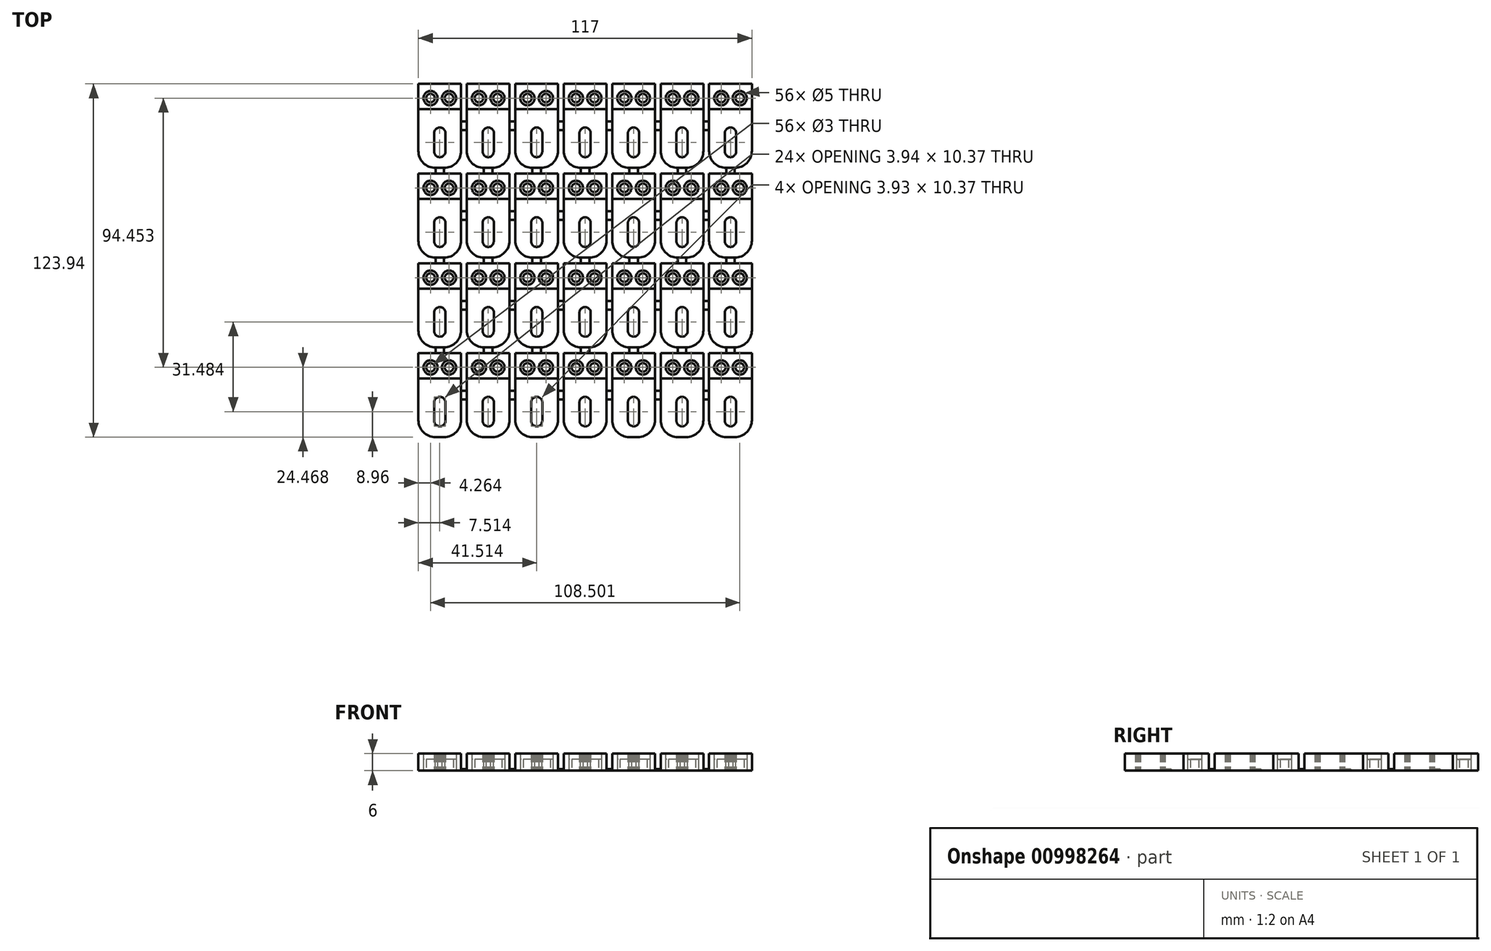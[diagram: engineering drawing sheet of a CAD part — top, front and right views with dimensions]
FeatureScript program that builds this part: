
annotation { "Feature Type Name" : "Feature", "Feature Type Description" : "" }
export const myFeature = defineFeature(function(context is Context, id is Id, definition is map)
    precondition{}
    {
        {
            var Q0;
            Q0=qCreatedBy(makeId("Top.planeOp"),FACE);
            var sketch = newSketch(context, id + "F0", { "sketchPlane" : qUnion([Q0])});
            skLineSegment(sketch, "E0", {"start": v(-52.5, 30.48) * mm, "end": v(-49.5, 30.48) * mm});
            skLineSegment(sketch, "E1", {"start": v(-49.5, 30.48) * mm, "end": v(-49.5, 32.48) * mm});
            skLineSegment(sketch, "E2", {"start": v(-49.5, 32.48) * mm, "end": v(-52.5, 32.48) * mm});
            skLineSegment(sketch, "E3", {"start": v(-52.5, 32.48) * mm, "end": v(-52.5, 30.48) * mm});
            skLineSegment(sketch, "E4", {"start": v(-58.5, 53.13) * mm, "end": v(-43.5, 53.13) * mm});
            skLineSegment(sketch, "E5", {"start": v(-43.5, 53.13) * mm, "end": v(-43.5, 61.97) * mm});
            skLineSegment(sketch, "E6", {"start": v(-43.5, 61.97) * mm, "end": v(-58.5, 61.97) * mm});
            skLineSegment(sketch, "E7", {"start": v(-58.5, 61.97) * mm, "end": v(-58.5, 53.13) * mm});
            skArc(sketch, "E8", {"start": v(-50.24, 56.95) * mm, "mid": v(-49.5, 55.18) * mm, "end": v(-47.74, 54.45) * mm});
            skArc(sketch, "E9", {"start": v(-47.74, 54.45) * mm, "mid": v(-45.97, 55.18) * mm, "end": v(-45.24, 56.95) * mm});
            skArc(sketch, "E10", {"start": v(-45.24, 56.95) * mm, "mid": v(-45.97, 58.72) * mm, "end": v(-47.74, 59.45) * mm});
            skArc(sketch, "E11", {"start": v(-47.74, 59.45) * mm, "mid": v(-49.5, 58.72) * mm, "end": v(-50.24, 56.95) * mm});
            skLineSegment(sketch, "E12", {"start": v(-58.5, 61.97) * mm, "end": v(-58.5, 38.48) * mm});
            skArc(sketch, "E13", {"start": v(-58.5, 38.48) * mm, "mid": v(-56.74, 34.24) * mm, "end": v(-52.5, 32.48) * mm});
            skLineSegment(sketch, "E14", {"start": v(-52.5, 32.48) * mm, "end": v(-49.5, 32.48) * mm});
            skArc(sketch, "E15", {"start": v(-49.5, 32.48) * mm, "mid": v(-45.26, 34.24) * mm, "end": v(-43.5, 38.48) * mm});
            skLineSegment(sketch, "E16", {"start": v(-43.5, 38.48) * mm, "end": v(-43.5, 61.97) * mm});
            skArc(sketch, "E17", {"start": v(-56.74, 56.95) * mm, "mid": v(-56, 55.18) * mm, "end": v(-54.24, 54.45) * mm});
            skArc(sketch, "E18", {"start": v(-54.24, 54.45) * mm, "mid": v(-52.47, 55.18) * mm, "end": v(-51.74, 56.95) * mm});
            skArc(sketch, "E19", {"start": v(-51.74, 56.95) * mm, "mid": v(-52.47, 58.72) * mm, "end": v(-54.24, 59.45) * mm});
            skArc(sketch, "E20", {"start": v(-54.24, 59.45) * mm, "mid": v(-56, 58.72) * mm, "end": v(-56.74, 56.95) * mm});
            skArc(sketch, "E21", {"start": v(-54.24, 58.45) * mm, "mid": v(-55.3, 58.01) * mm, "end": v(-55.74, 56.95) * mm});
            skArc(sketch, "E22", {"start": v(-55.74, 56.95) * mm, "mid": v(-55.3, 55.9) * mm, "end": v(-54.24, 55.45) * mm});
            skArc(sketch, "E23", {"start": v(-54.24, 55.45) * mm, "mid": v(-53.18, 55.9) * mm, "end": v(-52.74, 56.95) * mm});
            skArc(sketch, "E24", {"start": v(-52.74, 56.95) * mm, "mid": v(-53.18, 58.01) * mm, "end": v(-54.24, 58.45) * mm});
            skArc(sketch, "E25", {"start": v(-47.74, 58.45) * mm, "mid": v(-48.8, 58.01) * mm, "end": v(-49.24, 56.95) * mm});
            skArc(sketch, "E26", {"start": v(-49.24, 56.95) * mm, "mid": v(-48.8, 55.9) * mm, "end": v(-47.74, 55.45) * mm});
            skArc(sketch, "E27", {"start": v(-47.74, 55.45) * mm, "mid": v(-46.67, 55.9) * mm, "end": v(-46.24, 56.95) * mm});
            skArc(sketch, "E28", {"start": v(-46.24, 56.95) * mm, "mid": v(-46.67, 58.01) * mm, "end": v(-47.74, 58.45) * mm});
            skLineSegment(sketch, "E29", {"start": v(-51.27, 46.62) * mm, "end": v(-51.4, 46.6) * mm});
            skLineSegment(sketch, "E30", {"start": v(-51.4, 46.6) * mm, "end": v(-51.5, 46.58) * mm});
            skLineSegment(sketch, "E31", {"start": v(-51.5, 46.58) * mm, "end": v(-51.72, 46.5) * mm});
            skLineSegment(sketch, "E32", {"start": v(-51.72, 46.5) * mm, "end": v(-51.94, 46.4) * mm});
            skLineSegment(sketch, "E33", {"start": v(-51.94, 46.4) * mm, "end": v(-52.15, 46.27) * mm});
            skLineSegment(sketch, "E34", {"start": v(-52.15, 46.27) * mm, "end": v(-52.33, 46.12) * mm});
            skLineSegment(sketch, "E35", {"start": v(-52.33, 46.12) * mm, "end": v(-52.53, 45.92) * mm});
            skLineSegment(sketch, "E36", {"start": v(-52.53, 45.92) * mm, "end": v(-52.6, 45.8) * mm});
            skLineSegment(sketch, "E37", {"start": v(-52.6, 45.8) * mm, "end": v(-52.6, 45.8) * mm});
            skLineSegment(sketch, "E38", {"start": v(-52.6, 45.8) * mm, "end": v(-52.66, 45.7) * mm});
            skLineSegment(sketch, "E39", {"start": v(-52.66, 45.7) * mm, "end": v(-52.76, 45.53) * mm});
            skLineSegment(sketch, "E40", {"start": v(-52.76, 45.53) * mm, "end": v(-52.83, 45.34) * mm});
            skLineSegment(sketch, "E41", {"start": v(-52.83, 45.34) * mm, "end": v(-52.91, 45.1) * mm});
            skLineSegment(sketch, "E42", {"start": v(-52.91, 45.1) * mm, "end": v(-52.95, 45) * mm});
            skLineSegment(sketch, "E43", {"start": v(-52.95, 45) * mm, "end": v(-52.95, 37.9) * mm});
            skLineSegment(sketch, "E44", {"start": v(-52.95, 37.9) * mm, "end": v(-52.91, 37.81) * mm});
            skLineSegment(sketch, "E45", {"start": v(-52.91, 37.81) * mm, "end": v(-52.84, 37.58) * mm});
            skLineSegment(sketch, "E46", {"start": v(-52.84, 37.58) * mm, "end": v(-52.79, 37.43) * mm});
            skLineSegment(sketch, "E47", {"start": v(-52.79, 37.43) * mm, "end": v(-52.74, 37.31) * mm});
            skLineSegment(sketch, "E48", {"start": v(-52.74, 37.31) * mm, "end": v(-52.67, 37.2) * mm});
            skLineSegment(sketch, "E49", {"start": v(-52.67, 37.2) * mm, "end": v(-52.6, 37.11) * mm});
            skLineSegment(sketch, "E50", {"start": v(-52.6, 37.11) * mm, "end": v(-52.59, 37.1) * mm});
            skLineSegment(sketch, "E51", {"start": v(-52.59, 37.1) * mm, "end": v(-52.58, 37.07) * mm});
            skLineSegment(sketch, "E52", {"start": v(-52.58, 37.07) * mm, "end": v(-52.52, 36.98) * mm});
            skLineSegment(sketch, "E53", {"start": v(-52.52, 36.98) * mm, "end": v(-52.42, 36.87) * mm});
            skLineSegment(sketch, "E54", {"start": v(-52.42, 36.87) * mm, "end": v(-52.22, 36.68) * mm});
            skLineSegment(sketch, "E55", {"start": v(-52.22, 36.68) * mm, "end": v(-52.13, 36.62) * mm});
            skLineSegment(sketch, "E56", {"start": v(-52.13, 36.62) * mm, "end": v(-52.07, 36.58) * mm});
            skLineSegment(sketch, "E57", {"start": v(-52.07, 36.58) * mm, "end": v(-52.04, 36.56) * mm});
            skLineSegment(sketch, "E58", {"start": v(-52.04, 36.56) * mm, "end": v(-51.95, 36.51) * mm});
            skLineSegment(sketch, "E59", {"start": v(-51.95, 36.51) * mm, "end": v(-51.66, 36.37) * mm});
            skLineSegment(sketch, "E60", {"start": v(-51.66, 36.37) * mm, "end": v(-51.51, 36.32) * mm});
            skLineSegment(sketch, "E61", {"start": v(-51.51, 36.32) * mm, "end": v(-51.35, 36.29) * mm});
            skLineSegment(sketch, "E62", {"start": v(-51.35, 36.29) * mm, "end": v(-51.17, 36.27) * mm});
            skLineSegment(sketch, "E63", {"start": v(-51.17, 36.27) * mm, "end": v(-51, 36.26) * mm});
            skLineSegment(sketch, "E64", {"start": v(-51, 36.26) * mm, "end": v(-50.81, 36.27) * mm});
            skLineSegment(sketch, "E65", {"start": v(-50.81, 36.27) * mm, "end": v(-50.64, 36.29) * mm});
            skLineSegment(sketch, "E66", {"start": v(-50.64, 36.29) * mm, "end": v(-50.47, 36.32) * mm});
            skLineSegment(sketch, "E67", {"start": v(-50.47, 36.32) * mm, "end": v(-50.32, 36.37) * mm});
            skLineSegment(sketch, "E68", {"start": v(-50.32, 36.37) * mm, "end": v(-50.02, 36.5) * mm});
            skLineSegment(sketch, "E69", {"start": v(-50.02, 36.5) * mm, "end": v(-49.92, 36.56) * mm});
            skLineSegment(sketch, "E70", {"start": v(-49.92, 36.56) * mm, "end": v(-49.89, 36.6) * mm});
            skLineSegment(sketch, "E71", {"start": v(-49.89, 36.6) * mm, "end": v(-49.86, 36.6) * mm});
            skLineSegment(sketch, "E72", {"start": v(-49.86, 36.6) * mm, "end": v(-49.78, 36.66) * mm});
            skLineSegment(sketch, "E73", {"start": v(-49.78, 36.66) * mm, "end": v(-49.63, 36.8) * mm});
            skLineSegment(sketch, "E74", {"start": v(-49.63, 36.8) * mm, "end": v(-49.48, 36.94) * mm});
            skLineSegment(sketch, "E75", {"start": v(-49.48, 36.94) * mm, "end": v(-49.42, 37.02) * mm});
            skLineSegment(sketch, "E76", {"start": v(-49.42, 37.02) * mm, "end": v(-49.4, 37.08) * mm});
            skLineSegment(sketch, "E77", {"start": v(-49.4, 37.08) * mm, "end": v(-49.38, 37.1) * mm});
            skLineSegment(sketch, "E78", {"start": v(-49.38, 37.1) * mm, "end": v(-49.38, 37.1) * mm});
            skLineSegment(sketch, "E79", {"start": v(-49.38, 37.1) * mm, "end": v(-49.31, 37.19) * mm});
            skLineSegment(sketch, "E80", {"start": v(-49.31, 37.19) * mm, "end": v(-49.25, 37.27) * mm});
            skLineSegment(sketch, "E81", {"start": v(-49.25, 37.27) * mm, "end": v(-49.2, 37.4) * mm});
            skLineSegment(sketch, "E82", {"start": v(-49.2, 37.4) * mm, "end": v(-49.06, 37.8) * mm});
            skLineSegment(sketch, "E83", {"start": v(-49.06, 37.8) * mm, "end": v(-49.02, 37.94) * mm});
            skLineSegment(sketch, "E84", {"start": v(-49.02, 37.94) * mm, "end": v(-49.02, 45) * mm});
            skLineSegment(sketch, "E85", {"start": v(-49.02, 45) * mm, "end": v(-49.06, 45.1) * mm});
            skLineSegment(sketch, "E86", {"start": v(-49.06, 45.1) * mm, "end": v(-49.14, 45.34) * mm});
            skLineSegment(sketch, "E87", {"start": v(-49.14, 45.34) * mm, "end": v(-49.21, 45.53) * mm});
            skLineSegment(sketch, "E88", {"start": v(-49.21, 45.53) * mm, "end": v(-49.3, 45.7) * mm});
            skLineSegment(sketch, "E89", {"start": v(-49.3, 45.7) * mm, "end": v(-49.37, 45.8) * mm});
            skLineSegment(sketch, "E90", {"start": v(-49.37, 45.8) * mm, "end": v(-49.4, 45.86) * mm});
            skLineSegment(sketch, "E91", {"start": v(-49.4, 45.86) * mm, "end": v(-49.45, 45.92) * mm});
            skLineSegment(sketch, "E92", {"start": v(-49.45, 45.92) * mm, "end": v(-49.54, 46.02) * mm});
            skLineSegment(sketch, "E93", {"start": v(-49.54, 46.02) * mm, "end": v(-49.8, 46.26) * mm});
            skLineSegment(sketch, "E94", {"start": v(-49.8, 46.26) * mm, "end": v(-49.94, 46.35) * mm});
            skLineSegment(sketch, "E95", {"start": v(-49.94, 46.35) * mm, "end": v(-50.11, 46.44) * mm});
            skLineSegment(sketch, "E96", {"start": v(-50.11, 46.44) * mm, "end": v(-50.3, 46.52) * mm});
            skLineSegment(sketch, "E97", {"start": v(-50.3, 46.52) * mm, "end": v(-50.47, 46.58) * mm});
            skLineSegment(sketch, "E98", {"start": v(-50.47, 46.58) * mm, "end": v(-50.58, 46.6) * mm});
            skLineSegment(sketch, "E99", {"start": v(-50.58, 46.6) * mm, "end": v(-50.7, 46.62) * mm});
            skLineSegment(sketch, "E100", {"start": v(-50.7, 46.62) * mm, "end": v(-50.98, 46.63) * mm});
            skLineSegment(sketch, "E101", {"start": v(-50.98, 46.63) * mm, "end": v(-51.27, 46.62) * mm});
            skLineSegment(sketch, "E102", {"start": v(-35.5, 30.48) * mm, "end": v(-32.5, 30.48) * mm});
            skLineSegment(sketch, "E103", {"start": v(-32.5, 30.48) * mm, "end": v(-32.5, 32.48) * mm});
            skLineSegment(sketch, "E104", {"start": v(-32.5, 32.48) * mm, "end": v(-35.5, 32.48) * mm});
            skLineSegment(sketch, "E105", {"start": v(-35.5, 32.48) * mm, "end": v(-35.5, 30.48) * mm});
            skLineSegment(sketch, "E106", {"start": v(-41.5, 53.13) * mm, "end": v(-26.5, 53.13) * mm});
            skLineSegment(sketch, "E107", {"start": v(-26.5, 53.13) * mm, "end": v(-26.5, 61.97) * mm});
            skLineSegment(sketch, "E108", {"start": v(-26.5, 61.97) * mm, "end": v(-41.5, 61.97) * mm});
            skLineSegment(sketch, "E109", {"start": v(-41.5, 61.97) * mm, "end": v(-41.5, 53.13) * mm});
            skArc(sketch, "E110", {"start": v(-33.24, 56.95) * mm, "mid": v(-32.5, 55.18) * mm, "end": v(-30.74, 54.45) * mm});
            skArc(sketch, "E111", {"start": v(-30.74, 54.45) * mm, "mid": v(-28.97, 55.18) * mm, "end": v(-28.24, 56.95) * mm});
            skArc(sketch, "E112", {"start": v(-28.24, 56.95) * mm, "mid": v(-28.97, 58.72) * mm, "end": v(-30.74, 59.45) * mm});
            skArc(sketch, "E113", {"start": v(-30.74, 59.45) * mm, "mid": v(-32.5, 58.72) * mm, "end": v(-33.24, 56.95) * mm});
            skLineSegment(sketch, "E114", {"start": v(-41.5, 61.97) * mm, "end": v(-41.5, 38.48) * mm});
            skArc(sketch, "E115", {"start": v(-41.5, 38.48) * mm, "mid": v(-39.74, 34.24) * mm, "end": v(-35.5, 32.48) * mm});
            skLineSegment(sketch, "E116", {"start": v(-35.5, 32.48) * mm, "end": v(-32.5, 32.48) * mm});
            skArc(sketch, "E117", {"start": v(-32.5, 32.48) * mm, "mid": v(-28.26, 34.24) * mm, "end": v(-26.5, 38.48) * mm});
            skLineSegment(sketch, "E118", {"start": v(-26.5, 38.48) * mm, "end": v(-26.5, 61.97) * mm});
            skArc(sketch, "E119", {"start": v(-39.74, 56.95) * mm, "mid": v(-39, 55.18) * mm, "end": v(-37.24, 54.45) * mm});
            skArc(sketch, "E120", {"start": v(-37.24, 54.45) * mm, "mid": v(-35.47, 55.18) * mm, "end": v(-34.74, 56.95) * mm});
            skArc(sketch, "E121", {"start": v(-34.74, 56.95) * mm, "mid": v(-35.47, 58.72) * mm, "end": v(-37.24, 59.45) * mm});
            skArc(sketch, "E122", {"start": v(-37.24, 59.45) * mm, "mid": v(-39, 58.72) * mm, "end": v(-39.74, 56.95) * mm});
            skArc(sketch, "E123", {"start": v(-37.24, 58.45) * mm, "mid": v(-38.3, 58.01) * mm, "end": v(-38.74, 56.95) * mm});
            skArc(sketch, "E124", {"start": v(-38.74, 56.95) * mm, "mid": v(-38.3, 55.9) * mm, "end": v(-37.24, 55.45) * mm});
            skArc(sketch, "E125", {"start": v(-37.24, 55.45) * mm, "mid": v(-36.18, 55.9) * mm, "end": v(-35.74, 56.95) * mm});
            skArc(sketch, "E126", {"start": v(-35.74, 56.95) * mm, "mid": v(-36.18, 58.01) * mm, "end": v(-37.24, 58.45) * mm});
            skArc(sketch, "E127", {"start": v(-30.74, 58.45) * mm, "mid": v(-31.8, 58.01) * mm, "end": v(-32.24, 56.95) * mm});
            skArc(sketch, "E128", {"start": v(-32.24, 56.95) * mm, "mid": v(-31.8, 55.9) * mm, "end": v(-30.74, 55.45) * mm});
            skArc(sketch, "E129", {"start": v(-30.74, 55.45) * mm, "mid": v(-29.67, 55.9) * mm, "end": v(-29.24, 56.95) * mm});
            skArc(sketch, "E130", {"start": v(-29.24, 56.95) * mm, "mid": v(-29.67, 58.01) * mm, "end": v(-30.74, 58.45) * mm});
            skLineSegment(sketch, "E131", {"start": v(-34.27, 46.62) * mm, "end": v(-34.4, 46.6) * mm});
            skLineSegment(sketch, "E132", {"start": v(-34.4, 46.6) * mm, "end": v(-34.5, 46.58) * mm});
            skLineSegment(sketch, "E133", {"start": v(-34.5, 46.58) * mm, "end": v(-34.72, 46.5) * mm});
            skLineSegment(sketch, "E134", {"start": v(-34.72, 46.5) * mm, "end": v(-34.94, 46.4) * mm});
            skLineSegment(sketch, "E135", {"start": v(-34.94, 46.4) * mm, "end": v(-35.15, 46.27) * mm});
            skLineSegment(sketch, "E136", {"start": v(-35.15, 46.27) * mm, "end": v(-35.33, 46.12) * mm});
            skLineSegment(sketch, "E137", {"start": v(-35.33, 46.12) * mm, "end": v(-35.53, 45.92) * mm});
            skLineSegment(sketch, "E138", {"start": v(-35.53, 45.92) * mm, "end": v(-35.6, 45.8) * mm});
            skLineSegment(sketch, "E139", {"start": v(-35.6, 45.8) * mm, "end": v(-35.6, 45.8) * mm});
            skLineSegment(sketch, "E140", {"start": v(-35.6, 45.8) * mm, "end": v(-35.66, 45.7) * mm});
            skLineSegment(sketch, "E141", {"start": v(-35.66, 45.7) * mm, "end": v(-35.76, 45.53) * mm});
            skLineSegment(sketch, "E142", {"start": v(-35.76, 45.53) * mm, "end": v(-35.83, 45.34) * mm});
            skLineSegment(sketch, "E143", {"start": v(-35.83, 45.34) * mm, "end": v(-35.91, 45.1) * mm});
            skLineSegment(sketch, "E144", {"start": v(-35.91, 45.1) * mm, "end": v(-35.95, 45) * mm});
            skLineSegment(sketch, "E145", {"start": v(-35.95, 45) * mm, "end": v(-35.95, 37.9) * mm});
            skLineSegment(sketch, "E146", {"start": v(-35.95, 37.9) * mm, "end": v(-35.91, 37.81) * mm});
            skLineSegment(sketch, "E147", {"start": v(-35.91, 37.81) * mm, "end": v(-35.84, 37.58) * mm});
            skLineSegment(sketch, "E148", {"start": v(-35.84, 37.58) * mm, "end": v(-35.79, 37.43) * mm});
            skLineSegment(sketch, "E149", {"start": v(-35.79, 37.43) * mm, "end": v(-35.74, 37.31) * mm});
            skLineSegment(sketch, "E150", {"start": v(-35.74, 37.31) * mm, "end": v(-35.67, 37.2) * mm});
            skLineSegment(sketch, "E151", {"start": v(-35.67, 37.2) * mm, "end": v(-35.6, 37.11) * mm});
            skLineSegment(sketch, "E152", {"start": v(-35.6, 37.11) * mm, "end": v(-35.59, 37.1) * mm});
            skLineSegment(sketch, "E153", {"start": v(-35.59, 37.1) * mm, "end": v(-35.58, 37.07) * mm});
            skLineSegment(sketch, "E154", {"start": v(-35.58, 37.07) * mm, "end": v(-35.52, 36.98) * mm});
            skLineSegment(sketch, "E155", {"start": v(-35.52, 36.98) * mm, "end": v(-35.42, 36.87) * mm});
            skLineSegment(sketch, "E156", {"start": v(-35.42, 36.87) * mm, "end": v(-35.22, 36.68) * mm});
            skLineSegment(sketch, "E157", {"start": v(-35.22, 36.68) * mm, "end": v(-35.13, 36.62) * mm});
            skLineSegment(sketch, "E158", {"start": v(-35.13, 36.62) * mm, "end": v(-35.07, 36.58) * mm});
            skLineSegment(sketch, "E159", {"start": v(-35.07, 36.58) * mm, "end": v(-35.04, 36.56) * mm});
            skLineSegment(sketch, "E160", {"start": v(-35.04, 36.56) * mm, "end": v(-34.95, 36.51) * mm});
            skLineSegment(sketch, "E161", {"start": v(-34.95, 36.51) * mm, "end": v(-34.66, 36.37) * mm});
            skLineSegment(sketch, "E162", {"start": v(-34.66, 36.37) * mm, "end": v(-34.51, 36.32) * mm});
            skLineSegment(sketch, "E163", {"start": v(-34.51, 36.32) * mm, "end": v(-34.35, 36.29) * mm});
            skLineSegment(sketch, "E164", {"start": v(-34.35, 36.29) * mm, "end": v(-34.17, 36.27) * mm});
            skLineSegment(sketch, "E165", {"start": v(-34.17, 36.27) * mm, "end": v(-34, 36.26) * mm});
            skLineSegment(sketch, "E166", {"start": v(-34, 36.26) * mm, "end": v(-33.81, 36.27) * mm});
            skLineSegment(sketch, "E167", {"start": v(-33.81, 36.27) * mm, "end": v(-33.64, 36.29) * mm});
            skLineSegment(sketch, "E168", {"start": v(-33.64, 36.29) * mm, "end": v(-33.47, 36.32) * mm});
            skLineSegment(sketch, "E169", {"start": v(-33.47, 36.32) * mm, "end": v(-33.32, 36.37) * mm});
            skLineSegment(sketch, "E170", {"start": v(-33.32, 36.37) * mm, "end": v(-33.02, 36.5) * mm});
            skLineSegment(sketch, "E171", {"start": v(-33.02, 36.5) * mm, "end": v(-32.92, 36.56) * mm});
            skLineSegment(sketch, "E172", {"start": v(-32.92, 36.56) * mm, "end": v(-32.89, 36.6) * mm});
            skLineSegment(sketch, "E173", {"start": v(-32.89, 36.6) * mm, "end": v(-32.86, 36.6) * mm});
            skLineSegment(sketch, "E174", {"start": v(-32.86, 36.6) * mm, "end": v(-32.78, 36.66) * mm});
            skLineSegment(sketch, "E175", {"start": v(-32.78, 36.66) * mm, "end": v(-32.63, 36.8) * mm});
            skLineSegment(sketch, "E176", {"start": v(-32.63, 36.8) * mm, "end": v(-32.48, 36.94) * mm});
            skLineSegment(sketch, "E177", {"start": v(-32.48, 36.94) * mm, "end": v(-32.42, 37.02) * mm});
            skLineSegment(sketch, "E178", {"start": v(-32.42, 37.02) * mm, "end": v(-32.4, 37.08) * mm});
            skLineSegment(sketch, "E179", {"start": v(-32.4, 37.08) * mm, "end": v(-32.38, 37.1) * mm});
            skLineSegment(sketch, "E180", {"start": v(-32.38, 37.1) * mm, "end": v(-32.38, 37.1) * mm});
            skLineSegment(sketch, "E181", {"start": v(-32.38, 37.1) * mm, "end": v(-32.31, 37.19) * mm});
            skLineSegment(sketch, "E182", {"start": v(-32.31, 37.19) * mm, "end": v(-32.25, 37.27) * mm});
            skLineSegment(sketch, "E183", {"start": v(-32.25, 37.27) * mm, "end": v(-32.2, 37.4) * mm});
            skLineSegment(sketch, "E184", {"start": v(-32.2, 37.4) * mm, "end": v(-32.06, 37.8) * mm});
            skLineSegment(sketch, "E185", {"start": v(-32.06, 37.8) * mm, "end": v(-32.02, 37.94) * mm});
            skLineSegment(sketch, "E186", {"start": v(-32.02, 37.94) * mm, "end": v(-32.02, 45) * mm});
            skLineSegment(sketch, "E187", {"start": v(-32.02, 45) * mm, "end": v(-32.06, 45.1) * mm});
            skLineSegment(sketch, "E188", {"start": v(-32.06, 45.1) * mm, "end": v(-32.14, 45.34) * mm});
            skLineSegment(sketch, "E189", {"start": v(-32.14, 45.34) * mm, "end": v(-32.21, 45.53) * mm});
            skLineSegment(sketch, "E190", {"start": v(-32.21, 45.53) * mm, "end": v(-32.3, 45.7) * mm});
            skLineSegment(sketch, "E191", {"start": v(-32.3, 45.7) * mm, "end": v(-32.37, 45.8) * mm});
            skLineSegment(sketch, "E192", {"start": v(-32.37, 45.8) * mm, "end": v(-32.4, 45.86) * mm});
            skLineSegment(sketch, "E193", {"start": v(-32.4, 45.86) * mm, "end": v(-32.45, 45.92) * mm});
            skLineSegment(sketch, "E194", {"start": v(-32.45, 45.92) * mm, "end": v(-32.54, 46.02) * mm});
            skLineSegment(sketch, "E195", {"start": v(-32.54, 46.02) * mm, "end": v(-32.8, 46.26) * mm});
            skLineSegment(sketch, "E196", {"start": v(-32.8, 46.26) * mm, "end": v(-32.94, 46.35) * mm});
            skLineSegment(sketch, "E197", {"start": v(-32.94, 46.35) * mm, "end": v(-33.11, 46.44) * mm});
            skLineSegment(sketch, "E198", {"start": v(-33.11, 46.44) * mm, "end": v(-33.3, 46.52) * mm});
            skLineSegment(sketch, "E199", {"start": v(-33.3, 46.52) * mm, "end": v(-33.47, 46.58) * mm});
            skLineSegment(sketch, "E200", {"start": v(-33.47, 46.58) * mm, "end": v(-33.58, 46.6) * mm});
            skLineSegment(sketch, "E201", {"start": v(-33.58, 46.6) * mm, "end": v(-33.7, 46.62) * mm});
            skLineSegment(sketch, "E202", {"start": v(-33.7, 46.62) * mm, "end": v(-33.98, 46.63) * mm});
            skLineSegment(sketch, "E203", {"start": v(-33.98, 46.63) * mm, "end": v(-34.27, 46.62) * mm});
            skLineSegment(sketch, "E204", {"start": v(-43.5, 45.73) * mm, "end": v(-41.5, 45.73) * mm});
            skLineSegment(sketch, "E205", {"start": v(-41.5, 45.73) * mm, "end": v(-41.5, 48.73) * mm});
            skLineSegment(sketch, "E206", {"start": v(-41.5, 48.73) * mm, "end": v(-43.5, 48.73) * mm});
            skLineSegment(sketch, "E207", {"start": v(-43.5, 48.73) * mm, "end": v(-43.5, 45.73) * mm});
            skLineSegment(sketch, "E208", {"start": v(-18.5, 30.48) * mm, "end": v(-15.5, 30.48) * mm});
            skLineSegment(sketch, "E209", {"start": v(-15.5, 30.48) * mm, "end": v(-15.5, 32.48) * mm});
            skLineSegment(sketch, "E210", {"start": v(-15.5, 32.48) * mm, "end": v(-18.5, 32.48) * mm});
            skLineSegment(sketch, "E211", {"start": v(-18.5, 32.48) * mm, "end": v(-18.5, 30.48) * mm});
            skLineSegment(sketch, "E212", {"start": v(-24.5, 53.13) * mm, "end": v(-9.5, 53.13) * mm});
            skLineSegment(sketch, "E213", {"start": v(-9.5, 53.13) * mm, "end": v(-9.5, 61.97) * mm});
            skLineSegment(sketch, "E214", {"start": v(-9.5, 61.97) * mm, "end": v(-24.5, 61.97) * mm});
            skLineSegment(sketch, "E215", {"start": v(-24.5, 61.97) * mm, "end": v(-24.5, 53.13) * mm});
            skArc(sketch, "E216", {"start": v(-16.24, 56.95) * mm, "mid": v(-15.5, 55.18) * mm, "end": v(-13.74, 54.45) * mm});
            skArc(sketch, "E217", {"start": v(-13.74, 54.45) * mm, "mid": v(-11.97, 55.18) * mm, "end": v(-11.24, 56.95) * mm});
            skArc(sketch, "E218", {"start": v(-11.24, 56.95) * mm, "mid": v(-11.97, 58.72) * mm, "end": v(-13.74, 59.45) * mm});
            skArc(sketch, "E219", {"start": v(-13.74, 59.45) * mm, "mid": v(-15.5, 58.72) * mm, "end": v(-16.24, 56.95) * mm});
            skLineSegment(sketch, "E220", {"start": v(-24.5, 61.97) * mm, "end": v(-24.5, 38.48) * mm});
            skArc(sketch, "E221", {"start": v(-24.5, 38.48) * mm, "mid": v(-22.74, 34.24) * mm, "end": v(-18.5, 32.48) * mm});
            skLineSegment(sketch, "E222", {"start": v(-18.5, 32.48) * mm, "end": v(-15.5, 32.48) * mm});
            skArc(sketch, "E223", {"start": v(-15.5, 32.48) * mm, "mid": v(-11.26, 34.24) * mm, "end": v(-9.5, 38.48) * mm});
            skLineSegment(sketch, "E224", {"start": v(-9.5, 38.48) * mm, "end": v(-9.5, 61.97) * mm});
            skArc(sketch, "E225", {"start": v(-22.74, 56.95) * mm, "mid": v(-22, 55.18) * mm, "end": v(-20.24, 54.45) * mm});
            skArc(sketch, "E226", {"start": v(-20.24, 54.45) * mm, "mid": v(-18.47, 55.18) * mm, "end": v(-17.74, 56.95) * mm});
            skArc(sketch, "E227", {"start": v(-17.74, 56.95) * mm, "mid": v(-18.47, 58.72) * mm, "end": v(-20.24, 59.45) * mm});
            skArc(sketch, "E228", {"start": v(-20.24, 59.45) * mm, "mid": v(-22, 58.72) * mm, "end": v(-22.74, 56.95) * mm});
            skArc(sketch, "E229", {"start": v(-20.24, 58.45) * mm, "mid": v(-21.3, 58.01) * mm, "end": v(-21.74, 56.95) * mm});
            skArc(sketch, "E230", {"start": v(-21.74, 56.95) * mm, "mid": v(-21.3, 55.9) * mm, "end": v(-20.24, 55.45) * mm});
            skArc(sketch, "E231", {"start": v(-20.24, 55.45) * mm, "mid": v(-19.18, 55.9) * mm, "end": v(-18.74, 56.95) * mm});
            skArc(sketch, "E232", {"start": v(-18.74, 56.95) * mm, "mid": v(-19.18, 58.01) * mm, "end": v(-20.24, 58.45) * mm});
            skArc(sketch, "E233", {"start": v(-13.74, 58.45) * mm, "mid": v(-14.8, 58.01) * mm, "end": v(-15.24, 56.95) * mm});
            skArc(sketch, "E234", {"start": v(-15.24, 56.95) * mm, "mid": v(-14.8, 55.9) * mm, "end": v(-13.74, 55.45) * mm});
            skArc(sketch, "E235", {"start": v(-13.74, 55.45) * mm, "mid": v(-12.67, 55.9) * mm, "end": v(-12.24, 56.95) * mm});
            skArc(sketch, "E236", {"start": v(-12.24, 56.95) * mm, "mid": v(-12.67, 58.01) * mm, "end": v(-13.74, 58.45) * mm});
            skLineSegment(sketch, "E237", {"start": v(-17.27, 46.62) * mm, "end": v(-17.4, 46.6) * mm});
            skLineSegment(sketch, "E238", {"start": v(-17.4, 46.6) * mm, "end": v(-17.5, 46.58) * mm});
            skLineSegment(sketch, "E239", {"start": v(-17.5, 46.58) * mm, "end": v(-17.72, 46.5) * mm});
            skLineSegment(sketch, "E240", {"start": v(-17.72, 46.5) * mm, "end": v(-17.94, 46.4) * mm});
            skLineSegment(sketch, "E241", {"start": v(-17.94, 46.4) * mm, "end": v(-18.15, 46.27) * mm});
            skLineSegment(sketch, "E242", {"start": v(-18.15, 46.27) * mm, "end": v(-18.33, 46.12) * mm});
            skLineSegment(sketch, "E243", {"start": v(-18.33, 46.12) * mm, "end": v(-18.53, 45.92) * mm});
            skLineSegment(sketch, "E244", {"start": v(-18.53, 45.92) * mm, "end": v(-18.6, 45.8) * mm});
            skLineSegment(sketch, "E245", {"start": v(-18.6, 45.8) * mm, "end": v(-18.6, 45.8) * mm});
            skLineSegment(sketch, "E246", {"start": v(-18.6, 45.8) * mm, "end": v(-18.66, 45.7) * mm});
            skLineSegment(sketch, "E247", {"start": v(-18.66, 45.7) * mm, "end": v(-18.76, 45.53) * mm});
            skLineSegment(sketch, "E248", {"start": v(-18.76, 45.53) * mm, "end": v(-18.83, 45.34) * mm});
            skLineSegment(sketch, "E249", {"start": v(-18.83, 45.34) * mm, "end": v(-18.91, 45.1) * mm});
            skLineSegment(sketch, "E250", {"start": v(-18.91, 45.1) * mm, "end": v(-18.95, 45) * mm});
            skLineSegment(sketch, "E251", {"start": v(-18.95, 45) * mm, "end": v(-18.95, 37.9) * mm});
            skLineSegment(sketch, "E252", {"start": v(-18.95, 37.9) * mm, "end": v(-18.91, 37.81) * mm});
            skLineSegment(sketch, "E253", {"start": v(-18.91, 37.81) * mm, "end": v(-18.84, 37.58) * mm});
            skLineSegment(sketch, "E254", {"start": v(-18.84, 37.58) * mm, "end": v(-18.79, 37.43) * mm});
            skLineSegment(sketch, "E255", {"start": v(-18.79, 37.43) * mm, "end": v(-18.74, 37.31) * mm});
            skLineSegment(sketch, "E256", {"start": v(-18.74, 37.31) * mm, "end": v(-18.67, 37.2) * mm});
            skLineSegment(sketch, "E257", {"start": v(-18.67, 37.2) * mm, "end": v(-18.6, 37.11) * mm});
            skLineSegment(sketch, "E258", {"start": v(-18.6, 37.11) * mm, "end": v(-18.59, 37.1) * mm});
            skLineSegment(sketch, "E259", {"start": v(-18.59, 37.1) * mm, "end": v(-18.58, 37.07) * mm});
            skLineSegment(sketch, "E260", {"start": v(-18.58, 37.07) * mm, "end": v(-18.52, 36.98) * mm});
            skLineSegment(sketch, "E261", {"start": v(-18.52, 36.98) * mm, "end": v(-18.42, 36.87) * mm});
            skLineSegment(sketch, "E262", {"start": v(-18.42, 36.87) * mm, "end": v(-18.22, 36.68) * mm});
            skLineSegment(sketch, "E263", {"start": v(-18.22, 36.68) * mm, "end": v(-18.13, 36.62) * mm});
            skLineSegment(sketch, "E264", {"start": v(-18.13, 36.62) * mm, "end": v(-18.07, 36.58) * mm});
            skLineSegment(sketch, "E265", {"start": v(-18.07, 36.58) * mm, "end": v(-18.04, 36.56) * mm});
            skLineSegment(sketch, "E266", {"start": v(-18.04, 36.56) * mm, "end": v(-17.95, 36.51) * mm});
            skLineSegment(sketch, "E267", {"start": v(-17.95, 36.51) * mm, "end": v(-17.66, 36.37) * mm});
            skLineSegment(sketch, "E268", {"start": v(-17.66, 36.37) * mm, "end": v(-17.51, 36.32) * mm});
            skLineSegment(sketch, "E269", {"start": v(-17.51, 36.32) * mm, "end": v(-17.35, 36.29) * mm});
            skLineSegment(sketch, "E270", {"start": v(-17.35, 36.29) * mm, "end": v(-17.17, 36.27) * mm});
            skLineSegment(sketch, "E271", {"start": v(-17.17, 36.27) * mm, "end": v(-17, 36.26) * mm});
            skLineSegment(sketch, "E272", {"start": v(-17, 36.26) * mm, "end": v(-16.81, 36.27) * mm});
            skLineSegment(sketch, "E273", {"start": v(-16.81, 36.27) * mm, "end": v(-16.64, 36.29) * mm});
            skLineSegment(sketch, "E274", {"start": v(-16.64, 36.29) * mm, "end": v(-16.47, 36.32) * mm});
            skLineSegment(sketch, "E275", {"start": v(-16.47, 36.32) * mm, "end": v(-16.32, 36.37) * mm});
            skLineSegment(sketch, "E276", {"start": v(-16.32, 36.37) * mm, "end": v(-16.02, 36.5) * mm});
            skLineSegment(sketch, "E277", {"start": v(-16.02, 36.5) * mm, "end": v(-15.92, 36.56) * mm});
            skLineSegment(sketch, "E278", {"start": v(-15.92, 36.56) * mm, "end": v(-15.89, 36.6) * mm});
            skLineSegment(sketch, "E279", {"start": v(-15.89, 36.6) * mm, "end": v(-15.86, 36.6) * mm});
            skLineSegment(sketch, "E280", {"start": v(-15.86, 36.6) * mm, "end": v(-15.78, 36.66) * mm});
            skLineSegment(sketch, "E281", {"start": v(-15.78, 36.66) * mm, "end": v(-15.63, 36.8) * mm});
            skLineSegment(sketch, "E282", {"start": v(-15.63, 36.8) * mm, "end": v(-15.48, 36.94) * mm});
            skLineSegment(sketch, "E283", {"start": v(-15.48, 36.94) * mm, "end": v(-15.42, 37.02) * mm});
            skLineSegment(sketch, "E284", {"start": v(-15.42, 37.02) * mm, "end": v(-15.4, 37.08) * mm});
            skLineSegment(sketch, "E285", {"start": v(-15.4, 37.08) * mm, "end": v(-15.38, 37.1) * mm});
            skLineSegment(sketch, "E286", {"start": v(-15.38, 37.1) * mm, "end": v(-15.38, 37.1) * mm});
            skLineSegment(sketch, "E287", {"start": v(-15.38, 37.1) * mm, "end": v(-15.31, 37.19) * mm});
            skLineSegment(sketch, "E288", {"start": v(-15.31, 37.19) * mm, "end": v(-15.25, 37.27) * mm});
            skLineSegment(sketch, "E289", {"start": v(-15.25, 37.27) * mm, "end": v(-15.2, 37.4) * mm});
            skLineSegment(sketch, "E290", {"start": v(-15.2, 37.4) * mm, "end": v(-15.06, 37.8) * mm});
            skLineSegment(sketch, "E291", {"start": v(-15.06, 37.8) * mm, "end": v(-15.02, 37.94) * mm});
            skLineSegment(sketch, "E292", {"start": v(-15.02, 37.94) * mm, "end": v(-15.02, 45) * mm});
            skLineSegment(sketch, "E293", {"start": v(-15.02, 45) * mm, "end": v(-15.06, 45.1) * mm});
            skLineSegment(sketch, "E294", {"start": v(-15.06, 45.1) * mm, "end": v(-15.14, 45.34) * mm});
            skLineSegment(sketch, "E295", {"start": v(-15.14, 45.34) * mm, "end": v(-15.21, 45.53) * mm});
            skLineSegment(sketch, "E296", {"start": v(-15.21, 45.53) * mm, "end": v(-15.3, 45.7) * mm});
            skLineSegment(sketch, "E297", {"start": v(-15.3, 45.7) * mm, "end": v(-15.37, 45.8) * mm});
            skLineSegment(sketch, "E298", {"start": v(-15.37, 45.8) * mm, "end": v(-15.4, 45.86) * mm});
            skLineSegment(sketch, "E299", {"start": v(-15.4, 45.86) * mm, "end": v(-15.45, 45.92) * mm});
            skLineSegment(sketch, "E300", {"start": v(-15.45, 45.92) * mm, "end": v(-15.54, 46.02) * mm});
            skLineSegment(sketch, "E301", {"start": v(-15.54, 46.02) * mm, "end": v(-15.8, 46.26) * mm});
            skLineSegment(sketch, "E302", {"start": v(-15.8, 46.26) * mm, "end": v(-15.94, 46.35) * mm});
            skLineSegment(sketch, "E303", {"start": v(-15.94, 46.35) * mm, "end": v(-16.11, 46.44) * mm});
            skLineSegment(sketch, "E304", {"start": v(-16.11, 46.44) * mm, "end": v(-16.3, 46.52) * mm});
            skLineSegment(sketch, "E305", {"start": v(-16.3, 46.52) * mm, "end": v(-16.47, 46.58) * mm});
            skLineSegment(sketch, "E306", {"start": v(-16.47, 46.58) * mm, "end": v(-16.58, 46.6) * mm});
            skLineSegment(sketch, "E307", {"start": v(-16.58, 46.6) * mm, "end": v(-16.7, 46.62) * mm});
            skLineSegment(sketch, "E308", {"start": v(-16.7, 46.62) * mm, "end": v(-16.98, 46.63) * mm});
            skLineSegment(sketch, "E309", {"start": v(-16.98, 46.63) * mm, "end": v(-17.27, 46.62) * mm});
            skLineSegment(sketch, "E310", {"start": v(-26.5, 45.73) * mm, "end": v(-24.5, 45.73) * mm});
            skLineSegment(sketch, "E311", {"start": v(-24.5, 45.73) * mm, "end": v(-24.5, 48.73) * mm});
            skLineSegment(sketch, "E312", {"start": v(-24.5, 48.73) * mm, "end": v(-26.5, 48.73) * mm});
            skLineSegment(sketch, "E313", {"start": v(-26.5, 48.73) * mm, "end": v(-26.5, 45.73) * mm});
            skLineSegment(sketch, "E314", {"start": v(15.5, 30.48) * mm, "end": v(18.5, 30.48) * mm});
            skLineSegment(sketch, "E315", {"start": v(18.5, 30.48) * mm, "end": v(18.5, 32.48) * mm});
            skLineSegment(sketch, "E316", {"start": v(18.5, 32.48) * mm, "end": v(15.5, 32.48) * mm});
            skLineSegment(sketch, "E317", {"start": v(15.5, 32.48) * mm, "end": v(15.5, 30.48) * mm});
            skLineSegment(sketch, "E318", {"start": v(9.5, 53.13) * mm, "end": v(24.5, 53.13) * mm});
            skLineSegment(sketch, "E319", {"start": v(24.5, 53.13) * mm, "end": v(24.5, 61.97) * mm});
            skLineSegment(sketch, "E320", {"start": v(24.5, 61.97) * mm, "end": v(9.5, 61.97) * mm});
            skLineSegment(sketch, "E321", {"start": v(9.5, 61.97) * mm, "end": v(9.5, 53.13) * mm});
            skArc(sketch, "E322", {"start": v(17.76, 56.95) * mm, "mid": v(18.5, 55.18) * mm, "end": v(20.26, 54.45) * mm});
            skArc(sketch, "E323", {"start": v(20.26, 54.45) * mm, "mid": v(22.03, 55.18) * mm, "end": v(22.76, 56.95) * mm});
            skArc(sketch, "E324", {"start": v(22.76, 56.95) * mm, "mid": v(22.03, 58.72) * mm, "end": v(20.26, 59.45) * mm});
            skArc(sketch, "E325", {"start": v(20.26, 59.45) * mm, "mid": v(18.5, 58.72) * mm, "end": v(17.76, 56.95) * mm});
            skLineSegment(sketch, "E326", {"start": v(9.5, 61.97) * mm, "end": v(9.5, 38.48) * mm});
            skArc(sketch, "E327", {"start": v(9.5, 38.48) * mm, "mid": v(11.26, 34.24) * mm, "end": v(15.5, 32.48) * mm});
            skLineSegment(sketch, "E328", {"start": v(15.5, 32.48) * mm, "end": v(18.5, 32.48) * mm});
            skArc(sketch, "E329", {"start": v(18.5, 32.48) * mm, "mid": v(22.74, 34.24) * mm, "end": v(24.5, 38.48) * mm});
            skLineSegment(sketch, "E330", {"start": v(24.5, 38.48) * mm, "end": v(24.5, 61.97) * mm});
            skArc(sketch, "E331", {"start": v(11.26, 56.95) * mm, "mid": v(12, 55.18) * mm, "end": v(13.76, 54.45) * mm});
            skArc(sketch, "E332", {"start": v(13.76, 54.45) * mm, "mid": v(15.53, 55.18) * mm, "end": v(16.26, 56.95) * mm});
            skArc(sketch, "E333", {"start": v(16.26, 56.95) * mm, "mid": v(15.53, 58.72) * mm, "end": v(13.76, 59.45) * mm});
            skArc(sketch, "E334", {"start": v(13.76, 59.45) * mm, "mid": v(12, 58.72) * mm, "end": v(11.26, 56.95) * mm});
            skArc(sketch, "E335", {"start": v(13.76, 58.45) * mm, "mid": v(12.7, 58.01) * mm, "end": v(12.26, 56.95) * mm});
            skArc(sketch, "E336", {"start": v(12.26, 56.95) * mm, "mid": v(12.7, 55.9) * mm, "end": v(13.76, 55.45) * mm});
            skArc(sketch, "E337", {"start": v(13.76, 55.45) * mm, "mid": v(14.82, 55.9) * mm, "end": v(15.26, 56.95) * mm});
            skArc(sketch, "E338", {"start": v(15.26, 56.95) * mm, "mid": v(14.82, 58.01) * mm, "end": v(13.76, 58.45) * mm});
            skArc(sketch, "E339", {"start": v(20.27, 58.45) * mm, "mid": v(19.2, 58.01) * mm, "end": v(18.77, 56.95) * mm});
            skArc(sketch, "E340", {"start": v(18.77, 56.95) * mm, "mid": v(19.2, 55.9) * mm, "end": v(20.27, 55.45) * mm});
            skArc(sketch, "E341", {"start": v(20.27, 55.45) * mm, "mid": v(21.33, 55.9) * mm, "end": v(21.77, 56.95) * mm});
            skArc(sketch, "E342", {"start": v(21.77, 56.95) * mm, "mid": v(21.33, 58.01) * mm, "end": v(20.27, 58.45) * mm});
            skLineSegment(sketch, "E343", {"start": v(16.73, 46.62) * mm, "end": v(16.6, 46.6) * mm});
            skLineSegment(sketch, "E344", {"start": v(16.6, 46.6) * mm, "end": v(16.5, 46.58) * mm});
            skLineSegment(sketch, "E345", {"start": v(16.5, 46.58) * mm, "end": v(16.28, 46.5) * mm});
            skLineSegment(sketch, "E346", {"start": v(16.28, 46.5) * mm, "end": v(16.06, 46.4) * mm});
            skLineSegment(sketch, "E347", {"start": v(16.06, 46.4) * mm, "end": v(15.85, 46.27) * mm});
            skLineSegment(sketch, "E348", {"start": v(15.85, 46.27) * mm, "end": v(15.67, 46.12) * mm});
            skLineSegment(sketch, "E349", {"start": v(15.67, 46.12) * mm, "end": v(15.47, 45.92) * mm});
            skLineSegment(sketch, "E350", {"start": v(15.47, 45.92) * mm, "end": v(15.4, 45.8) * mm});
            skLineSegment(sketch, "E351", {"start": v(15.4, 45.8) * mm, "end": v(15.4, 45.8) * mm});
            skLineSegment(sketch, "E352", {"start": v(15.4, 45.8) * mm, "end": v(15.34, 45.7) * mm});
            skLineSegment(sketch, "E353", {"start": v(15.34, 45.7) * mm, "end": v(15.24, 45.53) * mm});
            skLineSegment(sketch, "E354", {"start": v(15.24, 45.53) * mm, "end": v(15.17, 45.34) * mm});
            skLineSegment(sketch, "E355", {"start": v(15.17, 45.34) * mm, "end": v(15.09, 45.1) * mm});
            skLineSegment(sketch, "E356", {"start": v(15.09, 45.1) * mm, "end": v(15.05, 45) * mm});
            skLineSegment(sketch, "E357", {"start": v(15.05, 45) * mm, "end": v(15.05, 37.9) * mm});
            skLineSegment(sketch, "E358", {"start": v(15.05, 37.9) * mm, "end": v(15.09, 37.81) * mm});
            skLineSegment(sketch, "E359", {"start": v(15.09, 37.81) * mm, "end": v(15.16, 37.58) * mm});
            skLineSegment(sketch, "E360", {"start": v(15.16, 37.58) * mm, "end": v(15.21, 37.43) * mm});
            skLineSegment(sketch, "E361", {"start": v(15.21, 37.43) * mm, "end": v(15.26, 37.31) * mm});
            skLineSegment(sketch, "E362", {"start": v(15.26, 37.31) * mm, "end": v(15.33, 37.2) * mm});
            skLineSegment(sketch, "E363", {"start": v(15.33, 37.2) * mm, "end": v(15.4, 37.11) * mm});
            skLineSegment(sketch, "E364", {"start": v(15.4, 37.11) * mm, "end": v(15.41, 37.1) * mm});
            skLineSegment(sketch, "E365", {"start": v(15.41, 37.1) * mm, "end": v(15.42, 37.07) * mm});
            skLineSegment(sketch, "E366", {"start": v(15.42, 37.07) * mm, "end": v(15.48, 36.98) * mm});
            skLineSegment(sketch, "E367", {"start": v(15.48, 36.98) * mm, "end": v(15.58, 36.87) * mm});
            skLineSegment(sketch, "E368", {"start": v(15.58, 36.87) * mm, "end": v(15.78, 36.68) * mm});
            skLineSegment(sketch, "E369", {"start": v(15.78, 36.68) * mm, "end": v(15.87, 36.62) * mm});
            skLineSegment(sketch, "E370", {"start": v(15.87, 36.62) * mm, "end": v(15.93, 36.58) * mm});
            skLineSegment(sketch, "E371", {"start": v(15.93, 36.58) * mm, "end": v(15.96, 36.56) * mm});
            skLineSegment(sketch, "E372", {"start": v(15.96, 36.56) * mm, "end": v(16.05, 36.51) * mm});
            skLineSegment(sketch, "E373", {"start": v(16.05, 36.51) * mm, "end": v(16.34, 36.37) * mm});
            skLineSegment(sketch, "E374", {"start": v(16.34, 36.37) * mm, "end": v(16.49, 36.32) * mm});
            skLineSegment(sketch, "E375", {"start": v(16.49, 36.32) * mm, "end": v(16.65, 36.29) * mm});
            skLineSegment(sketch, "E376", {"start": v(16.65, 36.29) * mm, "end": v(16.83, 36.27) * mm});
            skLineSegment(sketch, "E377", {"start": v(16.83, 36.27) * mm, "end": v(17, 36.26) * mm});
            skLineSegment(sketch, "E378", {"start": v(17, 36.26) * mm, "end": v(17.19, 36.27) * mm});
            skLineSegment(sketch, "E379", {"start": v(17.19, 36.27) * mm, "end": v(17.36, 36.29) * mm});
            skLineSegment(sketch, "E380", {"start": v(17.36, 36.29) * mm, "end": v(17.53, 36.32) * mm});
            skLineSegment(sketch, "E381", {"start": v(17.53, 36.32) * mm, "end": v(17.68, 36.37) * mm});
            skLineSegment(sketch, "E382", {"start": v(17.68, 36.37) * mm, "end": v(17.98, 36.5) * mm});
            skLineSegment(sketch, "E383", {"start": v(17.98, 36.5) * mm, "end": v(18.08, 36.56) * mm});
            skLineSegment(sketch, "E384", {"start": v(18.08, 36.56) * mm, "end": v(18.11, 36.6) * mm});
            skLineSegment(sketch, "E385", {"start": v(18.11, 36.6) * mm, "end": v(18.14, 36.6) * mm});
            skLineSegment(sketch, "E386", {"start": v(18.14, 36.6) * mm, "end": v(18.22, 36.66) * mm});
            skLineSegment(sketch, "E387", {"start": v(18.22, 36.66) * mm, "end": v(18.37, 36.8) * mm});
            skLineSegment(sketch, "E388", {"start": v(18.37, 36.8) * mm, "end": v(18.52, 36.94) * mm});
            skLineSegment(sketch, "E389", {"start": v(18.52, 36.94) * mm, "end": v(18.58, 37.02) * mm});
            skLineSegment(sketch, "E390", {"start": v(18.58, 37.02) * mm, "end": v(18.6, 37.08) * mm});
            skLineSegment(sketch, "E391", {"start": v(18.6, 37.08) * mm, "end": v(18.62, 37.1) * mm});
            skLineSegment(sketch, "E392", {"start": v(18.62, 37.1) * mm, "end": v(18.62, 37.1) * mm});
            skLineSegment(sketch, "E393", {"start": v(18.62, 37.1) * mm, "end": v(18.69, 37.19) * mm});
            skLineSegment(sketch, "E394", {"start": v(18.69, 37.19) * mm, "end": v(18.75, 37.27) * mm});
            skLineSegment(sketch, "E395", {"start": v(18.75, 37.27) * mm, "end": v(18.8, 37.4) * mm});
            skLineSegment(sketch, "E396", {"start": v(18.8, 37.4) * mm, "end": v(18.94, 37.8) * mm});
            skLineSegment(sketch, "E397", {"start": v(18.94, 37.8) * mm, "end": v(18.98, 37.94) * mm});
            skLineSegment(sketch, "E398", {"start": v(18.98, 37.94) * mm, "end": v(18.98, 45) * mm});
            skLineSegment(sketch, "E399", {"start": v(18.98, 45) * mm, "end": v(18.94, 45.1) * mm});
            skLineSegment(sketch, "E400", {"start": v(18.94, 45.1) * mm, "end": v(18.86, 45.34) * mm});
            skLineSegment(sketch, "E401", {"start": v(18.86, 45.34) * mm, "end": v(18.79, 45.53) * mm});
            skLineSegment(sketch, "E402", {"start": v(18.79, 45.53) * mm, "end": v(18.7, 45.7) * mm});
            skLineSegment(sketch, "E403", {"start": v(18.7, 45.7) * mm, "end": v(18.63, 45.8) * mm});
            skLineSegment(sketch, "E404", {"start": v(18.63, 45.8) * mm, "end": v(18.6, 45.86) * mm});
            skLineSegment(sketch, "E405", {"start": v(18.6, 45.86) * mm, "end": v(18.55, 45.92) * mm});
            skLineSegment(sketch, "E406", {"start": v(18.55, 45.92) * mm, "end": v(18.46, 46.02) * mm});
            skLineSegment(sketch, "E407", {"start": v(18.46, 46.02) * mm, "end": v(18.2, 46.26) * mm});
            skLineSegment(sketch, "E408", {"start": v(18.2, 46.26) * mm, "end": v(18.06, 46.35) * mm});
            skLineSegment(sketch, "E409", {"start": v(18.06, 46.35) * mm, "end": v(17.89, 46.44) * mm});
            skLineSegment(sketch, "E410", {"start": v(17.89, 46.44) * mm, "end": v(17.7, 46.52) * mm});
            skLineSegment(sketch, "E411", {"start": v(17.7, 46.52) * mm, "end": v(17.53, 46.58) * mm});
            skLineSegment(sketch, "E412", {"start": v(17.53, 46.58) * mm, "end": v(17.42, 46.6) * mm});
            skLineSegment(sketch, "E413", {"start": v(17.42, 46.6) * mm, "end": v(17.3, 46.62) * mm});
            skLineSegment(sketch, "E414", {"start": v(17.3, 46.62) * mm, "end": v(17.02, 46.63) * mm});
            skLineSegment(sketch, "E415", {"start": v(17.02, 46.63) * mm, "end": v(16.73, 46.62) * mm});
            skLineSegment(sketch, "E416", {"start": v(7.5, 45.73) * mm, "end": v(9.5, 45.73) * mm});
            skLineSegment(sketch, "E417", {"start": v(9.5, 45.73) * mm, "end": v(9.5, 48.73) * mm});
            skLineSegment(sketch, "E418", {"start": v(9.5, 48.73) * mm, "end": v(7.5, 48.73) * mm});
            skLineSegment(sketch, "E419", {"start": v(7.5, 48.73) * mm, "end": v(7.5, 45.73) * mm});
            skLineSegment(sketch, "E420", {"start": v(32.5, 30.48) * mm, "end": v(35.5, 30.48) * mm});
            skLineSegment(sketch, "E421", {"start": v(35.5, 30.48) * mm, "end": v(35.5, 32.48) * mm});
            skLineSegment(sketch, "E422", {"start": v(35.5, 32.48) * mm, "end": v(32.5, 32.48) * mm});
            skLineSegment(sketch, "E423", {"start": v(32.5, 32.48) * mm, "end": v(32.5, 30.48) * mm});
            skLineSegment(sketch, "E424", {"start": v(26.5, 53.13) * mm, "end": v(41.5, 53.13) * mm});
            skLineSegment(sketch, "E425", {"start": v(41.5, 53.13) * mm, "end": v(41.5, 61.97) * mm});
            skLineSegment(sketch, "E426", {"start": v(41.5, 61.97) * mm, "end": v(26.5, 61.97) * mm});
            skLineSegment(sketch, "E427", {"start": v(26.5, 61.97) * mm, "end": v(26.5, 53.13) * mm});
            skArc(sketch, "E428", {"start": v(34.76, 56.95) * mm, "mid": v(35.5, 55.18) * mm, "end": v(37.26, 54.45) * mm});
            skArc(sketch, "E429", {"start": v(37.26, 54.45) * mm, "mid": v(39.03, 55.18) * mm, "end": v(39.76, 56.95) * mm});
            skArc(sketch, "E430", {"start": v(39.76, 56.95) * mm, "mid": v(39.03, 58.72) * mm, "end": v(37.26, 59.45) * mm});
            skArc(sketch, "E431", {"start": v(37.26, 59.45) * mm, "mid": v(35.5, 58.72) * mm, "end": v(34.76, 56.95) * mm});
            skLineSegment(sketch, "E432", {"start": v(26.5, 61.97) * mm, "end": v(26.5, 38.48) * mm});
            skArc(sketch, "E433", {"start": v(26.5, 38.48) * mm, "mid": v(28.26, 34.24) * mm, "end": v(32.5, 32.48) * mm});
            skLineSegment(sketch, "E434", {"start": v(32.5, 32.48) * mm, "end": v(35.5, 32.48) * mm});
            skArc(sketch, "E435", {"start": v(35.5, 32.48) * mm, "mid": v(39.74, 34.24) * mm, "end": v(41.5, 38.48) * mm});
            skLineSegment(sketch, "E436", {"start": v(41.5, 38.48) * mm, "end": v(41.5, 61.97) * mm});
            skArc(sketch, "E437", {"start": v(28.26, 56.95) * mm, "mid": v(29, 55.18) * mm, "end": v(30.76, 54.45) * mm});
            skArc(sketch, "E438", {"start": v(30.76, 54.45) * mm, "mid": v(32.53, 55.18) * mm, "end": v(33.26, 56.95) * mm});
            skArc(sketch, "E439", {"start": v(33.26, 56.95) * mm, "mid": v(32.53, 58.72) * mm, "end": v(30.76, 59.45) * mm});
            skArc(sketch, "E440", {"start": v(30.76, 59.45) * mm, "mid": v(29, 58.72) * mm, "end": v(28.26, 56.95) * mm});
            skArc(sketch, "E441", {"start": v(30.76, 58.45) * mm, "mid": v(29.7, 58.01) * mm, "end": v(29.26, 56.95) * mm});
            skArc(sketch, "E442", {"start": v(29.26, 56.95) * mm, "mid": v(29.7, 55.9) * mm, "end": v(30.76, 55.45) * mm});
            skArc(sketch, "E443", {"start": v(30.76, 55.45) * mm, "mid": v(31.82, 55.9) * mm, "end": v(32.26, 56.95) * mm});
            skArc(sketch, "E444", {"start": v(32.26, 56.95) * mm, "mid": v(31.82, 58.01) * mm, "end": v(30.76, 58.45) * mm});
            skArc(sketch, "E445", {"start": v(37.27, 58.45) * mm, "mid": v(36.2, 58.01) * mm, "end": v(35.77, 56.95) * mm});
            skArc(sketch, "E446", {"start": v(35.77, 56.95) * mm, "mid": v(36.2, 55.9) * mm, "end": v(37.27, 55.45) * mm});
            skArc(sketch, "E447", {"start": v(37.27, 55.45) * mm, "mid": v(38.33, 55.9) * mm, "end": v(38.77, 56.95) * mm});
            skArc(sketch, "E448", {"start": v(38.77, 56.95) * mm, "mid": v(38.33, 58.01) * mm, "end": v(37.27, 58.45) * mm});
            skLineSegment(sketch, "E449", {"start": v(33.73, 46.62) * mm, "end": v(33.6, 46.6) * mm});
            skLineSegment(sketch, "E450", {"start": v(33.6, 46.6) * mm, "end": v(33.5, 46.58) * mm});
            skLineSegment(sketch, "E451", {"start": v(33.5, 46.58) * mm, "end": v(33.28, 46.5) * mm});
            skLineSegment(sketch, "E452", {"start": v(33.28, 46.5) * mm, "end": v(33.06, 46.4) * mm});
            skLineSegment(sketch, "E453", {"start": v(33.06, 46.4) * mm, "end": v(32.85, 46.27) * mm});
            skLineSegment(sketch, "E454", {"start": v(32.85, 46.27) * mm, "end": v(32.67, 46.12) * mm});
            skLineSegment(sketch, "E455", {"start": v(32.67, 46.12) * mm, "end": v(32.47, 45.92) * mm});
            skLineSegment(sketch, "E456", {"start": v(32.47, 45.92) * mm, "end": v(32.4, 45.8) * mm});
            skLineSegment(sketch, "E457", {"start": v(32.4, 45.8) * mm, "end": v(32.4, 45.8) * mm});
            skLineSegment(sketch, "E458", {"start": v(32.4, 45.8) * mm, "end": v(32.34, 45.7) * mm});
            skLineSegment(sketch, "E459", {"start": v(32.34, 45.7) * mm, "end": v(32.24, 45.53) * mm});
            skLineSegment(sketch, "E460", {"start": v(32.24, 45.53) * mm, "end": v(32.17, 45.34) * mm});
            skLineSegment(sketch, "E461", {"start": v(32.17, 45.34) * mm, "end": v(32.09, 45.1) * mm});
            skLineSegment(sketch, "E462", {"start": v(32.09, 45.1) * mm, "end": v(32.05, 45) * mm});
            skLineSegment(sketch, "E463", {"start": v(32.05, 45) * mm, "end": v(32.05, 37.9) * mm});
            skLineSegment(sketch, "E464", {"start": v(32.05, 37.9) * mm, "end": v(32.09, 37.81) * mm});
            skLineSegment(sketch, "E465", {"start": v(32.09, 37.81) * mm, "end": v(32.16, 37.58) * mm});
            skLineSegment(sketch, "E466", {"start": v(32.16, 37.58) * mm, "end": v(32.21, 37.43) * mm});
            skLineSegment(sketch, "E467", {"start": v(32.21, 37.43) * mm, "end": v(32.26, 37.31) * mm});
            skLineSegment(sketch, "E468", {"start": v(32.26, 37.31) * mm, "end": v(32.33, 37.2) * mm});
            skLineSegment(sketch, "E469", {"start": v(32.33, 37.2) * mm, "end": v(32.4, 37.11) * mm});
            skLineSegment(sketch, "E470", {"start": v(32.4, 37.11) * mm, "end": v(32.41, 37.1) * mm});
            skLineSegment(sketch, "E471", {"start": v(32.41, 37.1) * mm, "end": v(32.42, 37.07) * mm});
            skLineSegment(sketch, "E472", {"start": v(32.42, 37.07) * mm, "end": v(32.48, 36.98) * mm});
            skLineSegment(sketch, "E473", {"start": v(32.48, 36.98) * mm, "end": v(32.58, 36.87) * mm});
            skLineSegment(sketch, "E474", {"start": v(32.58, 36.87) * mm, "end": v(32.78, 36.68) * mm});
            skLineSegment(sketch, "E475", {"start": v(32.78, 36.68) * mm, "end": v(32.87, 36.62) * mm});
            skLineSegment(sketch, "E476", {"start": v(32.87, 36.62) * mm, "end": v(32.93, 36.58) * mm});
            skLineSegment(sketch, "E477", {"start": v(32.93, 36.58) * mm, "end": v(32.96, 36.56) * mm});
            skLineSegment(sketch, "E478", {"start": v(32.96, 36.56) * mm, "end": v(33.05, 36.51) * mm});
            skLineSegment(sketch, "E479", {"start": v(33.05, 36.51) * mm, "end": v(33.34, 36.37) * mm});
            skLineSegment(sketch, "E480", {"start": v(33.34, 36.37) * mm, "end": v(33.49, 36.32) * mm});
            skLineSegment(sketch, "E481", {"start": v(33.49, 36.32) * mm, "end": v(33.65, 36.29) * mm});
            skLineSegment(sketch, "E482", {"start": v(33.65, 36.29) * mm, "end": v(33.83, 36.27) * mm});
            skLineSegment(sketch, "E483", {"start": v(33.83, 36.27) * mm, "end": v(34, 36.26) * mm});
            skLineSegment(sketch, "E484", {"start": v(34, 36.26) * mm, "end": v(34.19, 36.27) * mm});
            skLineSegment(sketch, "E485", {"start": v(34.19, 36.27) * mm, "end": v(34.36, 36.29) * mm});
            skLineSegment(sketch, "E486", {"start": v(34.36, 36.29) * mm, "end": v(34.53, 36.32) * mm});
            skLineSegment(sketch, "E487", {"start": v(34.53, 36.32) * mm, "end": v(34.68, 36.37) * mm});
            skLineSegment(sketch, "E488", {"start": v(34.68, 36.37) * mm, "end": v(34.98, 36.5) * mm});
            skLineSegment(sketch, "E489", {"start": v(34.98, 36.5) * mm, "end": v(35.08, 36.56) * mm});
            skLineSegment(sketch, "E490", {"start": v(35.08, 36.56) * mm, "end": v(35.11, 36.6) * mm});
            skLineSegment(sketch, "E491", {"start": v(35.11, 36.6) * mm, "end": v(35.14, 36.6) * mm});
            skLineSegment(sketch, "E492", {"start": v(35.14, 36.6) * mm, "end": v(35.22, 36.66) * mm});
            skLineSegment(sketch, "E493", {"start": v(35.22, 36.66) * mm, "end": v(35.37, 36.8) * mm});
            skLineSegment(sketch, "E494", {"start": v(35.37, 36.8) * mm, "end": v(35.52, 36.94) * mm});
            skLineSegment(sketch, "E495", {"start": v(35.52, 36.94) * mm, "end": v(35.58, 37.02) * mm});
            skLineSegment(sketch, "E496", {"start": v(35.58, 37.02) * mm, "end": v(35.6, 37.08) * mm});
            skLineSegment(sketch, "E497", {"start": v(35.6, 37.08) * mm, "end": v(35.62, 37.1) * mm});
            skLineSegment(sketch, "E498", {"start": v(35.62, 37.1) * mm, "end": v(35.62, 37.1) * mm});
            skLineSegment(sketch, "E499", {"start": v(35.62, 37.1) * mm, "end": v(35.69, 37.19) * mm});
            skLineSegment(sketch, "E500", {"start": v(35.69, 37.19) * mm, "end": v(35.75, 37.27) * mm});
            skLineSegment(sketch, "E501", {"start": v(35.75, 37.27) * mm, "end": v(35.8, 37.4) * mm});
            skLineSegment(sketch, "E502", {"start": v(35.8, 37.4) * mm, "end": v(35.94, 37.8) * mm});
            skLineSegment(sketch, "E503", {"start": v(35.94, 37.8) * mm, "end": v(35.98, 37.94) * mm});
            skLineSegment(sketch, "E504", {"start": v(35.98, 37.94) * mm, "end": v(35.98, 45) * mm});
            skLineSegment(sketch, "E505", {"start": v(35.98, 45) * mm, "end": v(35.94, 45.1) * mm});
            skLineSegment(sketch, "E506", {"start": v(35.94, 45.1) * mm, "end": v(35.86, 45.34) * mm});
            skLineSegment(sketch, "E507", {"start": v(35.86, 45.34) * mm, "end": v(35.79, 45.53) * mm});
            skLineSegment(sketch, "E508", {"start": v(35.79, 45.53) * mm, "end": v(35.7, 45.7) * mm});
            skLineSegment(sketch, "E509", {"start": v(35.7, 45.7) * mm, "end": v(35.63, 45.8) * mm});
            skLineSegment(sketch, "E510", {"start": v(35.63, 45.8) * mm, "end": v(35.6, 45.86) * mm});
            skLineSegment(sketch, "E511", {"start": v(35.6, 45.86) * mm, "end": v(35.55, 45.92) * mm});
            skLineSegment(sketch, "E512", {"start": v(35.55, 45.92) * mm, "end": v(35.46, 46.02) * mm});
            skLineSegment(sketch, "E513", {"start": v(35.46, 46.02) * mm, "end": v(35.2, 46.26) * mm});
            skLineSegment(sketch, "E514", {"start": v(35.2, 46.26) * mm, "end": v(35.06, 46.35) * mm});
            skLineSegment(sketch, "E515", {"start": v(35.06, 46.35) * mm, "end": v(34.89, 46.44) * mm});
            skLineSegment(sketch, "E516", {"start": v(34.89, 46.44) * mm, "end": v(34.7, 46.52) * mm});
            skLineSegment(sketch, "E517", {"start": v(34.7, 46.52) * mm, "end": v(34.53, 46.58) * mm});
            skLineSegment(sketch, "E518", {"start": v(34.53, 46.58) * mm, "end": v(34.42, 46.6) * mm});
            skLineSegment(sketch, "E519", {"start": v(34.42, 46.6) * mm, "end": v(34.3, 46.62) * mm});
            skLineSegment(sketch, "E520", {"start": v(34.3, 46.62) * mm, "end": v(34.02, 46.63) * mm});
            skLineSegment(sketch, "E521", {"start": v(34.02, 46.63) * mm, "end": v(33.73, 46.62) * mm});
            skLineSegment(sketch, "E522", {"start": v(24.5, 45.73) * mm, "end": v(26.5, 45.73) * mm});
            skLineSegment(sketch, "E523", {"start": v(26.5, 45.73) * mm, "end": v(26.5, 48.73) * mm});
            skLineSegment(sketch, "E524", {"start": v(26.5, 48.73) * mm, "end": v(24.5, 48.73) * mm});
            skLineSegment(sketch, "E525", {"start": v(24.5, 48.73) * mm, "end": v(24.5, 45.73) * mm});
            skLineSegment(sketch, "E526", {"start": v(-1.5, 30.48) * mm, "end": v(1.5, 30.48) * mm});
            skLineSegment(sketch, "E527", {"start": v(1.5, 30.48) * mm, "end": v(1.5, 32.48) * mm});
            skLineSegment(sketch, "E528", {"start": v(1.5, 32.48) * mm, "end": v(-1.5, 32.48) * mm});
            skLineSegment(sketch, "E529", {"start": v(-1.5, 32.48) * mm, "end": v(-1.5, 30.48) * mm});
            skLineSegment(sketch, "E530", {"start": v(-7.5, 53.13) * mm, "end": v(7.5, 53.13) * mm});
            skLineSegment(sketch, "E531", {"start": v(7.5, 53.13) * mm, "end": v(7.5, 61.97) * mm});
            skLineSegment(sketch, "E532", {"start": v(7.5, 61.97) * mm, "end": v(-7.5, 61.97) * mm});
            skLineSegment(sketch, "E533", {"start": v(-7.5, 61.97) * mm, "end": v(-7.5, 53.13) * mm});
            skArc(sketch, "E534", {"start": v(0.76, 56.95) * mm, "mid": v(1.5, 55.18) * mm, "end": v(3.26, 54.45) * mm});
            skArc(sketch, "E535", {"start": v(3.26, 54.45) * mm, "mid": v(5.03, 55.18) * mm, "end": v(5.76, 56.95) * mm});
            skArc(sketch, "E536", {"start": v(5.76, 56.95) * mm, "mid": v(5.03, 58.72) * mm, "end": v(3.26, 59.45) * mm});
            skArc(sketch, "E537", {"start": v(3.26, 59.45) * mm, "mid": v(1.5, 58.72) * mm, "end": v(0.76, 56.95) * mm});
            skLineSegment(sketch, "E538", {"start": v(-7.5, 61.97) * mm, "end": v(-7.5, 38.48) * mm});
            skArc(sketch, "E539", {"start": v(-7.5, 38.48) * mm, "mid": v(-5.74, 34.24) * mm, "end": v(-1.5, 32.48) * mm});
            skLineSegment(sketch, "E540", {"start": v(-1.5, 32.48) * mm, "end": v(1.5, 32.48) * mm});
            skArc(sketch, "E541", {"start": v(1.5, 32.48) * mm, "mid": v(5.74, 34.24) * mm, "end": v(7.5, 38.48) * mm});
            skLineSegment(sketch, "E542", {"start": v(7.5, 38.48) * mm, "end": v(7.5, 61.97) * mm});
            skArc(sketch, "E543", {"start": v(-5.74, 56.95) * mm, "mid": v(-5, 55.18) * mm, "end": v(-3.24, 54.45) * mm});
            skArc(sketch, "E544", {"start": v(-3.24, 54.45) * mm, "mid": v(-1.47, 55.18) * mm, "end": v(-0.74, 56.95) * mm});
            skArc(sketch, "E545", {"start": v(-0.74, 56.95) * mm, "mid": v(-1.47, 58.72) * mm, "end": v(-3.24, 59.45) * mm});
            skArc(sketch, "E546", {"start": v(-3.24, 59.45) * mm, "mid": v(-5, 58.72) * mm, "end": v(-5.74, 56.95) * mm});
            skArc(sketch, "E547", {"start": v(-3.24, 58.45) * mm, "mid": v(-4.3, 58.01) * mm, "end": v(-4.74, 56.95) * mm});
            skArc(sketch, "E548", {"start": v(-4.74, 56.95) * mm, "mid": v(-4.3, 55.9) * mm, "end": v(-3.24, 55.45) * mm});
            skArc(sketch, "E549", {"start": v(-3.24, 55.45) * mm, "mid": v(-2.18, 55.9) * mm, "end": v(-1.74, 56.95) * mm});
            skArc(sketch, "E550", {"start": v(-1.74, 56.95) * mm, "mid": v(-2.18, 58.01) * mm, "end": v(-3.24, 58.45) * mm});
            skArc(sketch, "E551", {"start": v(3.26, 58.45) * mm, "mid": v(2.2, 58.01) * mm, "end": v(1.76, 56.95) * mm});
            skArc(sketch, "E552", {"start": v(1.76, 56.95) * mm, "mid": v(2.2, 55.9) * mm, "end": v(3.26, 55.45) * mm});
            skArc(sketch, "E553", {"start": v(3.26, 55.45) * mm, "mid": v(4.33, 55.9) * mm, "end": v(4.76, 56.95) * mm});
            skArc(sketch, "E554", {"start": v(4.76, 56.95) * mm, "mid": v(4.33, 58.01) * mm, "end": v(3.26, 58.45) * mm});
            skLineSegment(sketch, "E555", {"start": v(-0.27, 46.62) * mm, "end": v(-0.4, 46.6) * mm});
            skLineSegment(sketch, "E556", {"start": v(-0.4, 46.6) * mm, "end": v(-0.5, 46.58) * mm});
            skLineSegment(sketch, "E557", {"start": v(-0.5, 46.58) * mm, "end": v(-0.72, 46.5) * mm});
            skLineSegment(sketch, "E558", {"start": v(-0.72, 46.5) * mm, "end": v(-0.94, 46.4) * mm});
            skLineSegment(sketch, "E559", {"start": v(-0.94, 46.4) * mm, "end": v(-1.15, 46.27) * mm});
            skLineSegment(sketch, "E560", {"start": v(-1.15, 46.27) * mm, "end": v(-1.33, 46.12) * mm});
            skLineSegment(sketch, "E561", {"start": v(-1.33, 46.12) * mm, "end": v(-1.53, 45.92) * mm});
            skLineSegment(sketch, "E562", {"start": v(-1.53, 45.92) * mm, "end": v(-1.6, 45.8) * mm});
            skLineSegment(sketch, "E563", {"start": v(-1.6, 45.8) * mm, "end": v(-1.6, 45.8) * mm});
            skLineSegment(sketch, "E564", {"start": v(-1.6, 45.8) * mm, "end": v(-1.66, 45.7) * mm});
            skLineSegment(sketch, "E565", {"start": v(-1.66, 45.7) * mm, "end": v(-1.76, 45.53) * mm});
            skLineSegment(sketch, "E566", {"start": v(-1.76, 45.53) * mm, "end": v(-1.83, 45.34) * mm});
            skLineSegment(sketch, "E567", {"start": v(-1.83, 45.34) * mm, "end": v(-1.91, 45.1) * mm});
            skLineSegment(sketch, "E568", {"start": v(-1.91, 45.1) * mm, "end": v(-1.95, 45) * mm});
            skLineSegment(sketch, "E569", {"start": v(-1.95, 45) * mm, "end": v(-1.95, 37.9) * mm});
            skLineSegment(sketch, "E570", {"start": v(-1.95, 37.9) * mm, "end": v(-1.91, 37.81) * mm});
            skLineSegment(sketch, "E571", {"start": v(-1.91, 37.81) * mm, "end": v(-1.84, 37.58) * mm});
            skLineSegment(sketch, "E572", {"start": v(-1.84, 37.58) * mm, "end": v(-1.79, 37.43) * mm});
            skLineSegment(sketch, "E573", {"start": v(-1.79, 37.43) * mm, "end": v(-1.74, 37.31) * mm});
            skLineSegment(sketch, "E574", {"start": v(-1.74, 37.31) * mm, "end": v(-1.67, 37.2) * mm});
            skLineSegment(sketch, "E575", {"start": v(-1.67, 37.2) * mm, "end": v(-1.6, 37.11) * mm});
            skLineSegment(sketch, "E576", {"start": v(-1.6, 37.11) * mm, "end": v(-1.59, 37.1) * mm});
            skLineSegment(sketch, "E577", {"start": v(-1.59, 37.1) * mm, "end": v(-1.58, 37.07) * mm});
            skLineSegment(sketch, "E578", {"start": v(-1.58, 37.07) * mm, "end": v(-1.52, 36.98) * mm});
            skLineSegment(sketch, "E579", {"start": v(-1.52, 36.98) * mm, "end": v(-1.42, 36.87) * mm});
            skLineSegment(sketch, "E580", {"start": v(-1.42, 36.87) * mm, "end": v(-1.22, 36.68) * mm});
            skLineSegment(sketch, "E581", {"start": v(-1.22, 36.68) * mm, "end": v(-1.13, 36.62) * mm});
            skLineSegment(sketch, "E582", {"start": v(-1.13, 36.62) * mm, "end": v(-1.07, 36.58) * mm});
            skLineSegment(sketch, "E583", {"start": v(-1.07, 36.58) * mm, "end": v(-1.04, 36.56) * mm});
            skLineSegment(sketch, "E584", {"start": v(-1.04, 36.56) * mm, "end": v(-0.95, 36.51) * mm});
            skLineSegment(sketch, "E585", {"start": v(-0.95, 36.51) * mm, "end": v(-0.66, 36.37) * mm});
            skLineSegment(sketch, "E586", {"start": v(-0.66, 36.37) * mm, "end": v(-0.51, 36.32) * mm});
            skLineSegment(sketch, "E587", {"start": v(-0.51, 36.32) * mm, "end": v(-0.35, 36.29) * mm});
            skLineSegment(sketch, "E588", {"start": v(-0.35, 36.29) * mm, "end": v(-0.17, 36.27) * mm});
            skLineSegment(sketch, "E589", {"start": v(-0.17, 36.27) * mm, "end": v(0, 36.26) * mm});
            skLineSegment(sketch, "E590", {"start": v(0, 36.26) * mm, "end": v(0.19, 36.27) * mm});
            skLineSegment(sketch, "E591", {"start": v(0.19, 36.27) * mm, "end": v(0.36, 36.29) * mm});
            skLineSegment(sketch, "E592", {"start": v(0.36, 36.29) * mm, "end": v(0.53, 36.32) * mm});
            skLineSegment(sketch, "E593", {"start": v(0.53, 36.32) * mm, "end": v(0.68, 36.37) * mm});
            skLineSegment(sketch, "E594", {"start": v(0.68, 36.37) * mm, "end": v(0.98, 36.5) * mm});
            skLineSegment(sketch, "E595", {"start": v(0.98, 36.5) * mm, "end": v(1.08, 36.56) * mm});
            skLineSegment(sketch, "E596", {"start": v(1.08, 36.56) * mm, "end": v(1.11, 36.6) * mm});
            skLineSegment(sketch, "E597", {"start": v(1.11, 36.6) * mm, "end": v(1.14, 36.6) * mm});
            skLineSegment(sketch, "E598", {"start": v(1.14, 36.6) * mm, "end": v(1.22, 36.66) * mm});
            skLineSegment(sketch, "E599", {"start": v(1.22, 36.66) * mm, "end": v(1.37, 36.8) * mm});
            skLineSegment(sketch, "E600", {"start": v(1.37, 36.8) * mm, "end": v(1.52, 36.94) * mm});
            skLineSegment(sketch, "E601", {"start": v(1.52, 36.94) * mm, "end": v(1.58, 37.02) * mm});
            skLineSegment(sketch, "E602", {"start": v(1.58, 37.02) * mm, "end": v(1.6, 37.08) * mm});
            skLineSegment(sketch, "E603", {"start": v(1.6, 37.08) * mm, "end": v(1.62, 37.1) * mm});
            skLineSegment(sketch, "E604", {"start": v(1.62, 37.1) * mm, "end": v(1.62, 37.1) * mm});
            skLineSegment(sketch, "E605", {"start": v(1.62, 37.1) * mm, "end": v(1.69, 37.19) * mm});
            skLineSegment(sketch, "E606", {"start": v(1.69, 37.19) * mm, "end": v(1.75, 37.27) * mm});
            skLineSegment(sketch, "E607", {"start": v(1.75, 37.27) * mm, "end": v(1.8, 37.4) * mm});
            skLineSegment(sketch, "E608", {"start": v(1.8, 37.4) * mm, "end": v(1.94, 37.8) * mm});
            skLineSegment(sketch, "E609", {"start": v(1.94, 37.8) * mm, "end": v(1.98, 37.94) * mm});
            skLineSegment(sketch, "E610", {"start": v(1.98, 37.94) * mm, "end": v(1.98, 45) * mm});
            skLineSegment(sketch, "E611", {"start": v(1.98, 45) * mm, "end": v(1.94, 45.1) * mm});
            skLineSegment(sketch, "E612", {"start": v(1.94, 45.1) * mm, "end": v(1.86, 45.34) * mm});
            skLineSegment(sketch, "E613", {"start": v(1.86, 45.34) * mm, "end": v(1.79, 45.53) * mm});
            skLineSegment(sketch, "E614", {"start": v(1.79, 45.53) * mm, "end": v(1.7, 45.7) * mm});
            skLineSegment(sketch, "E615", {"start": v(1.7, 45.7) * mm, "end": v(1.63, 45.8) * mm});
            skLineSegment(sketch, "E616", {"start": v(1.63, 45.8) * mm, "end": v(1.6, 45.86) * mm});
            skLineSegment(sketch, "E617", {"start": v(1.6, 45.86) * mm, "end": v(1.55, 45.92) * mm});
            skLineSegment(sketch, "E618", {"start": v(1.55, 45.92) * mm, "end": v(1.46, 46.02) * mm});
            skLineSegment(sketch, "E619", {"start": v(1.46, 46.02) * mm, "end": v(1.2, 46.26) * mm});
            skLineSegment(sketch, "E620", {"start": v(1.2, 46.26) * mm, "end": v(1.06, 46.35) * mm});
            skLineSegment(sketch, "E621", {"start": v(1.06, 46.35) * mm, "end": v(0.89, 46.44) * mm});
            skLineSegment(sketch, "E622", {"start": v(0.89, 46.44) * mm, "end": v(0.7, 46.52) * mm});
            skLineSegment(sketch, "E623", {"start": v(0.7, 46.52) * mm, "end": v(0.53, 46.58) * mm});
            skLineSegment(sketch, "E624", {"start": v(0.53, 46.58) * mm, "end": v(0.42, 46.6) * mm});
            skLineSegment(sketch, "E625", {"start": v(0.42, 46.6) * mm, "end": v(0.3, 46.62) * mm});
            skLineSegment(sketch, "E626", {"start": v(0.3, 46.62) * mm, "end": v(0.02, 46.63) * mm});
            skLineSegment(sketch, "E627", {"start": v(0.02, 46.63) * mm, "end": v(-0.27, 46.62) * mm});
            skLineSegment(sketch, "E628", {"start": v(-9.5, 45.73) * mm, "end": v(-7.5, 45.73) * mm});
            skLineSegment(sketch, "E629", {"start": v(-7.5, 45.73) * mm, "end": v(-7.5, 48.73) * mm});
            skLineSegment(sketch, "E630", {"start": v(-7.5, 48.73) * mm, "end": v(-9.5, 48.73) * mm});
            skLineSegment(sketch, "E631", {"start": v(-9.5, 48.73) * mm, "end": v(-9.5, 45.73) * mm});
            skLineSegment(sketch, "E632", {"start": v(-52.5, -1) * mm, "end": v(-49.5, -1) * mm});
            skLineSegment(sketch, "E633", {"start": v(-49.5, -1) * mm, "end": v(-49.5, 1) * mm});
            skLineSegment(sketch, "E634", {"start": v(-49.5, 1) * mm, "end": v(-52.5, 1) * mm});
            skLineSegment(sketch, "E635", {"start": v(-52.5, 1) * mm, "end": v(-52.5, -1) * mm});
            skLineSegment(sketch, "E636", {"start": v(-58.5, 21.64) * mm, "end": v(-43.5, 21.64) * mm});
            skLineSegment(sketch, "E637", {"start": v(-43.5, 21.64) * mm, "end": v(-43.5, 30.48) * mm});
            skLineSegment(sketch, "E638", {"start": v(-43.5, 30.48) * mm, "end": v(-58.5, 30.48) * mm});
            skLineSegment(sketch, "E639", {"start": v(-58.5, 30.48) * mm, "end": v(-58.5, 21.64) * mm});
            skArc(sketch, "E640", {"start": v(-50.24, 25.47) * mm, "mid": v(-49.5, 23.7) * mm, "end": v(-47.74, 22.97) * mm});
            skArc(sketch, "E641", {"start": v(-47.74, 22.97) * mm, "mid": v(-45.97, 23.7) * mm, "end": v(-45.24, 25.47) * mm});
            skArc(sketch, "E642", {"start": v(-45.24, 25.47) * mm, "mid": v(-45.97, 27.23) * mm, "end": v(-47.74, 27.97) * mm});
            skArc(sketch, "E643", {"start": v(-47.74, 27.97) * mm, "mid": v(-49.5, 27.23) * mm, "end": v(-50.24, 25.47) * mm});
            skLineSegment(sketch, "E644", {"start": v(-58.5, 30.48) * mm, "end": v(-58.5, 7) * mm});
            skArc(sketch, "E645", {"start": v(-58.5, 7) * mm, "mid": v(-56.74, 2.76) * mm, "end": v(-52.5, 1) * mm});
            skLineSegment(sketch, "E646", {"start": v(-52.5, 1) * mm, "end": v(-49.5, 1) * mm});
            skArc(sketch, "E647", {"start": v(-49.5, 1) * mm, "mid": v(-45.26, 2.76) * mm, "end": v(-43.5, 7) * mm});
            skLineSegment(sketch, "E648", {"start": v(-43.5, 7) * mm, "end": v(-43.5, 30.48) * mm});
            skArc(sketch, "E649", {"start": v(-56.74, 25.47) * mm, "mid": v(-56, 23.7) * mm, "end": v(-54.24, 22.97) * mm});
            skArc(sketch, "E650", {"start": v(-54.24, 22.97) * mm, "mid": v(-52.47, 23.7) * mm, "end": v(-51.74, 25.47) * mm});
            skArc(sketch, "E651", {"start": v(-51.74, 25.47) * mm, "mid": v(-52.47, 27.23) * mm, "end": v(-54.24, 27.97) * mm});
            skArc(sketch, "E652", {"start": v(-54.24, 27.97) * mm, "mid": v(-56, 27.23) * mm, "end": v(-56.74, 25.47) * mm});
            skArc(sketch, "E653", {"start": v(-54.24, 26.97) * mm, "mid": v(-55.3, 26.53) * mm, "end": v(-55.74, 25.47) * mm});
            skArc(sketch, "E654", {"start": v(-55.74, 25.47) * mm, "mid": v(-55.3, 24.4) * mm, "end": v(-54.24, 23.97) * mm});
            skArc(sketch, "E655", {"start": v(-54.24, 23.97) * mm, "mid": v(-53.18, 24.4) * mm, "end": v(-52.74, 25.47) * mm});
            skArc(sketch, "E656", {"start": v(-52.74, 25.47) * mm, "mid": v(-53.18, 26.53) * mm, "end": v(-54.24, 26.97) * mm});
            skArc(sketch, "E657", {"start": v(-47.74, 26.97) * mm, "mid": v(-48.8, 26.53) * mm, "end": v(-49.24, 25.47) * mm});
            skArc(sketch, "E658", {"start": v(-49.24, 25.47) * mm, "mid": v(-48.8, 24.4) * mm, "end": v(-47.74, 23.97) * mm});
            skArc(sketch, "E659", {"start": v(-47.74, 23.97) * mm, "mid": v(-46.67, 24.4) * mm, "end": v(-46.24, 25.47) * mm});
            skArc(sketch, "E660", {"start": v(-46.24, 25.47) * mm, "mid": v(-46.67, 26.53) * mm, "end": v(-47.74, 26.97) * mm});
            skLineSegment(sketch, "E661", {"start": v(-51.27, 15.13) * mm, "end": v(-51.4, 15.12) * mm});
            skLineSegment(sketch, "E662", {"start": v(-51.4, 15.12) * mm, "end": v(-51.5, 15.1) * mm});
            skLineSegment(sketch, "E663", {"start": v(-51.5, 15.1) * mm, "end": v(-51.72, 15.02) * mm});
            skLineSegment(sketch, "E664", {"start": v(-51.72, 15.02) * mm, "end": v(-51.94, 14.91) * mm});
            skLineSegment(sketch, "E665", {"start": v(-51.94, 14.91) * mm, "end": v(-52.15, 14.78) * mm});
            skLineSegment(sketch, "E666", {"start": v(-52.15, 14.78) * mm, "end": v(-52.33, 14.63) * mm});
            skLineSegment(sketch, "E667", {"start": v(-52.33, 14.63) * mm, "end": v(-52.53, 14.44) * mm});
            skLineSegment(sketch, "E668", {"start": v(-52.53, 14.44) * mm, "end": v(-52.6, 14.32) * mm});
            skLineSegment(sketch, "E669", {"start": v(-52.6, 14.32) * mm, "end": v(-52.6, 14.31) * mm});
            skLineSegment(sketch, "E670", {"start": v(-52.6, 14.31) * mm, "end": v(-52.66, 14.21) * mm});
            skLineSegment(sketch, "E671", {"start": v(-52.66, 14.21) * mm, "end": v(-52.76, 14.04) * mm});
            skLineSegment(sketch, "E672", {"start": v(-52.76, 14.04) * mm, "end": v(-52.83, 13.86) * mm});
            skLineSegment(sketch, "E673", {"start": v(-52.83, 13.86) * mm, "end": v(-52.91, 13.61) * mm});
            skLineSegment(sketch, "E674", {"start": v(-52.91, 13.61) * mm, "end": v(-52.95, 13.51) * mm});
            skLineSegment(sketch, "E675", {"start": v(-52.95, 13.51) * mm, "end": v(-52.95, 6.42) * mm});
            skLineSegment(sketch, "E676", {"start": v(-52.95, 6.42) * mm, "end": v(-52.91, 6.33) * mm});
            skLineSegment(sketch, "E677", {"start": v(-52.91, 6.33) * mm, "end": v(-52.84, 6.1) * mm});
            skLineSegment(sketch, "E678", {"start": v(-52.84, 6.1) * mm, "end": v(-52.79, 5.95) * mm});
            skLineSegment(sketch, "E679", {"start": v(-52.79, 5.95) * mm, "end": v(-52.74, 5.83) * mm});
            skLineSegment(sketch, "E680", {"start": v(-52.74, 5.83) * mm, "end": v(-52.67, 5.72) * mm});
            skLineSegment(sketch, "E681", {"start": v(-52.67, 5.72) * mm, "end": v(-52.6, 5.63) * mm});
            skLineSegment(sketch, "E682", {"start": v(-52.6, 5.63) * mm, "end": v(-52.59, 5.62) * mm});
            skLineSegment(sketch, "E683", {"start": v(-52.59, 5.62) * mm, "end": v(-52.58, 5.58) * mm});
            skLineSegment(sketch, "E684", {"start": v(-52.58, 5.58) * mm, "end": v(-52.52, 5.5) * mm});
            skLineSegment(sketch, "E685", {"start": v(-52.52, 5.5) * mm, "end": v(-52.42, 5.39) * mm});
            skLineSegment(sketch, "E686", {"start": v(-52.42, 5.39) * mm, "end": v(-52.22, 5.2) * mm});
            skLineSegment(sketch, "E687", {"start": v(-52.22, 5.2) * mm, "end": v(-52.13, 5.13) * mm});
            skLineSegment(sketch, "E688", {"start": v(-52.13, 5.13) * mm, "end": v(-52.07, 5.1) * mm});
            skLineSegment(sketch, "E689", {"start": v(-52.07, 5.1) * mm, "end": v(-52.04, 5.08) * mm});
            skLineSegment(sketch, "E690", {"start": v(-52.04, 5.08) * mm, "end": v(-51.95, 5.03) * mm});
            skLineSegment(sketch, "E691", {"start": v(-51.95, 5.03) * mm, "end": v(-51.66, 4.89) * mm});
            skLineSegment(sketch, "E692", {"start": v(-51.66, 4.89) * mm, "end": v(-51.51, 4.84) * mm});
            skLineSegment(sketch, "E693", {"start": v(-51.51, 4.84) * mm, "end": v(-51.35, 4.8) * mm});
            skLineSegment(sketch, "E694", {"start": v(-51.35, 4.8) * mm, "end": v(-51.17, 4.78) * mm});
            skLineSegment(sketch, "E695", {"start": v(-51.17, 4.78) * mm, "end": v(-51, 4.78) * mm});
            skLineSegment(sketch, "E696", {"start": v(-51, 4.78) * mm, "end": v(-50.81, 4.78) * mm});
            skLineSegment(sketch, "E697", {"start": v(-50.81, 4.78) * mm, "end": v(-50.64, 4.8) * mm});
            skLineSegment(sketch, "E698", {"start": v(-50.64, 4.8) * mm, "end": v(-50.47, 4.84) * mm});
            skLineSegment(sketch, "E699", {"start": v(-50.47, 4.84) * mm, "end": v(-50.32, 4.89) * mm});
            skLineSegment(sketch, "E700", {"start": v(-50.32, 4.89) * mm, "end": v(-50.02, 5.02) * mm});
            skLineSegment(sketch, "E701", {"start": v(-50.02, 5.02) * mm, "end": v(-49.92, 5.08) * mm});
            skLineSegment(sketch, "E702", {"start": v(-49.92, 5.08) * mm, "end": v(-49.89, 5.11) * mm});
            skLineSegment(sketch, "E703", {"start": v(-49.89, 5.11) * mm, "end": v(-49.86, 5.12) * mm});
            skLineSegment(sketch, "E704", {"start": v(-49.86, 5.12) * mm, "end": v(-49.78, 5.18) * mm});
            skLineSegment(sketch, "E705", {"start": v(-49.78, 5.18) * mm, "end": v(-49.63, 5.31) * mm});
            skLineSegment(sketch, "E706", {"start": v(-49.63, 5.31) * mm, "end": v(-49.48, 5.46) * mm});
            skLineSegment(sketch, "E707", {"start": v(-49.48, 5.46) * mm, "end": v(-49.42, 5.53) * mm});
            skLineSegment(sketch, "E708", {"start": v(-49.42, 5.53) * mm, "end": v(-49.4, 5.6) * mm});
            skLineSegment(sketch, "E709", {"start": v(-49.4, 5.6) * mm, "end": v(-49.38, 5.62) * mm});
            skLineSegment(sketch, "E710", {"start": v(-49.38, 5.62) * mm, "end": v(-49.38, 5.62) * mm});
            skLineSegment(sketch, "E711", {"start": v(-49.38, 5.62) * mm, "end": v(-49.31, 5.7) * mm});
            skLineSegment(sketch, "E712", {"start": v(-49.31, 5.7) * mm, "end": v(-49.25, 5.79) * mm});
            skLineSegment(sketch, "E713", {"start": v(-49.25, 5.79) * mm, "end": v(-49.2, 5.91) * mm});
            skLineSegment(sketch, "E714", {"start": v(-49.2, 5.91) * mm, "end": v(-49.06, 6.32) * mm});
            skLineSegment(sketch, "E715", {"start": v(-49.06, 6.32) * mm, "end": v(-49.02, 6.46) * mm});
            skLineSegment(sketch, "E716", {"start": v(-49.02, 6.46) * mm, "end": v(-49.02, 13.51) * mm});
            skLineSegment(sketch, "E717", {"start": v(-49.02, 13.51) * mm, "end": v(-49.06, 13.61) * mm});
            skLineSegment(sketch, "E718", {"start": v(-49.06, 13.61) * mm, "end": v(-49.14, 13.86) * mm});
            skLineSegment(sketch, "E719", {"start": v(-49.14, 13.86) * mm, "end": v(-49.21, 14.04) * mm});
            skLineSegment(sketch, "E720", {"start": v(-49.21, 14.04) * mm, "end": v(-49.3, 14.21) * mm});
            skLineSegment(sketch, "E721", {"start": v(-49.3, 14.21) * mm, "end": v(-49.37, 14.31) * mm});
            skLineSegment(sketch, "E722", {"start": v(-49.37, 14.31) * mm, "end": v(-49.4, 14.37) * mm});
            skLineSegment(sketch, "E723", {"start": v(-49.4, 14.37) * mm, "end": v(-49.45, 14.44) * mm});
            skLineSegment(sketch, "E724", {"start": v(-49.45, 14.44) * mm, "end": v(-49.54, 14.53) * mm});
            skLineSegment(sketch, "E725", {"start": v(-49.54, 14.53) * mm, "end": v(-49.8, 14.77) * mm});
            skLineSegment(sketch, "E726", {"start": v(-49.8, 14.77) * mm, "end": v(-49.94, 14.87) * mm});
            skLineSegment(sketch, "E727", {"start": v(-49.94, 14.87) * mm, "end": v(-50.11, 14.96) * mm});
            skLineSegment(sketch, "E728", {"start": v(-50.11, 14.96) * mm, "end": v(-50.3, 15.04) * mm});
            skLineSegment(sketch, "E729", {"start": v(-50.3, 15.04) * mm, "end": v(-50.47, 15.1) * mm});
            skLineSegment(sketch, "E730", {"start": v(-50.47, 15.1) * mm, "end": v(-50.58, 15.12) * mm});
            skLineSegment(sketch, "E731", {"start": v(-50.58, 15.12) * mm, "end": v(-50.7, 15.13) * mm});
            skLineSegment(sketch, "E732", {"start": v(-50.7, 15.13) * mm, "end": v(-50.98, 15.14) * mm});
            skLineSegment(sketch, "E733", {"start": v(-50.98, 15.14) * mm, "end": v(-51.27, 15.13) * mm});
            skLineSegment(sketch, "E734", {"start": v(-35.5, -1) * mm, "end": v(-32.5, -1) * mm});
            skLineSegment(sketch, "E735", {"start": v(-32.5, -1) * mm, "end": v(-32.5, 1) * mm});
            skLineSegment(sketch, "E736", {"start": v(-32.5, 1) * mm, "end": v(-35.5, 1) * mm});
            skLineSegment(sketch, "E737", {"start": v(-35.5, 1) * mm, "end": v(-35.5, -1) * mm});
            skLineSegment(sketch, "E738", {"start": v(-41.5, 21.64) * mm, "end": v(-26.5, 21.64) * mm});
            skLineSegment(sketch, "E739", {"start": v(-26.5, 21.64) * mm, "end": v(-26.5, 30.48) * mm});
            skLineSegment(sketch, "E740", {"start": v(-26.5, 30.48) * mm, "end": v(-41.5, 30.48) * mm});
            skLineSegment(sketch, "E741", {"start": v(-41.5, 30.48) * mm, "end": v(-41.5, 21.64) * mm});
            skArc(sketch, "E742", {"start": v(-33.24, 25.47) * mm, "mid": v(-32.5, 23.7) * mm, "end": v(-30.74, 22.97) * mm});
            skArc(sketch, "E743", {"start": v(-30.74, 22.97) * mm, "mid": v(-28.97, 23.7) * mm, "end": v(-28.24, 25.47) * mm});
            skArc(sketch, "E744", {"start": v(-28.24, 25.47) * mm, "mid": v(-28.97, 27.23) * mm, "end": v(-30.74, 27.97) * mm});
            skArc(sketch, "E745", {"start": v(-30.74, 27.97) * mm, "mid": v(-32.5, 27.23) * mm, "end": v(-33.24, 25.47) * mm});
            skLineSegment(sketch, "E746", {"start": v(-41.5, 30.48) * mm, "end": v(-41.5, 7) * mm});
            skArc(sketch, "E747", {"start": v(-41.5, 7) * mm, "mid": v(-39.74, 2.76) * mm, "end": v(-35.5, 1) * mm});
            skLineSegment(sketch, "E748", {"start": v(-35.5, 1) * mm, "end": v(-32.5, 1) * mm});
            skArc(sketch, "E749", {"start": v(-32.5, 1) * mm, "mid": v(-28.26, 2.76) * mm, "end": v(-26.5, 7) * mm});
            skLineSegment(sketch, "E750", {"start": v(-26.5, 7) * mm, "end": v(-26.5, 30.48) * mm});
            skArc(sketch, "E751", {"start": v(-39.74, 25.47) * mm, "mid": v(-39, 23.7) * mm, "end": v(-37.24, 22.97) * mm});
            skArc(sketch, "E752", {"start": v(-37.24, 22.97) * mm, "mid": v(-35.47, 23.7) * mm, "end": v(-34.74, 25.47) * mm});
            skArc(sketch, "E753", {"start": v(-34.74, 25.47) * mm, "mid": v(-35.47, 27.23) * mm, "end": v(-37.24, 27.97) * mm});
            skArc(sketch, "E754", {"start": v(-37.24, 27.97) * mm, "mid": v(-39, 27.23) * mm, "end": v(-39.74, 25.47) * mm});
            skArc(sketch, "E755", {"start": v(-37.24, 26.97) * mm, "mid": v(-38.3, 26.53) * mm, "end": v(-38.74, 25.47) * mm});
            skArc(sketch, "E756", {"start": v(-38.74, 25.47) * mm, "mid": v(-38.3, 24.4) * mm, "end": v(-37.24, 23.97) * mm});
            skArc(sketch, "E757", {"start": v(-37.24, 23.97) * mm, "mid": v(-36.18, 24.4) * mm, "end": v(-35.74, 25.47) * mm});
            skArc(sketch, "E758", {"start": v(-35.74, 25.47) * mm, "mid": v(-36.18, 26.53) * mm, "end": v(-37.24, 26.97) * mm});
            skArc(sketch, "E759", {"start": v(-30.74, 26.97) * mm, "mid": v(-31.8, 26.53) * mm, "end": v(-32.24, 25.47) * mm});
            skArc(sketch, "E760", {"start": v(-32.24, 25.47) * mm, "mid": v(-31.8, 24.4) * mm, "end": v(-30.74, 23.97) * mm});
            skArc(sketch, "E761", {"start": v(-30.74, 23.97) * mm, "mid": v(-29.67, 24.4) * mm, "end": v(-29.24, 25.47) * mm});
            skArc(sketch, "E762", {"start": v(-29.24, 25.47) * mm, "mid": v(-29.67, 26.53) * mm, "end": v(-30.74, 26.97) * mm});
            skLineSegment(sketch, "E763", {"start": v(-34.27, 15.13) * mm, "end": v(-34.4, 15.12) * mm});
            skLineSegment(sketch, "E764", {"start": v(-34.4, 15.12) * mm, "end": v(-34.5, 15.1) * mm});
            skLineSegment(sketch, "E765", {"start": v(-34.5, 15.1) * mm, "end": v(-34.72, 15.02) * mm});
            skLineSegment(sketch, "E766", {"start": v(-34.72, 15.02) * mm, "end": v(-34.94, 14.91) * mm});
            skLineSegment(sketch, "E767", {"start": v(-34.94, 14.91) * mm, "end": v(-35.15, 14.78) * mm});
            skLineSegment(sketch, "E768", {"start": v(-35.15, 14.78) * mm, "end": v(-35.33, 14.63) * mm});
            skLineSegment(sketch, "E769", {"start": v(-35.33, 14.63) * mm, "end": v(-35.53, 14.44) * mm});
            skLineSegment(sketch, "E770", {"start": v(-35.53, 14.44) * mm, "end": v(-35.6, 14.32) * mm});
            skLineSegment(sketch, "E771", {"start": v(-35.6, 14.32) * mm, "end": v(-35.6, 14.31) * mm});
            skLineSegment(sketch, "E772", {"start": v(-35.6, 14.31) * mm, "end": v(-35.66, 14.21) * mm});
            skLineSegment(sketch, "E773", {"start": v(-35.66, 14.21) * mm, "end": v(-35.76, 14.04) * mm});
            skLineSegment(sketch, "E774", {"start": v(-35.76, 14.04) * mm, "end": v(-35.83, 13.86) * mm});
            skLineSegment(sketch, "E775", {"start": v(-35.83, 13.86) * mm, "end": v(-35.91, 13.61) * mm});
            skLineSegment(sketch, "E776", {"start": v(-35.91, 13.61) * mm, "end": v(-35.95, 13.51) * mm});
            skLineSegment(sketch, "E777", {"start": v(-35.95, 13.51) * mm, "end": v(-35.95, 6.42) * mm});
            skLineSegment(sketch, "E778", {"start": v(-35.95, 6.42) * mm, "end": v(-35.91, 6.33) * mm});
            skLineSegment(sketch, "E779", {"start": v(-35.91, 6.33) * mm, "end": v(-35.84, 6.1) * mm});
            skLineSegment(sketch, "E780", {"start": v(-35.84, 6.1) * mm, "end": v(-35.79, 5.95) * mm});
            skLineSegment(sketch, "E781", {"start": v(-35.79, 5.95) * mm, "end": v(-35.74, 5.83) * mm});
            skLineSegment(sketch, "E782", {"start": v(-35.74, 5.83) * mm, "end": v(-35.67, 5.72) * mm});
            skLineSegment(sketch, "E783", {"start": v(-35.67, 5.72) * mm, "end": v(-35.6, 5.63) * mm});
            skLineSegment(sketch, "E784", {"start": v(-35.6, 5.63) * mm, "end": v(-35.59, 5.62) * mm});
            skLineSegment(sketch, "E785", {"start": v(-35.59, 5.62) * mm, "end": v(-35.58, 5.58) * mm});
            skLineSegment(sketch, "E786", {"start": v(-35.58, 5.58) * mm, "end": v(-35.52, 5.5) * mm});
            skLineSegment(sketch, "E787", {"start": v(-35.52, 5.5) * mm, "end": v(-35.42, 5.39) * mm});
            skLineSegment(sketch, "E788", {"start": v(-35.42, 5.39) * mm, "end": v(-35.22, 5.2) * mm});
            skLineSegment(sketch, "E789", {"start": v(-35.22, 5.2) * mm, "end": v(-35.13, 5.13) * mm});
            skLineSegment(sketch, "E790", {"start": v(-35.13, 5.13) * mm, "end": v(-35.07, 5.1) * mm});
            skLineSegment(sketch, "E791", {"start": v(-35.07, 5.1) * mm, "end": v(-35.04, 5.08) * mm});
            skLineSegment(sketch, "E792", {"start": v(-35.04, 5.08) * mm, "end": v(-34.95, 5.03) * mm});
            skLineSegment(sketch, "E793", {"start": v(-34.95, 5.03) * mm, "end": v(-34.66, 4.89) * mm});
            skLineSegment(sketch, "E794", {"start": v(-34.66, 4.89) * mm, "end": v(-34.51, 4.84) * mm});
            skLineSegment(sketch, "E795", {"start": v(-34.51, 4.84) * mm, "end": v(-34.35, 4.8) * mm});
            skLineSegment(sketch, "E796", {"start": v(-34.35, 4.8) * mm, "end": v(-34.17, 4.78) * mm});
            skLineSegment(sketch, "E797", {"start": v(-34.17, 4.78) * mm, "end": v(-34, 4.78) * mm});
            skLineSegment(sketch, "E798", {"start": v(-34, 4.78) * mm, "end": v(-33.81, 4.78) * mm});
            skLineSegment(sketch, "E799", {"start": v(-33.81, 4.78) * mm, "end": v(-33.64, 4.8) * mm});
            skLineSegment(sketch, "E800", {"start": v(-33.64, 4.8) * mm, "end": v(-33.47, 4.84) * mm});
            skLineSegment(sketch, "E801", {"start": v(-33.47, 4.84) * mm, "end": v(-33.32, 4.89) * mm});
            skLineSegment(sketch, "E802", {"start": v(-33.32, 4.89) * mm, "end": v(-33.02, 5.02) * mm});
            skLineSegment(sketch, "E803", {"start": v(-33.02, 5.02) * mm, "end": v(-32.92, 5.08) * mm});
            skLineSegment(sketch, "E804", {"start": v(-32.92, 5.08) * mm, "end": v(-32.89, 5.11) * mm});
            skLineSegment(sketch, "E805", {"start": v(-32.89, 5.11) * mm, "end": v(-32.86, 5.12) * mm});
            skLineSegment(sketch, "E806", {"start": v(-32.86, 5.12) * mm, "end": v(-32.78, 5.18) * mm});
            skLineSegment(sketch, "E807", {"start": v(-32.78, 5.18) * mm, "end": v(-32.63, 5.31) * mm});
            skLineSegment(sketch, "E808", {"start": v(-32.63, 5.31) * mm, "end": v(-32.48, 5.46) * mm});
            skLineSegment(sketch, "E809", {"start": v(-32.48, 5.46) * mm, "end": v(-32.42, 5.53) * mm});
            skLineSegment(sketch, "E810", {"start": v(-32.42, 5.53) * mm, "end": v(-32.4, 5.6) * mm});
            skLineSegment(sketch, "E811", {"start": v(-32.4, 5.6) * mm, "end": v(-32.38, 5.62) * mm});
            skLineSegment(sketch, "E812", {"start": v(-32.38, 5.62) * mm, "end": v(-32.38, 5.62) * mm});
            skLineSegment(sketch, "E813", {"start": v(-32.38, 5.62) * mm, "end": v(-32.31, 5.7) * mm});
            skLineSegment(sketch, "E814", {"start": v(-32.31, 5.7) * mm, "end": v(-32.25, 5.79) * mm});
            skLineSegment(sketch, "E815", {"start": v(-32.25, 5.79) * mm, "end": v(-32.2, 5.91) * mm});
            skLineSegment(sketch, "E816", {"start": v(-32.2, 5.91) * mm, "end": v(-32.06, 6.32) * mm});
            skLineSegment(sketch, "E817", {"start": v(-32.06, 6.32) * mm, "end": v(-32.02, 6.46) * mm});
            skLineSegment(sketch, "E818", {"start": v(-32.02, 6.46) * mm, "end": v(-32.02, 13.51) * mm});
            skLineSegment(sketch, "E819", {"start": v(-32.02, 13.51) * mm, "end": v(-32.06, 13.61) * mm});
            skLineSegment(sketch, "E820", {"start": v(-32.06, 13.61) * mm, "end": v(-32.14, 13.86) * mm});
            skLineSegment(sketch, "E821", {"start": v(-32.14, 13.86) * mm, "end": v(-32.21, 14.04) * mm});
            skLineSegment(sketch, "E822", {"start": v(-32.21, 14.04) * mm, "end": v(-32.3, 14.21) * mm});
            skLineSegment(sketch, "E823", {"start": v(-32.3, 14.21) * mm, "end": v(-32.37, 14.31) * mm});
            skLineSegment(sketch, "E824", {"start": v(-32.37, 14.31) * mm, "end": v(-32.4, 14.37) * mm});
            skLineSegment(sketch, "E825", {"start": v(-32.4, 14.37) * mm, "end": v(-32.45, 14.44) * mm});
            skLineSegment(sketch, "E826", {"start": v(-32.45, 14.44) * mm, "end": v(-32.54, 14.53) * mm});
            skLineSegment(sketch, "E827", {"start": v(-32.54, 14.53) * mm, "end": v(-32.8, 14.77) * mm});
            skLineSegment(sketch, "E828", {"start": v(-32.8, 14.77) * mm, "end": v(-32.94, 14.87) * mm});
            skLineSegment(sketch, "E829", {"start": v(-32.94, 14.87) * mm, "end": v(-33.11, 14.96) * mm});
            skLineSegment(sketch, "E830", {"start": v(-33.11, 14.96) * mm, "end": v(-33.3, 15.04) * mm});
            skLineSegment(sketch, "E831", {"start": v(-33.3, 15.04) * mm, "end": v(-33.47, 15.1) * mm});
            skLineSegment(sketch, "E832", {"start": v(-33.47, 15.1) * mm, "end": v(-33.58, 15.12) * mm});
            skLineSegment(sketch, "E833", {"start": v(-33.58, 15.12) * mm, "end": v(-33.7, 15.13) * mm});
            skLineSegment(sketch, "E834", {"start": v(-33.7, 15.13) * mm, "end": v(-33.98, 15.14) * mm});
            skLineSegment(sketch, "E835", {"start": v(-33.98, 15.14) * mm, "end": v(-34.27, 15.13) * mm});
            skLineSegment(sketch, "E836", {"start": v(-43.5, 14.24) * mm, "end": v(-41.5, 14.24) * mm});
            skLineSegment(sketch, "E837", {"start": v(-41.5, 14.24) * mm, "end": v(-41.5, 17.24) * mm});
            skLineSegment(sketch, "E838", {"start": v(-41.5, 17.24) * mm, "end": v(-43.5, 17.24) * mm});
            skLineSegment(sketch, "E839", {"start": v(-43.5, 17.24) * mm, "end": v(-43.5, 14.24) * mm});
            skLineSegment(sketch, "E840", {"start": v(-18.5, -1) * mm, "end": v(-15.5, -1) * mm});
            skLineSegment(sketch, "E841", {"start": v(-15.5, -1) * mm, "end": v(-15.5, 1) * mm});
            skLineSegment(sketch, "E842", {"start": v(-15.5, 1) * mm, "end": v(-18.5, 1) * mm});
            skLineSegment(sketch, "E843", {"start": v(-18.5, 1) * mm, "end": v(-18.5, -1) * mm});
            skLineSegment(sketch, "E844", {"start": v(-24.5, 21.64) * mm, "end": v(-9.5, 21.64) * mm});
            skLineSegment(sketch, "E845", {"start": v(-9.5, 21.64) * mm, "end": v(-9.5, 30.48) * mm});
            skLineSegment(sketch, "E846", {"start": v(-9.5, 30.48) * mm, "end": v(-24.5, 30.48) * mm});
            skLineSegment(sketch, "E847", {"start": v(-24.5, 30.48) * mm, "end": v(-24.5, 21.64) * mm});
            skArc(sketch, "E848", {"start": v(-16.24, 25.47) * mm, "mid": v(-15.5, 23.7) * mm, "end": v(-13.74, 22.97) * mm});
            skArc(sketch, "E849", {"start": v(-13.74, 22.97) * mm, "mid": v(-11.97, 23.7) * mm, "end": v(-11.24, 25.47) * mm});
            skArc(sketch, "E850", {"start": v(-11.24, 25.47) * mm, "mid": v(-11.97, 27.23) * mm, "end": v(-13.74, 27.97) * mm});
            skArc(sketch, "E851", {"start": v(-13.74, 27.97) * mm, "mid": v(-15.5, 27.23) * mm, "end": v(-16.24, 25.47) * mm});
            skLineSegment(sketch, "E852", {"start": v(-24.5, 30.48) * mm, "end": v(-24.5, 7) * mm});
            skArc(sketch, "E853", {"start": v(-24.5, 7) * mm, "mid": v(-22.74, 2.76) * mm, "end": v(-18.5, 1) * mm});
            skLineSegment(sketch, "E854", {"start": v(-18.5, 1) * mm, "end": v(-15.5, 1) * mm});
            skArc(sketch, "E855", {"start": v(-15.5, 1) * mm, "mid": v(-11.26, 2.76) * mm, "end": v(-9.5, 7) * mm});
            skLineSegment(sketch, "E856", {"start": v(-9.5, 7) * mm, "end": v(-9.5, 30.48) * mm});
            skArc(sketch, "E857", {"start": v(-22.74, 25.47) * mm, "mid": v(-22, 23.7) * mm, "end": v(-20.24, 22.97) * mm});
            skArc(sketch, "E858", {"start": v(-20.24, 22.97) * mm, "mid": v(-18.47, 23.7) * mm, "end": v(-17.74, 25.47) * mm});
            skArc(sketch, "E859", {"start": v(-17.74, 25.47) * mm, "mid": v(-18.47, 27.23) * mm, "end": v(-20.24, 27.97) * mm});
            skArc(sketch, "E860", {"start": v(-20.24, 27.97) * mm, "mid": v(-22, 27.23) * mm, "end": v(-22.74, 25.47) * mm});
            skArc(sketch, "E861", {"start": v(-20.24, 26.97) * mm, "mid": v(-21.3, 26.53) * mm, "end": v(-21.74, 25.47) * mm});
            skArc(sketch, "E862", {"start": v(-21.74, 25.47) * mm, "mid": v(-21.3, 24.4) * mm, "end": v(-20.24, 23.97) * mm});
            skArc(sketch, "E863", {"start": v(-20.24, 23.97) * mm, "mid": v(-19.18, 24.4) * mm, "end": v(-18.74, 25.47) * mm});
            skArc(sketch, "E864", {"start": v(-18.74, 25.47) * mm, "mid": v(-19.18, 26.53) * mm, "end": v(-20.24, 26.97) * mm});
            skArc(sketch, "E865", {"start": v(-13.74, 26.97) * mm, "mid": v(-14.8, 26.53) * mm, "end": v(-15.24, 25.47) * mm});
            skArc(sketch, "E866", {"start": v(-15.24, 25.47) * mm, "mid": v(-14.8, 24.4) * mm, "end": v(-13.74, 23.97) * mm});
            skArc(sketch, "E867", {"start": v(-13.74, 23.97) * mm, "mid": v(-12.67, 24.4) * mm, "end": v(-12.24, 25.47) * mm});
            skArc(sketch, "E868", {"start": v(-12.24, 25.47) * mm, "mid": v(-12.67, 26.53) * mm, "end": v(-13.74, 26.97) * mm});
            skLineSegment(sketch, "E869", {"start": v(-17.27, 15.13) * mm, "end": v(-17.4, 15.12) * mm});
            skLineSegment(sketch, "E870", {"start": v(-17.4, 15.12) * mm, "end": v(-17.5, 15.1) * mm});
            skLineSegment(sketch, "E871", {"start": v(-17.5, 15.1) * mm, "end": v(-17.72, 15.02) * mm});
            skLineSegment(sketch, "E872", {"start": v(-17.72, 15.02) * mm, "end": v(-17.94, 14.91) * mm});
            skLineSegment(sketch, "E873", {"start": v(-17.94, 14.91) * mm, "end": v(-18.15, 14.78) * mm});
            skLineSegment(sketch, "E874", {"start": v(-18.15, 14.78) * mm, "end": v(-18.33, 14.63) * mm});
            skLineSegment(sketch, "E875", {"start": v(-18.33, 14.63) * mm, "end": v(-18.53, 14.44) * mm});
            skLineSegment(sketch, "E876", {"start": v(-18.53, 14.44) * mm, "end": v(-18.6, 14.32) * mm});
            skLineSegment(sketch, "E877", {"start": v(-18.6, 14.32) * mm, "end": v(-18.6, 14.31) * mm});
            skLineSegment(sketch, "E878", {"start": v(-18.6, 14.31) * mm, "end": v(-18.66, 14.21) * mm});
            skLineSegment(sketch, "E879", {"start": v(-18.66, 14.21) * mm, "end": v(-18.76, 14.04) * mm});
            skLineSegment(sketch, "E880", {"start": v(-18.76, 14.04) * mm, "end": v(-18.83, 13.86) * mm});
            skLineSegment(sketch, "E881", {"start": v(-18.83, 13.86) * mm, "end": v(-18.91, 13.61) * mm});
            skLineSegment(sketch, "E882", {"start": v(-18.91, 13.61) * mm, "end": v(-18.95, 13.51) * mm});
            skLineSegment(sketch, "E883", {"start": v(-18.95, 13.51) * mm, "end": v(-18.95, 6.42) * mm});
            skLineSegment(sketch, "E884", {"start": v(-18.95, 6.42) * mm, "end": v(-18.91, 6.33) * mm});
            skLineSegment(sketch, "E885", {"start": v(-18.91, 6.33) * mm, "end": v(-18.84, 6.1) * mm});
            skLineSegment(sketch, "E886", {"start": v(-18.84, 6.1) * mm, "end": v(-18.79, 5.95) * mm});
            skLineSegment(sketch, "E887", {"start": v(-18.79, 5.95) * mm, "end": v(-18.74, 5.83) * mm});
            skLineSegment(sketch, "E888", {"start": v(-18.74, 5.83) * mm, "end": v(-18.67, 5.72) * mm});
            skLineSegment(sketch, "E889", {"start": v(-18.67, 5.72) * mm, "end": v(-18.6, 5.63) * mm});
            skLineSegment(sketch, "E890", {"start": v(-18.6, 5.63) * mm, "end": v(-18.59, 5.62) * mm});
            skLineSegment(sketch, "E891", {"start": v(-18.59, 5.62) * mm, "end": v(-18.58, 5.58) * mm});
            skLineSegment(sketch, "E892", {"start": v(-18.58, 5.58) * mm, "end": v(-18.52, 5.5) * mm});
            skLineSegment(sketch, "E893", {"start": v(-18.52, 5.5) * mm, "end": v(-18.42, 5.39) * mm});
            skLineSegment(sketch, "E894", {"start": v(-18.42, 5.39) * mm, "end": v(-18.22, 5.2) * mm});
            skLineSegment(sketch, "E895", {"start": v(-18.22, 5.2) * mm, "end": v(-18.13, 5.13) * mm});
            skLineSegment(sketch, "E896", {"start": v(-18.13, 5.13) * mm, "end": v(-18.07, 5.1) * mm});
            skLineSegment(sketch, "E897", {"start": v(-18.07, 5.1) * mm, "end": v(-18.04, 5.08) * mm});
            skLineSegment(sketch, "E898", {"start": v(-18.04, 5.08) * mm, "end": v(-17.95, 5.03) * mm});
            skLineSegment(sketch, "E899", {"start": v(-17.95, 5.03) * mm, "end": v(-17.66, 4.89) * mm});
            skLineSegment(sketch, "E900", {"start": v(-17.66, 4.89) * mm, "end": v(-17.51, 4.84) * mm});
            skLineSegment(sketch, "E901", {"start": v(-17.51, 4.84) * mm, "end": v(-17.35, 4.8) * mm});
            skLineSegment(sketch, "E902", {"start": v(-17.35, 4.8) * mm, "end": v(-17.17, 4.78) * mm});
            skLineSegment(sketch, "E903", {"start": v(-17.17, 4.78) * mm, "end": v(-17, 4.78) * mm});
            skLineSegment(sketch, "E904", {"start": v(-17, 4.78) * mm, "end": v(-16.81, 4.78) * mm});
            skLineSegment(sketch, "E905", {"start": v(-16.81, 4.78) * mm, "end": v(-16.64, 4.8) * mm});
            skLineSegment(sketch, "E906", {"start": v(-16.64, 4.8) * mm, "end": v(-16.47, 4.84) * mm});
            skLineSegment(sketch, "E907", {"start": v(-16.47, 4.84) * mm, "end": v(-16.32, 4.89) * mm});
            skLineSegment(sketch, "E908", {"start": v(-16.32, 4.89) * mm, "end": v(-16.02, 5.02) * mm});
            skLineSegment(sketch, "E909", {"start": v(-16.02, 5.02) * mm, "end": v(-15.92, 5.08) * mm});
            skLineSegment(sketch, "E910", {"start": v(-15.92, 5.08) * mm, "end": v(-15.89, 5.11) * mm});
            skLineSegment(sketch, "E911", {"start": v(-15.89, 5.11) * mm, "end": v(-15.86, 5.12) * mm});
            skLineSegment(sketch, "E912", {"start": v(-15.86, 5.12) * mm, "end": v(-15.78, 5.18) * mm});
            skLineSegment(sketch, "E913", {"start": v(-15.78, 5.18) * mm, "end": v(-15.63, 5.31) * mm});
            skLineSegment(sketch, "E914", {"start": v(-15.63, 5.31) * mm, "end": v(-15.48, 5.46) * mm});
            skLineSegment(sketch, "E915", {"start": v(-15.48, 5.46) * mm, "end": v(-15.42, 5.53) * mm});
            skLineSegment(sketch, "E916", {"start": v(-15.42, 5.53) * mm, "end": v(-15.4, 5.6) * mm});
            skLineSegment(sketch, "E917", {"start": v(-15.4, 5.6) * mm, "end": v(-15.38, 5.62) * mm});
            skLineSegment(sketch, "E918", {"start": v(-15.38, 5.62) * mm, "end": v(-15.38, 5.62) * mm});
            skLineSegment(sketch, "E919", {"start": v(-15.38, 5.62) * mm, "end": v(-15.31, 5.7) * mm});
            skLineSegment(sketch, "E920", {"start": v(-15.31, 5.7) * mm, "end": v(-15.25, 5.79) * mm});
            skLineSegment(sketch, "E921", {"start": v(-15.25, 5.79) * mm, "end": v(-15.2, 5.91) * mm});
            skLineSegment(sketch, "E922", {"start": v(-15.2, 5.91) * mm, "end": v(-15.06, 6.32) * mm});
            skLineSegment(sketch, "E923", {"start": v(-15.06, 6.32) * mm, "end": v(-15.02, 6.46) * mm});
            skLineSegment(sketch, "E924", {"start": v(-15.02, 6.46) * mm, "end": v(-15.02, 13.51) * mm});
            skLineSegment(sketch, "E925", {"start": v(-15.02, 13.51) * mm, "end": v(-15.06, 13.61) * mm});
            skLineSegment(sketch, "E926", {"start": v(-15.06, 13.61) * mm, "end": v(-15.14, 13.86) * mm});
            skLineSegment(sketch, "E927", {"start": v(-15.14, 13.86) * mm, "end": v(-15.21, 14.04) * mm});
            skLineSegment(sketch, "E928", {"start": v(-15.21, 14.04) * mm, "end": v(-15.3, 14.21) * mm});
            skLineSegment(sketch, "E929", {"start": v(-15.3, 14.21) * mm, "end": v(-15.37, 14.31) * mm});
            skLineSegment(sketch, "E930", {"start": v(-15.37, 14.31) * mm, "end": v(-15.4, 14.37) * mm});
            skLineSegment(sketch, "E931", {"start": v(-15.4, 14.37) * mm, "end": v(-15.45, 14.44) * mm});
            skLineSegment(sketch, "E932", {"start": v(-15.45, 14.44) * mm, "end": v(-15.54, 14.53) * mm});
            skLineSegment(sketch, "E933", {"start": v(-15.54, 14.53) * mm, "end": v(-15.8, 14.77) * mm});
            skLineSegment(sketch, "E934", {"start": v(-15.8, 14.77) * mm, "end": v(-15.94, 14.87) * mm});
            skLineSegment(sketch, "E935", {"start": v(-15.94, 14.87) * mm, "end": v(-16.11, 14.96) * mm});
            skLineSegment(sketch, "E936", {"start": v(-16.11, 14.96) * mm, "end": v(-16.3, 15.04) * mm});
            skLineSegment(sketch, "E937", {"start": v(-16.3, 15.04) * mm, "end": v(-16.47, 15.1) * mm});
            skLineSegment(sketch, "E938", {"start": v(-16.47, 15.1) * mm, "end": v(-16.58, 15.12) * mm});
            skLineSegment(sketch, "E939", {"start": v(-16.58, 15.12) * mm, "end": v(-16.7, 15.13) * mm});
            skLineSegment(sketch, "E940", {"start": v(-16.7, 15.13) * mm, "end": v(-16.98, 15.14) * mm});
            skLineSegment(sketch, "E941", {"start": v(-16.98, 15.14) * mm, "end": v(-17.27, 15.13) * mm});
            skLineSegment(sketch, "E942", {"start": v(-26.5, 14.24) * mm, "end": v(-24.5, 14.24) * mm});
            skLineSegment(sketch, "E943", {"start": v(-24.5, 14.24) * mm, "end": v(-24.5, 17.24) * mm});
            skLineSegment(sketch, "E944", {"start": v(-24.5, 17.24) * mm, "end": v(-26.5, 17.24) * mm});
            skLineSegment(sketch, "E945", {"start": v(-26.5, 17.24) * mm, "end": v(-26.5, 14.24) * mm});
            skLineSegment(sketch, "E946", {"start": v(15.5, -1) * mm, "end": v(18.5, -1) * mm});
            skLineSegment(sketch, "E947", {"start": v(18.5, -1) * mm, "end": v(18.5, 1) * mm});
            skLineSegment(sketch, "E948", {"start": v(18.5, 1) * mm, "end": v(15.5, 1) * mm});
            skLineSegment(sketch, "E949", {"start": v(15.5, 1) * mm, "end": v(15.5, -1) * mm});
            skLineSegment(sketch, "E950", {"start": v(9.5, 21.64) * mm, "end": v(24.5, 21.64) * mm});
            skLineSegment(sketch, "E951", {"start": v(24.5, 21.64) * mm, "end": v(24.5, 30.48) * mm});
            skLineSegment(sketch, "E952", {"start": v(24.5, 30.48) * mm, "end": v(9.5, 30.48) * mm});
            skLineSegment(sketch, "E953", {"start": v(9.5, 30.48) * mm, "end": v(9.5, 21.64) * mm});
            skArc(sketch, "E954", {"start": v(17.76, 25.47) * mm, "mid": v(18.5, 23.7) * mm, "end": v(20.26, 22.97) * mm});
            skArc(sketch, "E955", {"start": v(20.26, 22.97) * mm, "mid": v(22.03, 23.7) * mm, "end": v(22.76, 25.47) * mm});
            skArc(sketch, "E956", {"start": v(22.76, 25.47) * mm, "mid": v(22.03, 27.23) * mm, "end": v(20.26, 27.97) * mm});
            skArc(sketch, "E957", {"start": v(20.26, 27.97) * mm, "mid": v(18.5, 27.23) * mm, "end": v(17.76, 25.47) * mm});
            skLineSegment(sketch, "E958", {"start": v(9.5, 30.48) * mm, "end": v(9.5, 7) * mm});
            skArc(sketch, "E959", {"start": v(9.5, 7) * mm, "mid": v(11.26, 2.76) * mm, "end": v(15.5, 1) * mm});
            skLineSegment(sketch, "E960", {"start": v(15.5, 1) * mm, "end": v(18.5, 1) * mm});
            skArc(sketch, "E961", {"start": v(18.5, 1) * mm, "mid": v(22.74, 2.76) * mm, "end": v(24.5, 7) * mm});
            skLineSegment(sketch, "E962", {"start": v(24.5, 7) * mm, "end": v(24.5, 30.48) * mm});
            skArc(sketch, "E963", {"start": v(11.26, 25.47) * mm, "mid": v(12, 23.7) * mm, "end": v(13.76, 22.97) * mm});
            skArc(sketch, "E964", {"start": v(13.76, 22.97) * mm, "mid": v(15.53, 23.7) * mm, "end": v(16.26, 25.47) * mm});
            skArc(sketch, "E965", {"start": v(16.26, 25.47) * mm, "mid": v(15.53, 27.23) * mm, "end": v(13.76, 27.97) * mm});
            skArc(sketch, "E966", {"start": v(13.76, 27.97) * mm, "mid": v(12, 27.23) * mm, "end": v(11.26, 25.47) * mm});
            skArc(sketch, "E967", {"start": v(13.76, 26.97) * mm, "mid": v(12.7, 26.53) * mm, "end": v(12.26, 25.47) * mm});
            skArc(sketch, "E968", {"start": v(12.26, 25.47) * mm, "mid": v(12.7, 24.4) * mm, "end": v(13.76, 23.97) * mm});
            skArc(sketch, "E969", {"start": v(13.76, 23.97) * mm, "mid": v(14.82, 24.4) * mm, "end": v(15.26, 25.47) * mm});
            skArc(sketch, "E970", {"start": v(15.26, 25.47) * mm, "mid": v(14.82, 26.53) * mm, "end": v(13.76, 26.97) * mm});
            skArc(sketch, "E971", {"start": v(20.27, 26.97) * mm, "mid": v(19.2, 26.53) * mm, "end": v(18.77, 25.47) * mm});
            skArc(sketch, "E972", {"start": v(18.77, 25.47) * mm, "mid": v(19.2, 24.4) * mm, "end": v(20.27, 23.97) * mm});
            skArc(sketch, "E973", {"start": v(20.27, 23.97) * mm, "mid": v(21.33, 24.4) * mm, "end": v(21.77, 25.47) * mm});
            skArc(sketch, "E974", {"start": v(21.77, 25.47) * mm, "mid": v(21.33, 26.53) * mm, "end": v(20.27, 26.97) * mm});
            skLineSegment(sketch, "E975", {"start": v(16.73, 15.13) * mm, "end": v(16.6, 15.12) * mm});
            skLineSegment(sketch, "E976", {"start": v(16.6, 15.12) * mm, "end": v(16.5, 15.1) * mm});
            skLineSegment(sketch, "E977", {"start": v(16.5, 15.1) * mm, "end": v(16.28, 15.02) * mm});
            skLineSegment(sketch, "E978", {"start": v(16.28, 15.02) * mm, "end": v(16.06, 14.91) * mm});
            skLineSegment(sketch, "E979", {"start": v(16.06, 14.91) * mm, "end": v(15.85, 14.78) * mm});
            skLineSegment(sketch, "E980", {"start": v(15.85, 14.78) * mm, "end": v(15.67, 14.63) * mm});
            skLineSegment(sketch, "E981", {"start": v(15.67, 14.63) * mm, "end": v(15.47, 14.44) * mm});
            skLineSegment(sketch, "E982", {"start": v(15.47, 14.44) * mm, "end": v(15.4, 14.32) * mm});
            skLineSegment(sketch, "E983", {"start": v(15.4, 14.32) * mm, "end": v(15.4, 14.31) * mm});
            skLineSegment(sketch, "E984", {"start": v(15.4, 14.31) * mm, "end": v(15.34, 14.21) * mm});
            skLineSegment(sketch, "E985", {"start": v(15.34, 14.21) * mm, "end": v(15.24, 14.04) * mm});
            skLineSegment(sketch, "E986", {"start": v(15.24, 14.04) * mm, "end": v(15.17, 13.86) * mm});
            skLineSegment(sketch, "E987", {"start": v(15.17, 13.86) * mm, "end": v(15.09, 13.61) * mm});
            skLineSegment(sketch, "E988", {"start": v(15.09, 13.61) * mm, "end": v(15.05, 13.51) * mm});
            skLineSegment(sketch, "E989", {"start": v(15.05, 13.51) * mm, "end": v(15.05, 6.42) * mm});
            skLineSegment(sketch, "E990", {"start": v(15.05, 6.42) * mm, "end": v(15.09, 6.33) * mm});
            skLineSegment(sketch, "E991", {"start": v(15.09, 6.33) * mm, "end": v(15.16, 6.1) * mm});
            skLineSegment(sketch, "E992", {"start": v(15.16, 6.1) * mm, "end": v(15.21, 5.95) * mm});
            skLineSegment(sketch, "E993", {"start": v(15.21, 5.95) * mm, "end": v(15.26, 5.83) * mm});
            skLineSegment(sketch, "E994", {"start": v(15.26, 5.83) * mm, "end": v(15.33, 5.72) * mm});
            skLineSegment(sketch, "E995", {"start": v(15.33, 5.72) * mm, "end": v(15.4, 5.63) * mm});
            skLineSegment(sketch, "E996", {"start": v(15.4, 5.63) * mm, "end": v(15.41, 5.62) * mm});
            skLineSegment(sketch, "E997", {"start": v(15.41, 5.62) * mm, "end": v(15.42, 5.58) * mm});
            skLineSegment(sketch, "E998", {"start": v(15.42, 5.58) * mm, "end": v(15.48, 5.5) * mm});
            skLineSegment(sketch, "E999", {"start": v(15.48, 5.5) * mm, "end": v(15.58, 5.39) * mm});
            skLineSegment(sketch, "E1000", {"start": v(15.58, 5.39) * mm, "end": v(15.78, 5.2) * mm});
            skLineSegment(sketch, "E1001", {"start": v(15.78, 5.2) * mm, "end": v(15.87, 5.13) * mm});
            skLineSegment(sketch, "E1002", {"start": v(15.87, 5.13) * mm, "end": v(15.93, 5.1) * mm});
            skLineSegment(sketch, "E1003", {"start": v(15.93, 5.1) * mm, "end": v(15.96, 5.08) * mm});
            skLineSegment(sketch, "E1004", {"start": v(15.96, 5.08) * mm, "end": v(16.05, 5.03) * mm});
            skLineSegment(sketch, "E1005", {"start": v(16.05, 5.03) * mm, "end": v(16.34, 4.89) * mm});
            skLineSegment(sketch, "E1006", {"start": v(16.34, 4.89) * mm, "end": v(16.49, 4.84) * mm});
            skLineSegment(sketch, "E1007", {"start": v(16.49, 4.84) * mm, "end": v(16.65, 4.8) * mm});
            skLineSegment(sketch, "E1008", {"start": v(16.65, 4.8) * mm, "end": v(16.83, 4.78) * mm});
            skLineSegment(sketch, "E1009", {"start": v(16.83, 4.78) * mm, "end": v(17, 4.78) * mm});
            skLineSegment(sketch, "E1010", {"start": v(17, 4.78) * mm, "end": v(17.19, 4.78) * mm});
            skLineSegment(sketch, "E1011", {"start": v(17.19, 4.78) * mm, "end": v(17.36, 4.8) * mm});
            skLineSegment(sketch, "E1012", {"start": v(17.36, 4.8) * mm, "end": v(17.53, 4.84) * mm});
            skLineSegment(sketch, "E1013", {"start": v(17.53, 4.84) * mm, "end": v(17.68, 4.89) * mm});
            skLineSegment(sketch, "E1014", {"start": v(17.68, 4.89) * mm, "end": v(17.98, 5.02) * mm});
            skLineSegment(sketch, "E1015", {"start": v(17.98, 5.02) * mm, "end": v(18.08, 5.08) * mm});
            skLineSegment(sketch, "E1016", {"start": v(18.08, 5.08) * mm, "end": v(18.11, 5.11) * mm});
            skLineSegment(sketch, "E1017", {"start": v(18.11, 5.11) * mm, "end": v(18.14, 5.12) * mm});
            skLineSegment(sketch, "E1018", {"start": v(18.14, 5.12) * mm, "end": v(18.22, 5.18) * mm});
            skLineSegment(sketch, "E1019", {"start": v(18.22, 5.18) * mm, "end": v(18.37, 5.31) * mm});
            skLineSegment(sketch, "E1020", {"start": v(18.37, 5.31) * mm, "end": v(18.52, 5.46) * mm});
            skLineSegment(sketch, "E1021", {"start": v(18.52, 5.46) * mm, "end": v(18.58, 5.53) * mm});
            skLineSegment(sketch, "E1022", {"start": v(18.58, 5.53) * mm, "end": v(18.6, 5.6) * mm});
            skLineSegment(sketch, "E1023", {"start": v(18.6, 5.6) * mm, "end": v(18.62, 5.62) * mm});
            skLineSegment(sketch, "E1024", {"start": v(18.62, 5.62) * mm, "end": v(18.62, 5.62) * mm});
            skLineSegment(sketch, "E1025", {"start": v(18.62, 5.62) * mm, "end": v(18.69, 5.7) * mm});
            skLineSegment(sketch, "E1026", {"start": v(18.69, 5.7) * mm, "end": v(18.75, 5.79) * mm});
            skLineSegment(sketch, "E1027", {"start": v(18.75, 5.79) * mm, "end": v(18.8, 5.91) * mm});
            skLineSegment(sketch, "E1028", {"start": v(18.8, 5.91) * mm, "end": v(18.94, 6.32) * mm});
            skLineSegment(sketch, "E1029", {"start": v(18.94, 6.32) * mm, "end": v(18.98, 6.46) * mm});
            skLineSegment(sketch, "E1030", {"start": v(18.98, 6.46) * mm, "end": v(18.98, 13.51) * mm});
            skLineSegment(sketch, "E1031", {"start": v(18.98, 13.51) * mm, "end": v(18.94, 13.61) * mm});
            skLineSegment(sketch, "E1032", {"start": v(18.94, 13.61) * mm, "end": v(18.86, 13.86) * mm});
            skLineSegment(sketch, "E1033", {"start": v(18.86, 13.86) * mm, "end": v(18.79, 14.04) * mm});
            skLineSegment(sketch, "E1034", {"start": v(18.79, 14.04) * mm, "end": v(18.7, 14.21) * mm});
            skLineSegment(sketch, "E1035", {"start": v(18.7, 14.21) * mm, "end": v(18.63, 14.31) * mm});
            skLineSegment(sketch, "E1036", {"start": v(18.63, 14.31) * mm, "end": v(18.6, 14.37) * mm});
            skLineSegment(sketch, "E1037", {"start": v(18.6, 14.37) * mm, "end": v(18.55, 14.44) * mm});
            skLineSegment(sketch, "E1038", {"start": v(18.55, 14.44) * mm, "end": v(18.46, 14.53) * mm});
            skLineSegment(sketch, "E1039", {"start": v(18.46, 14.53) * mm, "end": v(18.2, 14.77) * mm});
            skLineSegment(sketch, "E1040", {"start": v(18.2, 14.77) * mm, "end": v(18.06, 14.87) * mm});
            skLineSegment(sketch, "E1041", {"start": v(18.06, 14.87) * mm, "end": v(17.89, 14.96) * mm});
            skLineSegment(sketch, "E1042", {"start": v(17.89, 14.96) * mm, "end": v(17.7, 15.04) * mm});
            skLineSegment(sketch, "E1043", {"start": v(17.7, 15.04) * mm, "end": v(17.53, 15.1) * mm});
            skLineSegment(sketch, "E1044", {"start": v(17.53, 15.1) * mm, "end": v(17.42, 15.12) * mm});
            skLineSegment(sketch, "E1045", {"start": v(17.42, 15.12) * mm, "end": v(17.3, 15.13) * mm});
            skLineSegment(sketch, "E1046", {"start": v(17.3, 15.13) * mm, "end": v(17.02, 15.14) * mm});
            skLineSegment(sketch, "E1047", {"start": v(17.02, 15.14) * mm, "end": v(16.73, 15.13) * mm});
            skLineSegment(sketch, "E1048", {"start": v(7.5, 14.24) * mm, "end": v(9.5, 14.24) * mm});
            skLineSegment(sketch, "E1049", {"start": v(9.5, 14.24) * mm, "end": v(9.5, 17.24) * mm});
            skLineSegment(sketch, "E1050", {"start": v(9.5, 17.24) * mm, "end": v(7.5, 17.24) * mm});
            skLineSegment(sketch, "E1051", {"start": v(7.5, 17.24) * mm, "end": v(7.5, 14.24) * mm});
            skLineSegment(sketch, "E1052", {"start": v(32.5, -1) * mm, "end": v(35.5, -1) * mm});
            skLineSegment(sketch, "E1053", {"start": v(35.5, -1) * mm, "end": v(35.5, 1) * mm});
            skLineSegment(sketch, "E1054", {"start": v(35.5, 1) * mm, "end": v(32.5, 1) * mm});
            skLineSegment(sketch, "E1055", {"start": v(32.5, 1) * mm, "end": v(32.5, -1) * mm});
            skLineSegment(sketch, "E1056", {"start": v(26.5, 21.64) * mm, "end": v(41.5, 21.64) * mm});
            skLineSegment(sketch, "E1057", {"start": v(41.5, 21.64) * mm, "end": v(41.5, 30.48) * mm});
            skLineSegment(sketch, "E1058", {"start": v(41.5, 30.48) * mm, "end": v(26.5, 30.48) * mm});
            skLineSegment(sketch, "E1059", {"start": v(26.5, 30.48) * mm, "end": v(26.5, 21.64) * mm});
            skArc(sketch, "E1060", {"start": v(34.76, 25.47) * mm, "mid": v(35.5, 23.7) * mm, "end": v(37.26, 22.97) * mm});
            skArc(sketch, "E1061", {"start": v(37.26, 22.97) * mm, "mid": v(39.03, 23.7) * mm, "end": v(39.76, 25.47) * mm});
            skArc(sketch, "E1062", {"start": v(39.76, 25.47) * mm, "mid": v(39.03, 27.23) * mm, "end": v(37.26, 27.97) * mm});
            skArc(sketch, "E1063", {"start": v(37.26, 27.97) * mm, "mid": v(35.5, 27.23) * mm, "end": v(34.76, 25.47) * mm});
            skLineSegment(sketch, "E1064", {"start": v(26.5, 30.48) * mm, "end": v(26.5, 7) * mm});
            skArc(sketch, "E1065", {"start": v(26.5, 7) * mm, "mid": v(28.26, 2.76) * mm, "end": v(32.5, 1) * mm});
            skLineSegment(sketch, "E1066", {"start": v(32.5, 1) * mm, "end": v(35.5, 1) * mm});
            skArc(sketch, "E1067", {"start": v(35.5, 1) * mm, "mid": v(39.74, 2.76) * mm, "end": v(41.5, 7) * mm});
            skLineSegment(sketch, "E1068", {"start": v(41.5, 7) * mm, "end": v(41.5, 30.48) * mm});
            skArc(sketch, "E1069", {"start": v(28.26, 25.47) * mm, "mid": v(29, 23.7) * mm, "end": v(30.76, 22.97) * mm});
            skArc(sketch, "E1070", {"start": v(30.76, 22.97) * mm, "mid": v(32.53, 23.7) * mm, "end": v(33.26, 25.47) * mm});
            skArc(sketch, "E1071", {"start": v(33.26, 25.47) * mm, "mid": v(32.53, 27.23) * mm, "end": v(30.76, 27.97) * mm});
            skArc(sketch, "E1072", {"start": v(30.76, 27.97) * mm, "mid": v(29, 27.23) * mm, "end": v(28.26, 25.47) * mm});
            skArc(sketch, "E1073", {"start": v(30.76, 26.97) * mm, "mid": v(29.7, 26.53) * mm, "end": v(29.26, 25.47) * mm});
            skArc(sketch, "E1074", {"start": v(29.26, 25.47) * mm, "mid": v(29.7, 24.4) * mm, "end": v(30.76, 23.97) * mm});
            skArc(sketch, "E1075", {"start": v(30.76, 23.97) * mm, "mid": v(31.82, 24.4) * mm, "end": v(32.26, 25.47) * mm});
            skArc(sketch, "E1076", {"start": v(32.26, 25.47) * mm, "mid": v(31.82, 26.53) * mm, "end": v(30.76, 26.97) * mm});
            skArc(sketch, "E1077", {"start": v(37.27, 26.97) * mm, "mid": v(36.2, 26.53) * mm, "end": v(35.77, 25.47) * mm});
            skArc(sketch, "E1078", {"start": v(35.77, 25.47) * mm, "mid": v(36.2, 24.4) * mm, "end": v(37.27, 23.97) * mm});
            skArc(sketch, "E1079", {"start": v(37.27, 23.97) * mm, "mid": v(38.33, 24.4) * mm, "end": v(38.77, 25.47) * mm});
            skArc(sketch, "E1080", {"start": v(38.77, 25.47) * mm, "mid": v(38.33, 26.53) * mm, "end": v(37.27, 26.97) * mm});
            skLineSegment(sketch, "E1081", {"start": v(33.73, 15.13) * mm, "end": v(33.6, 15.12) * mm});
            skLineSegment(sketch, "E1082", {"start": v(33.6, 15.12) * mm, "end": v(33.5, 15.1) * mm});
            skLineSegment(sketch, "E1083", {"start": v(33.5, 15.1) * mm, "end": v(33.28, 15.02) * mm});
            skLineSegment(sketch, "E1084", {"start": v(33.28, 15.02) * mm, "end": v(33.06, 14.91) * mm});
            skLineSegment(sketch, "E1085", {"start": v(33.06, 14.91) * mm, "end": v(32.85, 14.78) * mm});
            skLineSegment(sketch, "E1086", {"start": v(32.85, 14.78) * mm, "end": v(32.67, 14.63) * mm});
            skLineSegment(sketch, "E1087", {"start": v(32.67, 14.63) * mm, "end": v(32.47, 14.44) * mm});
            skLineSegment(sketch, "E1088", {"start": v(32.47, 14.44) * mm, "end": v(32.4, 14.32) * mm});
            skLineSegment(sketch, "E1089", {"start": v(32.4, 14.32) * mm, "end": v(32.4, 14.31) * mm});
            skLineSegment(sketch, "E1090", {"start": v(32.4, 14.31) * mm, "end": v(32.34, 14.21) * mm});
            skLineSegment(sketch, "E1091", {"start": v(32.34, 14.21) * mm, "end": v(32.24, 14.04) * mm});
            skLineSegment(sketch, "E1092", {"start": v(32.24, 14.04) * mm, "end": v(32.17, 13.86) * mm});
            skLineSegment(sketch, "E1093", {"start": v(32.17, 13.86) * mm, "end": v(32.09, 13.61) * mm});
            skLineSegment(sketch, "E1094", {"start": v(32.09, 13.61) * mm, "end": v(32.05, 13.51) * mm});
            skLineSegment(sketch, "E1095", {"start": v(32.05, 13.51) * mm, "end": v(32.05, 6.42) * mm});
            skLineSegment(sketch, "E1096", {"start": v(32.05, 6.42) * mm, "end": v(32.09, 6.33) * mm});
            skLineSegment(sketch, "E1097", {"start": v(32.09, 6.33) * mm, "end": v(32.16, 6.1) * mm});
            skLineSegment(sketch, "E1098", {"start": v(32.16, 6.1) * mm, "end": v(32.21, 5.95) * mm});
            skLineSegment(sketch, "E1099", {"start": v(32.21, 5.95) * mm, "end": v(32.26, 5.83) * mm});
            skLineSegment(sketch, "E1100", {"start": v(32.26, 5.83) * mm, "end": v(32.33, 5.72) * mm});
            skLineSegment(sketch, "E1101", {"start": v(32.33, 5.72) * mm, "end": v(32.4, 5.63) * mm});
            skLineSegment(sketch, "E1102", {"start": v(32.4, 5.63) * mm, "end": v(32.41, 5.62) * mm});
            skLineSegment(sketch, "E1103", {"start": v(32.41, 5.62) * mm, "end": v(32.42, 5.58) * mm});
            skLineSegment(sketch, "E1104", {"start": v(32.42, 5.58) * mm, "end": v(32.48, 5.5) * mm});
            skLineSegment(sketch, "E1105", {"start": v(32.48, 5.5) * mm, "end": v(32.58, 5.39) * mm});
            skLineSegment(sketch, "E1106", {"start": v(32.58, 5.39) * mm, "end": v(32.78, 5.2) * mm});
            skLineSegment(sketch, "E1107", {"start": v(32.78, 5.2) * mm, "end": v(32.87, 5.13) * mm});
            skLineSegment(sketch, "E1108", {"start": v(32.87, 5.13) * mm, "end": v(32.93, 5.1) * mm});
            skLineSegment(sketch, "E1109", {"start": v(32.93, 5.1) * mm, "end": v(32.96, 5.08) * mm});
            skLineSegment(sketch, "E1110", {"start": v(32.96, 5.08) * mm, "end": v(33.05, 5.03) * mm});
            skLineSegment(sketch, "E1111", {"start": v(33.05, 5.03) * mm, "end": v(33.34, 4.89) * mm});
            skLineSegment(sketch, "E1112", {"start": v(33.34, 4.89) * mm, "end": v(33.49, 4.84) * mm});
            skLineSegment(sketch, "E1113", {"start": v(33.49, 4.84) * mm, "end": v(33.65, 4.8) * mm});
            skLineSegment(sketch, "E1114", {"start": v(33.65, 4.8) * mm, "end": v(33.83, 4.78) * mm});
            skLineSegment(sketch, "E1115", {"start": v(33.83, 4.78) * mm, "end": v(34, 4.78) * mm});
            skLineSegment(sketch, "E1116", {"start": v(34, 4.78) * mm, "end": v(34.19, 4.78) * mm});
            skLineSegment(sketch, "E1117", {"start": v(34.19, 4.78) * mm, "end": v(34.36, 4.8) * mm});
            skLineSegment(sketch, "E1118", {"start": v(34.36, 4.8) * mm, "end": v(34.53, 4.84) * mm});
            skLineSegment(sketch, "E1119", {"start": v(34.53, 4.84) * mm, "end": v(34.68, 4.89) * mm});
            skLineSegment(sketch, "E1120", {"start": v(34.68, 4.89) * mm, "end": v(34.98, 5.02) * mm});
            skLineSegment(sketch, "E1121", {"start": v(34.98, 5.02) * mm, "end": v(35.08, 5.08) * mm});
            skLineSegment(sketch, "E1122", {"start": v(35.08, 5.08) * mm, "end": v(35.11, 5.11) * mm});
            skLineSegment(sketch, "E1123", {"start": v(35.11, 5.11) * mm, "end": v(35.14, 5.12) * mm});
            skLineSegment(sketch, "E1124", {"start": v(35.14, 5.12) * mm, "end": v(35.22, 5.18) * mm});
            skLineSegment(sketch, "E1125", {"start": v(35.22, 5.18) * mm, "end": v(35.37, 5.31) * mm});
            skLineSegment(sketch, "E1126", {"start": v(35.37, 5.31) * mm, "end": v(35.52, 5.46) * mm});
            skLineSegment(sketch, "E1127", {"start": v(35.52, 5.46) * mm, "end": v(35.58, 5.53) * mm});
            skLineSegment(sketch, "E1128", {"start": v(35.58, 5.53) * mm, "end": v(35.6, 5.6) * mm});
            skLineSegment(sketch, "E1129", {"start": v(35.6, 5.6) * mm, "end": v(35.62, 5.62) * mm});
            skLineSegment(sketch, "E1130", {"start": v(35.62, 5.62) * mm, "end": v(35.62, 5.62) * mm});
            skLineSegment(sketch, "E1131", {"start": v(35.62, 5.62) * mm, "end": v(35.69, 5.7) * mm});
            skLineSegment(sketch, "E1132", {"start": v(35.69, 5.7) * mm, "end": v(35.75, 5.79) * mm});
            skLineSegment(sketch, "E1133", {"start": v(35.75, 5.79) * mm, "end": v(35.8, 5.91) * mm});
            skLineSegment(sketch, "E1134", {"start": v(35.8, 5.91) * mm, "end": v(35.94, 6.32) * mm});
            skLineSegment(sketch, "E1135", {"start": v(35.94, 6.32) * mm, "end": v(35.98, 6.46) * mm});
            skLineSegment(sketch, "E1136", {"start": v(35.98, 6.46) * mm, "end": v(35.98, 13.51) * mm});
            skLineSegment(sketch, "E1137", {"start": v(35.98, 13.51) * mm, "end": v(35.94, 13.61) * mm});
            skLineSegment(sketch, "E1138", {"start": v(35.94, 13.61) * mm, "end": v(35.86, 13.86) * mm});
            skLineSegment(sketch, "E1139", {"start": v(35.86, 13.86) * mm, "end": v(35.79, 14.04) * mm});
            skLineSegment(sketch, "E1140", {"start": v(35.79, 14.04) * mm, "end": v(35.7, 14.21) * mm});
            skLineSegment(sketch, "E1141", {"start": v(35.7, 14.21) * mm, "end": v(35.63, 14.31) * mm});
            skLineSegment(sketch, "E1142", {"start": v(35.63, 14.31) * mm, "end": v(35.6, 14.37) * mm});
            skLineSegment(sketch, "E1143", {"start": v(35.6, 14.37) * mm, "end": v(35.55, 14.44) * mm});
            skLineSegment(sketch, "E1144", {"start": v(35.55, 14.44) * mm, "end": v(35.46, 14.53) * mm});
            skLineSegment(sketch, "E1145", {"start": v(35.46, 14.53) * mm, "end": v(35.2, 14.77) * mm});
            skLineSegment(sketch, "E1146", {"start": v(35.2, 14.77) * mm, "end": v(35.06, 14.87) * mm});
            skLineSegment(sketch, "E1147", {"start": v(35.06, 14.87) * mm, "end": v(34.89, 14.96) * mm});
            skLineSegment(sketch, "E1148", {"start": v(34.89, 14.96) * mm, "end": v(34.7, 15.04) * mm});
            skLineSegment(sketch, "E1149", {"start": v(34.7, 15.04) * mm, "end": v(34.53, 15.1) * mm});
            skLineSegment(sketch, "E1150", {"start": v(34.53, 15.1) * mm, "end": v(34.42, 15.12) * mm});
            skLineSegment(sketch, "E1151", {"start": v(34.42, 15.12) * mm, "end": v(34.3, 15.13) * mm});
            skLineSegment(sketch, "E1152", {"start": v(34.3, 15.13) * mm, "end": v(34.02, 15.14) * mm});
            skLineSegment(sketch, "E1153", {"start": v(34.02, 15.14) * mm, "end": v(33.73, 15.13) * mm});
            skLineSegment(sketch, "E1154", {"start": v(24.5, 14.24) * mm, "end": v(26.5, 14.24) * mm});
            skLineSegment(sketch, "E1155", {"start": v(26.5, 14.24) * mm, "end": v(26.5, 17.24) * mm});
            skLineSegment(sketch, "E1156", {"start": v(26.5, 17.24) * mm, "end": v(24.5, 17.24) * mm});
            skLineSegment(sketch, "E1157", {"start": v(24.5, 17.24) * mm, "end": v(24.5, 14.24) * mm});
            skLineSegment(sketch, "E1158", {"start": v(-1.5, -1) * mm, "end": v(1.5, -1) * mm});
            skLineSegment(sketch, "E1159", {"start": v(1.5, -1) * mm, "end": v(1.5, 1) * mm});
            skLineSegment(sketch, "E1160", {"start": v(1.5, 1) * mm, "end": v(-1.5, 1) * mm});
            skLineSegment(sketch, "E1161", {"start": v(-1.5, 1) * mm, "end": v(-1.5, -1) * mm});
            skLineSegment(sketch, "E1162", {"start": v(-7.5, 21.64) * mm, "end": v(7.5, 21.64) * mm});
            skLineSegment(sketch, "E1163", {"start": v(7.5, 21.64) * mm, "end": v(7.5, 30.48) * mm});
            skLineSegment(sketch, "E1164", {"start": v(7.5, 30.48) * mm, "end": v(-7.5, 30.48) * mm});
            skLineSegment(sketch, "E1165", {"start": v(-7.5, 30.48) * mm, "end": v(-7.5, 21.64) * mm});
            skArc(sketch, "E1166", {"start": v(0.76, 25.47) * mm, "mid": v(1.5, 23.7) * mm, "end": v(3.26, 22.97) * mm});
            skArc(sketch, "E1167", {"start": v(3.26, 22.97) * mm, "mid": v(5.03, 23.7) * mm, "end": v(5.76, 25.47) * mm});
            skArc(sketch, "E1168", {"start": v(5.76, 25.47) * mm, "mid": v(5.03, 27.23) * mm, "end": v(3.26, 27.97) * mm});
            skArc(sketch, "E1169", {"start": v(3.26, 27.97) * mm, "mid": v(1.5, 27.23) * mm, "end": v(0.76, 25.47) * mm});
            skLineSegment(sketch, "E1170", {"start": v(-7.5, 30.48) * mm, "end": v(-7.5, 7) * mm});
            skArc(sketch, "E1171", {"start": v(-7.5, 7) * mm, "mid": v(-5.74, 2.76) * mm, "end": v(-1.5, 1) * mm});
            skLineSegment(sketch, "E1172", {"start": v(-1.5, 1) * mm, "end": v(1.5, 1) * mm});
            skArc(sketch, "E1173", {"start": v(1.5, 1) * mm, "mid": v(5.74, 2.76) * mm, "end": v(7.5, 7) * mm});
            skLineSegment(sketch, "E1174", {"start": v(7.5, 7) * mm, "end": v(7.5, 30.48) * mm});
            skArc(sketch, "E1175", {"start": v(-5.74, 25.47) * mm, "mid": v(-5, 23.7) * mm, "end": v(-3.24, 22.97) * mm});
            skArc(sketch, "E1176", {"start": v(-3.24, 22.97) * mm, "mid": v(-1.47, 23.7) * mm, "end": v(-0.74, 25.47) * mm});
            skArc(sketch, "E1177", {"start": v(-0.74, 25.47) * mm, "mid": v(-1.47, 27.23) * mm, "end": v(-3.24, 27.97) * mm});
            skArc(sketch, "E1178", {"start": v(-3.24, 27.97) * mm, "mid": v(-5, 27.23) * mm, "end": v(-5.74, 25.47) * mm});
            skArc(sketch, "E1179", {"start": v(-3.24, 26.97) * mm, "mid": v(-4.3, 26.53) * mm, "end": v(-4.74, 25.47) * mm});
            skArc(sketch, "E1180", {"start": v(-4.74, 25.47) * mm, "mid": v(-4.3, 24.4) * mm, "end": v(-3.24, 23.97) * mm});
            skArc(sketch, "E1181", {"start": v(-3.24, 23.97) * mm, "mid": v(-2.18, 24.4) * mm, "end": v(-1.74, 25.47) * mm});
            skArc(sketch, "E1182", {"start": v(-1.74, 25.47) * mm, "mid": v(-2.18, 26.53) * mm, "end": v(-3.24, 26.97) * mm});
            skArc(sketch, "E1183", {"start": v(3.26, 26.97) * mm, "mid": v(2.2, 26.53) * mm, "end": v(1.76, 25.47) * mm});
            skArc(sketch, "E1184", {"start": v(1.76, 25.47) * mm, "mid": v(2.2, 24.4) * mm, "end": v(3.26, 23.97) * mm});
            skArc(sketch, "E1185", {"start": v(3.26, 23.97) * mm, "mid": v(4.33, 24.4) * mm, "end": v(4.76, 25.47) * mm});
            skArc(sketch, "E1186", {"start": v(4.76, 25.47) * mm, "mid": v(4.33, 26.53) * mm, "end": v(3.26, 26.97) * mm});
            skLineSegment(sketch, "E1187", {"start": v(-0.27, 15.13) * mm, "end": v(-0.4, 15.12) * mm});
            skLineSegment(sketch, "E1188", {"start": v(-0.4, 15.12) * mm, "end": v(-0.5, 15.1) * mm});
            skLineSegment(sketch, "E1189", {"start": v(-0.5, 15.1) * mm, "end": v(-0.72, 15.02) * mm});
            skLineSegment(sketch, "E1190", {"start": v(-0.72, 15.02) * mm, "end": v(-0.94, 14.91) * mm});
            skLineSegment(sketch, "E1191", {"start": v(-0.94, 14.91) * mm, "end": v(-1.15, 14.78) * mm});
            skLineSegment(sketch, "E1192", {"start": v(-1.15, 14.78) * mm, "end": v(-1.33, 14.63) * mm});
            skLineSegment(sketch, "E1193", {"start": v(-1.33, 14.63) * mm, "end": v(-1.53, 14.44) * mm});
            skLineSegment(sketch, "E1194", {"start": v(-1.53, 14.44) * mm, "end": v(-1.6, 14.32) * mm});
            skLineSegment(sketch, "E1195", {"start": v(-1.6, 14.32) * mm, "end": v(-1.6, 14.31) * mm});
            skLineSegment(sketch, "E1196", {"start": v(-1.6, 14.31) * mm, "end": v(-1.66, 14.21) * mm});
            skLineSegment(sketch, "E1197", {"start": v(-1.66, 14.21) * mm, "end": v(-1.76, 14.04) * mm});
            skLineSegment(sketch, "E1198", {"start": v(-1.76, 14.04) * mm, "end": v(-1.83, 13.86) * mm});
            skLineSegment(sketch, "E1199", {"start": v(-1.83, 13.86) * mm, "end": v(-1.91, 13.61) * mm});
            skLineSegment(sketch, "E1200", {"start": v(-1.91, 13.61) * mm, "end": v(-1.95, 13.51) * mm});
            skLineSegment(sketch, "E1201", {"start": v(-1.95, 13.51) * mm, "end": v(-1.95, 6.42) * mm});
            skLineSegment(sketch, "E1202", {"start": v(-1.95, 6.42) * mm, "end": v(-1.91, 6.33) * mm});
            skLineSegment(sketch, "E1203", {"start": v(-1.91, 6.33) * mm, "end": v(-1.84, 6.1) * mm});
            skLineSegment(sketch, "E1204", {"start": v(-1.84, 6.1) * mm, "end": v(-1.79, 5.95) * mm});
            skLineSegment(sketch, "E1205", {"start": v(-1.79, 5.95) * mm, "end": v(-1.74, 5.83) * mm});
            skLineSegment(sketch, "E1206", {"start": v(-1.74, 5.83) * mm, "end": v(-1.67, 5.72) * mm});
            skLineSegment(sketch, "E1207", {"start": v(-1.67, 5.72) * mm, "end": v(-1.6, 5.63) * mm});
            skLineSegment(sketch, "E1208", {"start": v(-1.6, 5.63) * mm, "end": v(-1.59, 5.62) * mm});
            skLineSegment(sketch, "E1209", {"start": v(-1.59, 5.62) * mm, "end": v(-1.58, 5.58) * mm});
            skLineSegment(sketch, "E1210", {"start": v(-1.58, 5.58) * mm, "end": v(-1.52, 5.5) * mm});
            skLineSegment(sketch, "E1211", {"start": v(-1.52, 5.5) * mm, "end": v(-1.42, 5.39) * mm});
            skLineSegment(sketch, "E1212", {"start": v(-1.42, 5.39) * mm, "end": v(-1.22, 5.2) * mm});
            skLineSegment(sketch, "E1213", {"start": v(-1.22, 5.2) * mm, "end": v(-1.13, 5.13) * mm});
            skLineSegment(sketch, "E1214", {"start": v(-1.13, 5.13) * mm, "end": v(-1.07, 5.1) * mm});
            skLineSegment(sketch, "E1215", {"start": v(-1.07, 5.1) * mm, "end": v(-1.04, 5.08) * mm});
            skLineSegment(sketch, "E1216", {"start": v(-1.04, 5.08) * mm, "end": v(-0.95, 5.03) * mm});
            skLineSegment(sketch, "E1217", {"start": v(-0.95, 5.03) * mm, "end": v(-0.66, 4.89) * mm});
            skLineSegment(sketch, "E1218", {"start": v(-0.66, 4.89) * mm, "end": v(-0.51, 4.84) * mm});
            skLineSegment(sketch, "E1219", {"start": v(-0.51, 4.84) * mm, "end": v(-0.35, 4.8) * mm});
            skLineSegment(sketch, "E1220", {"start": v(-0.35, 4.8) * mm, "end": v(-0.17, 4.78) * mm});
            skLineSegment(sketch, "E1221", {"start": v(-0.17, 4.78) * mm, "end": v(0, 4.78) * mm});
            skLineSegment(sketch, "E1222", {"start": v(0, 4.78) * mm, "end": v(0.19, 4.78) * mm});
            skLineSegment(sketch, "E1223", {"start": v(0.19, 4.78) * mm, "end": v(0.36, 4.8) * mm});
            skLineSegment(sketch, "E1224", {"start": v(0.36, 4.8) * mm, "end": v(0.53, 4.84) * mm});
            skLineSegment(sketch, "E1225", {"start": v(0.53, 4.84) * mm, "end": v(0.68, 4.89) * mm});
            skLineSegment(sketch, "E1226", {"start": v(0.68, 4.89) * mm, "end": v(0.98, 5.02) * mm});
            skLineSegment(sketch, "E1227", {"start": v(0.98, 5.02) * mm, "end": v(1.08, 5.08) * mm});
            skLineSegment(sketch, "E1228", {"start": v(1.08, 5.08) * mm, "end": v(1.11, 5.11) * mm});
            skLineSegment(sketch, "E1229", {"start": v(1.11, 5.11) * mm, "end": v(1.14, 5.12) * mm});
            skLineSegment(sketch, "E1230", {"start": v(1.14, 5.12) * mm, "end": v(1.22, 5.18) * mm});
            skLineSegment(sketch, "E1231", {"start": v(1.22, 5.18) * mm, "end": v(1.37, 5.31) * mm});
            skLineSegment(sketch, "E1232", {"start": v(1.37, 5.31) * mm, "end": v(1.52, 5.46) * mm});
            skLineSegment(sketch, "E1233", {"start": v(1.52, 5.46) * mm, "end": v(1.58, 5.53) * mm});
            skLineSegment(sketch, "E1234", {"start": v(1.58, 5.53) * mm, "end": v(1.6, 5.6) * mm});
            skLineSegment(sketch, "E1235", {"start": v(1.6, 5.6) * mm, "end": v(1.62, 5.62) * mm});
            skLineSegment(sketch, "E1236", {"start": v(1.62, 5.62) * mm, "end": v(1.62, 5.62) * mm});
            skLineSegment(sketch, "E1237", {"start": v(1.62, 5.62) * mm, "end": v(1.69, 5.7) * mm});
            skLineSegment(sketch, "E1238", {"start": v(1.69, 5.7) * mm, "end": v(1.75, 5.79) * mm});
            skLineSegment(sketch, "E1239", {"start": v(1.75, 5.79) * mm, "end": v(1.8, 5.91) * mm});
            skLineSegment(sketch, "E1240", {"start": v(1.8, 5.91) * mm, "end": v(1.94, 6.32) * mm});
            skLineSegment(sketch, "E1241", {"start": v(1.94, 6.32) * mm, "end": v(1.98, 6.46) * mm});
            skLineSegment(sketch, "E1242", {"start": v(1.98, 6.46) * mm, "end": v(1.98, 13.51) * mm});
            skLineSegment(sketch, "E1243", {"start": v(1.98, 13.51) * mm, "end": v(1.94, 13.61) * mm});
            skLineSegment(sketch, "E1244", {"start": v(1.94, 13.61) * mm, "end": v(1.86, 13.86) * mm});
            skLineSegment(sketch, "E1245", {"start": v(1.86, 13.86) * mm, "end": v(1.79, 14.04) * mm});
            skLineSegment(sketch, "E1246", {"start": v(1.79, 14.04) * mm, "end": v(1.7, 14.21) * mm});
            skLineSegment(sketch, "E1247", {"start": v(1.7, 14.21) * mm, "end": v(1.63, 14.31) * mm});
            skLineSegment(sketch, "E1248", {"start": v(1.63, 14.31) * mm, "end": v(1.6, 14.37) * mm});
            skLineSegment(sketch, "E1249", {"start": v(1.6, 14.37) * mm, "end": v(1.55, 14.44) * mm});
            skLineSegment(sketch, "E1250", {"start": v(1.55, 14.44) * mm, "end": v(1.46, 14.53) * mm});
            skLineSegment(sketch, "E1251", {"start": v(1.46, 14.53) * mm, "end": v(1.2, 14.77) * mm});
            skLineSegment(sketch, "E1252", {"start": v(1.2, 14.77) * mm, "end": v(1.06, 14.87) * mm});
            skLineSegment(sketch, "E1253", {"start": v(1.06, 14.87) * mm, "end": v(0.89, 14.96) * mm});
            skLineSegment(sketch, "E1254", {"start": v(0.89, 14.96) * mm, "end": v(0.7, 15.04) * mm});
            skLineSegment(sketch, "E1255", {"start": v(0.7, 15.04) * mm, "end": v(0.53, 15.1) * mm});
            skLineSegment(sketch, "E1256", {"start": v(0.53, 15.1) * mm, "end": v(0.42, 15.12) * mm});
            skLineSegment(sketch, "E1257", {"start": v(0.42, 15.12) * mm, "end": v(0.3, 15.13) * mm});
            skLineSegment(sketch, "E1258", {"start": v(0.3, 15.13) * mm, "end": v(0.02, 15.14) * mm});
            skLineSegment(sketch, "E1259", {"start": v(0.02, 15.14) * mm, "end": v(-0.27, 15.13) * mm});
            skLineSegment(sketch, "E1260", {"start": v(-9.5, 14.24) * mm, "end": v(-7.5, 14.24) * mm});
            skLineSegment(sketch, "E1261", {"start": v(-7.5, 14.24) * mm, "end": v(-7.5, 17.24) * mm});
            skLineSegment(sketch, "E1262", {"start": v(-7.5, 17.24) * mm, "end": v(-9.5, 17.24) * mm});
            skLineSegment(sketch, "E1263", {"start": v(-9.5, 17.24) * mm, "end": v(-9.5, 14.24) * mm});
            skLineSegment(sketch, "E1264", {"start": v(-52.5, -32.48) * mm, "end": v(-49.5, -32.48) * mm});
            skLineSegment(sketch, "E1265", {"start": v(-49.5, -32.48) * mm, "end": v(-49.5, -30.48) * mm});
            skLineSegment(sketch, "E1266", {"start": v(-49.5, -30.48) * mm, "end": v(-52.5, -30.48) * mm});
            skLineSegment(sketch, "E1267", {"start": v(-52.5, -30.48) * mm, "end": v(-52.5, -32.48) * mm});
            skLineSegment(sketch, "E1268", {"start": v(-58.5, -9.84) * mm, "end": v(-43.5, -9.84) * mm});
            skLineSegment(sketch, "E1269", {"start": v(-43.5, -9.84) * mm, "end": v(-43.5, -1) * mm});
            skLineSegment(sketch, "E1270", {"start": v(-43.5, -1) * mm, "end": v(-58.5, -1) * mm});
            skLineSegment(sketch, "E1271", {"start": v(-58.5, -1) * mm, "end": v(-58.5, -9.84) * mm});
            skArc(sketch, "E1272", {"start": v(-50.24, -6.02) * mm, "mid": v(-49.5, -7.79) * mm, "end": v(-47.74, -8.52) * mm});
            skArc(sketch, "E1273", {"start": v(-47.74, -8.52) * mm, "mid": v(-45.97, -7.79) * mm, "end": v(-45.24, -6.02) * mm});
            skArc(sketch, "E1274", {"start": v(-45.24, -6.02) * mm, "mid": v(-45.97, -4.25) * mm, "end": v(-47.74, -3.52) * mm});
            skArc(sketch, "E1275", {"start": v(-47.74, -3.52) * mm, "mid": v(-49.5, -4.25) * mm, "end": v(-50.24, -6.02) * mm});
            skLineSegment(sketch, "E1276", {"start": v(-58.5, -1) * mm, "end": v(-58.5, -24.48) * mm});
            skArc(sketch, "E1277", {"start": v(-58.5, -24.48) * mm, "mid": v(-56.74, -28.73) * mm, "end": v(-52.5, -30.48) * mm});
            skLineSegment(sketch, "E1278", {"start": v(-52.5, -30.48) * mm, "end": v(-49.5, -30.48) * mm});
            skArc(sketch, "E1279", {"start": v(-49.5, -30.48) * mm, "mid": v(-45.26, -28.73) * mm, "end": v(-43.5, -24.48) * mm});
            skLineSegment(sketch, "E1280", {"start": v(-43.5, -24.48) * mm, "end": v(-43.5, -1) * mm});
            skArc(sketch, "E1281", {"start": v(-56.74, -6.02) * mm, "mid": v(-56, -7.79) * mm, "end": v(-54.24, -8.52) * mm});
            skArc(sketch, "E1282", {"start": v(-54.24, -8.52) * mm, "mid": v(-52.47, -7.79) * mm, "end": v(-51.74, -6.02) * mm});
            skArc(sketch, "E1283", {"start": v(-51.74, -6.02) * mm, "mid": v(-52.47, -4.25) * mm, "end": v(-54.24, -3.52) * mm});
            skArc(sketch, "E1284", {"start": v(-54.24, -3.52) * mm, "mid": v(-56, -4.25) * mm, "end": v(-56.74, -6.02) * mm});
            skArc(sketch, "E1285", {"start": v(-54.24, -4.52) * mm, "mid": v(-55.3, -4.96) * mm, "end": v(-55.74, -6.02) * mm});
            skArc(sketch, "E1286", {"start": v(-55.74, -6.02) * mm, "mid": v(-55.3, -7.08) * mm, "end": v(-54.24, -7.52) * mm});
            skArc(sketch, "E1287", {"start": v(-54.24, -7.52) * mm, "mid": v(-53.18, -7.08) * mm, "end": v(-52.74, -6.02) * mm});
            skArc(sketch, "E1288", {"start": v(-52.74, -6.02) * mm, "mid": v(-53.18, -4.96) * mm, "end": v(-54.24, -4.52) * mm});
            skArc(sketch, "E1289", {"start": v(-47.74, -4.52) * mm, "mid": v(-48.8, -4.96) * mm, "end": v(-49.24, -6.02) * mm});
            skArc(sketch, "E1290", {"start": v(-49.24, -6.02) * mm, "mid": v(-48.8, -7.08) * mm, "end": v(-47.74, -7.52) * mm});
            skArc(sketch, "E1291", {"start": v(-47.74, -7.52) * mm, "mid": v(-46.67, -7.08) * mm, "end": v(-46.24, -6.02) * mm});
            skArc(sketch, "E1292", {"start": v(-46.24, -6.02) * mm, "mid": v(-46.67, -4.96) * mm, "end": v(-47.74, -4.52) * mm});
            skLineSegment(sketch, "E1293", {"start": v(-51.27, -16.35) * mm, "end": v(-51.4, -16.36) * mm});
            skLineSegment(sketch, "E1294", {"start": v(-51.4, -16.36) * mm, "end": v(-51.5, -16.38) * mm});
            skLineSegment(sketch, "E1295", {"start": v(-51.5, -16.38) * mm, "end": v(-51.72, -16.46) * mm});
            skLineSegment(sketch, "E1296", {"start": v(-51.72, -16.46) * mm, "end": v(-51.94, -16.57) * mm});
            skLineSegment(sketch, "E1297", {"start": v(-51.94, -16.57) * mm, "end": v(-52.15, -16.7) * mm});
            skLineSegment(sketch, "E1298", {"start": v(-52.15, -16.7) * mm, "end": v(-52.33, -16.85) * mm});
            skLineSegment(sketch, "E1299", {"start": v(-52.33, -16.85) * mm, "end": v(-52.53, -17.04) * mm});
            skLineSegment(sketch, "E1300", {"start": v(-52.53, -17.04) * mm, "end": v(-52.6, -17.16) * mm});
            skLineSegment(sketch, "E1301", {"start": v(-52.6, -17.16) * mm, "end": v(-52.6, -17.17) * mm});
            skLineSegment(sketch, "E1302", {"start": v(-52.6, -17.17) * mm, "end": v(-52.66, -17.27) * mm});
            skLineSegment(sketch, "E1303", {"start": v(-52.66, -17.27) * mm, "end": v(-52.76, -17.44) * mm});
            skLineSegment(sketch, "E1304", {"start": v(-52.76, -17.44) * mm, "end": v(-52.83, -17.62) * mm});
            skLineSegment(sketch, "E1305", {"start": v(-52.83, -17.62) * mm, "end": v(-52.91, -17.87) * mm});
            skLineSegment(sketch, "E1306", {"start": v(-52.91, -17.87) * mm, "end": v(-52.95, -17.97) * mm});
            skLineSegment(sketch, "E1307", {"start": v(-52.95, -17.97) * mm, "end": v(-52.95, -25.07) * mm});
            skLineSegment(sketch, "E1308", {"start": v(-52.95, -25.07) * mm, "end": v(-52.91, -25.16) * mm});
            skLineSegment(sketch, "E1309", {"start": v(-52.91, -25.16) * mm, "end": v(-52.84, -25.39) * mm});
            skLineSegment(sketch, "E1310", {"start": v(-52.84, -25.39) * mm, "end": v(-52.79, -25.54) * mm});
            skLineSegment(sketch, "E1311", {"start": v(-52.79, -25.54) * mm, "end": v(-52.74, -25.65) * mm});
            skLineSegment(sketch, "E1312", {"start": v(-52.74, -25.65) * mm, "end": v(-52.67, -25.76) * mm});
            skLineSegment(sketch, "E1313", {"start": v(-52.67, -25.76) * mm, "end": v(-52.6, -25.86) * mm});
            skLineSegment(sketch, "E1314", {"start": v(-52.6, -25.86) * mm, "end": v(-52.59, -25.87) * mm});
            skLineSegment(sketch, "E1315", {"start": v(-52.59, -25.87) * mm, "end": v(-52.58, -25.9) * mm});
            skLineSegment(sketch, "E1316", {"start": v(-52.58, -25.9) * mm, "end": v(-52.52, -26) * mm});
            skLineSegment(sketch, "E1317", {"start": v(-52.52, -26) * mm, "end": v(-52.42, -26.1) * mm});
            skLineSegment(sketch, "E1318", {"start": v(-52.42, -26.1) * mm, "end": v(-52.22, -26.29) * mm});
            skLineSegment(sketch, "E1319", {"start": v(-52.22, -26.29) * mm, "end": v(-52.13, -26.35) * mm});
            skLineSegment(sketch, "E1320", {"start": v(-52.13, -26.35) * mm, "end": v(-52.07, -26.38) * mm});
            skLineSegment(sketch, "E1321", {"start": v(-52.07, -26.38) * mm, "end": v(-52.04, -26.4) * mm});
            skLineSegment(sketch, "E1322", {"start": v(-52.04, -26.4) * mm, "end": v(-51.95, -26.46) * mm});
            skLineSegment(sketch, "E1323", {"start": v(-51.95, -26.46) * mm, "end": v(-51.66, -26.6) * mm});
            skLineSegment(sketch, "E1324", {"start": v(-51.66, -26.6) * mm, "end": v(-51.51, -26.65) * mm});
            skLineSegment(sketch, "E1325", {"start": v(-51.51, -26.65) * mm, "end": v(-51.35, -26.68) * mm});
            skLineSegment(sketch, "E1326", {"start": v(-51.35, -26.68) * mm, "end": v(-51.17, -26.7) * mm});
            skLineSegment(sketch, "E1327", {"start": v(-51.17, -26.7) * mm, "end": v(-51, -26.7) * mm});
            skLineSegment(sketch, "E1328", {"start": v(-51, -26.7) * mm, "end": v(-50.81, -26.7) * mm});
            skLineSegment(sketch, "E1329", {"start": v(-50.81, -26.7) * mm, "end": v(-50.64, -26.68) * mm});
            skLineSegment(sketch, "E1330", {"start": v(-50.64, -26.68) * mm, "end": v(-50.47, -26.65) * mm});
            skLineSegment(sketch, "E1331", {"start": v(-50.47, -26.65) * mm, "end": v(-50.32, -26.6) * mm});
            skLineSegment(sketch, "E1332", {"start": v(-50.32, -26.6) * mm, "end": v(-50.02, -26.46) * mm});
            skLineSegment(sketch, "E1333", {"start": v(-50.02, -26.46) * mm, "end": v(-49.92, -26.4) * mm});
            skLineSegment(sketch, "E1334", {"start": v(-49.92, -26.4) * mm, "end": v(-49.89, -26.37) * mm});
            skLineSegment(sketch, "E1335", {"start": v(-49.89, -26.37) * mm, "end": v(-49.86, -26.36) * mm});
            skLineSegment(sketch, "E1336", {"start": v(-49.86, -26.36) * mm, "end": v(-49.78, -26.3) * mm});
            skLineSegment(sketch, "E1337", {"start": v(-49.78, -26.3) * mm, "end": v(-49.63, -26.17) * mm});
            skLineSegment(sketch, "E1338", {"start": v(-49.63, -26.17) * mm, "end": v(-49.48, -26.03) * mm});
            skLineSegment(sketch, "E1339", {"start": v(-49.48, -26.03) * mm, "end": v(-49.42, -25.95) * mm});
            skLineSegment(sketch, "E1340", {"start": v(-49.42, -25.95) * mm, "end": v(-49.4, -25.89) * mm});
            skLineSegment(sketch, "E1341", {"start": v(-49.4, -25.89) * mm, "end": v(-49.38, -25.87) * mm});
            skLineSegment(sketch, "E1342", {"start": v(-49.38, -25.87) * mm, "end": v(-49.38, -25.86) * mm});
            skLineSegment(sketch, "E1343", {"start": v(-49.38, -25.86) * mm, "end": v(-49.31, -25.78) * mm});
            skLineSegment(sketch, "E1344", {"start": v(-49.31, -25.78) * mm, "end": v(-49.25, -25.7) * mm});
            skLineSegment(sketch, "E1345", {"start": v(-49.25, -25.7) * mm, "end": v(-49.2, -25.57) * mm});
            skLineSegment(sketch, "E1346", {"start": v(-49.2, -25.57) * mm, "end": v(-49.06, -25.16) * mm});
            skLineSegment(sketch, "E1347", {"start": v(-49.06, -25.16) * mm, "end": v(-49.02, -25.03) * mm});
            skLineSegment(sketch, "E1348", {"start": v(-49.02, -25.03) * mm, "end": v(-49.02, -17.97) * mm});
            skLineSegment(sketch, "E1349", {"start": v(-49.02, -17.97) * mm, "end": v(-49.06, -17.87) * mm});
            skLineSegment(sketch, "E1350", {"start": v(-49.06, -17.87) * mm, "end": v(-49.14, -17.62) * mm});
            skLineSegment(sketch, "E1351", {"start": v(-49.14, -17.62) * mm, "end": v(-49.21, -17.44) * mm});
            skLineSegment(sketch, "E1352", {"start": v(-49.21, -17.44) * mm, "end": v(-49.3, -17.27) * mm});
            skLineSegment(sketch, "E1353", {"start": v(-49.3, -17.27) * mm, "end": v(-49.37, -17.17) * mm});
            skLineSegment(sketch, "E1354", {"start": v(-49.37, -17.17) * mm, "end": v(-49.4, -17.11) * mm});
            skLineSegment(sketch, "E1355", {"start": v(-49.4, -17.11) * mm, "end": v(-49.45, -17.05) * mm});
            skLineSegment(sketch, "E1356", {"start": v(-49.45, -17.05) * mm, "end": v(-49.54, -16.95) * mm});
            skLineSegment(sketch, "E1357", {"start": v(-49.54, -16.95) * mm, "end": v(-49.8, -16.7) * mm});
            skLineSegment(sketch, "E1358", {"start": v(-49.8, -16.7) * mm, "end": v(-49.94, -16.62) * mm});
            skLineSegment(sketch, "E1359", {"start": v(-49.94, -16.62) * mm, "end": v(-50.11, -16.53) * mm});
            skLineSegment(sketch, "E1360", {"start": v(-50.11, -16.53) * mm, "end": v(-50.3, -16.45) * mm});
            skLineSegment(sketch, "E1361", {"start": v(-50.3, -16.45) * mm, "end": v(-50.47, -16.38) * mm});
            skLineSegment(sketch, "E1362", {"start": v(-50.47, -16.38) * mm, "end": v(-50.58, -16.36) * mm});
            skLineSegment(sketch, "E1363", {"start": v(-50.58, -16.36) * mm, "end": v(-50.7, -16.35) * mm});
            skLineSegment(sketch, "E1364", {"start": v(-50.7, -16.35) * mm, "end": v(-50.98, -16.34) * mm});
            skLineSegment(sketch, "E1365", {"start": v(-50.98, -16.34) * mm, "end": v(-51.27, -16.35) * mm});
            skLineSegment(sketch, "E1366", {"start": v(-35.5, -32.48) * mm, "end": v(-32.5, -32.48) * mm});
            skLineSegment(sketch, "E1367", {"start": v(-32.5, -32.48) * mm, "end": v(-32.5, -30.48) * mm});
            skLineSegment(sketch, "E1368", {"start": v(-32.5, -30.48) * mm, "end": v(-35.5, -30.48) * mm});
            skLineSegment(sketch, "E1369", {"start": v(-35.5, -30.48) * mm, "end": v(-35.5, -32.48) * mm});
            skLineSegment(sketch, "E1370", {"start": v(-41.5, -9.84) * mm, "end": v(-26.5, -9.84) * mm});
            skLineSegment(sketch, "E1371", {"start": v(-26.5, -9.84) * mm, "end": v(-26.5, -1) * mm});
            skLineSegment(sketch, "E1372", {"start": v(-26.5, -1) * mm, "end": v(-41.5, -1) * mm});
            skLineSegment(sketch, "E1373", {"start": v(-41.5, -1) * mm, "end": v(-41.5, -9.84) * mm});
            skArc(sketch, "E1374", {"start": v(-33.24, -6.02) * mm, "mid": v(-32.5, -7.79) * mm, "end": v(-30.74, -8.52) * mm});
            skArc(sketch, "E1375", {"start": v(-30.74, -8.52) * mm, "mid": v(-28.97, -7.79) * mm, "end": v(-28.24, -6.02) * mm});
            skArc(sketch, "E1376", {"start": v(-28.24, -6.02) * mm, "mid": v(-28.97, -4.25) * mm, "end": v(-30.74, -3.52) * mm});
            skArc(sketch, "E1377", {"start": v(-30.74, -3.52) * mm, "mid": v(-32.5, -4.25) * mm, "end": v(-33.24, -6.02) * mm});
            skLineSegment(sketch, "E1378", {"start": v(-41.5, -1) * mm, "end": v(-41.5, -24.48) * mm});
            skArc(sketch, "E1379", {"start": v(-41.5, -24.48) * mm, "mid": v(-39.74, -28.73) * mm, "end": v(-35.5, -30.48) * mm});
            skLineSegment(sketch, "E1380", {"start": v(-35.5, -30.48) * mm, "end": v(-32.5, -30.48) * mm});
            skArc(sketch, "E1381", {"start": v(-32.5, -30.48) * mm, "mid": v(-28.26, -28.73) * mm, "end": v(-26.5, -24.48) * mm});
            skLineSegment(sketch, "E1382", {"start": v(-26.5, -24.48) * mm, "end": v(-26.5, -1) * mm});
            skArc(sketch, "E1383", {"start": v(-39.74, -6.02) * mm, "mid": v(-39, -7.79) * mm, "end": v(-37.24, -8.52) * mm});
            skArc(sketch, "E1384", {"start": v(-37.24, -8.52) * mm, "mid": v(-35.47, -7.79) * mm, "end": v(-34.74, -6.02) * mm});
            skArc(sketch, "E1385", {"start": v(-34.74, -6.02) * mm, "mid": v(-35.47, -4.25) * mm, "end": v(-37.24, -3.52) * mm});
            skArc(sketch, "E1386", {"start": v(-37.24, -3.52) * mm, "mid": v(-39, -4.25) * mm, "end": v(-39.74, -6.02) * mm});
            skArc(sketch, "E1387", {"start": v(-37.24, -4.52) * mm, "mid": v(-38.3, -4.96) * mm, "end": v(-38.74, -6.02) * mm});
            skArc(sketch, "E1388", {"start": v(-38.74, -6.02) * mm, "mid": v(-38.3, -7.08) * mm, "end": v(-37.24, -7.52) * mm});
            skArc(sketch, "E1389", {"start": v(-37.24, -7.52) * mm, "mid": v(-36.18, -7.08) * mm, "end": v(-35.74, -6.02) * mm});
            skArc(sketch, "E1390", {"start": v(-35.74, -6.02) * mm, "mid": v(-36.18, -4.96) * mm, "end": v(-37.24, -4.52) * mm});
            skArc(sketch, "E1391", {"start": v(-30.74, -4.52) * mm, "mid": v(-31.8, -4.96) * mm, "end": v(-32.24, -6.02) * mm});
            skArc(sketch, "E1392", {"start": v(-32.24, -6.02) * mm, "mid": v(-31.8, -7.08) * mm, "end": v(-30.74, -7.52) * mm});
            skArc(sketch, "E1393", {"start": v(-30.74, -7.52) * mm, "mid": v(-29.67, -7.08) * mm, "end": v(-29.24, -6.02) * mm});
            skArc(sketch, "E1394", {"start": v(-29.24, -6.02) * mm, "mid": v(-29.67, -4.96) * mm, "end": v(-30.74, -4.52) * mm});
            skLineSegment(sketch, "E1395", {"start": v(-34.27, -16.35) * mm, "end": v(-34.4, -16.36) * mm});
            skLineSegment(sketch, "E1396", {"start": v(-34.4, -16.36) * mm, "end": v(-34.5, -16.38) * mm});
            skLineSegment(sketch, "E1397", {"start": v(-34.5, -16.38) * mm, "end": v(-34.72, -16.46) * mm});
            skLineSegment(sketch, "E1398", {"start": v(-34.72, -16.46) * mm, "end": v(-34.94, -16.57) * mm});
            skLineSegment(sketch, "E1399", {"start": v(-34.94, -16.57) * mm, "end": v(-35.15, -16.7) * mm});
            skLineSegment(sketch, "E1400", {"start": v(-35.15, -16.7) * mm, "end": v(-35.33, -16.85) * mm});
            skLineSegment(sketch, "E1401", {"start": v(-35.33, -16.85) * mm, "end": v(-35.53, -17.04) * mm});
            skLineSegment(sketch, "E1402", {"start": v(-35.53, -17.04) * mm, "end": v(-35.6, -17.16) * mm});
            skLineSegment(sketch, "E1403", {"start": v(-35.6, -17.16) * mm, "end": v(-35.6, -17.17) * mm});
            skLineSegment(sketch, "E1404", {"start": v(-35.6, -17.17) * mm, "end": v(-35.66, -17.27) * mm});
            skLineSegment(sketch, "E1405", {"start": v(-35.66, -17.27) * mm, "end": v(-35.76, -17.44) * mm});
            skLineSegment(sketch, "E1406", {"start": v(-35.76, -17.44) * mm, "end": v(-35.83, -17.62) * mm});
            skLineSegment(sketch, "E1407", {"start": v(-35.83, -17.62) * mm, "end": v(-35.91, -17.87) * mm});
            skLineSegment(sketch, "E1408", {"start": v(-35.91, -17.87) * mm, "end": v(-35.95, -17.97) * mm});
            skLineSegment(sketch, "E1409", {"start": v(-35.95, -17.97) * mm, "end": v(-35.95, -25.07) * mm});
            skLineSegment(sketch, "E1410", {"start": v(-35.95, -25.07) * mm, "end": v(-35.91, -25.16) * mm});
            skLineSegment(sketch, "E1411", {"start": v(-35.91, -25.16) * mm, "end": v(-35.84, -25.39) * mm});
            skLineSegment(sketch, "E1412", {"start": v(-35.84, -25.39) * mm, "end": v(-35.79, -25.54) * mm});
            skLineSegment(sketch, "E1413", {"start": v(-35.79, -25.54) * mm, "end": v(-35.74, -25.65) * mm});
            skLineSegment(sketch, "E1414", {"start": v(-35.74, -25.65) * mm, "end": v(-35.67, -25.76) * mm});
            skLineSegment(sketch, "E1415", {"start": v(-35.67, -25.76) * mm, "end": v(-35.6, -25.86) * mm});
            skLineSegment(sketch, "E1416", {"start": v(-35.6, -25.86) * mm, "end": v(-35.59, -25.87) * mm});
            skLineSegment(sketch, "E1417", {"start": v(-35.59, -25.87) * mm, "end": v(-35.58, -25.9) * mm});
            skLineSegment(sketch, "E1418", {"start": v(-35.58, -25.9) * mm, "end": v(-35.52, -26) * mm});
            skLineSegment(sketch, "E1419", {"start": v(-35.52, -26) * mm, "end": v(-35.42, -26.1) * mm});
            skLineSegment(sketch, "E1420", {"start": v(-35.42, -26.1) * mm, "end": v(-35.22, -26.29) * mm});
            skLineSegment(sketch, "E1421", {"start": v(-35.22, -26.29) * mm, "end": v(-35.13, -26.35) * mm});
            skLineSegment(sketch, "E1422", {"start": v(-35.13, -26.35) * mm, "end": v(-35.07, -26.38) * mm});
            skLineSegment(sketch, "E1423", {"start": v(-35.07, -26.38) * mm, "end": v(-35.04, -26.4) * mm});
            skLineSegment(sketch, "E1424", {"start": v(-35.04, -26.4) * mm, "end": v(-34.95, -26.46) * mm});
            skLineSegment(sketch, "E1425", {"start": v(-34.95, -26.46) * mm, "end": v(-34.66, -26.6) * mm});
            skLineSegment(sketch, "E1426", {"start": v(-34.66, -26.6) * mm, "end": v(-34.51, -26.65) * mm});
            skLineSegment(sketch, "E1427", {"start": v(-34.51, -26.65) * mm, "end": v(-34.35, -26.68) * mm});
            skLineSegment(sketch, "E1428", {"start": v(-34.35, -26.68) * mm, "end": v(-34.17, -26.7) * mm});
            skLineSegment(sketch, "E1429", {"start": v(-34.17, -26.7) * mm, "end": v(-34, -26.7) * mm});
            skLineSegment(sketch, "E1430", {"start": v(-34, -26.7) * mm, "end": v(-33.81, -26.7) * mm});
            skLineSegment(sketch, "E1431", {"start": v(-33.81, -26.7) * mm, "end": v(-33.64, -26.68) * mm});
            skLineSegment(sketch, "E1432", {"start": v(-33.64, -26.68) * mm, "end": v(-33.47, -26.65) * mm});
            skLineSegment(sketch, "E1433", {"start": v(-33.47, -26.65) * mm, "end": v(-33.32, -26.6) * mm});
            skLineSegment(sketch, "E1434", {"start": v(-33.32, -26.6) * mm, "end": v(-33.02, -26.46) * mm});
            skLineSegment(sketch, "E1435", {"start": v(-33.02, -26.46) * mm, "end": v(-32.92, -26.4) * mm});
            skLineSegment(sketch, "E1436", {"start": v(-32.92, -26.4) * mm, "end": v(-32.89, -26.37) * mm});
            skLineSegment(sketch, "E1437", {"start": v(-32.89, -26.37) * mm, "end": v(-32.86, -26.36) * mm});
            skLineSegment(sketch, "E1438", {"start": v(-32.86, -26.36) * mm, "end": v(-32.78, -26.3) * mm});
            skLineSegment(sketch, "E1439", {"start": v(-32.78, -26.3) * mm, "end": v(-32.63, -26.17) * mm});
            skLineSegment(sketch, "E1440", {"start": v(-32.63, -26.17) * mm, "end": v(-32.48, -26.03) * mm});
            skLineSegment(sketch, "E1441", {"start": v(-32.48, -26.03) * mm, "end": v(-32.42, -25.95) * mm});
            skLineSegment(sketch, "E1442", {"start": v(-32.42, -25.95) * mm, "end": v(-32.4, -25.89) * mm});
            skLineSegment(sketch, "E1443", {"start": v(-32.4, -25.89) * mm, "end": v(-32.38, -25.87) * mm});
            skLineSegment(sketch, "E1444", {"start": v(-32.38, -25.87) * mm, "end": v(-32.38, -25.86) * mm});
            skLineSegment(sketch, "E1445", {"start": v(-32.38, -25.86) * mm, "end": v(-32.31, -25.78) * mm});
            skLineSegment(sketch, "E1446", {"start": v(-32.31, -25.78) * mm, "end": v(-32.25, -25.7) * mm});
            skLineSegment(sketch, "E1447", {"start": v(-32.25, -25.7) * mm, "end": v(-32.2, -25.57) * mm});
            skLineSegment(sketch, "E1448", {"start": v(-32.2, -25.57) * mm, "end": v(-32.06, -25.16) * mm});
            skLineSegment(sketch, "E1449", {"start": v(-32.06, -25.16) * mm, "end": v(-32.02, -25.03) * mm});
            skLineSegment(sketch, "E1450", {"start": v(-32.02, -25.03) * mm, "end": v(-32.02, -17.97) * mm});
            skLineSegment(sketch, "E1451", {"start": v(-32.02, -17.97) * mm, "end": v(-32.06, -17.87) * mm});
            skLineSegment(sketch, "E1452", {"start": v(-32.06, -17.87) * mm, "end": v(-32.14, -17.62) * mm});
            skLineSegment(sketch, "E1453", {"start": v(-32.14, -17.62) * mm, "end": v(-32.21, -17.44) * mm});
            skLineSegment(sketch, "E1454", {"start": v(-32.21, -17.44) * mm, "end": v(-32.3, -17.27) * mm});
            skLineSegment(sketch, "E1455", {"start": v(-32.3, -17.27) * mm, "end": v(-32.37, -17.17) * mm});
            skLineSegment(sketch, "E1456", {"start": v(-32.37, -17.17) * mm, "end": v(-32.4, -17.11) * mm});
            skLineSegment(sketch, "E1457", {"start": v(-32.4, -17.11) * mm, "end": v(-32.45, -17.05) * mm});
            skLineSegment(sketch, "E1458", {"start": v(-32.45, -17.05) * mm, "end": v(-32.54, -16.95) * mm});
            skLineSegment(sketch, "E1459", {"start": v(-32.54, -16.95) * mm, "end": v(-32.8, -16.7) * mm});
            skLineSegment(sketch, "E1460", {"start": v(-32.8, -16.7) * mm, "end": v(-32.94, -16.62) * mm});
            skLineSegment(sketch, "E1461", {"start": v(-32.94, -16.62) * mm, "end": v(-33.11, -16.53) * mm});
            skLineSegment(sketch, "E1462", {"start": v(-33.11, -16.53) * mm, "end": v(-33.3, -16.45) * mm});
            skLineSegment(sketch, "E1463", {"start": v(-33.3, -16.45) * mm, "end": v(-33.47, -16.38) * mm});
            skLineSegment(sketch, "E1464", {"start": v(-33.47, -16.38) * mm, "end": v(-33.58, -16.36) * mm});
            skLineSegment(sketch, "E1465", {"start": v(-33.58, -16.36) * mm, "end": v(-33.7, -16.35) * mm});
            skLineSegment(sketch, "E1466", {"start": v(-33.7, -16.35) * mm, "end": v(-33.98, -16.34) * mm});
            skLineSegment(sketch, "E1467", {"start": v(-33.98, -16.34) * mm, "end": v(-34.27, -16.35) * mm});
            skLineSegment(sketch, "E1468", {"start": v(-43.5, -17.24) * mm, "end": v(-41.5, -17.24) * mm});
            skLineSegment(sketch, "E1469", {"start": v(-41.5, -17.24) * mm, "end": v(-41.5, -14.24) * mm});
            skLineSegment(sketch, "E1470", {"start": v(-41.5, -14.24) * mm, "end": v(-43.5, -14.24) * mm});
            skLineSegment(sketch, "E1471", {"start": v(-43.5, -14.24) * mm, "end": v(-43.5, -17.24) * mm});
            skLineSegment(sketch, "E1472", {"start": v(-18.5, -32.48) * mm, "end": v(-15.5, -32.48) * mm});
            skLineSegment(sketch, "E1473", {"start": v(-15.5, -32.48) * mm, "end": v(-15.5, -30.48) * mm});
            skLineSegment(sketch, "E1474", {"start": v(-15.5, -30.48) * mm, "end": v(-18.5, -30.48) * mm});
            skLineSegment(sketch, "E1475", {"start": v(-18.5, -30.48) * mm, "end": v(-18.5, -32.48) * mm});
            skLineSegment(sketch, "E1476", {"start": v(-24.5, -9.84) * mm, "end": v(-9.5, -9.84) * mm});
            skLineSegment(sketch, "E1477", {"start": v(-9.5, -9.84) * mm, "end": v(-9.5, -1) * mm});
            skLineSegment(sketch, "E1478", {"start": v(-9.5, -1) * mm, "end": v(-24.5, -1) * mm});
            skLineSegment(sketch, "E1479", {"start": v(-24.5, -1) * mm, "end": v(-24.5, -9.84) * mm});
            skArc(sketch, "E1480", {"start": v(-16.24, -6.02) * mm, "mid": v(-15.5, -7.79) * mm, "end": v(-13.74, -8.52) * mm});
            skArc(sketch, "E1481", {"start": v(-13.74, -8.52) * mm, "mid": v(-11.97, -7.79) * mm, "end": v(-11.24, -6.02) * mm});
            skArc(sketch, "E1482", {"start": v(-11.24, -6.02) * mm, "mid": v(-11.97, -4.25) * mm, "end": v(-13.74, -3.52) * mm});
            skArc(sketch, "E1483", {"start": v(-13.74, -3.52) * mm, "mid": v(-15.5, -4.25) * mm, "end": v(-16.24, -6.02) * mm});
            skLineSegment(sketch, "E1484", {"start": v(-24.5, -1) * mm, "end": v(-24.5, -24.48) * mm});
            skArc(sketch, "E1485", {"start": v(-24.5, -24.48) * mm, "mid": v(-22.74, -28.73) * mm, "end": v(-18.5, -30.48) * mm});
            skLineSegment(sketch, "E1486", {"start": v(-18.5, -30.48) * mm, "end": v(-15.5, -30.48) * mm});
            skArc(sketch, "E1487", {"start": v(-15.5, -30.48) * mm, "mid": v(-11.26, -28.73) * mm, "end": v(-9.5, -24.48) * mm});
            skLineSegment(sketch, "E1488", {"start": v(-9.5, -24.48) * mm, "end": v(-9.5, -1) * mm});
            skArc(sketch, "E1489", {"start": v(-22.74, -6.02) * mm, "mid": v(-22, -7.79) * mm, "end": v(-20.24, -8.52) * mm});
            skArc(sketch, "E1490", {"start": v(-20.24, -8.52) * mm, "mid": v(-18.47, -7.79) * mm, "end": v(-17.74, -6.02) * mm});
            skArc(sketch, "E1491", {"start": v(-17.74, -6.02) * mm, "mid": v(-18.47, -4.25) * mm, "end": v(-20.24, -3.52) * mm});
            skArc(sketch, "E1492", {"start": v(-20.24, -3.52) * mm, "mid": v(-22, -4.25) * mm, "end": v(-22.74, -6.02) * mm});
            skArc(sketch, "E1493", {"start": v(-20.24, -4.52) * mm, "mid": v(-21.3, -4.96) * mm, "end": v(-21.74, -6.02) * mm});
            skArc(sketch, "E1494", {"start": v(-21.74, -6.02) * mm, "mid": v(-21.3, -7.08) * mm, "end": v(-20.24, -7.52) * mm});
            skArc(sketch, "E1495", {"start": v(-20.24, -7.52) * mm, "mid": v(-19.18, -7.08) * mm, "end": v(-18.74, -6.02) * mm});
            skArc(sketch, "E1496", {"start": v(-18.74, -6.02) * mm, "mid": v(-19.18, -4.96) * mm, "end": v(-20.24, -4.52) * mm});
            skArc(sketch, "E1497", {"start": v(-13.74, -4.52) * mm, "mid": v(-14.8, -4.96) * mm, "end": v(-15.24, -6.02) * mm});
            skArc(sketch, "E1498", {"start": v(-15.24, -6.02) * mm, "mid": v(-14.8, -7.08) * mm, "end": v(-13.74, -7.52) * mm});
            skArc(sketch, "E1499", {"start": v(-13.74, -7.52) * mm, "mid": v(-12.67, -7.08) * mm, "end": v(-12.24, -6.02) * mm});
            skArc(sketch, "E1500", {"start": v(-12.24, -6.02) * mm, "mid": v(-12.67, -4.96) * mm, "end": v(-13.74, -4.52) * mm});
            skLineSegment(sketch, "E1501", {"start": v(-17.27, -16.35) * mm, "end": v(-17.4, -16.36) * mm});
            skLineSegment(sketch, "E1502", {"start": v(-17.4, -16.36) * mm, "end": v(-17.5, -16.38) * mm});
            skLineSegment(sketch, "E1503", {"start": v(-17.5, -16.38) * mm, "end": v(-17.72, -16.46) * mm});
            skLineSegment(sketch, "E1504", {"start": v(-17.72, -16.46) * mm, "end": v(-17.94, -16.57) * mm});
            skLineSegment(sketch, "E1505", {"start": v(-17.94, -16.57) * mm, "end": v(-18.15, -16.7) * mm});
            skLineSegment(sketch, "E1506", {"start": v(-18.15, -16.7) * mm, "end": v(-18.33, -16.85) * mm});
            skLineSegment(sketch, "E1507", {"start": v(-18.33, -16.85) * mm, "end": v(-18.53, -17.04) * mm});
            skLineSegment(sketch, "E1508", {"start": v(-18.53, -17.04) * mm, "end": v(-18.6, -17.16) * mm});
            skLineSegment(sketch, "E1509", {"start": v(-18.6, -17.16) * mm, "end": v(-18.6, -17.17) * mm});
            skLineSegment(sketch, "E1510", {"start": v(-18.6, -17.17) * mm, "end": v(-18.66, -17.27) * mm});
            skLineSegment(sketch, "E1511", {"start": v(-18.66, -17.27) * mm, "end": v(-18.76, -17.44) * mm});
            skLineSegment(sketch, "E1512", {"start": v(-18.76, -17.44) * mm, "end": v(-18.83, -17.62) * mm});
            skLineSegment(sketch, "E1513", {"start": v(-18.83, -17.62) * mm, "end": v(-18.91, -17.87) * mm});
            skLineSegment(sketch, "E1514", {"start": v(-18.91, -17.87) * mm, "end": v(-18.95, -17.97) * mm});
            skLineSegment(sketch, "E1515", {"start": v(-18.95, -17.97) * mm, "end": v(-18.95, -25.07) * mm});
            skLineSegment(sketch, "E1516", {"start": v(-18.95, -25.07) * mm, "end": v(-18.91, -25.16) * mm});
            skLineSegment(sketch, "E1517", {"start": v(-18.91, -25.16) * mm, "end": v(-18.84, -25.39) * mm});
            skLineSegment(sketch, "E1518", {"start": v(-18.84, -25.39) * mm, "end": v(-18.79, -25.54) * mm});
            skLineSegment(sketch, "E1519", {"start": v(-18.79, -25.54) * mm, "end": v(-18.74, -25.65) * mm});
            skLineSegment(sketch, "E1520", {"start": v(-18.74, -25.65) * mm, "end": v(-18.67, -25.76) * mm});
            skLineSegment(sketch, "E1521", {"start": v(-18.67, -25.76) * mm, "end": v(-18.6, -25.86) * mm});
            skLineSegment(sketch, "E1522", {"start": v(-18.6, -25.86) * mm, "end": v(-18.59, -25.87) * mm});
            skLineSegment(sketch, "E1523", {"start": v(-18.59, -25.87) * mm, "end": v(-18.58, -25.9) * mm});
            skLineSegment(sketch, "E1524", {"start": v(-18.58, -25.9) * mm, "end": v(-18.52, -26) * mm});
            skLineSegment(sketch, "E1525", {"start": v(-18.52, -26) * mm, "end": v(-18.42, -26.1) * mm});
            skLineSegment(sketch, "E1526", {"start": v(-18.42, -26.1) * mm, "end": v(-18.22, -26.29) * mm});
            skLineSegment(sketch, "E1527", {"start": v(-18.22, -26.29) * mm, "end": v(-18.13, -26.35) * mm});
            skLineSegment(sketch, "E1528", {"start": v(-18.13, -26.35) * mm, "end": v(-18.07, -26.38) * mm});
            skLineSegment(sketch, "E1529", {"start": v(-18.07, -26.38) * mm, "end": v(-18.04, -26.4) * mm});
            skLineSegment(sketch, "E1530", {"start": v(-18.04, -26.4) * mm, "end": v(-17.95, -26.46) * mm});
            skLineSegment(sketch, "E1531", {"start": v(-17.95, -26.46) * mm, "end": v(-17.66, -26.6) * mm});
            skLineSegment(sketch, "E1532", {"start": v(-17.66, -26.6) * mm, "end": v(-17.51, -26.65) * mm});
            skLineSegment(sketch, "E1533", {"start": v(-17.51, -26.65) * mm, "end": v(-17.35, -26.68) * mm});
            skLineSegment(sketch, "E1534", {"start": v(-17.35, -26.68) * mm, "end": v(-17.17, -26.7) * mm});
            skLineSegment(sketch, "E1535", {"start": v(-17.17, -26.7) * mm, "end": v(-17, -26.7) * mm});
            skLineSegment(sketch, "E1536", {"start": v(-17, -26.7) * mm, "end": v(-16.81, -26.7) * mm});
            skLineSegment(sketch, "E1537", {"start": v(-16.81, -26.7) * mm, "end": v(-16.64, -26.68) * mm});
            skLineSegment(sketch, "E1538", {"start": v(-16.64, -26.68) * mm, "end": v(-16.47, -26.65) * mm});
            skLineSegment(sketch, "E1539", {"start": v(-16.47, -26.65) * mm, "end": v(-16.32, -26.6) * mm});
            skLineSegment(sketch, "E1540", {"start": v(-16.32, -26.6) * mm, "end": v(-16.02, -26.46) * mm});
            skLineSegment(sketch, "E1541", {"start": v(-16.02, -26.46) * mm, "end": v(-15.92, -26.4) * mm});
            skLineSegment(sketch, "E1542", {"start": v(-15.92, -26.4) * mm, "end": v(-15.89, -26.37) * mm});
            skLineSegment(sketch, "E1543", {"start": v(-15.89, -26.37) * mm, "end": v(-15.86, -26.36) * mm});
            skLineSegment(sketch, "E1544", {"start": v(-15.86, -26.36) * mm, "end": v(-15.78, -26.3) * mm});
            skLineSegment(sketch, "E1545", {"start": v(-15.78, -26.3) * mm, "end": v(-15.63, -26.17) * mm});
            skLineSegment(sketch, "E1546", {"start": v(-15.63, -26.17) * mm, "end": v(-15.48, -26.03) * mm});
            skLineSegment(sketch, "E1547", {"start": v(-15.48, -26.03) * mm, "end": v(-15.42, -25.95) * mm});
            skLineSegment(sketch, "E1548", {"start": v(-15.42, -25.95) * mm, "end": v(-15.4, -25.89) * mm});
            skLineSegment(sketch, "E1549", {"start": v(-15.4, -25.89) * mm, "end": v(-15.38, -25.87) * mm});
            skLineSegment(sketch, "E1550", {"start": v(-15.38, -25.87) * mm, "end": v(-15.38, -25.86) * mm});
            skLineSegment(sketch, "E1551", {"start": v(-15.38, -25.86) * mm, "end": v(-15.31, -25.78) * mm});
            skLineSegment(sketch, "E1552", {"start": v(-15.31, -25.78) * mm, "end": v(-15.25, -25.7) * mm});
            skLineSegment(sketch, "E1553", {"start": v(-15.25, -25.7) * mm, "end": v(-15.2, -25.57) * mm});
            skLineSegment(sketch, "E1554", {"start": v(-15.2, -25.57) * mm, "end": v(-15.06, -25.16) * mm});
            skLineSegment(sketch, "E1555", {"start": v(-15.06, -25.16) * mm, "end": v(-15.02, -25.03) * mm});
            skLineSegment(sketch, "E1556", {"start": v(-15.02, -25.03) * mm, "end": v(-15.02, -17.97) * mm});
            skLineSegment(sketch, "E1557", {"start": v(-15.02, -17.97) * mm, "end": v(-15.06, -17.87) * mm});
            skLineSegment(sketch, "E1558", {"start": v(-15.06, -17.87) * mm, "end": v(-15.14, -17.62) * mm});
            skLineSegment(sketch, "E1559", {"start": v(-15.14, -17.62) * mm, "end": v(-15.21, -17.44) * mm});
            skLineSegment(sketch, "E1560", {"start": v(-15.21, -17.44) * mm, "end": v(-15.3, -17.27) * mm});
            skLineSegment(sketch, "E1561", {"start": v(-15.3, -17.27) * mm, "end": v(-15.37, -17.17) * mm});
            skLineSegment(sketch, "E1562", {"start": v(-15.37, -17.17) * mm, "end": v(-15.4, -17.11) * mm});
            skLineSegment(sketch, "E1563", {"start": v(-15.4, -17.11) * mm, "end": v(-15.45, -17.05) * mm});
            skLineSegment(sketch, "E1564", {"start": v(-15.45, -17.05) * mm, "end": v(-15.54, -16.95) * mm});
            skLineSegment(sketch, "E1565", {"start": v(-15.54, -16.95) * mm, "end": v(-15.8, -16.7) * mm});
            skLineSegment(sketch, "E1566", {"start": v(-15.8, -16.7) * mm, "end": v(-15.94, -16.62) * mm});
            skLineSegment(sketch, "E1567", {"start": v(-15.94, -16.62) * mm, "end": v(-16.11, -16.53) * mm});
            skLineSegment(sketch, "E1568", {"start": v(-16.11, -16.53) * mm, "end": v(-16.3, -16.45) * mm});
            skLineSegment(sketch, "E1569", {"start": v(-16.3, -16.45) * mm, "end": v(-16.47, -16.38) * mm});
            skLineSegment(sketch, "E1570", {"start": v(-16.47, -16.38) * mm, "end": v(-16.58, -16.36) * mm});
            skLineSegment(sketch, "E1571", {"start": v(-16.58, -16.36) * mm, "end": v(-16.7, -16.35) * mm});
            skLineSegment(sketch, "E1572", {"start": v(-16.7, -16.35) * mm, "end": v(-16.98, -16.34) * mm});
            skLineSegment(sketch, "E1573", {"start": v(-16.98, -16.34) * mm, "end": v(-17.27, -16.35) * mm});
            skLineSegment(sketch, "E1574", {"start": v(-26.5, -17.24) * mm, "end": v(-24.5, -17.24) * mm});
            skLineSegment(sketch, "E1575", {"start": v(-24.5, -17.24) * mm, "end": v(-24.5, -14.24) * mm});
            skLineSegment(sketch, "E1576", {"start": v(-24.5, -14.24) * mm, "end": v(-26.5, -14.24) * mm});
            skLineSegment(sketch, "E1577", {"start": v(-26.5, -14.24) * mm, "end": v(-26.5, -17.24) * mm});
            skLineSegment(sketch, "E1578", {"start": v(15.5, -32.48) * mm, "end": v(18.5, -32.48) * mm});
            skLineSegment(sketch, "E1579", {"start": v(18.5, -32.48) * mm, "end": v(18.5, -30.48) * mm});
            skLineSegment(sketch, "E1580", {"start": v(18.5, -30.48) * mm, "end": v(15.5, -30.48) * mm});
            skLineSegment(sketch, "E1581", {"start": v(15.5, -30.48) * mm, "end": v(15.5, -32.48) * mm});
            skLineSegment(sketch, "E1582", {"start": v(9.5, -9.84) * mm, "end": v(24.5, -9.84) * mm});
            skLineSegment(sketch, "E1583", {"start": v(24.5, -9.84) * mm, "end": v(24.5, -1) * mm});
            skLineSegment(sketch, "E1584", {"start": v(24.5, -1) * mm, "end": v(9.5, -1) * mm});
            skLineSegment(sketch, "E1585", {"start": v(9.5, -1) * mm, "end": v(9.5, -9.84) * mm});
            skArc(sketch, "E1586", {"start": v(17.76, -6.02) * mm, "mid": v(18.5, -7.79) * mm, "end": v(20.26, -8.52) * mm});
            skArc(sketch, "E1587", {"start": v(20.26, -8.52) * mm, "mid": v(22.03, -7.79) * mm, "end": v(22.76, -6.02) * mm});
            skArc(sketch, "E1588", {"start": v(22.76, -6.02) * mm, "mid": v(22.03, -4.25) * mm, "end": v(20.26, -3.52) * mm});
            skArc(sketch, "E1589", {"start": v(20.26, -3.52) * mm, "mid": v(18.5, -4.25) * mm, "end": v(17.76, -6.02) * mm});
            skLineSegment(sketch, "E1590", {"start": v(9.5, -1) * mm, "end": v(9.5, -24.48) * mm});
            skArc(sketch, "E1591", {"start": v(9.5, -24.48) * mm, "mid": v(11.26, -28.73) * mm, "end": v(15.5, -30.48) * mm});
            skLineSegment(sketch, "E1592", {"start": v(15.5, -30.48) * mm, "end": v(18.5, -30.48) * mm});
            skArc(sketch, "E1593", {"start": v(18.5, -30.48) * mm, "mid": v(22.74, -28.73) * mm, "end": v(24.5, -24.48) * mm});
            skLineSegment(sketch, "E1594", {"start": v(24.5, -24.48) * mm, "end": v(24.5, -1) * mm});
            skArc(sketch, "E1595", {"start": v(11.26, -6.02) * mm, "mid": v(12, -7.79) * mm, "end": v(13.76, -8.52) * mm});
            skArc(sketch, "E1596", {"start": v(13.76, -8.52) * mm, "mid": v(15.53, -7.79) * mm, "end": v(16.26, -6.02) * mm});
            skArc(sketch, "E1597", {"start": v(16.26, -6.02) * mm, "mid": v(15.53, -4.25) * mm, "end": v(13.76, -3.52) * mm});
            skArc(sketch, "E1598", {"start": v(13.76, -3.52) * mm, "mid": v(12, -4.25) * mm, "end": v(11.26, -6.02) * mm});
            skArc(sketch, "E1599", {"start": v(13.76, -4.52) * mm, "mid": v(12.7, -4.96) * mm, "end": v(12.26, -6.02) * mm});
            skArc(sketch, "E1600", {"start": v(12.26, -6.02) * mm, "mid": v(12.7, -7.08) * mm, "end": v(13.76, -7.52) * mm});
            skArc(sketch, "E1601", {"start": v(13.76, -7.52) * mm, "mid": v(14.82, -7.08) * mm, "end": v(15.26, -6.02) * mm});
            skArc(sketch, "E1602", {"start": v(15.26, -6.02) * mm, "mid": v(14.82, -4.96) * mm, "end": v(13.76, -4.52) * mm});
            skArc(sketch, "E1603", {"start": v(20.27, -4.52) * mm, "mid": v(19.2, -4.96) * mm, "end": v(18.77, -6.02) * mm});
            skArc(sketch, "E1604", {"start": v(18.77, -6.02) * mm, "mid": v(19.2, -7.08) * mm, "end": v(20.27, -7.52) * mm});
            skArc(sketch, "E1605", {"start": v(20.27, -7.52) * mm, "mid": v(21.33, -7.08) * mm, "end": v(21.77, -6.02) * mm});
            skArc(sketch, "E1606", {"start": v(21.77, -6.02) * mm, "mid": v(21.33, -4.96) * mm, "end": v(20.27, -4.52) * mm});
            skLineSegment(sketch, "E1607", {"start": v(16.73, -16.35) * mm, "end": v(16.6, -16.36) * mm});
            skLineSegment(sketch, "E1608", {"start": v(16.6, -16.36) * mm, "end": v(16.5, -16.38) * mm});
            skLineSegment(sketch, "E1609", {"start": v(16.5, -16.38) * mm, "end": v(16.28, -16.46) * mm});
            skLineSegment(sketch, "E1610", {"start": v(16.28, -16.46) * mm, "end": v(16.06, -16.57) * mm});
            skLineSegment(sketch, "E1611", {"start": v(16.06, -16.57) * mm, "end": v(15.85, -16.7) * mm});
            skLineSegment(sketch, "E1612", {"start": v(15.85, -16.7) * mm, "end": v(15.67, -16.85) * mm});
            skLineSegment(sketch, "E1613", {"start": v(15.67, -16.85) * mm, "end": v(15.47, -17.04) * mm});
            skLineSegment(sketch, "E1614", {"start": v(15.47, -17.04) * mm, "end": v(15.4, -17.16) * mm});
            skLineSegment(sketch, "E1615", {"start": v(15.4, -17.16) * mm, "end": v(15.4, -17.17) * mm});
            skLineSegment(sketch, "E1616", {"start": v(15.4, -17.17) * mm, "end": v(15.34, -17.27) * mm});
            skLineSegment(sketch, "E1617", {"start": v(15.34, -17.27) * mm, "end": v(15.24, -17.44) * mm});
            skLineSegment(sketch, "E1618", {"start": v(15.24, -17.44) * mm, "end": v(15.17, -17.62) * mm});
            skLineSegment(sketch, "E1619", {"start": v(15.17, -17.62) * mm, "end": v(15.09, -17.87) * mm});
            skLineSegment(sketch, "E1620", {"start": v(15.09, -17.87) * mm, "end": v(15.05, -17.97) * mm});
            skLineSegment(sketch, "E1621", {"start": v(15.05, -17.97) * mm, "end": v(15.05, -25.07) * mm});
            skLineSegment(sketch, "E1622", {"start": v(15.05, -25.07) * mm, "end": v(15.09, -25.16) * mm});
            skLineSegment(sketch, "E1623", {"start": v(15.09, -25.16) * mm, "end": v(15.16, -25.39) * mm});
            skLineSegment(sketch, "E1624", {"start": v(15.16, -25.39) * mm, "end": v(15.21, -25.54) * mm});
            skLineSegment(sketch, "E1625", {"start": v(15.21, -25.54) * mm, "end": v(15.26, -25.65) * mm});
            skLineSegment(sketch, "E1626", {"start": v(15.26, -25.65) * mm, "end": v(15.33, -25.76) * mm});
            skLineSegment(sketch, "E1627", {"start": v(15.33, -25.76) * mm, "end": v(15.4, -25.86) * mm});
            skLineSegment(sketch, "E1628", {"start": v(15.4, -25.86) * mm, "end": v(15.41, -25.87) * mm});
            skLineSegment(sketch, "E1629", {"start": v(15.41, -25.87) * mm, "end": v(15.42, -25.9) * mm});
            skLineSegment(sketch, "E1630", {"start": v(15.42, -25.9) * mm, "end": v(15.48, -26) * mm});
            skLineSegment(sketch, "E1631", {"start": v(15.48, -26) * mm, "end": v(15.58, -26.1) * mm});
            skLineSegment(sketch, "E1632", {"start": v(15.58, -26.1) * mm, "end": v(15.78, -26.29) * mm});
            skLineSegment(sketch, "E1633", {"start": v(15.78, -26.29) * mm, "end": v(15.87, -26.35) * mm});
            skLineSegment(sketch, "E1634", {"start": v(15.87, -26.35) * mm, "end": v(15.93, -26.38) * mm});
            skLineSegment(sketch, "E1635", {"start": v(15.93, -26.38) * mm, "end": v(15.96, -26.4) * mm});
            skLineSegment(sketch, "E1636", {"start": v(15.96, -26.4) * mm, "end": v(16.05, -26.46) * mm});
            skLineSegment(sketch, "E1637", {"start": v(16.05, -26.46) * mm, "end": v(16.34, -26.6) * mm});
            skLineSegment(sketch, "E1638", {"start": v(16.34, -26.6) * mm, "end": v(16.49, -26.65) * mm});
            skLineSegment(sketch, "E1639", {"start": v(16.49, -26.65) * mm, "end": v(16.65, -26.68) * mm});
            skLineSegment(sketch, "E1640", {"start": v(16.65, -26.68) * mm, "end": v(16.83, -26.7) * mm});
            skLineSegment(sketch, "E1641", {"start": v(16.83, -26.7) * mm, "end": v(17, -26.7) * mm});
            skLineSegment(sketch, "E1642", {"start": v(17, -26.7) * mm, "end": v(17.19, -26.7) * mm});
            skLineSegment(sketch, "E1643", {"start": v(17.19, -26.7) * mm, "end": v(17.36, -26.68) * mm});
            skLineSegment(sketch, "E1644", {"start": v(17.36, -26.68) * mm, "end": v(17.53, -26.65) * mm});
            skLineSegment(sketch, "E1645", {"start": v(17.53, -26.65) * mm, "end": v(17.68, -26.6) * mm});
            skLineSegment(sketch, "E1646", {"start": v(17.68, -26.6) * mm, "end": v(17.98, -26.46) * mm});
            skLineSegment(sketch, "E1647", {"start": v(17.98, -26.46) * mm, "end": v(18.08, -26.4) * mm});
            skLineSegment(sketch, "E1648", {"start": v(18.08, -26.4) * mm, "end": v(18.11, -26.37) * mm});
            skLineSegment(sketch, "E1649", {"start": v(18.11, -26.37) * mm, "end": v(18.14, -26.36) * mm});
            skLineSegment(sketch, "E1650", {"start": v(18.14, -26.36) * mm, "end": v(18.22, -26.3) * mm});
            skLineSegment(sketch, "E1651", {"start": v(18.22, -26.3) * mm, "end": v(18.37, -26.17) * mm});
            skLineSegment(sketch, "E1652", {"start": v(18.37, -26.17) * mm, "end": v(18.52, -26.03) * mm});
            skLineSegment(sketch, "E1653", {"start": v(18.52, -26.03) * mm, "end": v(18.58, -25.95) * mm});
            skLineSegment(sketch, "E1654", {"start": v(18.58, -25.95) * mm, "end": v(18.6, -25.89) * mm});
            skLineSegment(sketch, "E1655", {"start": v(18.6, -25.89) * mm, "end": v(18.62, -25.87) * mm});
            skLineSegment(sketch, "E1656", {"start": v(18.62, -25.87) * mm, "end": v(18.62, -25.86) * mm});
            skLineSegment(sketch, "E1657", {"start": v(18.62, -25.86) * mm, "end": v(18.69, -25.78) * mm});
            skLineSegment(sketch, "E1658", {"start": v(18.69, -25.78) * mm, "end": v(18.75, -25.7) * mm});
            skLineSegment(sketch, "E1659", {"start": v(18.75, -25.7) * mm, "end": v(18.8, -25.57) * mm});
            skLineSegment(sketch, "E1660", {"start": v(18.8, -25.57) * mm, "end": v(18.94, -25.16) * mm});
            skLineSegment(sketch, "E1661", {"start": v(18.94, -25.16) * mm, "end": v(18.98, -25.03) * mm});
            skLineSegment(sketch, "E1662", {"start": v(18.98, -25.03) * mm, "end": v(18.98, -17.97) * mm});
            skLineSegment(sketch, "E1663", {"start": v(18.98, -17.97) * mm, "end": v(18.94, -17.87) * mm});
            skLineSegment(sketch, "E1664", {"start": v(18.94, -17.87) * mm, "end": v(18.86, -17.62) * mm});
            skLineSegment(sketch, "E1665", {"start": v(18.86, -17.62) * mm, "end": v(18.79, -17.44) * mm});
            skLineSegment(sketch, "E1666", {"start": v(18.79, -17.44) * mm, "end": v(18.7, -17.27) * mm});
            skLineSegment(sketch, "E1667", {"start": v(18.7, -17.27) * mm, "end": v(18.63, -17.17) * mm});
            skLineSegment(sketch, "E1668", {"start": v(18.63, -17.17) * mm, "end": v(18.6, -17.11) * mm});
            skLineSegment(sketch, "E1669", {"start": v(18.6, -17.11) * mm, "end": v(18.55, -17.05) * mm});
            skLineSegment(sketch, "E1670", {"start": v(18.55, -17.05) * mm, "end": v(18.46, -16.95) * mm});
            skLineSegment(sketch, "E1671", {"start": v(18.46, -16.95) * mm, "end": v(18.2, -16.7) * mm});
            skLineSegment(sketch, "E1672", {"start": v(18.2, -16.7) * mm, "end": v(18.06, -16.62) * mm});
            skLineSegment(sketch, "E1673", {"start": v(18.06, -16.62) * mm, "end": v(17.89, -16.53) * mm});
            skLineSegment(sketch, "E1674", {"start": v(17.89, -16.53) * mm, "end": v(17.7, -16.45) * mm});
            skLineSegment(sketch, "E1675", {"start": v(17.7, -16.45) * mm, "end": v(17.53, -16.38) * mm});
            skLineSegment(sketch, "E1676", {"start": v(17.53, -16.38) * mm, "end": v(17.42, -16.36) * mm});
            skLineSegment(sketch, "E1677", {"start": v(17.42, -16.36) * mm, "end": v(17.3, -16.35) * mm});
            skLineSegment(sketch, "E1678", {"start": v(17.3, -16.35) * mm, "end": v(17.02, -16.34) * mm});
            skLineSegment(sketch, "E1679", {"start": v(17.02, -16.34) * mm, "end": v(16.73, -16.35) * mm});
            skLineSegment(sketch, "E1680", {"start": v(7.5, -17.24) * mm, "end": v(9.5, -17.24) * mm});
            skLineSegment(sketch, "E1681", {"start": v(9.5, -17.24) * mm, "end": v(9.5, -14.24) * mm});
            skLineSegment(sketch, "E1682", {"start": v(9.5, -14.24) * mm, "end": v(7.5, -14.24) * mm});
            skLineSegment(sketch, "E1683", {"start": v(7.5, -14.24) * mm, "end": v(7.5, -17.24) * mm});
            skLineSegment(sketch, "E1684", {"start": v(32.5, -32.48) * mm, "end": v(35.5, -32.48) * mm});
            skLineSegment(sketch, "E1685", {"start": v(35.5, -32.48) * mm, "end": v(35.5, -30.48) * mm});
            skLineSegment(sketch, "E1686", {"start": v(35.5, -30.48) * mm, "end": v(32.5, -30.48) * mm});
            skLineSegment(sketch, "E1687", {"start": v(32.5, -30.48) * mm, "end": v(32.5, -32.48) * mm});
            skLineSegment(sketch, "E1688", {"start": v(26.5, -9.84) * mm, "end": v(41.5, -9.84) * mm});
            skLineSegment(sketch, "E1689", {"start": v(41.5, -9.84) * mm, "end": v(41.5, -1) * mm});
            skLineSegment(sketch, "E1690", {"start": v(41.5, -1) * mm, "end": v(26.5, -1) * mm});
            skLineSegment(sketch, "E1691", {"start": v(26.5, -1) * mm, "end": v(26.5, -9.84) * mm});
            skArc(sketch, "E1692", {"start": v(34.76, -6.02) * mm, "mid": v(35.5, -7.79) * mm, "end": v(37.26, -8.52) * mm});
            skArc(sketch, "E1693", {"start": v(37.26, -8.52) * mm, "mid": v(39.03, -7.79) * mm, "end": v(39.76, -6.02) * mm});
            skArc(sketch, "E1694", {"start": v(39.76, -6.02) * mm, "mid": v(39.03, -4.25) * mm, "end": v(37.26, -3.52) * mm});
            skArc(sketch, "E1695", {"start": v(37.26, -3.52) * mm, "mid": v(35.5, -4.25) * mm, "end": v(34.76, -6.02) * mm});
            skLineSegment(sketch, "E1696", {"start": v(26.5, -1) * mm, "end": v(26.5, -24.48) * mm});
            skArc(sketch, "E1697", {"start": v(26.5, -24.48) * mm, "mid": v(28.26, -28.73) * mm, "end": v(32.5, -30.48) * mm});
            skLineSegment(sketch, "E1698", {"start": v(32.5, -30.48) * mm, "end": v(35.5, -30.48) * mm});
            skArc(sketch, "E1699", {"start": v(35.5, -30.48) * mm, "mid": v(39.74, -28.73) * mm, "end": v(41.5, -24.48) * mm});
            skLineSegment(sketch, "E1700", {"start": v(41.5, -24.48) * mm, "end": v(41.5, -1) * mm});
            skArc(sketch, "E1701", {"start": v(28.26, -6.02) * mm, "mid": v(29, -7.79) * mm, "end": v(30.76, -8.52) * mm});
            skArc(sketch, "E1702", {"start": v(30.76, -8.52) * mm, "mid": v(32.53, -7.79) * mm, "end": v(33.26, -6.02) * mm});
            skArc(sketch, "E1703", {"start": v(33.26, -6.02) * mm, "mid": v(32.53, -4.25) * mm, "end": v(30.76, -3.52) * mm});
            skArc(sketch, "E1704", {"start": v(30.76, -3.52) * mm, "mid": v(29, -4.25) * mm, "end": v(28.26, -6.02) * mm});
            skArc(sketch, "E1705", {"start": v(30.76, -4.52) * mm, "mid": v(29.7, -4.96) * mm, "end": v(29.26, -6.02) * mm});
            skArc(sketch, "E1706", {"start": v(29.26, -6.02) * mm, "mid": v(29.7, -7.08) * mm, "end": v(30.76, -7.52) * mm});
            skArc(sketch, "E1707", {"start": v(30.76, -7.52) * mm, "mid": v(31.82, -7.08) * mm, "end": v(32.26, -6.02) * mm});
            skArc(sketch, "E1708", {"start": v(32.26, -6.02) * mm, "mid": v(31.82, -4.96) * mm, "end": v(30.76, -4.52) * mm});
            skArc(sketch, "E1709", {"start": v(37.27, -4.52) * mm, "mid": v(36.2, -4.96) * mm, "end": v(35.77, -6.02) * mm});
            skArc(sketch, "E1710", {"start": v(35.77, -6.02) * mm, "mid": v(36.2, -7.08) * mm, "end": v(37.27, -7.52) * mm});
            skArc(sketch, "E1711", {"start": v(37.27, -7.52) * mm, "mid": v(38.33, -7.08) * mm, "end": v(38.77, -6.02) * mm});
            skArc(sketch, "E1712", {"start": v(38.77, -6.02) * mm, "mid": v(38.33, -4.96) * mm, "end": v(37.27, -4.52) * mm});
            skLineSegment(sketch, "E1713", {"start": v(33.73, -16.35) * mm, "end": v(33.6, -16.36) * mm});
            skLineSegment(sketch, "E1714", {"start": v(33.6, -16.36) * mm, "end": v(33.5, -16.38) * mm});
            skLineSegment(sketch, "E1715", {"start": v(33.5, -16.38) * mm, "end": v(33.28, -16.46) * mm});
            skLineSegment(sketch, "E1716", {"start": v(33.28, -16.46) * mm, "end": v(33.06, -16.57) * mm});
            skLineSegment(sketch, "E1717", {"start": v(33.06, -16.57) * mm, "end": v(32.85, -16.7) * mm});
            skLineSegment(sketch, "E1718", {"start": v(32.85, -16.7) * mm, "end": v(32.67, -16.85) * mm});
            skLineSegment(sketch, "E1719", {"start": v(32.67, -16.85) * mm, "end": v(32.47, -17.04) * mm});
            skLineSegment(sketch, "E1720", {"start": v(32.47, -17.04) * mm, "end": v(32.4, -17.16) * mm});
            skLineSegment(sketch, "E1721", {"start": v(32.4, -17.16) * mm, "end": v(32.4, -17.17) * mm});
            skLineSegment(sketch, "E1722", {"start": v(32.4, -17.17) * mm, "end": v(32.34, -17.27) * mm});
            skLineSegment(sketch, "E1723", {"start": v(32.34, -17.27) * mm, "end": v(32.24, -17.44) * mm});
            skLineSegment(sketch, "E1724", {"start": v(32.24, -17.44) * mm, "end": v(32.17, -17.62) * mm});
            skLineSegment(sketch, "E1725", {"start": v(32.17, -17.62) * mm, "end": v(32.09, -17.87) * mm});
            skLineSegment(sketch, "E1726", {"start": v(32.09, -17.87) * mm, "end": v(32.05, -17.97) * mm});
            skLineSegment(sketch, "E1727", {"start": v(32.05, -17.97) * mm, "end": v(32.05, -25.07) * mm});
            skLineSegment(sketch, "E1728", {"start": v(32.05, -25.07) * mm, "end": v(32.09, -25.16) * mm});
            skLineSegment(sketch, "E1729", {"start": v(32.09, -25.16) * mm, "end": v(32.16, -25.39) * mm});
            skLineSegment(sketch, "E1730", {"start": v(32.16, -25.39) * mm, "end": v(32.21, -25.54) * mm});
            skLineSegment(sketch, "E1731", {"start": v(32.21, -25.54) * mm, "end": v(32.26, -25.65) * mm});
            skLineSegment(sketch, "E1732", {"start": v(32.26, -25.65) * mm, "end": v(32.33, -25.76) * mm});
            skLineSegment(sketch, "E1733", {"start": v(32.33, -25.76) * mm, "end": v(32.4, -25.86) * mm});
            skLineSegment(sketch, "E1734", {"start": v(32.4, -25.86) * mm, "end": v(32.41, -25.87) * mm});
            skLineSegment(sketch, "E1735", {"start": v(32.41, -25.87) * mm, "end": v(32.42, -25.9) * mm});
            skLineSegment(sketch, "E1736", {"start": v(32.42, -25.9) * mm, "end": v(32.48, -26) * mm});
            skLineSegment(sketch, "E1737", {"start": v(32.48, -26) * mm, "end": v(32.58, -26.1) * mm});
            skLineSegment(sketch, "E1738", {"start": v(32.58, -26.1) * mm, "end": v(32.78, -26.29) * mm});
            skLineSegment(sketch, "E1739", {"start": v(32.78, -26.29) * mm, "end": v(32.87, -26.35) * mm});
            skLineSegment(sketch, "E1740", {"start": v(32.87, -26.35) * mm, "end": v(32.93, -26.38) * mm});
            skLineSegment(sketch, "E1741", {"start": v(32.93, -26.38) * mm, "end": v(32.96, -26.4) * mm});
            skLineSegment(sketch, "E1742", {"start": v(32.96, -26.4) * mm, "end": v(33.05, -26.46) * mm});
            skLineSegment(sketch, "E1743", {"start": v(33.05, -26.46) * mm, "end": v(33.34, -26.6) * mm});
            skLineSegment(sketch, "E1744", {"start": v(33.34, -26.6) * mm, "end": v(33.49, -26.65) * mm});
            skLineSegment(sketch, "E1745", {"start": v(33.49, -26.65) * mm, "end": v(33.65, -26.68) * mm});
            skLineSegment(sketch, "E1746", {"start": v(33.65, -26.68) * mm, "end": v(33.83, -26.7) * mm});
            skLineSegment(sketch, "E1747", {"start": v(33.83, -26.7) * mm, "end": v(34, -26.7) * mm});
            skLineSegment(sketch, "E1748", {"start": v(34, -26.7) * mm, "end": v(34.19, -26.7) * mm});
            skLineSegment(sketch, "E1749", {"start": v(34.19, -26.7) * mm, "end": v(34.36, -26.68) * mm});
            skLineSegment(sketch, "E1750", {"start": v(34.36, -26.68) * mm, "end": v(34.53, -26.65) * mm});
            skLineSegment(sketch, "E1751", {"start": v(34.53, -26.65) * mm, "end": v(34.68, -26.6) * mm});
            skLineSegment(sketch, "E1752", {"start": v(34.68, -26.6) * mm, "end": v(34.98, -26.46) * mm});
            skLineSegment(sketch, "E1753", {"start": v(34.98, -26.46) * mm, "end": v(35.08, -26.4) * mm});
            skLineSegment(sketch, "E1754", {"start": v(35.08, -26.4) * mm, "end": v(35.11, -26.37) * mm});
            skLineSegment(sketch, "E1755", {"start": v(35.11, -26.37) * mm, "end": v(35.14, -26.36) * mm});
            skLineSegment(sketch, "E1756", {"start": v(35.14, -26.36) * mm, "end": v(35.22, -26.3) * mm});
            skLineSegment(sketch, "E1757", {"start": v(35.22, -26.3) * mm, "end": v(35.37, -26.17) * mm});
            skLineSegment(sketch, "E1758", {"start": v(35.37, -26.17) * mm, "end": v(35.52, -26.03) * mm});
            skLineSegment(sketch, "E1759", {"start": v(35.52, -26.03) * mm, "end": v(35.58, -25.95) * mm});
            skLineSegment(sketch, "E1760", {"start": v(35.58, -25.95) * mm, "end": v(35.6, -25.89) * mm});
            skLineSegment(sketch, "E1761", {"start": v(35.6, -25.89) * mm, "end": v(35.62, -25.87) * mm});
            skLineSegment(sketch, "E1762", {"start": v(35.62, -25.87) * mm, "end": v(35.62, -25.86) * mm});
            skLineSegment(sketch, "E1763", {"start": v(35.62, -25.86) * mm, "end": v(35.69, -25.78) * mm});
            skLineSegment(sketch, "E1764", {"start": v(35.69, -25.78) * mm, "end": v(35.75, -25.7) * mm});
            skLineSegment(sketch, "E1765", {"start": v(35.75, -25.7) * mm, "end": v(35.8, -25.57) * mm});
            skLineSegment(sketch, "E1766", {"start": v(35.8, -25.57) * mm, "end": v(35.94, -25.16) * mm});
            skLineSegment(sketch, "E1767", {"start": v(35.94, -25.16) * mm, "end": v(35.98, -25.03) * mm});
            skLineSegment(sketch, "E1768", {"start": v(35.98, -25.03) * mm, "end": v(35.98, -17.97) * mm});
            skLineSegment(sketch, "E1769", {"start": v(35.98, -17.97) * mm, "end": v(35.94, -17.87) * mm});
            skLineSegment(sketch, "E1770", {"start": v(35.94, -17.87) * mm, "end": v(35.86, -17.62) * mm});
            skLineSegment(sketch, "E1771", {"start": v(35.86, -17.62) * mm, "end": v(35.79, -17.44) * mm});
            skLineSegment(sketch, "E1772", {"start": v(35.79, -17.44) * mm, "end": v(35.7, -17.27) * mm});
            skLineSegment(sketch, "E1773", {"start": v(35.7, -17.27) * mm, "end": v(35.63, -17.17) * mm});
            skLineSegment(sketch, "E1774", {"start": v(35.63, -17.17) * mm, "end": v(35.6, -17.11) * mm});
            skLineSegment(sketch, "E1775", {"start": v(35.6, -17.11) * mm, "end": v(35.55, -17.05) * mm});
            skLineSegment(sketch, "E1776", {"start": v(35.55, -17.05) * mm, "end": v(35.46, -16.95) * mm});
            skLineSegment(sketch, "E1777", {"start": v(35.46, -16.95) * mm, "end": v(35.2, -16.7) * mm});
            skLineSegment(sketch, "E1778", {"start": v(35.2, -16.7) * mm, "end": v(35.06, -16.62) * mm});
            skLineSegment(sketch, "E1779", {"start": v(35.06, -16.62) * mm, "end": v(34.89, -16.53) * mm});
            skLineSegment(sketch, "E1780", {"start": v(34.89, -16.53) * mm, "end": v(34.7, -16.45) * mm});
            skLineSegment(sketch, "E1781", {"start": v(34.7, -16.45) * mm, "end": v(34.53, -16.38) * mm});
            skLineSegment(sketch, "E1782", {"start": v(34.53, -16.38) * mm, "end": v(34.42, -16.36) * mm});
            skLineSegment(sketch, "E1783", {"start": v(34.42, -16.36) * mm, "end": v(34.3, -16.35) * mm});
            skLineSegment(sketch, "E1784", {"start": v(34.3, -16.35) * mm, "end": v(34.02, -16.34) * mm});
            skLineSegment(sketch, "E1785", {"start": v(34.02, -16.34) * mm, "end": v(33.73, -16.35) * mm});
            skLineSegment(sketch, "E1786", {"start": v(24.5, -17.24) * mm, "end": v(26.5, -17.24) * mm});
            skLineSegment(sketch, "E1787", {"start": v(26.5, -17.24) * mm, "end": v(26.5, -14.24) * mm});
            skLineSegment(sketch, "E1788", {"start": v(26.5, -14.24) * mm, "end": v(24.5, -14.24) * mm});
            skLineSegment(sketch, "E1789", {"start": v(24.5, -14.24) * mm, "end": v(24.5, -17.24) * mm});
            skLineSegment(sketch, "E1790", {"start": v(-1.5, -32.48) * mm, "end": v(1.5, -32.48) * mm});
            skLineSegment(sketch, "E1791", {"start": v(1.5, -32.48) * mm, "end": v(1.5, -30.48) * mm});
            skLineSegment(sketch, "E1792", {"start": v(1.5, -30.48) * mm, "end": v(-1.5, -30.48) * mm});
            skLineSegment(sketch, "E1793", {"start": v(-1.5, -30.48) * mm, "end": v(-1.5, -32.48) * mm});
            skLineSegment(sketch, "E1794", {"start": v(-7.5, -9.84) * mm, "end": v(7.5, -9.84) * mm});
            skLineSegment(sketch, "E1795", {"start": v(7.5, -9.84) * mm, "end": v(7.5, -1) * mm});
            skLineSegment(sketch, "E1796", {"start": v(7.5, -1) * mm, "end": v(-7.5, -1) * mm});
            skLineSegment(sketch, "E1797", {"start": v(-7.5, -1) * mm, "end": v(-7.5, -9.84) * mm});
            skArc(sketch, "E1798", {"start": v(0.76, -6.02) * mm, "mid": v(1.5, -7.79) * mm, "end": v(3.26, -8.52) * mm});
            skArc(sketch, "E1799", {"start": v(3.26, -8.52) * mm, "mid": v(5.03, -7.79) * mm, "end": v(5.76, -6.02) * mm});
            skArc(sketch, "E1800", {"start": v(5.76, -6.02) * mm, "mid": v(5.03, -4.25) * mm, "end": v(3.26, -3.52) * mm});
            skArc(sketch, "E1801", {"start": v(3.26, -3.52) * mm, "mid": v(1.5, -4.25) * mm, "end": v(0.76, -6.02) * mm});
            skLineSegment(sketch, "E1802", {"start": v(-7.5, -1) * mm, "end": v(-7.5, -24.48) * mm});
            skArc(sketch, "E1803", {"start": v(-7.5, -24.48) * mm, "mid": v(-5.74, -28.73) * mm, "end": v(-1.5, -30.48) * mm});
            skLineSegment(sketch, "E1804", {"start": v(-1.5, -30.48) * mm, "end": v(1.5, -30.48) * mm});
            skArc(sketch, "E1805", {"start": v(1.5, -30.48) * mm, "mid": v(5.74, -28.73) * mm, "end": v(7.5, -24.48) * mm});
            skLineSegment(sketch, "E1806", {"start": v(7.5, -24.48) * mm, "end": v(7.5, -1) * mm});
            skArc(sketch, "E1807", {"start": v(-5.74, -6.02) * mm, "mid": v(-5, -7.79) * mm, "end": v(-3.24, -8.52) * mm});
            skArc(sketch, "E1808", {"start": v(-3.24, -8.52) * mm, "mid": v(-1.47, -7.79) * mm, "end": v(-0.74, -6.02) * mm});
            skArc(sketch, "E1809", {"start": v(-0.74, -6.02) * mm, "mid": v(-1.47, -4.25) * mm, "end": v(-3.24, -3.52) * mm});
            skArc(sketch, "E1810", {"start": v(-3.24, -3.52) * mm, "mid": v(-5, -4.25) * mm, "end": v(-5.74, -6.02) * mm});
            skArc(sketch, "E1811", {"start": v(-3.24, -4.52) * mm, "mid": v(-4.3, -4.96) * mm, "end": v(-4.74, -6.02) * mm});
            skArc(sketch, "E1812", {"start": v(-4.74, -6.02) * mm, "mid": v(-4.3, -7.08) * mm, "end": v(-3.24, -7.52) * mm});
            skArc(sketch, "E1813", {"start": v(-3.24, -7.52) * mm, "mid": v(-2.18, -7.08) * mm, "end": v(-1.74, -6.02) * mm});
            skArc(sketch, "E1814", {"start": v(-1.74, -6.02) * mm, "mid": v(-2.18, -4.96) * mm, "end": v(-3.24, -4.52) * mm});
            skArc(sketch, "E1815", {"start": v(3.26, -4.52) * mm, "mid": v(2.2, -4.96) * mm, "end": v(1.76, -6.02) * mm});
            skArc(sketch, "E1816", {"start": v(1.76, -6.02) * mm, "mid": v(2.2, -7.08) * mm, "end": v(3.26, -7.52) * mm});
            skArc(sketch, "E1817", {"start": v(3.26, -7.52) * mm, "mid": v(4.33, -7.08) * mm, "end": v(4.76, -6.02) * mm});
            skArc(sketch, "E1818", {"start": v(4.76, -6.02) * mm, "mid": v(4.33, -4.96) * mm, "end": v(3.26, -4.52) * mm});
            skLineSegment(sketch, "E1819", {"start": v(-0.27, -16.35) * mm, "end": v(-0.4, -16.36) * mm});
            skLineSegment(sketch, "E1820", {"start": v(-0.4, -16.36) * mm, "end": v(-0.5, -16.38) * mm});
            skLineSegment(sketch, "E1821", {"start": v(-0.5, -16.38) * mm, "end": v(-0.72, -16.46) * mm});
            skLineSegment(sketch, "E1822", {"start": v(-0.72, -16.46) * mm, "end": v(-0.94, -16.57) * mm});
            skLineSegment(sketch, "E1823", {"start": v(-0.94, -16.57) * mm, "end": v(-1.15, -16.7) * mm});
            skLineSegment(sketch, "E1824", {"start": v(-1.15, -16.7) * mm, "end": v(-1.33, -16.85) * mm});
            skLineSegment(sketch, "E1825", {"start": v(-1.33, -16.85) * mm, "end": v(-1.53, -17.04) * mm});
            skLineSegment(sketch, "E1826", {"start": v(-1.53, -17.04) * mm, "end": v(-1.6, -17.16) * mm});
            skLineSegment(sketch, "E1827", {"start": v(-1.6, -17.16) * mm, "end": v(-1.6, -17.17) * mm});
            skLineSegment(sketch, "E1828", {"start": v(-1.6, -17.17) * mm, "end": v(-1.66, -17.27) * mm});
            skLineSegment(sketch, "E1829", {"start": v(-1.66, -17.27) * mm, "end": v(-1.76, -17.44) * mm});
            skLineSegment(sketch, "E1830", {"start": v(-1.76, -17.44) * mm, "end": v(-1.83, -17.62) * mm});
            skLineSegment(sketch, "E1831", {"start": v(-1.83, -17.62) * mm, "end": v(-1.91, -17.87) * mm});
            skLineSegment(sketch, "E1832", {"start": v(-1.91, -17.87) * mm, "end": v(-1.95, -17.97) * mm});
            skLineSegment(sketch, "E1833", {"start": v(-1.95, -17.97) * mm, "end": v(-1.95, -25.07) * mm});
            skLineSegment(sketch, "E1834", {"start": v(-1.95, -25.07) * mm, "end": v(-1.91, -25.16) * mm});
            skLineSegment(sketch, "E1835", {"start": v(-1.91, -25.16) * mm, "end": v(-1.84, -25.39) * mm});
            skLineSegment(sketch, "E1836", {"start": v(-1.84, -25.39) * mm, "end": v(-1.79, -25.54) * mm});
            skLineSegment(sketch, "E1837", {"start": v(-1.79, -25.54) * mm, "end": v(-1.74, -25.65) * mm});
            skLineSegment(sketch, "E1838", {"start": v(-1.74, -25.65) * mm, "end": v(-1.67, -25.76) * mm});
            skLineSegment(sketch, "E1839", {"start": v(-1.67, -25.76) * mm, "end": v(-1.6, -25.86) * mm});
            skLineSegment(sketch, "E1840", {"start": v(-1.6, -25.86) * mm, "end": v(-1.59, -25.87) * mm});
            skLineSegment(sketch, "E1841", {"start": v(-1.59, -25.87) * mm, "end": v(-1.58, -25.9) * mm});
            skLineSegment(sketch, "E1842", {"start": v(-1.58, -25.9) * mm, "end": v(-1.52, -26) * mm});
            skLineSegment(sketch, "E1843", {"start": v(-1.52, -26) * mm, "end": v(-1.42, -26.1) * mm});
            skLineSegment(sketch, "E1844", {"start": v(-1.42, -26.1) * mm, "end": v(-1.22, -26.29) * mm});
            skLineSegment(sketch, "E1845", {"start": v(-1.22, -26.29) * mm, "end": v(-1.13, -26.35) * mm});
            skLineSegment(sketch, "E1846", {"start": v(-1.13, -26.35) * mm, "end": v(-1.07, -26.38) * mm});
            skLineSegment(sketch, "E1847", {"start": v(-1.07, -26.38) * mm, "end": v(-1.04, -26.4) * mm});
            skLineSegment(sketch, "E1848", {"start": v(-1.04, -26.4) * mm, "end": v(-0.95, -26.46) * mm});
            skLineSegment(sketch, "E1849", {"start": v(-0.95, -26.46) * mm, "end": v(-0.66, -26.6) * mm});
            skLineSegment(sketch, "E1850", {"start": v(-0.66, -26.6) * mm, "end": v(-0.51, -26.65) * mm});
            skLineSegment(sketch, "E1851", {"start": v(-0.51, -26.65) * mm, "end": v(-0.35, -26.68) * mm});
            skLineSegment(sketch, "E1852", {"start": v(-0.35, -26.68) * mm, "end": v(-0.17, -26.7) * mm});
            skLineSegment(sketch, "E1853", {"start": v(-0.17, -26.7) * mm, "end": v(0, -26.7) * mm});
            skLineSegment(sketch, "E1854", {"start": v(0, -26.7) * mm, "end": v(0.19, -26.7) * mm});
            skLineSegment(sketch, "E1855", {"start": v(0.19, -26.7) * mm, "end": v(0.36, -26.68) * mm});
            skLineSegment(sketch, "E1856", {"start": v(0.36, -26.68) * mm, "end": v(0.53, -26.65) * mm});
            skLineSegment(sketch, "E1857", {"start": v(0.53, -26.65) * mm, "end": v(0.68, -26.6) * mm});
            skLineSegment(sketch, "E1858", {"start": v(0.68, -26.6) * mm, "end": v(0.98, -26.46) * mm});
            skLineSegment(sketch, "E1859", {"start": v(0.98, -26.46) * mm, "end": v(1.08, -26.4) * mm});
            skLineSegment(sketch, "E1860", {"start": v(1.08, -26.4) * mm, "end": v(1.11, -26.37) * mm});
            skLineSegment(sketch, "E1861", {"start": v(1.11, -26.37) * mm, "end": v(1.14, -26.36) * mm});
            skLineSegment(sketch, "E1862", {"start": v(1.14, -26.36) * mm, "end": v(1.22, -26.3) * mm});
            skLineSegment(sketch, "E1863", {"start": v(1.22, -26.3) * mm, "end": v(1.37, -26.17) * mm});
            skLineSegment(sketch, "E1864", {"start": v(1.37, -26.17) * mm, "end": v(1.52, -26.03) * mm});
            skLineSegment(sketch, "E1865", {"start": v(1.52, -26.03) * mm, "end": v(1.58, -25.95) * mm});
            skLineSegment(sketch, "E1866", {"start": v(1.58, -25.95) * mm, "end": v(1.6, -25.89) * mm});
            skLineSegment(sketch, "E1867", {"start": v(1.6, -25.89) * mm, "end": v(1.62, -25.87) * mm});
            skLineSegment(sketch, "E1868", {"start": v(1.62, -25.87) * mm, "end": v(1.62, -25.86) * mm});
            skLineSegment(sketch, "E1869", {"start": v(1.62, -25.86) * mm, "end": v(1.69, -25.78) * mm});
            skLineSegment(sketch, "E1870", {"start": v(1.69, -25.78) * mm, "end": v(1.75, -25.7) * mm});
            skLineSegment(sketch, "E1871", {"start": v(1.75, -25.7) * mm, "end": v(1.8, -25.57) * mm});
            skLineSegment(sketch, "E1872", {"start": v(1.8, -25.57) * mm, "end": v(1.94, -25.16) * mm});
            skLineSegment(sketch, "E1873", {"start": v(1.94, -25.16) * mm, "end": v(1.98, -25.03) * mm});
            skLineSegment(sketch, "E1874", {"start": v(1.98, -25.03) * mm, "end": v(1.98, -17.97) * mm});
            skLineSegment(sketch, "E1875", {"start": v(1.98, -17.97) * mm, "end": v(1.94, -17.87) * mm});
            skLineSegment(sketch, "E1876", {"start": v(1.94, -17.87) * mm, "end": v(1.86, -17.62) * mm});
            skLineSegment(sketch, "E1877", {"start": v(1.86, -17.62) * mm, "end": v(1.79, -17.44) * mm});
            skLineSegment(sketch, "E1878", {"start": v(1.79, -17.44) * mm, "end": v(1.7, -17.27) * mm});
            skLineSegment(sketch, "E1879", {"start": v(1.7, -17.27) * mm, "end": v(1.63, -17.17) * mm});
            skLineSegment(sketch, "E1880", {"start": v(1.63, -17.17) * mm, "end": v(1.6, -17.11) * mm});
            skLineSegment(sketch, "E1881", {"start": v(1.6, -17.11) * mm, "end": v(1.55, -17.05) * mm});
            skLineSegment(sketch, "E1882", {"start": v(1.55, -17.05) * mm, "end": v(1.46, -16.95) * mm});
            skLineSegment(sketch, "E1883", {"start": v(1.46, -16.95) * mm, "end": v(1.2, -16.7) * mm});
            skLineSegment(sketch, "E1884", {"start": v(1.2, -16.7) * mm, "end": v(1.06, -16.62) * mm});
            skLineSegment(sketch, "E1885", {"start": v(1.06, -16.62) * mm, "end": v(0.89, -16.53) * mm});
            skLineSegment(sketch, "E1886", {"start": v(0.89, -16.53) * mm, "end": v(0.7, -16.45) * mm});
            skLineSegment(sketch, "E1887", {"start": v(0.7, -16.45) * mm, "end": v(0.53, -16.38) * mm});
            skLineSegment(sketch, "E1888", {"start": v(0.53, -16.38) * mm, "end": v(0.42, -16.36) * mm});
            skLineSegment(sketch, "E1889", {"start": v(0.42, -16.36) * mm, "end": v(0.3, -16.35) * mm});
            skLineSegment(sketch, "E1890", {"start": v(0.3, -16.35) * mm, "end": v(0.02, -16.34) * mm});
            skLineSegment(sketch, "E1891", {"start": v(0.02, -16.34) * mm, "end": v(-0.27, -16.35) * mm});
            skLineSegment(sketch, "E1892", {"start": v(-9.5, -17.24) * mm, "end": v(-7.5, -17.24) * mm});
            skLineSegment(sketch, "E1893", {"start": v(-7.5, -17.24) * mm, "end": v(-7.5, -14.24) * mm});
            skLineSegment(sketch, "E1894", {"start": v(-7.5, -14.24) * mm, "end": v(-9.5, -14.24) * mm});
            skLineSegment(sketch, "E1895", {"start": v(-9.5, -14.24) * mm, "end": v(-9.5, -17.24) * mm});
            skLineSegment(sketch, "E1896", {"start": v(-58.5, -41.33) * mm, "end": v(-43.5, -41.33) * mm});
            skLineSegment(sketch, "E1897", {"start": v(-43.5, -41.33) * mm, "end": v(-43.5, -32.48) * mm});
            skLineSegment(sketch, "E1898", {"start": v(-43.5, -32.48) * mm, "end": v(-58.5, -32.48) * mm});
            skLineSegment(sketch, "E1899", {"start": v(-58.5, -32.48) * mm, "end": v(-58.5, -41.33) * mm});
            skArc(sketch, "E1900", {"start": v(-50.24, -37.5) * mm, "mid": v(-49.5, -39.27) * mm, "end": v(-47.74, -40) * mm});
            skArc(sketch, "E1901", {"start": v(-47.74, -40) * mm, "mid": v(-45.97, -39.27) * mm, "end": v(-45.24, -37.5) * mm});
            skArc(sketch, "E1902", {"start": v(-45.24, -37.5) * mm, "mid": v(-45.97, -35.73) * mm, "end": v(-47.74, -35) * mm});
            skArc(sketch, "E1903", {"start": v(-47.74, -35) * mm, "mid": v(-49.5, -35.73) * mm, "end": v(-50.24, -37.5) * mm});
            skLineSegment(sketch, "E1904", {"start": v(-58.5, -32.48) * mm, "end": v(-58.5, -55.97) * mm});
            skArc(sketch, "E1905", {"start": v(-58.5, -55.97) * mm, "mid": v(-56.74, -60.21) * mm, "end": v(-52.5, -61.97) * mm});
            skLineSegment(sketch, "E1906", {"start": v(-52.5, -61.97) * mm, "end": v(-49.5, -61.97) * mm});
            skArc(sketch, "E1907", {"start": v(-49.5, -61.97) * mm, "mid": v(-45.26, -60.21) * mm, "end": v(-43.5, -55.97) * mm});
            skLineSegment(sketch, "E1908", {"start": v(-43.5, -55.97) * mm, "end": v(-43.5, -32.48) * mm});
            skArc(sketch, "E1909", {"start": v(-56.74, -37.5) * mm, "mid": v(-56, -39.27) * mm, "end": v(-54.24, -40) * mm});
            skArc(sketch, "E1910", {"start": v(-54.24, -40) * mm, "mid": v(-52.47, -39.27) * mm, "end": v(-51.74, -37.5) * mm});
            skArc(sketch, "E1911", {"start": v(-51.74, -37.5) * mm, "mid": v(-52.47, -35.73) * mm, "end": v(-54.24, -35) * mm});
            skArc(sketch, "E1912", {"start": v(-54.24, -35) * mm, "mid": v(-56, -35.73) * mm, "end": v(-56.74, -37.5) * mm});
            skArc(sketch, "E1913", {"start": v(-54.24, -36) * mm, "mid": v(-55.3, -36.44) * mm, "end": v(-55.74, -37.5) * mm});
            skArc(sketch, "E1914", {"start": v(-55.74, -37.5) * mm, "mid": v(-55.3, -38.56) * mm, "end": v(-54.24, -39) * mm});
            skArc(sketch, "E1915", {"start": v(-54.24, -39) * mm, "mid": v(-53.18, -38.56) * mm, "end": v(-52.74, -37.5) * mm});
            skArc(sketch, "E1916", {"start": v(-52.74, -37.5) * mm, "mid": v(-53.18, -36.44) * mm, "end": v(-54.24, -36) * mm});
            skArc(sketch, "E1917", {"start": v(-47.74, -36) * mm, "mid": v(-48.8, -36.44) * mm, "end": v(-49.24, -37.5) * mm});
            skArc(sketch, "E1918", {"start": v(-49.24, -37.5) * mm, "mid": v(-48.8, -38.56) * mm, "end": v(-47.74, -39) * mm});
            skArc(sketch, "E1919", {"start": v(-47.74, -39) * mm, "mid": v(-46.67, -38.56) * mm, "end": v(-46.24, -37.5) * mm});
            skArc(sketch, "E1920", {"start": v(-46.24, -37.5) * mm, "mid": v(-46.67, -36.44) * mm, "end": v(-47.74, -36) * mm});
            skLineSegment(sketch, "E1921", {"start": v(-51.27, -47.84) * mm, "end": v(-51.4, -47.85) * mm});
            skLineSegment(sketch, "E1922", {"start": v(-51.4, -47.85) * mm, "end": v(-51.5, -47.87) * mm});
            skLineSegment(sketch, "E1923", {"start": v(-51.5, -47.87) * mm, "end": v(-51.72, -47.95) * mm});
            skLineSegment(sketch, "E1924", {"start": v(-51.72, -47.95) * mm, "end": v(-51.94, -48.05) * mm});
            skLineSegment(sketch, "E1925", {"start": v(-51.94, -48.05) * mm, "end": v(-52.15, -48.19) * mm});
            skLineSegment(sketch, "E1926", {"start": v(-52.15, -48.19) * mm, "end": v(-52.33, -48.34) * mm});
            skLineSegment(sketch, "E1927", {"start": v(-52.33, -48.34) * mm, "end": v(-52.53, -48.53) * mm});
            skLineSegment(sketch, "E1928", {"start": v(-52.53, -48.53) * mm, "end": v(-52.6, -48.65) * mm});
            skLineSegment(sketch, "E1929", {"start": v(-52.6, -48.65) * mm, "end": v(-52.6, -48.66) * mm});
            skLineSegment(sketch, "E1930", {"start": v(-52.6, -48.66) * mm, "end": v(-52.66, -48.76) * mm});
            skLineSegment(sketch, "E1931", {"start": v(-52.66, -48.76) * mm, "end": v(-52.76, -48.92) * mm});
            skLineSegment(sketch, "E1932", {"start": v(-52.76, -48.92) * mm, "end": v(-52.83, -49.1) * mm});
            skLineSegment(sketch, "E1933", {"start": v(-52.83, -49.1) * mm, "end": v(-52.91, -49.36) * mm});
            skLineSegment(sketch, "E1934", {"start": v(-52.91, -49.36) * mm, "end": v(-52.95, -49.45) * mm});
            skLineSegment(sketch, "E1935", {"start": v(-52.95, -49.45) * mm, "end": v(-52.95, -56.55) * mm});
            skLineSegment(sketch, "E1936", {"start": v(-52.95, -56.55) * mm, "end": v(-52.91, -56.64) * mm});
            skLineSegment(sketch, "E1937", {"start": v(-52.91, -56.64) * mm, "end": v(-52.84, -56.87) * mm});
            skLineSegment(sketch, "E1938", {"start": v(-52.84, -56.87) * mm, "end": v(-52.79, -57.02) * mm});
            skLineSegment(sketch, "E1939", {"start": v(-52.79, -57.02) * mm, "end": v(-52.74, -57.14) * mm});
            skLineSegment(sketch, "E1940", {"start": v(-52.74, -57.14) * mm, "end": v(-52.67, -57.24) * mm});
            skLineSegment(sketch, "E1941", {"start": v(-52.67, -57.24) * mm, "end": v(-52.6, -57.34) * mm});
            skLineSegment(sketch, "E1942", {"start": v(-52.6, -57.34) * mm, "end": v(-52.59, -57.35) * mm});
            skLineSegment(sketch, "E1943", {"start": v(-52.59, -57.35) * mm, "end": v(-52.58, -57.39) * mm});
            skLineSegment(sketch, "E1944", {"start": v(-52.58, -57.39) * mm, "end": v(-52.52, -57.47) * mm});
            skLineSegment(sketch, "E1945", {"start": v(-52.52, -57.47) * mm, "end": v(-52.42, -57.58) * mm});
            skLineSegment(sketch, "E1946", {"start": v(-52.42, -57.58) * mm, "end": v(-52.22, -57.77) * mm});
            skLineSegment(sketch, "E1947", {"start": v(-52.22, -57.77) * mm, "end": v(-52.13, -57.84) * mm});
            skLineSegment(sketch, "E1948", {"start": v(-52.13, -57.84) * mm, "end": v(-52.07, -57.87) * mm});
            skLineSegment(sketch, "E1949", {"start": v(-52.07, -57.87) * mm, "end": v(-52.04, -57.9) * mm});
            skLineSegment(sketch, "E1950", {"start": v(-52.04, -57.9) * mm, "end": v(-51.95, -57.94) * mm});
            skLineSegment(sketch, "E1951", {"start": v(-51.95, -57.94) * mm, "end": v(-51.66, -58.08) * mm});
            skLineSegment(sketch, "E1952", {"start": v(-51.66, -58.08) * mm, "end": v(-51.51, -58.13) * mm});
            skLineSegment(sketch, "E1953", {"start": v(-51.51, -58.13) * mm, "end": v(-51.35, -58.17) * mm});
            skLineSegment(sketch, "E1954", {"start": v(-51.35, -58.17) * mm, "end": v(-51.17, -58.19) * mm});
            skLineSegment(sketch, "E1955", {"start": v(-51.17, -58.19) * mm, "end": v(-51, -58.2) * mm});
            skLineSegment(sketch, "E1956", {"start": v(-51, -58.2) * mm, "end": v(-50.81, -58.19) * mm});
            skLineSegment(sketch, "E1957", {"start": v(-50.81, -58.19) * mm, "end": v(-50.64, -58.17) * mm});
            skLineSegment(sketch, "E1958", {"start": v(-50.64, -58.17) * mm, "end": v(-50.47, -58.13) * mm});
            skLineSegment(sketch, "E1959", {"start": v(-50.47, -58.13) * mm, "end": v(-50.32, -58.08) * mm});
            skLineSegment(sketch, "E1960", {"start": v(-50.32, -58.08) * mm, "end": v(-50.02, -57.95) * mm});
            skLineSegment(sketch, "E1961", {"start": v(-50.02, -57.95) * mm, "end": v(-49.92, -57.9) * mm});
            skLineSegment(sketch, "E1962", {"start": v(-49.92, -57.9) * mm, "end": v(-49.89, -57.86) * mm});
            skLineSegment(sketch, "E1963", {"start": v(-49.89, -57.86) * mm, "end": v(-49.86, -57.85) * mm});
            skLineSegment(sketch, "E1964", {"start": v(-49.86, -57.85) * mm, "end": v(-49.78, -57.79) * mm});
            skLineSegment(sketch, "E1965", {"start": v(-49.78, -57.79) * mm, "end": v(-49.63, -57.65) * mm});
            skLineSegment(sketch, "E1966", {"start": v(-49.63, -57.65) * mm, "end": v(-49.48, -57.51) * mm});
            skLineSegment(sketch, "E1967", {"start": v(-49.48, -57.51) * mm, "end": v(-49.42, -57.44) * mm});
            skLineSegment(sketch, "E1968", {"start": v(-49.42, -57.44) * mm, "end": v(-49.4, -57.37) * mm});
            skLineSegment(sketch, "E1969", {"start": v(-49.4, -57.37) * mm, "end": v(-49.38, -57.35) * mm});
            skLineSegment(sketch, "E1970", {"start": v(-49.38, -57.35) * mm, "end": v(-49.38, -57.34) * mm});
            skLineSegment(sketch, "E1971", {"start": v(-49.38, -57.34) * mm, "end": v(-49.31, -57.26) * mm});
            skLineSegment(sketch, "E1972", {"start": v(-49.31, -57.26) * mm, "end": v(-49.25, -57.18) * mm});
            skLineSegment(sketch, "E1973", {"start": v(-49.25, -57.18) * mm, "end": v(-49.2, -57.06) * mm});
            skLineSegment(sketch, "E1974", {"start": v(-49.2, -57.06) * mm, "end": v(-49.06, -56.65) * mm});
            skLineSegment(sketch, "E1975", {"start": v(-49.06, -56.65) * mm, "end": v(-49.02, -56.51) * mm});
            skLineSegment(sketch, "E1976", {"start": v(-49.02, -56.51) * mm, "end": v(-49.02, -49.45) * mm});
            skLineSegment(sketch, "E1977", {"start": v(-49.02, -49.45) * mm, "end": v(-49.06, -49.36) * mm});
            skLineSegment(sketch, "E1978", {"start": v(-49.06, -49.36) * mm, "end": v(-49.14, -49.1) * mm});
            skLineSegment(sketch, "E1979", {"start": v(-49.14, -49.1) * mm, "end": v(-49.21, -48.92) * mm});
            skLineSegment(sketch, "E1980", {"start": v(-49.21, -48.92) * mm, "end": v(-49.3, -48.76) * mm});
            skLineSegment(sketch, "E1981", {"start": v(-49.3, -48.76) * mm, "end": v(-49.37, -48.66) * mm});
            skLineSegment(sketch, "E1982", {"start": v(-49.37, -48.66) * mm, "end": v(-49.4, -48.6) * mm});
            skLineSegment(sketch, "E1983", {"start": v(-49.4, -48.6) * mm, "end": v(-49.45, -48.53) * mm});
            skLineSegment(sketch, "E1984", {"start": v(-49.45, -48.53) * mm, "end": v(-49.54, -48.44) * mm});
            skLineSegment(sketch, "E1985", {"start": v(-49.54, -48.44) * mm, "end": v(-49.8, -48.2) * mm});
            skLineSegment(sketch, "E1986", {"start": v(-49.8, -48.2) * mm, "end": v(-49.94, -48.1) * mm});
            skLineSegment(sketch, "E1987", {"start": v(-49.94, -48.1) * mm, "end": v(-50.11, -48.01) * mm});
            skLineSegment(sketch, "E1988", {"start": v(-50.11, -48.01) * mm, "end": v(-50.3, -47.93) * mm});
            skLineSegment(sketch, "E1989", {"start": v(-50.3, -47.93) * mm, "end": v(-50.47, -47.87) * mm});
            skLineSegment(sketch, "E1990", {"start": v(-50.47, -47.87) * mm, "end": v(-50.58, -47.85) * mm});
            skLineSegment(sketch, "E1991", {"start": v(-50.58, -47.85) * mm, "end": v(-50.7, -47.84) * mm});
            skLineSegment(sketch, "E1992", {"start": v(-50.7, -47.84) * mm, "end": v(-50.98, -47.83) * mm});
            skLineSegment(sketch, "E1993", {"start": v(-50.98, -47.83) * mm, "end": v(-51.27, -47.84) * mm});
            skLineSegment(sketch, "E1994", {"start": v(-41.5, -41.33) * mm, "end": v(-26.5, -41.33) * mm});
            skLineSegment(sketch, "E1995", {"start": v(-26.5, -41.33) * mm, "end": v(-26.5, -32.48) * mm});
            skLineSegment(sketch, "E1996", {"start": v(-26.5, -32.48) * mm, "end": v(-41.5, -32.48) * mm});
            skLineSegment(sketch, "E1997", {"start": v(-41.5, -32.48) * mm, "end": v(-41.5, -41.33) * mm});
            skArc(sketch, "E1998", {"start": v(-33.24, -37.5) * mm, "mid": v(-32.5, -39.27) * mm, "end": v(-30.74, -40) * mm});
            skArc(sketch, "E1999", {"start": v(-30.74, -40) * mm, "mid": v(-28.97, -39.27) * mm, "end": v(-28.24, -37.5) * mm});
            skArc(sketch, "E2000", {"start": v(-28.24, -37.5) * mm, "mid": v(-28.97, -35.73) * mm, "end": v(-30.74, -35) * mm});
            skArc(sketch, "E2001", {"start": v(-30.74, -35) * mm, "mid": v(-32.5, -35.73) * mm, "end": v(-33.24, -37.5) * mm});
            skLineSegment(sketch, "E2002", {"start": v(-41.5, -32.48) * mm, "end": v(-41.5, -55.97) * mm});
            skArc(sketch, "E2003", {"start": v(-41.5, -55.97) * mm, "mid": v(-39.74, -60.21) * mm, "end": v(-35.5, -61.97) * mm});
            skLineSegment(sketch, "E2004", {"start": v(-35.5, -61.97) * mm, "end": v(-32.5, -61.97) * mm});
            skArc(sketch, "E2005", {"start": v(-32.5, -61.97) * mm, "mid": v(-28.26, -60.21) * mm, "end": v(-26.5, -55.97) * mm});
            skLineSegment(sketch, "E2006", {"start": v(-26.5, -55.97) * mm, "end": v(-26.5, -32.48) * mm});
            skArc(sketch, "E2007", {"start": v(-39.74, -37.5) * mm, "mid": v(-39, -39.27) * mm, "end": v(-37.24, -40) * mm});
            skArc(sketch, "E2008", {"start": v(-37.24, -40) * mm, "mid": v(-35.47, -39.27) * mm, "end": v(-34.74, -37.5) * mm});
            skArc(sketch, "E2009", {"start": v(-34.74, -37.5) * mm, "mid": v(-35.47, -35.73) * mm, "end": v(-37.24, -35) * mm});
            skArc(sketch, "E2010", {"start": v(-37.24, -35) * mm, "mid": v(-39, -35.73) * mm, "end": v(-39.74, -37.5) * mm});
            skArc(sketch, "E2011", {"start": v(-37.24, -36) * mm, "mid": v(-38.3, -36.44) * mm, "end": v(-38.74, -37.5) * mm});
            skArc(sketch, "E2012", {"start": v(-38.74, -37.5) * mm, "mid": v(-38.3, -38.56) * mm, "end": v(-37.24, -39) * mm});
            skArc(sketch, "E2013", {"start": v(-37.24, -39) * mm, "mid": v(-36.18, -38.56) * mm, "end": v(-35.74, -37.5) * mm});
            skArc(sketch, "E2014", {"start": v(-35.74, -37.5) * mm, "mid": v(-36.18, -36.44) * mm, "end": v(-37.24, -36) * mm});
            skArc(sketch, "E2015", {"start": v(-30.74, -36) * mm, "mid": v(-31.8, -36.44) * mm, "end": v(-32.24, -37.5) * mm});
            skArc(sketch, "E2016", {"start": v(-32.24, -37.5) * mm, "mid": v(-31.8, -38.56) * mm, "end": v(-30.74, -39) * mm});
            skArc(sketch, "E2017", {"start": v(-30.74, -39) * mm, "mid": v(-29.67, -38.56) * mm, "end": v(-29.24, -37.5) * mm});
            skArc(sketch, "E2018", {"start": v(-29.24, -37.5) * mm, "mid": v(-29.67, -36.44) * mm, "end": v(-30.74, -36) * mm});
            skLineSegment(sketch, "E2019", {"start": v(-34.27, -47.84) * mm, "end": v(-34.4, -47.85) * mm});
            skLineSegment(sketch, "E2020", {"start": v(-34.4, -47.85) * mm, "end": v(-34.5, -47.87) * mm});
            skLineSegment(sketch, "E2021", {"start": v(-34.5, -47.87) * mm, "end": v(-34.72, -47.95) * mm});
            skLineSegment(sketch, "E2022", {"start": v(-34.72, -47.95) * mm, "end": v(-34.94, -48.05) * mm});
            skLineSegment(sketch, "E2023", {"start": v(-34.94, -48.05) * mm, "end": v(-35.15, -48.19) * mm});
            skLineSegment(sketch, "E2024", {"start": v(-35.15, -48.19) * mm, "end": v(-35.33, -48.34) * mm});
            skLineSegment(sketch, "E2025", {"start": v(-35.33, -48.34) * mm, "end": v(-35.53, -48.53) * mm});
            skLineSegment(sketch, "E2026", {"start": v(-35.53, -48.53) * mm, "end": v(-35.6, -48.65) * mm});
            skLineSegment(sketch, "E2027", {"start": v(-35.6, -48.65) * mm, "end": v(-35.6, -48.66) * mm});
            skLineSegment(sketch, "E2028", {"start": v(-35.6, -48.66) * mm, "end": v(-35.66, -48.76) * mm});
            skLineSegment(sketch, "E2029", {"start": v(-35.66, -48.76) * mm, "end": v(-35.76, -48.92) * mm});
            skLineSegment(sketch, "E2030", {"start": v(-35.76, -48.92) * mm, "end": v(-35.83, -49.1) * mm});
            skLineSegment(sketch, "E2031", {"start": v(-35.83, -49.1) * mm, "end": v(-35.91, -49.36) * mm});
            skLineSegment(sketch, "E2032", {"start": v(-35.91, -49.36) * mm, "end": v(-35.95, -49.45) * mm});
            skLineSegment(sketch, "E2033", {"start": v(-35.95, -49.45) * mm, "end": v(-35.95, -56.55) * mm});
            skLineSegment(sketch, "E2034", {"start": v(-35.95, -56.55) * mm, "end": v(-35.91, -56.64) * mm});
            skLineSegment(sketch, "E2035", {"start": v(-35.91, -56.64) * mm, "end": v(-35.84, -56.87) * mm});
            skLineSegment(sketch, "E2036", {"start": v(-35.84, -56.87) * mm, "end": v(-35.79, -57.02) * mm});
            skLineSegment(sketch, "E2037", {"start": v(-35.79, -57.02) * mm, "end": v(-35.74, -57.14) * mm});
            skLineSegment(sketch, "E2038", {"start": v(-35.74, -57.14) * mm, "end": v(-35.67, -57.24) * mm});
            skLineSegment(sketch, "E2039", {"start": v(-35.67, -57.24) * mm, "end": v(-35.6, -57.34) * mm});
            skLineSegment(sketch, "E2040", {"start": v(-35.6, -57.34) * mm, "end": v(-35.59, -57.35) * mm});
            skLineSegment(sketch, "E2041", {"start": v(-35.59, -57.35) * mm, "end": v(-35.58, -57.39) * mm});
            skLineSegment(sketch, "E2042", {"start": v(-35.58, -57.39) * mm, "end": v(-35.52, -57.47) * mm});
            skLineSegment(sketch, "E2043", {"start": v(-35.52, -57.47) * mm, "end": v(-35.42, -57.58) * mm});
            skLineSegment(sketch, "E2044", {"start": v(-35.42, -57.58) * mm, "end": v(-35.22, -57.77) * mm});
            skLineSegment(sketch, "E2045", {"start": v(-35.22, -57.77) * mm, "end": v(-35.13, -57.84) * mm});
            skLineSegment(sketch, "E2046", {"start": v(-35.13, -57.84) * mm, "end": v(-35.07, -57.87) * mm});
            skLineSegment(sketch, "E2047", {"start": v(-35.07, -57.87) * mm, "end": v(-35.04, -57.9) * mm});
            skLineSegment(sketch, "E2048", {"start": v(-35.04, -57.9) * mm, "end": v(-34.95, -57.94) * mm});
            skLineSegment(sketch, "E2049", {"start": v(-34.95, -57.94) * mm, "end": v(-34.66, -58.08) * mm});
            skLineSegment(sketch, "E2050", {"start": v(-34.66, -58.08) * mm, "end": v(-34.51, -58.13) * mm});
            skLineSegment(sketch, "E2051", {"start": v(-34.51, -58.13) * mm, "end": v(-34.35, -58.17) * mm});
            skLineSegment(sketch, "E2052", {"start": v(-34.35, -58.17) * mm, "end": v(-34.17, -58.19) * mm});
            skLineSegment(sketch, "E2053", {"start": v(-34.17, -58.19) * mm, "end": v(-34, -58.2) * mm});
            skLineSegment(sketch, "E2054", {"start": v(-34, -58.2) * mm, "end": v(-33.81, -58.19) * mm});
            skLineSegment(sketch, "E2055", {"start": v(-33.81, -58.19) * mm, "end": v(-33.64, -58.17) * mm});
            skLineSegment(sketch, "E2056", {"start": v(-33.64, -58.17) * mm, "end": v(-33.47, -58.13) * mm});
            skLineSegment(sketch, "E2057", {"start": v(-33.47, -58.13) * mm, "end": v(-33.32, -58.08) * mm});
            skLineSegment(sketch, "E2058", {"start": v(-33.32, -58.08) * mm, "end": v(-33.02, -57.95) * mm});
            skLineSegment(sketch, "E2059", {"start": v(-33.02, -57.95) * mm, "end": v(-32.92, -57.9) * mm});
            skLineSegment(sketch, "E2060", {"start": v(-32.92, -57.9) * mm, "end": v(-32.89, -57.86) * mm});
            skLineSegment(sketch, "E2061", {"start": v(-32.89, -57.86) * mm, "end": v(-32.86, -57.85) * mm});
            skLineSegment(sketch, "E2062", {"start": v(-32.86, -57.85) * mm, "end": v(-32.78, -57.79) * mm});
            skLineSegment(sketch, "E2063", {"start": v(-32.78, -57.79) * mm, "end": v(-32.63, -57.65) * mm});
            skLineSegment(sketch, "E2064", {"start": v(-32.63, -57.65) * mm, "end": v(-32.48, -57.51) * mm});
            skLineSegment(sketch, "E2065", {"start": v(-32.48, -57.51) * mm, "end": v(-32.42, -57.44) * mm});
            skLineSegment(sketch, "E2066", {"start": v(-32.42, -57.44) * mm, "end": v(-32.4, -57.37) * mm});
            skLineSegment(sketch, "E2067", {"start": v(-32.4, -57.37) * mm, "end": v(-32.38, -57.35) * mm});
            skLineSegment(sketch, "E2068", {"start": v(-32.38, -57.35) * mm, "end": v(-32.38, -57.34) * mm});
            skLineSegment(sketch, "E2069", {"start": v(-32.38, -57.34) * mm, "end": v(-32.31, -57.26) * mm});
            skLineSegment(sketch, "E2070", {"start": v(-32.31, -57.26) * mm, "end": v(-32.25, -57.18) * mm});
            skLineSegment(sketch, "E2071", {"start": v(-32.25, -57.18) * mm, "end": v(-32.2, -57.06) * mm});
            skLineSegment(sketch, "E2072", {"start": v(-32.2, -57.06) * mm, "end": v(-32.06, -56.65) * mm});
            skLineSegment(sketch, "E2073", {"start": v(-32.06, -56.65) * mm, "end": v(-32.02, -56.51) * mm});
            skLineSegment(sketch, "E2074", {"start": v(-32.02, -56.51) * mm, "end": v(-32.02, -49.45) * mm});
            skLineSegment(sketch, "E2075", {"start": v(-32.02, -49.45) * mm, "end": v(-32.06, -49.36) * mm});
            skLineSegment(sketch, "E2076", {"start": v(-32.06, -49.36) * mm, "end": v(-32.14, -49.1) * mm});
            skLineSegment(sketch, "E2077", {"start": v(-32.14, -49.1) * mm, "end": v(-32.21, -48.92) * mm});
            skLineSegment(sketch, "E2078", {"start": v(-32.21, -48.92) * mm, "end": v(-32.3, -48.76) * mm});
            skLineSegment(sketch, "E2079", {"start": v(-32.3, -48.76) * mm, "end": v(-32.37, -48.66) * mm});
            skLineSegment(sketch, "E2080", {"start": v(-32.37, -48.66) * mm, "end": v(-32.4, -48.6) * mm});
            skLineSegment(sketch, "E2081", {"start": v(-32.4, -48.6) * mm, "end": v(-32.45, -48.53) * mm});
            skLineSegment(sketch, "E2082", {"start": v(-32.45, -48.53) * mm, "end": v(-32.54, -48.44) * mm});
            skLineSegment(sketch, "E2083", {"start": v(-32.54, -48.44) * mm, "end": v(-32.8, -48.2) * mm});
            skLineSegment(sketch, "E2084", {"start": v(-32.8, -48.2) * mm, "end": v(-32.94, -48.1) * mm});
            skLineSegment(sketch, "E2085", {"start": v(-32.94, -48.1) * mm, "end": v(-33.11, -48.01) * mm});
            skLineSegment(sketch, "E2086", {"start": v(-33.11, -48.01) * mm, "end": v(-33.3, -47.93) * mm});
            skLineSegment(sketch, "E2087", {"start": v(-33.3, -47.93) * mm, "end": v(-33.47, -47.87) * mm});
            skLineSegment(sketch, "E2088", {"start": v(-33.47, -47.87) * mm, "end": v(-33.58, -47.85) * mm});
            skLineSegment(sketch, "E2089", {"start": v(-33.58, -47.85) * mm, "end": v(-33.7, -47.84) * mm});
            skLineSegment(sketch, "E2090", {"start": v(-33.7, -47.84) * mm, "end": v(-33.98, -47.83) * mm});
            skLineSegment(sketch, "E2091", {"start": v(-33.98, -47.83) * mm, "end": v(-34.27, -47.84) * mm});
            skLineSegment(sketch, "E2092", {"start": v(-43.5, -48.73) * mm, "end": v(-41.5, -48.73) * mm});
            skLineSegment(sketch, "E2093", {"start": v(-41.5, -48.73) * mm, "end": v(-41.5, -45.73) * mm});
            skLineSegment(sketch, "E2094", {"start": v(-41.5, -45.73) * mm, "end": v(-43.5, -45.73) * mm});
            skLineSegment(sketch, "E2095", {"start": v(-43.5, -45.73) * mm, "end": v(-43.5, -48.73) * mm});
            skLineSegment(sketch, "E2096", {"start": v(-24.5, -41.33) * mm, "end": v(-9.5, -41.33) * mm});
            skLineSegment(sketch, "E2097", {"start": v(-9.5, -41.33) * mm, "end": v(-9.5, -32.48) * mm});
            skLineSegment(sketch, "E2098", {"start": v(-9.5, -32.48) * mm, "end": v(-24.5, -32.48) * mm});
            skLineSegment(sketch, "E2099", {"start": v(-24.5, -32.48) * mm, "end": v(-24.5, -41.33) * mm});
            skArc(sketch, "E2100", {"start": v(-16.24, -37.5) * mm, "mid": v(-15.5, -39.27) * mm, "end": v(-13.74, -40) * mm});
            skArc(sketch, "E2101", {"start": v(-13.74, -40) * mm, "mid": v(-11.97, -39.27) * mm, "end": v(-11.24, -37.5) * mm});
            skArc(sketch, "E2102", {"start": v(-11.24, -37.5) * mm, "mid": v(-11.97, -35.73) * mm, "end": v(-13.74, -35) * mm});
            skArc(sketch, "E2103", {"start": v(-13.74, -35) * mm, "mid": v(-15.5, -35.73) * mm, "end": v(-16.24, -37.5) * mm});
            skLineSegment(sketch, "E2104", {"start": v(-24.5, -32.48) * mm, "end": v(-24.5, -55.97) * mm});
            skArc(sketch, "E2105", {"start": v(-24.5, -55.97) * mm, "mid": v(-22.74, -60.21) * mm, "end": v(-18.5, -61.97) * mm});
            skLineSegment(sketch, "E2106", {"start": v(-18.5, -61.97) * mm, "end": v(-15.5, -61.97) * mm});
            skArc(sketch, "E2107", {"start": v(-15.5, -61.97) * mm, "mid": v(-11.26, -60.21) * mm, "end": v(-9.5, -55.97) * mm});
            skLineSegment(sketch, "E2108", {"start": v(-9.5, -55.97) * mm, "end": v(-9.5, -32.48) * mm});
            skArc(sketch, "E2109", {"start": v(-22.74, -37.5) * mm, "mid": v(-22, -39.27) * mm, "end": v(-20.24, -40) * mm});
            skArc(sketch, "E2110", {"start": v(-20.24, -40) * mm, "mid": v(-18.47, -39.27) * mm, "end": v(-17.74, -37.5) * mm});
            skArc(sketch, "E2111", {"start": v(-17.74, -37.5) * mm, "mid": v(-18.47, -35.73) * mm, "end": v(-20.24, -35) * mm});
            skArc(sketch, "E2112", {"start": v(-20.24, -35) * mm, "mid": v(-22, -35.73) * mm, "end": v(-22.74, -37.5) * mm});
            skArc(sketch, "E2113", {"start": v(-20.24, -36) * mm, "mid": v(-21.3, -36.44) * mm, "end": v(-21.74, -37.5) * mm});
            skArc(sketch, "E2114", {"start": v(-21.74, -37.5) * mm, "mid": v(-21.3, -38.56) * mm, "end": v(-20.24, -39) * mm});
            skArc(sketch, "E2115", {"start": v(-20.24, -39) * mm, "mid": v(-19.18, -38.56) * mm, "end": v(-18.74, -37.5) * mm});
            skArc(sketch, "E2116", {"start": v(-18.74, -37.5) * mm, "mid": v(-19.18, -36.44) * mm, "end": v(-20.24, -36) * mm});
            skArc(sketch, "E2117", {"start": v(-13.74, -36) * mm, "mid": v(-14.8, -36.44) * mm, "end": v(-15.24, -37.5) * mm});
            skArc(sketch, "E2118", {"start": v(-15.24, -37.5) * mm, "mid": v(-14.8, -38.56) * mm, "end": v(-13.74, -39) * mm});
            skArc(sketch, "E2119", {"start": v(-13.74, -39) * mm, "mid": v(-12.67, -38.56) * mm, "end": v(-12.24, -37.5) * mm});
            skArc(sketch, "E2120", {"start": v(-12.24, -37.5) * mm, "mid": v(-12.67, -36.44) * mm, "end": v(-13.74, -36) * mm});
            skLineSegment(sketch, "E2121", {"start": v(-17.27, -47.84) * mm, "end": v(-17.4, -47.85) * mm});
            skLineSegment(sketch, "E2122", {"start": v(-17.4, -47.85) * mm, "end": v(-17.5, -47.87) * mm});
            skLineSegment(sketch, "E2123", {"start": v(-17.5, -47.87) * mm, "end": v(-17.72, -47.95) * mm});
            skLineSegment(sketch, "E2124", {"start": v(-17.72, -47.95) * mm, "end": v(-17.94, -48.05) * mm});
            skLineSegment(sketch, "E2125", {"start": v(-17.94, -48.05) * mm, "end": v(-18.15, -48.19) * mm});
            skLineSegment(sketch, "E2126", {"start": v(-18.15, -48.19) * mm, "end": v(-18.33, -48.34) * mm});
            skLineSegment(sketch, "E2127", {"start": v(-18.33, -48.34) * mm, "end": v(-18.53, -48.53) * mm});
            skLineSegment(sketch, "E2128", {"start": v(-18.53, -48.53) * mm, "end": v(-18.6, -48.65) * mm});
            skLineSegment(sketch, "E2129", {"start": v(-18.6, -48.65) * mm, "end": v(-18.6, -48.66) * mm});
            skLineSegment(sketch, "E2130", {"start": v(-18.6, -48.66) * mm, "end": v(-18.66, -48.76) * mm});
            skLineSegment(sketch, "E2131", {"start": v(-18.66, -48.76) * mm, "end": v(-18.76, -48.92) * mm});
            skLineSegment(sketch, "E2132", {"start": v(-18.76, -48.92) * mm, "end": v(-18.83, -49.1) * mm});
            skLineSegment(sketch, "E2133", {"start": v(-18.83, -49.1) * mm, "end": v(-18.91, -49.36) * mm});
            skLineSegment(sketch, "E2134", {"start": v(-18.91, -49.36) * mm, "end": v(-18.95, -49.45) * mm});
            skLineSegment(sketch, "E2135", {"start": v(-18.95, -49.45) * mm, "end": v(-18.95, -56.55) * mm});
            skLineSegment(sketch, "E2136", {"start": v(-18.95, -56.55) * mm, "end": v(-18.91, -56.64) * mm});
            skLineSegment(sketch, "E2137", {"start": v(-18.91, -56.64) * mm, "end": v(-18.84, -56.87) * mm});
            skLineSegment(sketch, "E2138", {"start": v(-18.84, -56.87) * mm, "end": v(-18.79, -57.02) * mm});
            skLineSegment(sketch, "E2139", {"start": v(-18.79, -57.02) * mm, "end": v(-18.74, -57.14) * mm});
            skLineSegment(sketch, "E2140", {"start": v(-18.74, -57.14) * mm, "end": v(-18.67, -57.24) * mm});
            skLineSegment(sketch, "E2141", {"start": v(-18.67, -57.24) * mm, "end": v(-18.6, -57.34) * mm});
            skLineSegment(sketch, "E2142", {"start": v(-18.6, -57.34) * mm, "end": v(-18.59, -57.35) * mm});
            skLineSegment(sketch, "E2143", {"start": v(-18.59, -57.35) * mm, "end": v(-18.58, -57.39) * mm});
            skLineSegment(sketch, "E2144", {"start": v(-18.58, -57.39) * mm, "end": v(-18.52, -57.47) * mm});
            skLineSegment(sketch, "E2145", {"start": v(-18.52, -57.47) * mm, "end": v(-18.42, -57.58) * mm});
            skLineSegment(sketch, "E2146", {"start": v(-18.42, -57.58) * mm, "end": v(-18.22, -57.77) * mm});
            skLineSegment(sketch, "E2147", {"start": v(-18.22, -57.77) * mm, "end": v(-18.13, -57.84) * mm});
            skLineSegment(sketch, "E2148", {"start": v(-18.13, -57.84) * mm, "end": v(-18.07, -57.87) * mm});
            skLineSegment(sketch, "E2149", {"start": v(-18.07, -57.87) * mm, "end": v(-18.04, -57.9) * mm});
            skLineSegment(sketch, "E2150", {"start": v(-18.04, -57.9) * mm, "end": v(-17.95, -57.94) * mm});
            skLineSegment(sketch, "E2151", {"start": v(-17.95, -57.94) * mm, "end": v(-17.66, -58.08) * mm});
            skLineSegment(sketch, "E2152", {"start": v(-17.66, -58.08) * mm, "end": v(-17.51, -58.13) * mm});
            skLineSegment(sketch, "E2153", {"start": v(-17.51, -58.13) * mm, "end": v(-17.35, -58.17) * mm});
            skLineSegment(sketch, "E2154", {"start": v(-17.35, -58.17) * mm, "end": v(-17.17, -58.19) * mm});
            skLineSegment(sketch, "E2155", {"start": v(-17.17, -58.19) * mm, "end": v(-17, -58.2) * mm});
            skLineSegment(sketch, "E2156", {"start": v(-17, -58.2) * mm, "end": v(-16.81, -58.19) * mm});
            skLineSegment(sketch, "E2157", {"start": v(-16.81, -58.19) * mm, "end": v(-16.64, -58.17) * mm});
            skLineSegment(sketch, "E2158", {"start": v(-16.64, -58.17) * mm, "end": v(-16.47, -58.13) * mm});
            skLineSegment(sketch, "E2159", {"start": v(-16.47, -58.13) * mm, "end": v(-16.32, -58.08) * mm});
            skLineSegment(sketch, "E2160", {"start": v(-16.32, -58.08) * mm, "end": v(-16.02, -57.95) * mm});
            skLineSegment(sketch, "E2161", {"start": v(-16.02, -57.95) * mm, "end": v(-15.92, -57.9) * mm});
            skLineSegment(sketch, "E2162", {"start": v(-15.92, -57.9) * mm, "end": v(-15.89, -57.86) * mm});
            skLineSegment(sketch, "E2163", {"start": v(-15.89, -57.86) * mm, "end": v(-15.86, -57.85) * mm});
            skLineSegment(sketch, "E2164", {"start": v(-15.86, -57.85) * mm, "end": v(-15.78, -57.79) * mm});
            skLineSegment(sketch, "E2165", {"start": v(-15.78, -57.79) * mm, "end": v(-15.63, -57.65) * mm});
            skLineSegment(sketch, "E2166", {"start": v(-15.63, -57.65) * mm, "end": v(-15.48, -57.51) * mm});
            skLineSegment(sketch, "E2167", {"start": v(-15.48, -57.51) * mm, "end": v(-15.42, -57.44) * mm});
            skLineSegment(sketch, "E2168", {"start": v(-15.42, -57.44) * mm, "end": v(-15.4, -57.37) * mm});
            skLineSegment(sketch, "E2169", {"start": v(-15.4, -57.37) * mm, "end": v(-15.38, -57.35) * mm});
            skLineSegment(sketch, "E2170", {"start": v(-15.38, -57.35) * mm, "end": v(-15.38, -57.34) * mm});
            skLineSegment(sketch, "E2171", {"start": v(-15.38, -57.34) * mm, "end": v(-15.31, -57.26) * mm});
            skLineSegment(sketch, "E2172", {"start": v(-15.31, -57.26) * mm, "end": v(-15.25, -57.18) * mm});
            skLineSegment(sketch, "E2173", {"start": v(-15.25, -57.18) * mm, "end": v(-15.2, -57.06) * mm});
            skLineSegment(sketch, "E2174", {"start": v(-15.2, -57.06) * mm, "end": v(-15.06, -56.65) * mm});
            skLineSegment(sketch, "E2175", {"start": v(-15.06, -56.65) * mm, "end": v(-15.02, -56.51) * mm});
            skLineSegment(sketch, "E2176", {"start": v(-15.02, -56.51) * mm, "end": v(-15.02, -49.45) * mm});
            skLineSegment(sketch, "E2177", {"start": v(-15.02, -49.45) * mm, "end": v(-15.06, -49.36) * mm});
            skLineSegment(sketch, "E2178", {"start": v(-15.06, -49.36) * mm, "end": v(-15.14, -49.1) * mm});
            skLineSegment(sketch, "E2179", {"start": v(-15.14, -49.1) * mm, "end": v(-15.21, -48.92) * mm});
            skLineSegment(sketch, "E2180", {"start": v(-15.21, -48.92) * mm, "end": v(-15.3, -48.76) * mm});
            skLineSegment(sketch, "E2181", {"start": v(-15.3, -48.76) * mm, "end": v(-15.37, -48.66) * mm});
            skLineSegment(sketch, "E2182", {"start": v(-15.37, -48.66) * mm, "end": v(-15.4, -48.6) * mm});
            skLineSegment(sketch, "E2183", {"start": v(-15.4, -48.6) * mm, "end": v(-15.45, -48.53) * mm});
            skLineSegment(sketch, "E2184", {"start": v(-15.45, -48.53) * mm, "end": v(-15.54, -48.44) * mm});
            skLineSegment(sketch, "E2185", {"start": v(-15.54, -48.44) * mm, "end": v(-15.8, -48.2) * mm});
            skLineSegment(sketch, "E2186", {"start": v(-15.8, -48.2) * mm, "end": v(-15.94, -48.1) * mm});
            skLineSegment(sketch, "E2187", {"start": v(-15.94, -48.1) * mm, "end": v(-16.11, -48.01) * mm});
            skLineSegment(sketch, "E2188", {"start": v(-16.11, -48.01) * mm, "end": v(-16.3, -47.93) * mm});
            skLineSegment(sketch, "E2189", {"start": v(-16.3, -47.93) * mm, "end": v(-16.47, -47.87) * mm});
            skLineSegment(sketch, "E2190", {"start": v(-16.47, -47.87) * mm, "end": v(-16.58, -47.85) * mm});
            skLineSegment(sketch, "E2191", {"start": v(-16.58, -47.85) * mm, "end": v(-16.7, -47.84) * mm});
            skLineSegment(sketch, "E2192", {"start": v(-16.7, -47.84) * mm, "end": v(-16.98, -47.83) * mm});
            skLineSegment(sketch, "E2193", {"start": v(-16.98, -47.83) * mm, "end": v(-17.27, -47.84) * mm});
            skLineSegment(sketch, "E2194", {"start": v(-26.5, -48.73) * mm, "end": v(-24.5, -48.73) * mm});
            skLineSegment(sketch, "E2195", {"start": v(-24.5, -48.73) * mm, "end": v(-24.5, -45.73) * mm});
            skLineSegment(sketch, "E2196", {"start": v(-24.5, -45.73) * mm, "end": v(-26.5, -45.73) * mm});
            skLineSegment(sketch, "E2197", {"start": v(-26.5, -45.73) * mm, "end": v(-26.5, -48.73) * mm});
            skLineSegment(sketch, "E2198", {"start": v(9.5, -41.33) * mm, "end": v(24.5, -41.33) * mm});
            skLineSegment(sketch, "E2199", {"start": v(24.5, -41.33) * mm, "end": v(24.5, -32.48) * mm});
            skLineSegment(sketch, "E2200", {"start": v(24.5, -32.48) * mm, "end": v(9.5, -32.48) * mm});
            skLineSegment(sketch, "E2201", {"start": v(9.5, -32.48) * mm, "end": v(9.5, -41.33) * mm});
            skArc(sketch, "E2202", {"start": v(17.76, -37.5) * mm, "mid": v(18.5, -39.27) * mm, "end": v(20.26, -40) * mm});
            skArc(sketch, "E2203", {"start": v(20.26, -40) * mm, "mid": v(22.03, -39.27) * mm, "end": v(22.76, -37.5) * mm});
            skArc(sketch, "E2204", {"start": v(22.76, -37.5) * mm, "mid": v(22.03, -35.73) * mm, "end": v(20.26, -35) * mm});
            skArc(sketch, "E2205", {"start": v(20.26, -35) * mm, "mid": v(18.5, -35.73) * mm, "end": v(17.76, -37.5) * mm});
            skLineSegment(sketch, "E2206", {"start": v(9.5, -32.48) * mm, "end": v(9.5, -55.97) * mm});
            skArc(sketch, "E2207", {"start": v(9.5, -55.97) * mm, "mid": v(11.26, -60.21) * mm, "end": v(15.5, -61.97) * mm});
            skLineSegment(sketch, "E2208", {"start": v(15.5, -61.97) * mm, "end": v(18.5, -61.97) * mm});
            skArc(sketch, "E2209", {"start": v(18.5, -61.97) * mm, "mid": v(22.74, -60.21) * mm, "end": v(24.5, -55.97) * mm});
            skLineSegment(sketch, "E2210", {"start": v(24.5, -55.97) * mm, "end": v(24.5, -32.48) * mm});
            skArc(sketch, "E2211", {"start": v(11.26, -37.5) * mm, "mid": v(12, -39.27) * mm, "end": v(13.76, -40) * mm});
            skArc(sketch, "E2212", {"start": v(13.76, -40) * mm, "mid": v(15.53, -39.27) * mm, "end": v(16.26, -37.5) * mm});
            skArc(sketch, "E2213", {"start": v(16.26, -37.5) * mm, "mid": v(15.53, -35.73) * mm, "end": v(13.76, -35) * mm});
            skArc(sketch, "E2214", {"start": v(13.76, -35) * mm, "mid": v(12, -35.73) * mm, "end": v(11.26, -37.5) * mm});
            skArc(sketch, "E2215", {"start": v(13.76, -36) * mm, "mid": v(12.7, -36.44) * mm, "end": v(12.26, -37.5) * mm});
            skArc(sketch, "E2216", {"start": v(12.26, -37.5) * mm, "mid": v(12.7, -38.56) * mm, "end": v(13.76, -39) * mm});
            skArc(sketch, "E2217", {"start": v(13.76, -39) * mm, "mid": v(14.82, -38.56) * mm, "end": v(15.26, -37.5) * mm});
            skArc(sketch, "E2218", {"start": v(15.26, -37.5) * mm, "mid": v(14.82, -36.44) * mm, "end": v(13.76, -36) * mm});
            skArc(sketch, "E2219", {"start": v(20.27, -36) * mm, "mid": v(19.2, -36.44) * mm, "end": v(18.77, -37.5) * mm});
            skArc(sketch, "E2220", {"start": v(18.77, -37.5) * mm, "mid": v(19.2, -38.56) * mm, "end": v(20.27, -39) * mm});
            skArc(sketch, "E2221", {"start": v(20.27, -39) * mm, "mid": v(21.33, -38.56) * mm, "end": v(21.77, -37.5) * mm});
            skArc(sketch, "E2222", {"start": v(21.77, -37.5) * mm, "mid": v(21.33, -36.44) * mm, "end": v(20.27, -36) * mm});
            skLineSegment(sketch, "E2223", {"start": v(16.73, -47.84) * mm, "end": v(16.6, -47.85) * mm});
            skLineSegment(sketch, "E2224", {"start": v(16.6, -47.85) * mm, "end": v(16.5, -47.87) * mm});
            skLineSegment(sketch, "E2225", {"start": v(16.5, -47.87) * mm, "end": v(16.28, -47.95) * mm});
            skLineSegment(sketch, "E2226", {"start": v(16.28, -47.95) * mm, "end": v(16.06, -48.05) * mm});
            skLineSegment(sketch, "E2227", {"start": v(16.06, -48.05) * mm, "end": v(15.85, -48.19) * mm});
            skLineSegment(sketch, "E2228", {"start": v(15.85, -48.19) * mm, "end": v(15.67, -48.34) * mm});
            skLineSegment(sketch, "E2229", {"start": v(15.67, -48.34) * mm, "end": v(15.47, -48.53) * mm});
            skLineSegment(sketch, "E2230", {"start": v(15.47, -48.53) * mm, "end": v(15.4, -48.65) * mm});
            skLineSegment(sketch, "E2231", {"start": v(15.4, -48.65) * mm, "end": v(15.4, -48.66) * mm});
            skLineSegment(sketch, "E2232", {"start": v(15.4, -48.66) * mm, "end": v(15.34, -48.76) * mm});
            skLineSegment(sketch, "E2233", {"start": v(15.34, -48.76) * mm, "end": v(15.24, -48.92) * mm});
            skLineSegment(sketch, "E2234", {"start": v(15.24, -48.92) * mm, "end": v(15.17, -49.1) * mm});
            skLineSegment(sketch, "E2235", {"start": v(15.17, -49.1) * mm, "end": v(15.09, -49.36) * mm});
            skLineSegment(sketch, "E2236", {"start": v(15.09, -49.36) * mm, "end": v(15.05, -49.45) * mm});
            skLineSegment(sketch, "E2237", {"start": v(15.05, -49.45) * mm, "end": v(15.05, -56.55) * mm});
            skLineSegment(sketch, "E2238", {"start": v(15.05, -56.55) * mm, "end": v(15.09, -56.64) * mm});
            skLineSegment(sketch, "E2239", {"start": v(15.09, -56.64) * mm, "end": v(15.16, -56.87) * mm});
            skLineSegment(sketch, "E2240", {"start": v(15.16, -56.87) * mm, "end": v(15.21, -57.02) * mm});
            skLineSegment(sketch, "E2241", {"start": v(15.21, -57.02) * mm, "end": v(15.26, -57.14) * mm});
            skLineSegment(sketch, "E2242", {"start": v(15.26, -57.14) * mm, "end": v(15.33, -57.24) * mm});
            skLineSegment(sketch, "E2243", {"start": v(15.33, -57.24) * mm, "end": v(15.4, -57.34) * mm});
            skLineSegment(sketch, "E2244", {"start": v(15.4, -57.34) * mm, "end": v(15.41, -57.35) * mm});
            skLineSegment(sketch, "E2245", {"start": v(15.41, -57.35) * mm, "end": v(15.42, -57.39) * mm});
            skLineSegment(sketch, "E2246", {"start": v(15.42, -57.39) * mm, "end": v(15.48, -57.47) * mm});
            skLineSegment(sketch, "E2247", {"start": v(15.48, -57.47) * mm, "end": v(15.58, -57.58) * mm});
            skLineSegment(sketch, "E2248", {"start": v(15.58, -57.58) * mm, "end": v(15.78, -57.77) * mm});
            skLineSegment(sketch, "E2249", {"start": v(15.78, -57.77) * mm, "end": v(15.87, -57.84) * mm});
            skLineSegment(sketch, "E2250", {"start": v(15.87, -57.84) * mm, "end": v(15.93, -57.87) * mm});
            skLineSegment(sketch, "E2251", {"start": v(15.93, -57.87) * mm, "end": v(15.96, -57.9) * mm});
            skLineSegment(sketch, "E2252", {"start": v(15.96, -57.9) * mm, "end": v(16.05, -57.94) * mm});
            skLineSegment(sketch, "E2253", {"start": v(16.05, -57.94) * mm, "end": v(16.34, -58.08) * mm});
            skLineSegment(sketch, "E2254", {"start": v(16.34, -58.08) * mm, "end": v(16.49, -58.13) * mm});
            skLineSegment(sketch, "E2255", {"start": v(16.49, -58.13) * mm, "end": v(16.65, -58.17) * mm});
            skLineSegment(sketch, "E2256", {"start": v(16.65, -58.17) * mm, "end": v(16.83, -58.19) * mm});
            skLineSegment(sketch, "E2257", {"start": v(16.83, -58.19) * mm, "end": v(17, -58.2) * mm});
            skLineSegment(sketch, "E2258", {"start": v(17, -58.2) * mm, "end": v(17.19, -58.19) * mm});
            skLineSegment(sketch, "E2259", {"start": v(17.19, -58.19) * mm, "end": v(17.36, -58.17) * mm});
            skLineSegment(sketch, "E2260", {"start": v(17.36, -58.17) * mm, "end": v(17.53, -58.13) * mm});
            skLineSegment(sketch, "E2261", {"start": v(17.53, -58.13) * mm, "end": v(17.68, -58.08) * mm});
            skLineSegment(sketch, "E2262", {"start": v(17.68, -58.08) * mm, "end": v(17.98, -57.95) * mm});
            skLineSegment(sketch, "E2263", {"start": v(17.98, -57.95) * mm, "end": v(18.08, -57.9) * mm});
            skLineSegment(sketch, "E2264", {"start": v(18.08, -57.9) * mm, "end": v(18.11, -57.86) * mm});
            skLineSegment(sketch, "E2265", {"start": v(18.11, -57.86) * mm, "end": v(18.14, -57.85) * mm});
            skLineSegment(sketch, "E2266", {"start": v(18.14, -57.85) * mm, "end": v(18.22, -57.79) * mm});
            skLineSegment(sketch, "E2267", {"start": v(18.22, -57.79) * mm, "end": v(18.37, -57.65) * mm});
            skLineSegment(sketch, "E2268", {"start": v(18.37, -57.65) * mm, "end": v(18.52, -57.51) * mm});
            skLineSegment(sketch, "E2269", {"start": v(18.52, -57.51) * mm, "end": v(18.58, -57.44) * mm});
            skLineSegment(sketch, "E2270", {"start": v(18.58, -57.44) * mm, "end": v(18.6, -57.37) * mm});
            skLineSegment(sketch, "E2271", {"start": v(18.6, -57.37) * mm, "end": v(18.62, -57.35) * mm});
            skLineSegment(sketch, "E2272", {"start": v(18.62, -57.35) * mm, "end": v(18.62, -57.34) * mm});
            skLineSegment(sketch, "E2273", {"start": v(18.62, -57.34) * mm, "end": v(18.69, -57.26) * mm});
            skLineSegment(sketch, "E2274", {"start": v(18.69, -57.26) * mm, "end": v(18.75, -57.18) * mm});
            skLineSegment(sketch, "E2275", {"start": v(18.75, -57.18) * mm, "end": v(18.8, -57.06) * mm});
            skLineSegment(sketch, "E2276", {"start": v(18.8, -57.06) * mm, "end": v(18.94, -56.65) * mm});
            skLineSegment(sketch, "E2277", {"start": v(18.94, -56.65) * mm, "end": v(18.98, -56.51) * mm});
            skLineSegment(sketch, "E2278", {"start": v(18.98, -56.51) * mm, "end": v(18.98, -49.45) * mm});
            skLineSegment(sketch, "E2279", {"start": v(18.98, -49.45) * mm, "end": v(18.94, -49.36) * mm});
            skLineSegment(sketch, "E2280", {"start": v(18.94, -49.36) * mm, "end": v(18.86, -49.1) * mm});
            skLineSegment(sketch, "E2281", {"start": v(18.86, -49.1) * mm, "end": v(18.79, -48.92) * mm});
            skLineSegment(sketch, "E2282", {"start": v(18.79, -48.92) * mm, "end": v(18.7, -48.76) * mm});
            skLineSegment(sketch, "E2283", {"start": v(18.7, -48.76) * mm, "end": v(18.63, -48.66) * mm});
            skLineSegment(sketch, "E2284", {"start": v(18.63, -48.66) * mm, "end": v(18.6, -48.6) * mm});
            skLineSegment(sketch, "E2285", {"start": v(18.6, -48.6) * mm, "end": v(18.55, -48.53) * mm});
            skLineSegment(sketch, "E2286", {"start": v(18.55, -48.53) * mm, "end": v(18.46, -48.44) * mm});
            skLineSegment(sketch, "E2287", {"start": v(18.46, -48.44) * mm, "end": v(18.2, -48.2) * mm});
            skLineSegment(sketch, "E2288", {"start": v(18.2, -48.2) * mm, "end": v(18.06, -48.1) * mm});
            skLineSegment(sketch, "E2289", {"start": v(18.06, -48.1) * mm, "end": v(17.89, -48.01) * mm});
            skLineSegment(sketch, "E2290", {"start": v(17.89, -48.01) * mm, "end": v(17.7, -47.93) * mm});
            skLineSegment(sketch, "E2291", {"start": v(17.7, -47.93) * mm, "end": v(17.53, -47.87) * mm});
            skLineSegment(sketch, "E2292", {"start": v(17.53, -47.87) * mm, "end": v(17.42, -47.85) * mm});
            skLineSegment(sketch, "E2293", {"start": v(17.42, -47.85) * mm, "end": v(17.3, -47.84) * mm});
            skLineSegment(sketch, "E2294", {"start": v(17.3, -47.84) * mm, "end": v(17.02, -47.83) * mm});
            skLineSegment(sketch, "E2295", {"start": v(17.02, -47.83) * mm, "end": v(16.73, -47.84) * mm});
            skLineSegment(sketch, "E2296", {"start": v(7.5, -48.73) * mm, "end": v(9.5, -48.73) * mm});
            skLineSegment(sketch, "E2297", {"start": v(9.5, -48.73) * mm, "end": v(9.5, -45.73) * mm});
            skLineSegment(sketch, "E2298", {"start": v(9.5, -45.73) * mm, "end": v(7.5, -45.73) * mm});
            skLineSegment(sketch, "E2299", {"start": v(7.5, -45.73) * mm, "end": v(7.5, -48.73) * mm});
            skLineSegment(sketch, "E2300", {"start": v(26.5, -41.33) * mm, "end": v(41.5, -41.33) * mm});
            skLineSegment(sketch, "E2301", {"start": v(41.5, -41.33) * mm, "end": v(41.5, -32.48) * mm});
            skLineSegment(sketch, "E2302", {"start": v(41.5, -32.48) * mm, "end": v(26.5, -32.48) * mm});
            skLineSegment(sketch, "E2303", {"start": v(26.5, -32.48) * mm, "end": v(26.5, -41.33) * mm});
            skArc(sketch, "E2304", {"start": v(34.76, -37.5) * mm, "mid": v(35.5, -39.27) * mm, "end": v(37.26, -40) * mm});
            skArc(sketch, "E2305", {"start": v(37.26, -40) * mm, "mid": v(39.03, -39.27) * mm, "end": v(39.76, -37.5) * mm});
            skArc(sketch, "E2306", {"start": v(39.76, -37.5) * mm, "mid": v(39.03, -35.73) * mm, "end": v(37.26, -35) * mm});
            skArc(sketch, "E2307", {"start": v(37.26, -35) * mm, "mid": v(35.5, -35.73) * mm, "end": v(34.76, -37.5) * mm});
            skLineSegment(sketch, "E2308", {"start": v(26.5, -32.48) * mm, "end": v(26.5, -55.97) * mm});
            skArc(sketch, "E2309", {"start": v(26.5, -55.97) * mm, "mid": v(28.26, -60.21) * mm, "end": v(32.5, -61.97) * mm});
            skLineSegment(sketch, "E2310", {"start": v(32.5, -61.97) * mm, "end": v(35.5, -61.97) * mm});
            skArc(sketch, "E2311", {"start": v(35.5, -61.97) * mm, "mid": v(39.74, -60.21) * mm, "end": v(41.5, -55.97) * mm});
            skLineSegment(sketch, "E2312", {"start": v(41.5, -55.97) * mm, "end": v(41.5, -32.48) * mm});
            skArc(sketch, "E2313", {"start": v(28.26, -37.5) * mm, "mid": v(29, -39.27) * mm, "end": v(30.76, -40) * mm});
            skArc(sketch, "E2314", {"start": v(30.76, -40) * mm, "mid": v(32.53, -39.27) * mm, "end": v(33.26, -37.5) * mm});
            skArc(sketch, "E2315", {"start": v(33.26, -37.5) * mm, "mid": v(32.53, -35.73) * mm, "end": v(30.76, -35) * mm});
            skArc(sketch, "E2316", {"start": v(30.76, -35) * mm, "mid": v(29, -35.73) * mm, "end": v(28.26, -37.5) * mm});
            skArc(sketch, "E2317", {"start": v(30.76, -36) * mm, "mid": v(29.7, -36.44) * mm, "end": v(29.26, -37.5) * mm});
            skArc(sketch, "E2318", {"start": v(29.26, -37.5) * mm, "mid": v(29.7, -38.56) * mm, "end": v(30.76, -39) * mm});
            skArc(sketch, "E2319", {"start": v(30.76, -39) * mm, "mid": v(31.82, -38.56) * mm, "end": v(32.26, -37.5) * mm});
            skArc(sketch, "E2320", {"start": v(32.26, -37.5) * mm, "mid": v(31.82, -36.44) * mm, "end": v(30.76, -36) * mm});
            skArc(sketch, "E2321", {"start": v(37.27, -36) * mm, "mid": v(36.2, -36.44) * mm, "end": v(35.77, -37.5) * mm});
            skArc(sketch, "E2322", {"start": v(35.77, -37.5) * mm, "mid": v(36.2, -38.56) * mm, "end": v(37.27, -39) * mm});
            skArc(sketch, "E2323", {"start": v(37.27, -39) * mm, "mid": v(38.33, -38.56) * mm, "end": v(38.77, -37.5) * mm});
            skArc(sketch, "E2324", {"start": v(38.77, -37.5) * mm, "mid": v(38.33, -36.44) * mm, "end": v(37.27, -36) * mm});
            skLineSegment(sketch, "E2325", {"start": v(33.73, -47.84) * mm, "end": v(33.6, -47.85) * mm});
            skLineSegment(sketch, "E2326", {"start": v(33.6, -47.85) * mm, "end": v(33.5, -47.87) * mm});
            skLineSegment(sketch, "E2327", {"start": v(33.5, -47.87) * mm, "end": v(33.28, -47.95) * mm});
            skLineSegment(sketch, "E2328", {"start": v(33.28, -47.95) * mm, "end": v(33.06, -48.05) * mm});
            skLineSegment(sketch, "E2329", {"start": v(33.06, -48.05) * mm, "end": v(32.85, -48.19) * mm});
            skLineSegment(sketch, "E2330", {"start": v(32.85, -48.19) * mm, "end": v(32.67, -48.34) * mm});
            skLineSegment(sketch, "E2331", {"start": v(32.67, -48.34) * mm, "end": v(32.47, -48.53) * mm});
            skLineSegment(sketch, "E2332", {"start": v(32.47, -48.53) * mm, "end": v(32.4, -48.65) * mm});
            skLineSegment(sketch, "E2333", {"start": v(32.4, -48.65) * mm, "end": v(32.4, -48.66) * mm});
            skLineSegment(sketch, "E2334", {"start": v(32.4, -48.66) * mm, "end": v(32.34, -48.76) * mm});
            skLineSegment(sketch, "E2335", {"start": v(32.34, -48.76) * mm, "end": v(32.24, -48.92) * mm});
            skLineSegment(sketch, "E2336", {"start": v(32.24, -48.92) * mm, "end": v(32.17, -49.1) * mm});
            skLineSegment(sketch, "E2337", {"start": v(32.17, -49.1) * mm, "end": v(32.09, -49.36) * mm});
            skLineSegment(sketch, "E2338", {"start": v(32.09, -49.36) * mm, "end": v(32.05, -49.45) * mm});
            skLineSegment(sketch, "E2339", {"start": v(32.05, -49.45) * mm, "end": v(32.05, -56.55) * mm});
            skLineSegment(sketch, "E2340", {"start": v(32.05, -56.55) * mm, "end": v(32.09, -56.64) * mm});
            skLineSegment(sketch, "E2341", {"start": v(32.09, -56.64) * mm, "end": v(32.16, -56.87) * mm});
            skLineSegment(sketch, "E2342", {"start": v(32.16, -56.87) * mm, "end": v(32.21, -57.02) * mm});
            skLineSegment(sketch, "E2343", {"start": v(32.21, -57.02) * mm, "end": v(32.26, -57.14) * mm});
            skLineSegment(sketch, "E2344", {"start": v(32.26, -57.14) * mm, "end": v(32.33, -57.24) * mm});
            skLineSegment(sketch, "E2345", {"start": v(32.33, -57.24) * mm, "end": v(32.4, -57.34) * mm});
            skLineSegment(sketch, "E2346", {"start": v(32.4, -57.34) * mm, "end": v(32.41, -57.35) * mm});
            skLineSegment(sketch, "E2347", {"start": v(32.41, -57.35) * mm, "end": v(32.42, -57.39) * mm});
            skLineSegment(sketch, "E2348", {"start": v(32.42, -57.39) * mm, "end": v(32.48, -57.47) * mm});
            skLineSegment(sketch, "E2349", {"start": v(32.48, -57.47) * mm, "end": v(32.58, -57.58) * mm});
            skLineSegment(sketch, "E2350", {"start": v(32.58, -57.58) * mm, "end": v(32.78, -57.77) * mm});
            skLineSegment(sketch, "E2351", {"start": v(32.78, -57.77) * mm, "end": v(32.87, -57.84) * mm});
            skLineSegment(sketch, "E2352", {"start": v(32.87, -57.84) * mm, "end": v(32.93, -57.87) * mm});
            skLineSegment(sketch, "E2353", {"start": v(32.93, -57.87) * mm, "end": v(32.96, -57.9) * mm});
            skLineSegment(sketch, "E2354", {"start": v(32.96, -57.9) * mm, "end": v(33.05, -57.94) * mm});
            skLineSegment(sketch, "E2355", {"start": v(33.05, -57.94) * mm, "end": v(33.34, -58.08) * mm});
            skLineSegment(sketch, "E2356", {"start": v(33.34, -58.08) * mm, "end": v(33.49, -58.13) * mm});
            skLineSegment(sketch, "E2357", {"start": v(33.49, -58.13) * mm, "end": v(33.65, -58.17) * mm});
            skLineSegment(sketch, "E2358", {"start": v(33.65, -58.17) * mm, "end": v(33.83, -58.19) * mm});
            skLineSegment(sketch, "E2359", {"start": v(33.83, -58.19) * mm, "end": v(34, -58.2) * mm});
            skLineSegment(sketch, "E2360", {"start": v(34, -58.2) * mm, "end": v(34.19, -58.19) * mm});
            skLineSegment(sketch, "E2361", {"start": v(34.19, -58.19) * mm, "end": v(34.36, -58.17) * mm});
            skLineSegment(sketch, "E2362", {"start": v(34.36, -58.17) * mm, "end": v(34.53, -58.13) * mm});
            skLineSegment(sketch, "E2363", {"start": v(34.53, -58.13) * mm, "end": v(34.68, -58.08) * mm});
            skLineSegment(sketch, "E2364", {"start": v(34.68, -58.08) * mm, "end": v(34.98, -57.95) * mm});
            skLineSegment(sketch, "E2365", {"start": v(34.98, -57.95) * mm, "end": v(35.08, -57.9) * mm});
            skLineSegment(sketch, "E2366", {"start": v(35.08, -57.9) * mm, "end": v(35.11, -57.86) * mm});
            skLineSegment(sketch, "E2367", {"start": v(35.11, -57.86) * mm, "end": v(35.14, -57.85) * mm});
            skLineSegment(sketch, "E2368", {"start": v(35.14, -57.85) * mm, "end": v(35.22, -57.79) * mm});
            skLineSegment(sketch, "E2369", {"start": v(35.22, -57.79) * mm, "end": v(35.37, -57.65) * mm});
            skLineSegment(sketch, "E2370", {"start": v(35.37, -57.65) * mm, "end": v(35.52, -57.51) * mm});
            skLineSegment(sketch, "E2371", {"start": v(35.52, -57.51) * mm, "end": v(35.58, -57.44) * mm});
            skLineSegment(sketch, "E2372", {"start": v(35.58, -57.44) * mm, "end": v(35.6, -57.37) * mm});
            skLineSegment(sketch, "E2373", {"start": v(35.6, -57.37) * mm, "end": v(35.62, -57.35) * mm});
            skLineSegment(sketch, "E2374", {"start": v(35.62, -57.35) * mm, "end": v(35.62, -57.34) * mm});
            skLineSegment(sketch, "E2375", {"start": v(35.62, -57.34) * mm, "end": v(35.69, -57.26) * mm});
            skLineSegment(sketch, "E2376", {"start": v(35.69, -57.26) * mm, "end": v(35.75, -57.18) * mm});
            skLineSegment(sketch, "E2377", {"start": v(35.75, -57.18) * mm, "end": v(35.8, -57.06) * mm});
            skLineSegment(sketch, "E2378", {"start": v(35.8, -57.06) * mm, "end": v(35.94, -56.65) * mm});
            skLineSegment(sketch, "E2379", {"start": v(35.94, -56.65) * mm, "end": v(35.98, -56.51) * mm});
            skLineSegment(sketch, "E2380", {"start": v(35.98, -56.51) * mm, "end": v(35.98, -49.45) * mm});
            skLineSegment(sketch, "E2381", {"start": v(35.98, -49.45) * mm, "end": v(35.94, -49.36) * mm});
            skLineSegment(sketch, "E2382", {"start": v(35.94, -49.36) * mm, "end": v(35.86, -49.1) * mm});
            skLineSegment(sketch, "E2383", {"start": v(35.86, -49.1) * mm, "end": v(35.79, -48.92) * mm});
            skLineSegment(sketch, "E2384", {"start": v(35.79, -48.92) * mm, "end": v(35.7, -48.76) * mm});
            skLineSegment(sketch, "E2385", {"start": v(35.7, -48.76) * mm, "end": v(35.63, -48.66) * mm});
            skLineSegment(sketch, "E2386", {"start": v(35.63, -48.66) * mm, "end": v(35.6, -48.6) * mm});
            skLineSegment(sketch, "E2387", {"start": v(35.6, -48.6) * mm, "end": v(35.55, -48.53) * mm});
            skLineSegment(sketch, "E2388", {"start": v(35.55, -48.53) * mm, "end": v(35.46, -48.44) * mm});
            skLineSegment(sketch, "E2389", {"start": v(35.46, -48.44) * mm, "end": v(35.2, -48.2) * mm});
            skLineSegment(sketch, "E2390", {"start": v(35.2, -48.2) * mm, "end": v(35.06, -48.1) * mm});
            skLineSegment(sketch, "E2391", {"start": v(35.06, -48.1) * mm, "end": v(34.89, -48.01) * mm});
            skLineSegment(sketch, "E2392", {"start": v(34.89, -48.01) * mm, "end": v(34.7, -47.93) * mm});
            skLineSegment(sketch, "E2393", {"start": v(34.7, -47.93) * mm, "end": v(34.53, -47.87) * mm});
            skLineSegment(sketch, "E2394", {"start": v(34.53, -47.87) * mm, "end": v(34.42, -47.85) * mm});
            skLineSegment(sketch, "E2395", {"start": v(34.42, -47.85) * mm, "end": v(34.3, -47.84) * mm});
            skLineSegment(sketch, "E2396", {"start": v(34.3, -47.84) * mm, "end": v(34.02, -47.83) * mm});
            skLineSegment(sketch, "E2397", {"start": v(34.02, -47.83) * mm, "end": v(33.73, -47.84) * mm});
            skLineSegment(sketch, "E2398", {"start": v(24.5, -48.73) * mm, "end": v(26.5, -48.73) * mm});
            skLineSegment(sketch, "E2399", {"start": v(26.5, -48.73) * mm, "end": v(26.5, -45.73) * mm});
            skLineSegment(sketch, "E2400", {"start": v(26.5, -45.73) * mm, "end": v(24.5, -45.73) * mm});
            skLineSegment(sketch, "E2401", {"start": v(24.5, -45.73) * mm, "end": v(24.5, -48.73) * mm});
            skLineSegment(sketch, "E2402", {"start": v(-7.5, -41.33) * mm, "end": v(7.5, -41.33) * mm});
            skLineSegment(sketch, "E2403", {"start": v(7.5, -41.33) * mm, "end": v(7.5, -32.48) * mm});
            skLineSegment(sketch, "E2404", {"start": v(7.5, -32.48) * mm, "end": v(-7.5, -32.48) * mm});
            skLineSegment(sketch, "E2405", {"start": v(-7.5, -32.48) * mm, "end": v(-7.5, -41.33) * mm});
            skArc(sketch, "E2406", {"start": v(0.76, -37.5) * mm, "mid": v(1.5, -39.27) * mm, "end": v(3.26, -40) * mm});
            skArc(sketch, "E2407", {"start": v(3.26, -40) * mm, "mid": v(5.03, -39.27) * mm, "end": v(5.76, -37.5) * mm});
            skArc(sketch, "E2408", {"start": v(5.76, -37.5) * mm, "mid": v(5.03, -35.73) * mm, "end": v(3.26, -35) * mm});
            skArc(sketch, "E2409", {"start": v(3.26, -35) * mm, "mid": v(1.5, -35.73) * mm, "end": v(0.76, -37.5) * mm});
            skLineSegment(sketch, "E2410", {"start": v(-7.5, -32.48) * mm, "end": v(-7.5, -55.97) * mm});
            skArc(sketch, "E2411", {"start": v(-7.5, -55.97) * mm, "mid": v(-5.74, -60.21) * mm, "end": v(-1.5, -61.97) * mm});
            skLineSegment(sketch, "E2412", {"start": v(-1.5, -61.97) * mm, "end": v(1.5, -61.97) * mm});
            skArc(sketch, "E2413", {"start": v(1.5, -61.97) * mm, "mid": v(5.74, -60.21) * mm, "end": v(7.5, -55.97) * mm});
            skLineSegment(sketch, "E2414", {"start": v(7.5, -55.97) * mm, "end": v(7.5, -32.48) * mm});
            skArc(sketch, "E2415", {"start": v(-5.74, -37.5) * mm, "mid": v(-5, -39.27) * mm, "end": v(-3.24, -40) * mm});
            skArc(sketch, "E2416", {"start": v(-3.24, -40) * mm, "mid": v(-1.47, -39.27) * mm, "end": v(-0.74, -37.5) * mm});
            skArc(sketch, "E2417", {"start": v(-0.74, -37.5) * mm, "mid": v(-1.47, -35.73) * mm, "end": v(-3.24, -35) * mm});
            skArc(sketch, "E2418", {"start": v(-3.24, -35) * mm, "mid": v(-5, -35.73) * mm, "end": v(-5.74, -37.5) * mm});
            skArc(sketch, "E2419", {"start": v(-3.24, -36) * mm, "mid": v(-4.3, -36.44) * mm, "end": v(-4.74, -37.5) * mm});
            skArc(sketch, "E2420", {"start": v(-4.74, -37.5) * mm, "mid": v(-4.3, -38.56) * mm, "end": v(-3.24, -39) * mm});
            skArc(sketch, "E2421", {"start": v(-3.24, -39) * mm, "mid": v(-2.18, -38.56) * mm, "end": v(-1.74, -37.5) * mm});
            skArc(sketch, "E2422", {"start": v(-1.74, -37.5) * mm, "mid": v(-2.18, -36.44) * mm, "end": v(-3.24, -36) * mm});
            skArc(sketch, "E2423", {"start": v(3.26, -36) * mm, "mid": v(2.2, -36.44) * mm, "end": v(1.76, -37.5) * mm});
            skArc(sketch, "E2424", {"start": v(1.76, -37.5) * mm, "mid": v(2.2, -38.56) * mm, "end": v(3.26, -39) * mm});
            skArc(sketch, "E2425", {"start": v(3.26, -39) * mm, "mid": v(4.33, -38.56) * mm, "end": v(4.76, -37.5) * mm});
            skArc(sketch, "E2426", {"start": v(4.76, -37.5) * mm, "mid": v(4.33, -36.44) * mm, "end": v(3.26, -36) * mm});
            skLineSegment(sketch, "E2427", {"start": v(-0.27, -47.84) * mm, "end": v(-0.4, -47.85) * mm});
            skLineSegment(sketch, "E2428", {"start": v(-0.4, -47.85) * mm, "end": v(-0.5, -47.87) * mm});
            skLineSegment(sketch, "E2429", {"start": v(-0.5, -47.87) * mm, "end": v(-0.72, -47.95) * mm});
            skLineSegment(sketch, "E2430", {"start": v(-0.72, -47.95) * mm, "end": v(-0.94, -48.05) * mm});
            skLineSegment(sketch, "E2431", {"start": v(-0.94, -48.05) * mm, "end": v(-1.15, -48.19) * mm});
            skLineSegment(sketch, "E2432", {"start": v(-1.15, -48.19) * mm, "end": v(-1.33, -48.34) * mm});
            skLineSegment(sketch, "E2433", {"start": v(-1.33, -48.34) * mm, "end": v(-1.53, -48.53) * mm});
            skLineSegment(sketch, "E2434", {"start": v(-1.53, -48.53) * mm, "end": v(-1.6, -48.65) * mm});
            skLineSegment(sketch, "E2435", {"start": v(-1.6, -48.65) * mm, "end": v(-1.6, -48.66) * mm});
            skLineSegment(sketch, "E2436", {"start": v(-1.6, -48.66) * mm, "end": v(-1.66, -48.76) * mm});
            skLineSegment(sketch, "E2437", {"start": v(-1.66, -48.76) * mm, "end": v(-1.76, -48.92) * mm});
            skLineSegment(sketch, "E2438", {"start": v(-1.76, -48.92) * mm, "end": v(-1.83, -49.1) * mm});
            skLineSegment(sketch, "E2439", {"start": v(-1.83, -49.1) * mm, "end": v(-1.91, -49.36) * mm});
            skLineSegment(sketch, "E2440", {"start": v(-1.91, -49.36) * mm, "end": v(-1.95, -49.45) * mm});
            skLineSegment(sketch, "E2441", {"start": v(-1.95, -49.45) * mm, "end": v(-1.95, -56.55) * mm});
            skLineSegment(sketch, "E2442", {"start": v(-1.95, -56.55) * mm, "end": v(-1.91, -56.64) * mm});
            skLineSegment(sketch, "E2443", {"start": v(-1.91, -56.64) * mm, "end": v(-1.84, -56.87) * mm});
            skLineSegment(sketch, "E2444", {"start": v(-1.84, -56.87) * mm, "end": v(-1.79, -57.02) * mm});
            skLineSegment(sketch, "E2445", {"start": v(-1.79, -57.02) * mm, "end": v(-1.74, -57.14) * mm});
            skLineSegment(sketch, "E2446", {"start": v(-1.74, -57.14) * mm, "end": v(-1.67, -57.24) * mm});
            skLineSegment(sketch, "E2447", {"start": v(-1.67, -57.24) * mm, "end": v(-1.6, -57.34) * mm});
            skLineSegment(sketch, "E2448", {"start": v(-1.6, -57.34) * mm, "end": v(-1.59, -57.35) * mm});
            skLineSegment(sketch, "E2449", {"start": v(-1.59, -57.35) * mm, "end": v(-1.58, -57.39) * mm});
            skLineSegment(sketch, "E2450", {"start": v(-1.58, -57.39) * mm, "end": v(-1.52, -57.47) * mm});
            skLineSegment(sketch, "E2451", {"start": v(-1.52, -57.47) * mm, "end": v(-1.42, -57.58) * mm});
            skLineSegment(sketch, "E2452", {"start": v(-1.42, -57.58) * mm, "end": v(-1.22, -57.77) * mm});
            skLineSegment(sketch, "E2453", {"start": v(-1.22, -57.77) * mm, "end": v(-1.13, -57.84) * mm});
            skLineSegment(sketch, "E2454", {"start": v(-1.13, -57.84) * mm, "end": v(-1.07, -57.87) * mm});
            skLineSegment(sketch, "E2455", {"start": v(-1.07, -57.87) * mm, "end": v(-1.04, -57.9) * mm});
            skLineSegment(sketch, "E2456", {"start": v(-1.04, -57.9) * mm, "end": v(-0.95, -57.94) * mm});
            skLineSegment(sketch, "E2457", {"start": v(-0.95, -57.94) * mm, "end": v(-0.66, -58.08) * mm});
            skLineSegment(sketch, "E2458", {"start": v(-0.66, -58.08) * mm, "end": v(-0.51, -58.13) * mm});
            skLineSegment(sketch, "E2459", {"start": v(-0.51, -58.13) * mm, "end": v(-0.35, -58.17) * mm});
            skLineSegment(sketch, "E2460", {"start": v(-0.35, -58.17) * mm, "end": v(-0.17, -58.19) * mm});
            skLineSegment(sketch, "E2461", {"start": v(-0.17, -58.19) * mm, "end": v(0, -58.2) * mm});
            skLineSegment(sketch, "E2462", {"start": v(0, -58.2) * mm, "end": v(0.19, -58.19) * mm});
            skLineSegment(sketch, "E2463", {"start": v(0.19, -58.19) * mm, "end": v(0.36, -58.17) * mm});
            skLineSegment(sketch, "E2464", {"start": v(0.36, -58.17) * mm, "end": v(0.53, -58.13) * mm});
            skLineSegment(sketch, "E2465", {"start": v(0.53, -58.13) * mm, "end": v(0.68, -58.08) * mm});
            skLineSegment(sketch, "E2466", {"start": v(0.68, -58.08) * mm, "end": v(0.98, -57.95) * mm});
            skLineSegment(sketch, "E2467", {"start": v(0.98, -57.95) * mm, "end": v(1.08, -57.9) * mm});
            skLineSegment(sketch, "E2468", {"start": v(1.08, -57.9) * mm, "end": v(1.11, -57.86) * mm});
            skLineSegment(sketch, "E2469", {"start": v(1.11, -57.86) * mm, "end": v(1.14, -57.85) * mm});
            skLineSegment(sketch, "E2470", {"start": v(1.14, -57.85) * mm, "end": v(1.22, -57.79) * mm});
            skLineSegment(sketch, "E2471", {"start": v(1.22, -57.79) * mm, "end": v(1.37, -57.65) * mm});
            skLineSegment(sketch, "E2472", {"start": v(1.37, -57.65) * mm, "end": v(1.52, -57.51) * mm});
            skLineSegment(sketch, "E2473", {"start": v(1.52, -57.51) * mm, "end": v(1.58, -57.44) * mm});
            skLineSegment(sketch, "E2474", {"start": v(1.58, -57.44) * mm, "end": v(1.6, -57.37) * mm});
            skLineSegment(sketch, "E2475", {"start": v(1.6, -57.37) * mm, "end": v(1.62, -57.35) * mm});
            skLineSegment(sketch, "E2476", {"start": v(1.62, -57.35) * mm, "end": v(1.62, -57.34) * mm});
            skLineSegment(sketch, "E2477", {"start": v(1.62, -57.34) * mm, "end": v(1.69, -57.26) * mm});
            skLineSegment(sketch, "E2478", {"start": v(1.69, -57.26) * mm, "end": v(1.75, -57.18) * mm});
            skLineSegment(sketch, "E2479", {"start": v(1.75, -57.18) * mm, "end": v(1.8, -57.06) * mm});
            skLineSegment(sketch, "E2480", {"start": v(1.8, -57.06) * mm, "end": v(1.94, -56.65) * mm});
            skLineSegment(sketch, "E2481", {"start": v(1.94, -56.65) * mm, "end": v(1.98, -56.51) * mm});
            skLineSegment(sketch, "E2482", {"start": v(1.98, -56.51) * mm, "end": v(1.98, -49.45) * mm});
            skLineSegment(sketch, "E2483", {"start": v(1.98, -49.45) * mm, "end": v(1.94, -49.36) * mm});
            skLineSegment(sketch, "E2484", {"start": v(1.94, -49.36) * mm, "end": v(1.86, -49.1) * mm});
            skLineSegment(sketch, "E2485", {"start": v(1.86, -49.1) * mm, "end": v(1.79, -48.92) * mm});
            skLineSegment(sketch, "E2486", {"start": v(1.79, -48.92) * mm, "end": v(1.7, -48.76) * mm});
            skLineSegment(sketch, "E2487", {"start": v(1.7, -48.76) * mm, "end": v(1.63, -48.66) * mm});
            skLineSegment(sketch, "E2488", {"start": v(1.63, -48.66) * mm, "end": v(1.6, -48.6) * mm});
            skLineSegment(sketch, "E2489", {"start": v(1.6, -48.6) * mm, "end": v(1.55, -48.53) * mm});
            skLineSegment(sketch, "E2490", {"start": v(1.55, -48.53) * mm, "end": v(1.46, -48.44) * mm});
            skLineSegment(sketch, "E2491", {"start": v(1.46, -48.44) * mm, "end": v(1.2, -48.2) * mm});
            skLineSegment(sketch, "E2492", {"start": v(1.2, -48.2) * mm, "end": v(1.06, -48.1) * mm});
            skLineSegment(sketch, "E2493", {"start": v(1.06, -48.1) * mm, "end": v(0.89, -48.01) * mm});
            skLineSegment(sketch, "E2494", {"start": v(0.89, -48.01) * mm, "end": v(0.7, -47.93) * mm});
            skLineSegment(sketch, "E2495", {"start": v(0.7, -47.93) * mm, "end": v(0.53, -47.87) * mm});
            skLineSegment(sketch, "E2496", {"start": v(0.53, -47.87) * mm, "end": v(0.42, -47.85) * mm});
            skLineSegment(sketch, "E2497", {"start": v(0.42, -47.85) * mm, "end": v(0.3, -47.84) * mm});
            skLineSegment(sketch, "E2498", {"start": v(0.3, -47.84) * mm, "end": v(0.02, -47.83) * mm});
            skLineSegment(sketch, "E2499", {"start": v(0.02, -47.83) * mm, "end": v(-0.27, -47.84) * mm});
            skLineSegment(sketch, "E2500", {"start": v(-9.5, -48.73) * mm, "end": v(-7.5, -48.73) * mm});
            skLineSegment(sketch, "E2501", {"start": v(-7.5, -48.73) * mm, "end": v(-7.5, -45.73) * mm});
            skLineSegment(sketch, "E2502", {"start": v(-7.5, -45.73) * mm, "end": v(-9.5, -45.73) * mm});
            skLineSegment(sketch, "E2503", {"start": v(-9.5, -45.73) * mm, "end": v(-9.5, -48.73) * mm});
            skLineSegment(sketch, "E2504", {"start": v(49.5, 30.48) * mm, "end": v(52.5, 30.48) * mm});
            skLineSegment(sketch, "E2505", {"start": v(52.5, 30.48) * mm, "end": v(52.5, 32.48) * mm});
            skLineSegment(sketch, "E2506", {"start": v(52.5, 32.48) * mm, "end": v(49.5, 32.48) * mm});
            skLineSegment(sketch, "E2507", {"start": v(49.5, 32.48) * mm, "end": v(49.5, 30.48) * mm});
            skLineSegment(sketch, "E2508", {"start": v(43.5, 53.13) * mm, "end": v(58.5, 53.13) * mm});
            skLineSegment(sketch, "E2509", {"start": v(58.5, 53.13) * mm, "end": v(58.5, 61.97) * mm});
            skLineSegment(sketch, "E2510", {"start": v(58.5, 61.97) * mm, "end": v(43.5, 61.97) * mm});
            skLineSegment(sketch, "E2511", {"start": v(43.5, 61.97) * mm, "end": v(43.5, 53.13) * mm});
            skArc(sketch, "E2512", {"start": v(51.76, 56.95) * mm, "mid": v(52.5, 55.18) * mm, "end": v(54.26, 54.45) * mm});
            skArc(sketch, "E2513", {"start": v(54.26, 54.45) * mm, "mid": v(56.03, 55.18) * mm, "end": v(56.76, 56.95) * mm});
            skArc(sketch, "E2514", {"start": v(56.76, 56.95) * mm, "mid": v(56.03, 58.72) * mm, "end": v(54.26, 59.45) * mm});
            skArc(sketch, "E2515", {"start": v(54.26, 59.45) * mm, "mid": v(52.5, 58.72) * mm, "end": v(51.76, 56.95) * mm});
            skLineSegment(sketch, "E2516", {"start": v(43.5, 61.97) * mm, "end": v(43.5, 38.48) * mm});
            skArc(sketch, "E2517", {"start": v(43.5, 38.48) * mm, "mid": v(45.26, 34.24) * mm, "end": v(49.5, 32.48) * mm});
            skLineSegment(sketch, "E2518", {"start": v(49.5, 32.48) * mm, "end": v(52.5, 32.48) * mm});
            skArc(sketch, "E2519", {"start": v(52.5, 32.48) * mm, "mid": v(56.74, 34.24) * mm, "end": v(58.5, 38.48) * mm});
            skLineSegment(sketch, "E2520", {"start": v(58.5, 38.48) * mm, "end": v(58.5, 61.97) * mm});
            skArc(sketch, "E2521", {"start": v(45.26, 56.95) * mm, "mid": v(46, 55.18) * mm, "end": v(47.76, 54.45) * mm});
            skArc(sketch, "E2522", {"start": v(47.76, 54.45) * mm, "mid": v(49.53, 55.18) * mm, "end": v(50.26, 56.95) * mm});
            skArc(sketch, "E2523", {"start": v(50.26, 56.95) * mm, "mid": v(49.53, 58.72) * mm, "end": v(47.76, 59.45) * mm});
            skArc(sketch, "E2524", {"start": v(47.76, 59.45) * mm, "mid": v(46, 58.72) * mm, "end": v(45.26, 56.95) * mm});
            skArc(sketch, "E2525", {"start": v(47.76, 58.45) * mm, "mid": v(46.7, 58.01) * mm, "end": v(46.26, 56.95) * mm});
            skArc(sketch, "E2526", {"start": v(46.26, 56.95) * mm, "mid": v(46.7, 55.9) * mm, "end": v(47.76, 55.45) * mm});
            skArc(sketch, "E2527", {"start": v(47.76, 55.45) * mm, "mid": v(48.82, 55.9) * mm, "end": v(49.26, 56.95) * mm});
            skArc(sketch, "E2528", {"start": v(49.26, 56.95) * mm, "mid": v(48.82, 58.01) * mm, "end": v(47.76, 58.45) * mm});
            skArc(sketch, "E2529", {"start": v(54.27, 58.45) * mm, "mid": v(53.2, 58.01) * mm, "end": v(52.77, 56.95) * mm});
            skArc(sketch, "E2530", {"start": v(52.77, 56.95) * mm, "mid": v(53.2, 55.9) * mm, "end": v(54.27, 55.45) * mm});
            skArc(sketch, "E2531", {"start": v(54.27, 55.45) * mm, "mid": v(55.33, 55.9) * mm, "end": v(55.77, 56.95) * mm});
            skArc(sketch, "E2532", {"start": v(55.77, 56.95) * mm, "mid": v(55.33, 58.01) * mm, "end": v(54.27, 58.45) * mm});
            skLineSegment(sketch, "E2533", {"start": v(50.73, 46.62) * mm, "end": v(50.6, 46.6) * mm});
            skLineSegment(sketch, "E2534", {"start": v(50.6, 46.6) * mm, "end": v(50.5, 46.58) * mm});
            skLineSegment(sketch, "E2535", {"start": v(50.5, 46.58) * mm, "end": v(50.28, 46.5) * mm});
            skLineSegment(sketch, "E2536", {"start": v(50.28, 46.5) * mm, "end": v(50.06, 46.4) * mm});
            skLineSegment(sketch, "E2537", {"start": v(50.06, 46.4) * mm, "end": v(49.85, 46.27) * mm});
            skLineSegment(sketch, "E2538", {"start": v(49.85, 46.27) * mm, "end": v(49.67, 46.12) * mm});
            skLineSegment(sketch, "E2539", {"start": v(49.67, 46.12) * mm, "end": v(49.47, 45.92) * mm});
            skLineSegment(sketch, "E2540", {"start": v(49.47, 45.92) * mm, "end": v(49.4, 45.8) * mm});
            skLineSegment(sketch, "E2541", {"start": v(49.4, 45.8) * mm, "end": v(49.4, 45.8) * mm});
            skLineSegment(sketch, "E2542", {"start": v(49.4, 45.8) * mm, "end": v(49.34, 45.7) * mm});
            skLineSegment(sketch, "E2543", {"start": v(49.34, 45.7) * mm, "end": v(49.24, 45.53) * mm});
            skLineSegment(sketch, "E2544", {"start": v(49.24, 45.53) * mm, "end": v(49.17, 45.34) * mm});
            skLineSegment(sketch, "E2545", {"start": v(49.17, 45.34) * mm, "end": v(49.09, 45.1) * mm});
            skLineSegment(sketch, "E2546", {"start": v(49.09, 45.1) * mm, "end": v(49.05, 45) * mm});
            skLineSegment(sketch, "E2547", {"start": v(49.05, 45) * mm, "end": v(49.05, 37.9) * mm});
            skLineSegment(sketch, "E2548", {"start": v(49.05, 37.9) * mm, "end": v(49.09, 37.81) * mm});
            skLineSegment(sketch, "E2549", {"start": v(49.09, 37.81) * mm, "end": v(49.16, 37.58) * mm});
            skLineSegment(sketch, "E2550", {"start": v(49.16, 37.58) * mm, "end": v(49.21, 37.43) * mm});
            skLineSegment(sketch, "E2551", {"start": v(49.21, 37.43) * mm, "end": v(49.26, 37.31) * mm});
            skLineSegment(sketch, "E2552", {"start": v(49.26, 37.31) * mm, "end": v(49.33, 37.2) * mm});
            skLineSegment(sketch, "E2553", {"start": v(49.33, 37.2) * mm, "end": v(49.4, 37.11) * mm});
            skLineSegment(sketch, "E2554", {"start": v(49.4, 37.11) * mm, "end": v(49.41, 37.1) * mm});
            skLineSegment(sketch, "E2555", {"start": v(49.41, 37.1) * mm, "end": v(49.42, 37.07) * mm});
            skLineSegment(sketch, "E2556", {"start": v(49.42, 37.07) * mm, "end": v(49.48, 36.98) * mm});
            skLineSegment(sketch, "E2557", {"start": v(49.48, 36.98) * mm, "end": v(49.58, 36.87) * mm});
            skLineSegment(sketch, "E2558", {"start": v(49.58, 36.87) * mm, "end": v(49.78, 36.68) * mm});
            skLineSegment(sketch, "E2559", {"start": v(49.78, 36.68) * mm, "end": v(49.87, 36.62) * mm});
            skLineSegment(sketch, "E2560", {"start": v(49.87, 36.62) * mm, "end": v(49.93, 36.58) * mm});
            skLineSegment(sketch, "E2561", {"start": v(49.93, 36.58) * mm, "end": v(49.96, 36.56) * mm});
            skLineSegment(sketch, "E2562", {"start": v(49.96, 36.56) * mm, "end": v(50.05, 36.51) * mm});
            skLineSegment(sketch, "E2563", {"start": v(50.05, 36.51) * mm, "end": v(50.34, 36.37) * mm});
            skLineSegment(sketch, "E2564", {"start": v(50.34, 36.37) * mm, "end": v(50.49, 36.32) * mm});
            skLineSegment(sketch, "E2565", {"start": v(50.49, 36.32) * mm, "end": v(50.65, 36.29) * mm});
            skLineSegment(sketch, "E2566", {"start": v(50.65, 36.29) * mm, "end": v(50.83, 36.27) * mm});
            skLineSegment(sketch, "E2567", {"start": v(50.83, 36.27) * mm, "end": v(51, 36.26) * mm});
            skLineSegment(sketch, "E2568", {"start": v(51, 36.26) * mm, "end": v(51.19, 36.27) * mm});
            skLineSegment(sketch, "E2569", {"start": v(51.19, 36.27) * mm, "end": v(51.36, 36.29) * mm});
            skLineSegment(sketch, "E2570", {"start": v(51.36, 36.29) * mm, "end": v(51.53, 36.32) * mm});
            skLineSegment(sketch, "E2571", {"start": v(51.53, 36.32) * mm, "end": v(51.68, 36.37) * mm});
            skLineSegment(sketch, "E2572", {"start": v(51.68, 36.37) * mm, "end": v(51.98, 36.5) * mm});
            skLineSegment(sketch, "E2573", {"start": v(51.98, 36.5) * mm, "end": v(52.08, 36.56) * mm});
            skLineSegment(sketch, "E2574", {"start": v(52.08, 36.56) * mm, "end": v(52.11, 36.6) * mm});
            skLineSegment(sketch, "E2575", {"start": v(52.11, 36.6) * mm, "end": v(52.14, 36.6) * mm});
            skLineSegment(sketch, "E2576", {"start": v(52.14, 36.6) * mm, "end": v(52.22, 36.66) * mm});
            skLineSegment(sketch, "E2577", {"start": v(52.22, 36.66) * mm, "end": v(52.37, 36.8) * mm});
            skLineSegment(sketch, "E2578", {"start": v(52.37, 36.8) * mm, "end": v(52.52, 36.94) * mm});
            skLineSegment(sketch, "E2579", {"start": v(52.52, 36.94) * mm, "end": v(52.58, 37.02) * mm});
            skLineSegment(sketch, "E2580", {"start": v(52.58, 37.02) * mm, "end": v(52.6, 37.08) * mm});
            skLineSegment(sketch, "E2581", {"start": v(52.6, 37.08) * mm, "end": v(52.62, 37.1) * mm});
            skLineSegment(sketch, "E2582", {"start": v(52.62, 37.1) * mm, "end": v(52.62, 37.1) * mm});
            skLineSegment(sketch, "E2583", {"start": v(52.62, 37.1) * mm, "end": v(52.69, 37.19) * mm});
            skLineSegment(sketch, "E2584", {"start": v(52.69, 37.19) * mm, "end": v(52.75, 37.27) * mm});
            skLineSegment(sketch, "E2585", {"start": v(52.75, 37.27) * mm, "end": v(52.8, 37.4) * mm});
            skLineSegment(sketch, "E2586", {"start": v(52.8, 37.4) * mm, "end": v(52.94, 37.8) * mm});
            skLineSegment(sketch, "E2587", {"start": v(52.94, 37.8) * mm, "end": v(52.98, 37.94) * mm});
            skLineSegment(sketch, "E2588", {"start": v(52.98, 37.94) * mm, "end": v(52.98, 45) * mm});
            skLineSegment(sketch, "E2589", {"start": v(52.98, 45) * mm, "end": v(52.94, 45.1) * mm});
            skLineSegment(sketch, "E2590", {"start": v(52.94, 45.1) * mm, "end": v(52.86, 45.34) * mm});
            skLineSegment(sketch, "E2591", {"start": v(52.86, 45.34) * mm, "end": v(52.79, 45.53) * mm});
            skLineSegment(sketch, "E2592", {"start": v(52.79, 45.53) * mm, "end": v(52.7, 45.7) * mm});
            skLineSegment(sketch, "E2593", {"start": v(52.7, 45.7) * mm, "end": v(52.63, 45.8) * mm});
            skLineSegment(sketch, "E2594", {"start": v(52.63, 45.8) * mm, "end": v(52.6, 45.86) * mm});
            skLineSegment(sketch, "E2595", {"start": v(52.6, 45.86) * mm, "end": v(52.55, 45.92) * mm});
            skLineSegment(sketch, "E2596", {"start": v(52.55, 45.92) * mm, "end": v(52.46, 46.02) * mm});
            skLineSegment(sketch, "E2597", {"start": v(52.46, 46.02) * mm, "end": v(52.2, 46.26) * mm});
            skLineSegment(sketch, "E2598", {"start": v(52.2, 46.26) * mm, "end": v(52.06, 46.35) * mm});
            skLineSegment(sketch, "E2599", {"start": v(52.06, 46.35) * mm, "end": v(51.89, 46.44) * mm});
            skLineSegment(sketch, "E2600", {"start": v(51.89, 46.44) * mm, "end": v(51.7, 46.52) * mm});
            skLineSegment(sketch, "E2601", {"start": v(51.7, 46.52) * mm, "end": v(51.53, 46.58) * mm});
            skLineSegment(sketch, "E2602", {"start": v(51.53, 46.58) * mm, "end": v(51.42, 46.6) * mm});
            skLineSegment(sketch, "E2603", {"start": v(51.42, 46.6) * mm, "end": v(51.3, 46.62) * mm});
            skLineSegment(sketch, "E2604", {"start": v(51.3, 46.62) * mm, "end": v(51.02, 46.63) * mm});
            skLineSegment(sketch, "E2605", {"start": v(51.02, 46.63) * mm, "end": v(50.73, 46.62) * mm});
            skLineSegment(sketch, "E2606", {"start": v(41.5, 45.73) * mm, "end": v(43.5, 45.73) * mm});
            skLineSegment(sketch, "E2607", {"start": v(43.5, 45.73) * mm, "end": v(43.5, 48.73) * mm});
            skLineSegment(sketch, "E2608", {"start": v(43.5, 48.73) * mm, "end": v(41.5, 48.73) * mm});
            skLineSegment(sketch, "E2609", {"start": v(41.5, 48.73) * mm, "end": v(41.5, 45.73) * mm});
            skLineSegment(sketch, "E2610", {"start": v(49.5, -1) * mm, "end": v(52.5, -1) * mm});
            skLineSegment(sketch, "E2611", {"start": v(52.5, -1) * mm, "end": v(52.5, 1) * mm});
            skLineSegment(sketch, "E2612", {"start": v(52.5, 1) * mm, "end": v(49.5, 1) * mm});
            skLineSegment(sketch, "E2613", {"start": v(49.5, 1) * mm, "end": v(49.5, -1) * mm});
            skLineSegment(sketch, "E2614", {"start": v(43.5, 21.64) * mm, "end": v(58.5, 21.64) * mm});
            skLineSegment(sketch, "E2615", {"start": v(58.5, 21.64) * mm, "end": v(58.5, 30.48) * mm});
            skLineSegment(sketch, "E2616", {"start": v(58.5, 30.48) * mm, "end": v(43.5, 30.48) * mm});
            skLineSegment(sketch, "E2617", {"start": v(43.5, 30.48) * mm, "end": v(43.5, 21.64) * mm});
            skArc(sketch, "E2618", {"start": v(51.76, 25.47) * mm, "mid": v(52.5, 23.7) * mm, "end": v(54.26, 22.97) * mm});
            skArc(sketch, "E2619", {"start": v(54.26, 22.97) * mm, "mid": v(56.03, 23.7) * mm, "end": v(56.76, 25.47) * mm});
            skArc(sketch, "E2620", {"start": v(56.76, 25.47) * mm, "mid": v(56.03, 27.23) * mm, "end": v(54.26, 27.97) * mm});
            skArc(sketch, "E2621", {"start": v(54.26, 27.97) * mm, "mid": v(52.5, 27.23) * mm, "end": v(51.76, 25.47) * mm});
            skLineSegment(sketch, "E2622", {"start": v(43.5, 30.48) * mm, "end": v(43.5, 7) * mm});
            skArc(sketch, "E2623", {"start": v(43.5, 7) * mm, "mid": v(45.26, 2.76) * mm, "end": v(49.5, 1) * mm});
            skLineSegment(sketch, "E2624", {"start": v(49.5, 1) * mm, "end": v(52.5, 1) * mm});
            skArc(sketch, "E2625", {"start": v(52.5, 1) * mm, "mid": v(56.74, 2.76) * mm, "end": v(58.5, 7) * mm});
            skLineSegment(sketch, "E2626", {"start": v(58.5, 7) * mm, "end": v(58.5, 30.48) * mm});
            skArc(sketch, "E2627", {"start": v(45.26, 25.47) * mm, "mid": v(46, 23.7) * mm, "end": v(47.76, 22.97) * mm});
            skArc(sketch, "E2628", {"start": v(47.76, 22.97) * mm, "mid": v(49.53, 23.7) * mm, "end": v(50.26, 25.47) * mm});
            skArc(sketch, "E2629", {"start": v(50.26, 25.47) * mm, "mid": v(49.53, 27.23) * mm, "end": v(47.76, 27.97) * mm});
            skArc(sketch, "E2630", {"start": v(47.76, 27.97) * mm, "mid": v(46, 27.23) * mm, "end": v(45.26, 25.47) * mm});
            skArc(sketch, "E2631", {"start": v(47.76, 26.97) * mm, "mid": v(46.7, 26.53) * mm, "end": v(46.26, 25.47) * mm});
            skArc(sketch, "E2632", {"start": v(46.26, 25.47) * mm, "mid": v(46.7, 24.4) * mm, "end": v(47.76, 23.97) * mm});
            skArc(sketch, "E2633", {"start": v(47.76, 23.97) * mm, "mid": v(48.82, 24.4) * mm, "end": v(49.26, 25.47) * mm});
            skArc(sketch, "E2634", {"start": v(49.26, 25.47) * mm, "mid": v(48.82, 26.53) * mm, "end": v(47.76, 26.97) * mm});
            skArc(sketch, "E2635", {"start": v(54.27, 26.97) * mm, "mid": v(53.2, 26.53) * mm, "end": v(52.77, 25.47) * mm});
            skArc(sketch, "E2636", {"start": v(52.77, 25.47) * mm, "mid": v(53.2, 24.4) * mm, "end": v(54.27, 23.97) * mm});
            skArc(sketch, "E2637", {"start": v(54.27, 23.97) * mm, "mid": v(55.33, 24.4) * mm, "end": v(55.77, 25.47) * mm});
            skArc(sketch, "E2638", {"start": v(55.77, 25.47) * mm, "mid": v(55.33, 26.53) * mm, "end": v(54.27, 26.97) * mm});
            skLineSegment(sketch, "E2639", {"start": v(50.73, 15.13) * mm, "end": v(50.6, 15.12) * mm});
            skLineSegment(sketch, "E2640", {"start": v(50.6, 15.12) * mm, "end": v(50.5, 15.1) * mm});
            skLineSegment(sketch, "E2641", {"start": v(50.5, 15.1) * mm, "end": v(50.28, 15.02) * mm});
            skLineSegment(sketch, "E2642", {"start": v(50.28, 15.02) * mm, "end": v(50.06, 14.91) * mm});
            skLineSegment(sketch, "E2643", {"start": v(50.06, 14.91) * mm, "end": v(49.85, 14.78) * mm});
            skLineSegment(sketch, "E2644", {"start": v(49.85, 14.78) * mm, "end": v(49.67, 14.63) * mm});
            skLineSegment(sketch, "E2645", {"start": v(49.67, 14.63) * mm, "end": v(49.47, 14.44) * mm});
            skLineSegment(sketch, "E2646", {"start": v(49.47, 14.44) * mm, "end": v(49.4, 14.32) * mm});
            skLineSegment(sketch, "E2647", {"start": v(49.4, 14.32) * mm, "end": v(49.4, 14.31) * mm});
            skLineSegment(sketch, "E2648", {"start": v(49.4, 14.31) * mm, "end": v(49.34, 14.21) * mm});
            skLineSegment(sketch, "E2649", {"start": v(49.34, 14.21) * mm, "end": v(49.24, 14.04) * mm});
            skLineSegment(sketch, "E2650", {"start": v(49.24, 14.04) * mm, "end": v(49.17, 13.86) * mm});
            skLineSegment(sketch, "E2651", {"start": v(49.17, 13.86) * mm, "end": v(49.09, 13.61) * mm});
            skLineSegment(sketch, "E2652", {"start": v(49.09, 13.61) * mm, "end": v(49.05, 13.51) * mm});
            skLineSegment(sketch, "E2653", {"start": v(49.05, 13.51) * mm, "end": v(49.05, 6.42) * mm});
            skLineSegment(sketch, "E2654", {"start": v(49.05, 6.42) * mm, "end": v(49.09, 6.33) * mm});
            skLineSegment(sketch, "E2655", {"start": v(49.09, 6.33) * mm, "end": v(49.16, 6.1) * mm});
            skLineSegment(sketch, "E2656", {"start": v(49.16, 6.1) * mm, "end": v(49.21, 5.95) * mm});
            skLineSegment(sketch, "E2657", {"start": v(49.21, 5.95) * mm, "end": v(49.26, 5.83) * mm});
            skLineSegment(sketch, "E2658", {"start": v(49.26, 5.83) * mm, "end": v(49.33, 5.72) * mm});
            skLineSegment(sketch, "E2659", {"start": v(49.33, 5.72) * mm, "end": v(49.4, 5.63) * mm});
            skLineSegment(sketch, "E2660", {"start": v(49.4, 5.63) * mm, "end": v(49.41, 5.62) * mm});
            skLineSegment(sketch, "E2661", {"start": v(49.41, 5.62) * mm, "end": v(49.42, 5.58) * mm});
            skLineSegment(sketch, "E2662", {"start": v(49.42, 5.58) * mm, "end": v(49.48, 5.5) * mm});
            skLineSegment(sketch, "E2663", {"start": v(49.48, 5.5) * mm, "end": v(49.58, 5.39) * mm});
            skLineSegment(sketch, "E2664", {"start": v(49.58, 5.39) * mm, "end": v(49.78, 5.2) * mm});
            skLineSegment(sketch, "E2665", {"start": v(49.78, 5.2) * mm, "end": v(49.87, 5.13) * mm});
            skLineSegment(sketch, "E2666", {"start": v(49.87, 5.13) * mm, "end": v(49.93, 5.1) * mm});
            skLineSegment(sketch, "E2667", {"start": v(49.93, 5.1) * mm, "end": v(49.96, 5.08) * mm});
            skLineSegment(sketch, "E2668", {"start": v(49.96, 5.08) * mm, "end": v(50.05, 5.03) * mm});
            skLineSegment(sketch, "E2669", {"start": v(50.05, 5.03) * mm, "end": v(50.34, 4.89) * mm});
            skLineSegment(sketch, "E2670", {"start": v(50.34, 4.89) * mm, "end": v(50.49, 4.84) * mm});
            skLineSegment(sketch, "E2671", {"start": v(50.49, 4.84) * mm, "end": v(50.65, 4.8) * mm});
            skLineSegment(sketch, "E2672", {"start": v(50.65, 4.8) * mm, "end": v(50.83, 4.78) * mm});
            skLineSegment(sketch, "E2673", {"start": v(50.83, 4.78) * mm, "end": v(51, 4.78) * mm});
            skLineSegment(sketch, "E2674", {"start": v(51, 4.78) * mm, "end": v(51.19, 4.78) * mm});
            skLineSegment(sketch, "E2675", {"start": v(51.19, 4.78) * mm, "end": v(51.36, 4.8) * mm});
            skLineSegment(sketch, "E2676", {"start": v(51.36, 4.8) * mm, "end": v(51.53, 4.84) * mm});
            skLineSegment(sketch, "E2677", {"start": v(51.53, 4.84) * mm, "end": v(51.68, 4.89) * mm});
            skLineSegment(sketch, "E2678", {"start": v(51.68, 4.89) * mm, "end": v(51.98, 5.02) * mm});
            skLineSegment(sketch, "E2679", {"start": v(51.98, 5.02) * mm, "end": v(52.08, 5.08) * mm});
            skLineSegment(sketch, "E2680", {"start": v(52.08, 5.08) * mm, "end": v(52.11, 5.11) * mm});
            skLineSegment(sketch, "E2681", {"start": v(52.11, 5.11) * mm, "end": v(52.14, 5.12) * mm});
            skLineSegment(sketch, "E2682", {"start": v(52.14, 5.12) * mm, "end": v(52.22, 5.18) * mm});
            skLineSegment(sketch, "E2683", {"start": v(52.22, 5.18) * mm, "end": v(52.37, 5.31) * mm});
            skLineSegment(sketch, "E2684", {"start": v(52.37, 5.31) * mm, "end": v(52.52, 5.46) * mm});
            skLineSegment(sketch, "E2685", {"start": v(52.52, 5.46) * mm, "end": v(52.58, 5.53) * mm});
            skLineSegment(sketch, "E2686", {"start": v(52.58, 5.53) * mm, "end": v(52.6, 5.6) * mm});
            skLineSegment(sketch, "E2687", {"start": v(52.6, 5.6) * mm, "end": v(52.62, 5.62) * mm});
            skLineSegment(sketch, "E2688", {"start": v(52.62, 5.62) * mm, "end": v(52.62, 5.62) * mm});
            skLineSegment(sketch, "E2689", {"start": v(52.62, 5.62) * mm, "end": v(52.69, 5.7) * mm});
            skLineSegment(sketch, "E2690", {"start": v(52.69, 5.7) * mm, "end": v(52.75, 5.79) * mm});
            skLineSegment(sketch, "E2691", {"start": v(52.75, 5.79) * mm, "end": v(52.8, 5.91) * mm});
            skLineSegment(sketch, "E2692", {"start": v(52.8, 5.91) * mm, "end": v(52.94, 6.32) * mm});
            skLineSegment(sketch, "E2693", {"start": v(52.94, 6.32) * mm, "end": v(52.98, 6.46) * mm});
            skLineSegment(sketch, "E2694", {"start": v(52.98, 6.46) * mm, "end": v(52.98, 13.51) * mm});
            skLineSegment(sketch, "E2695", {"start": v(52.98, 13.51) * mm, "end": v(52.94, 13.61) * mm});
            skLineSegment(sketch, "E2696", {"start": v(52.94, 13.61) * mm, "end": v(52.86, 13.86) * mm});
            skLineSegment(sketch, "E2697", {"start": v(52.86, 13.86) * mm, "end": v(52.79, 14.04) * mm});
            skLineSegment(sketch, "E2698", {"start": v(52.79, 14.04) * mm, "end": v(52.7, 14.21) * mm});
            skLineSegment(sketch, "E2699", {"start": v(52.7, 14.21) * mm, "end": v(52.63, 14.31) * mm});
            skLineSegment(sketch, "E2700", {"start": v(52.63, 14.31) * mm, "end": v(52.6, 14.37) * mm});
            skLineSegment(sketch, "E2701", {"start": v(52.6, 14.37) * mm, "end": v(52.55, 14.44) * mm});
            skLineSegment(sketch, "E2702", {"start": v(52.55, 14.44) * mm, "end": v(52.46, 14.53) * mm});
            skLineSegment(sketch, "E2703", {"start": v(52.46, 14.53) * mm, "end": v(52.2, 14.77) * mm});
            skLineSegment(sketch, "E2704", {"start": v(52.2, 14.77) * mm, "end": v(52.06, 14.87) * mm});
            skLineSegment(sketch, "E2705", {"start": v(52.06, 14.87) * mm, "end": v(51.89, 14.96) * mm});
            skLineSegment(sketch, "E2706", {"start": v(51.89, 14.96) * mm, "end": v(51.7, 15.04) * mm});
            skLineSegment(sketch, "E2707", {"start": v(51.7, 15.04) * mm, "end": v(51.53, 15.1) * mm});
            skLineSegment(sketch, "E2708", {"start": v(51.53, 15.1) * mm, "end": v(51.42, 15.12) * mm});
            skLineSegment(sketch, "E2709", {"start": v(51.42, 15.12) * mm, "end": v(51.3, 15.13) * mm});
            skLineSegment(sketch, "E2710", {"start": v(51.3, 15.13) * mm, "end": v(51.02, 15.14) * mm});
            skLineSegment(sketch, "E2711", {"start": v(51.02, 15.14) * mm, "end": v(50.73, 15.13) * mm});
            skLineSegment(sketch, "E2712", {"start": v(41.5, 14.24) * mm, "end": v(43.5, 14.24) * mm});
            skLineSegment(sketch, "E2713", {"start": v(43.5, 14.24) * mm, "end": v(43.5, 17.24) * mm});
            skLineSegment(sketch, "E2714", {"start": v(43.5, 17.24) * mm, "end": v(41.5, 17.24) * mm});
            skLineSegment(sketch, "E2715", {"start": v(41.5, 17.24) * mm, "end": v(41.5, 14.24) * mm});
            skLineSegment(sketch, "E2716", {"start": v(49.5, -32.48) * mm, "end": v(52.5, -32.48) * mm});
            skLineSegment(sketch, "E2717", {"start": v(52.5, -32.48) * mm, "end": v(52.5, -30.48) * mm});
            skLineSegment(sketch, "E2718", {"start": v(52.5, -30.48) * mm, "end": v(49.5, -30.48) * mm});
            skLineSegment(sketch, "E2719", {"start": v(49.5, -30.48) * mm, "end": v(49.5, -32.48) * mm});
            skLineSegment(sketch, "E2720", {"start": v(43.5, -9.84) * mm, "end": v(58.5, -9.84) * mm});
            skLineSegment(sketch, "E2721", {"start": v(58.5, -9.84) * mm, "end": v(58.5, -1) * mm});
            skLineSegment(sketch, "E2722", {"start": v(58.5, -1) * mm, "end": v(43.5, -1) * mm});
            skLineSegment(sketch, "E2723", {"start": v(43.5, -1) * mm, "end": v(43.5, -9.84) * mm});
            skArc(sketch, "E2724", {"start": v(51.76, -6.02) * mm, "mid": v(52.5, -7.79) * mm, "end": v(54.26, -8.52) * mm});
            skArc(sketch, "E2725", {"start": v(54.26, -8.52) * mm, "mid": v(56.03, -7.79) * mm, "end": v(56.76, -6.02) * mm});
            skArc(sketch, "E2726", {"start": v(56.76, -6.02) * mm, "mid": v(56.03, -4.25) * mm, "end": v(54.26, -3.52) * mm});
            skArc(sketch, "E2727", {"start": v(54.26, -3.52) * mm, "mid": v(52.5, -4.25) * mm, "end": v(51.76, -6.02) * mm});
            skLineSegment(sketch, "E2728", {"start": v(43.5, -1) * mm, "end": v(43.5, -24.48) * mm});
            skArc(sketch, "E2729", {"start": v(43.5, -24.48) * mm, "mid": v(45.26, -28.73) * mm, "end": v(49.5, -30.48) * mm});
            skLineSegment(sketch, "E2730", {"start": v(49.5, -30.48) * mm, "end": v(52.5, -30.48) * mm});
            skArc(sketch, "E2731", {"start": v(52.5, -30.48) * mm, "mid": v(56.74, -28.73) * mm, "end": v(58.5, -24.48) * mm});
            skLineSegment(sketch, "E2732", {"start": v(58.5, -24.48) * mm, "end": v(58.5, -1) * mm});
            skArc(sketch, "E2733", {"start": v(45.26, -6.02) * mm, "mid": v(46, -7.79) * mm, "end": v(47.76, -8.52) * mm});
            skArc(sketch, "E2734", {"start": v(47.76, -8.52) * mm, "mid": v(49.53, -7.79) * mm, "end": v(50.26, -6.02) * mm});
            skArc(sketch, "E2735", {"start": v(50.26, -6.02) * mm, "mid": v(49.53, -4.25) * mm, "end": v(47.76, -3.52) * mm});
            skArc(sketch, "E2736", {"start": v(47.76, -3.52) * mm, "mid": v(46, -4.25) * mm, "end": v(45.26, -6.02) * mm});
            skArc(sketch, "E2737", {"start": v(47.76, -4.52) * mm, "mid": v(46.7, -4.96) * mm, "end": v(46.26, -6.02) * mm});
            skArc(sketch, "E2738", {"start": v(46.26, -6.02) * mm, "mid": v(46.7, -7.08) * mm, "end": v(47.76, -7.52) * mm});
            skArc(sketch, "E2739", {"start": v(47.76, -7.52) * mm, "mid": v(48.82, -7.08) * mm, "end": v(49.26, -6.02) * mm});
            skArc(sketch, "E2740", {"start": v(49.26, -6.02) * mm, "mid": v(48.82, -4.96) * mm, "end": v(47.76, -4.52) * mm});
            skArc(sketch, "E2741", {"start": v(54.27, -4.52) * mm, "mid": v(53.2, -4.96) * mm, "end": v(52.77, -6.02) * mm});
            skArc(sketch, "E2742", {"start": v(52.77, -6.02) * mm, "mid": v(53.2, -7.08) * mm, "end": v(54.27, -7.52) * mm});
            skArc(sketch, "E2743", {"start": v(54.27, -7.52) * mm, "mid": v(55.33, -7.08) * mm, "end": v(55.77, -6.02) * mm});
            skArc(sketch, "E2744", {"start": v(55.77, -6.02) * mm, "mid": v(55.33, -4.96) * mm, "end": v(54.27, -4.52) * mm});
            skLineSegment(sketch, "E2745", {"start": v(50.73, -16.35) * mm, "end": v(50.6, -16.36) * mm});
            skLineSegment(sketch, "E2746", {"start": v(50.6, -16.36) * mm, "end": v(50.5, -16.38) * mm});
            skLineSegment(sketch, "E2747", {"start": v(50.5, -16.38) * mm, "end": v(50.28, -16.46) * mm});
            skLineSegment(sketch, "E2748", {"start": v(50.28, -16.46) * mm, "end": v(50.06, -16.57) * mm});
            skLineSegment(sketch, "E2749", {"start": v(50.06, -16.57) * mm, "end": v(49.85, -16.7) * mm});
            skLineSegment(sketch, "E2750", {"start": v(49.85, -16.7) * mm, "end": v(49.67, -16.85) * mm});
            skLineSegment(sketch, "E2751", {"start": v(49.67, -16.85) * mm, "end": v(49.47, -17.04) * mm});
            skLineSegment(sketch, "E2752", {"start": v(49.47, -17.04) * mm, "end": v(49.4, -17.16) * mm});
            skLineSegment(sketch, "E2753", {"start": v(49.4, -17.16) * mm, "end": v(49.4, -17.17) * mm});
            skLineSegment(sketch, "E2754", {"start": v(49.4, -17.17) * mm, "end": v(49.34, -17.27) * mm});
            skLineSegment(sketch, "E2755", {"start": v(49.34, -17.27) * mm, "end": v(49.24, -17.44) * mm});
            skLineSegment(sketch, "E2756", {"start": v(49.24, -17.44) * mm, "end": v(49.17, -17.62) * mm});
            skLineSegment(sketch, "E2757", {"start": v(49.17, -17.62) * mm, "end": v(49.09, -17.87) * mm});
            skLineSegment(sketch, "E2758", {"start": v(49.09, -17.87) * mm, "end": v(49.05, -17.97) * mm});
            skLineSegment(sketch, "E2759", {"start": v(49.05, -17.97) * mm, "end": v(49.05, -25.07) * mm});
            skLineSegment(sketch, "E2760", {"start": v(49.05, -25.07) * mm, "end": v(49.09, -25.16) * mm});
            skLineSegment(sketch, "E2761", {"start": v(49.09, -25.16) * mm, "end": v(49.16, -25.39) * mm});
            skLineSegment(sketch, "E2762", {"start": v(49.16, -25.39) * mm, "end": v(49.21, -25.54) * mm});
            skLineSegment(sketch, "E2763", {"start": v(49.21, -25.54) * mm, "end": v(49.26, -25.65) * mm});
            skLineSegment(sketch, "E2764", {"start": v(49.26, -25.65) * mm, "end": v(49.33, -25.76) * mm});
            skLineSegment(sketch, "E2765", {"start": v(49.33, -25.76) * mm, "end": v(49.4, -25.86) * mm});
            skLineSegment(sketch, "E2766", {"start": v(49.4, -25.86) * mm, "end": v(49.41, -25.87) * mm});
            skLineSegment(sketch, "E2767", {"start": v(49.41, -25.87) * mm, "end": v(49.42, -25.9) * mm});
            skLineSegment(sketch, "E2768", {"start": v(49.42, -25.9) * mm, "end": v(49.48, -26) * mm});
            skLineSegment(sketch, "E2769", {"start": v(49.48, -26) * mm, "end": v(49.58, -26.1) * mm});
            skLineSegment(sketch, "E2770", {"start": v(49.58, -26.1) * mm, "end": v(49.78, -26.29) * mm});
            skLineSegment(sketch, "E2771", {"start": v(49.78, -26.29) * mm, "end": v(49.87, -26.35) * mm});
            skLineSegment(sketch, "E2772", {"start": v(49.87, -26.35) * mm, "end": v(49.93, -26.38) * mm});
            skLineSegment(sketch, "E2773", {"start": v(49.93, -26.38) * mm, "end": v(49.96, -26.4) * mm});
            skLineSegment(sketch, "E2774", {"start": v(49.96, -26.4) * mm, "end": v(50.05, -26.46) * mm});
            skLineSegment(sketch, "E2775", {"start": v(50.05, -26.46) * mm, "end": v(50.34, -26.6) * mm});
            skLineSegment(sketch, "E2776", {"start": v(50.34, -26.6) * mm, "end": v(50.49, -26.65) * mm});
            skLineSegment(sketch, "E2777", {"start": v(50.49, -26.65) * mm, "end": v(50.65, -26.68) * mm});
            skLineSegment(sketch, "E2778", {"start": v(50.65, -26.68) * mm, "end": v(50.83, -26.7) * mm});
            skLineSegment(sketch, "E2779", {"start": v(50.83, -26.7) * mm, "end": v(51, -26.7) * mm});
            skLineSegment(sketch, "E2780", {"start": v(51, -26.7) * mm, "end": v(51.19, -26.7) * mm});
            skLineSegment(sketch, "E2781", {"start": v(51.19, -26.7) * mm, "end": v(51.36, -26.68) * mm});
            skLineSegment(sketch, "E2782", {"start": v(51.36, -26.68) * mm, "end": v(51.53, -26.65) * mm});
            skLineSegment(sketch, "E2783", {"start": v(51.53, -26.65) * mm, "end": v(51.68, -26.6) * mm});
            skLineSegment(sketch, "E2784", {"start": v(51.68, -26.6) * mm, "end": v(51.98, -26.46) * mm});
            skLineSegment(sketch, "E2785", {"start": v(51.98, -26.46) * mm, "end": v(52.08, -26.4) * mm});
            skLineSegment(sketch, "E2786", {"start": v(52.08, -26.4) * mm, "end": v(52.11, -26.37) * mm});
            skLineSegment(sketch, "E2787", {"start": v(52.11, -26.37) * mm, "end": v(52.14, -26.36) * mm});
            skLineSegment(sketch, "E2788", {"start": v(52.14, -26.36) * mm, "end": v(52.22, -26.3) * mm});
            skLineSegment(sketch, "E2789", {"start": v(52.22, -26.3) * mm, "end": v(52.37, -26.17) * mm});
            skLineSegment(sketch, "E2790", {"start": v(52.37, -26.17) * mm, "end": v(52.52, -26.03) * mm});
            skLineSegment(sketch, "E2791", {"start": v(52.52, -26.03) * mm, "end": v(52.58, -25.95) * mm});
            skLineSegment(sketch, "E2792", {"start": v(52.58, -25.95) * mm, "end": v(52.6, -25.89) * mm});
            skLineSegment(sketch, "E2793", {"start": v(52.6, -25.89) * mm, "end": v(52.62, -25.87) * mm});
            skLineSegment(sketch, "E2794", {"start": v(52.62, -25.87) * mm, "end": v(52.62, -25.86) * mm});
            skLineSegment(sketch, "E2795", {"start": v(52.62, -25.86) * mm, "end": v(52.69, -25.78) * mm});
            skLineSegment(sketch, "E2796", {"start": v(52.69, -25.78) * mm, "end": v(52.75, -25.7) * mm});
            skLineSegment(sketch, "E2797", {"start": v(52.75, -25.7) * mm, "end": v(52.8, -25.57) * mm});
            skLineSegment(sketch, "E2798", {"start": v(52.8, -25.57) * mm, "end": v(52.94, -25.16) * mm});
            skLineSegment(sketch, "E2799", {"start": v(52.94, -25.16) * mm, "end": v(52.98, -25.03) * mm});
            skLineSegment(sketch, "E2800", {"start": v(52.98, -25.03) * mm, "end": v(52.98, -17.97) * mm});
            skLineSegment(sketch, "E2801", {"start": v(52.98, -17.97) * mm, "end": v(52.94, -17.87) * mm});
            skLineSegment(sketch, "E2802", {"start": v(52.94, -17.87) * mm, "end": v(52.86, -17.62) * mm});
            skLineSegment(sketch, "E2803", {"start": v(52.86, -17.62) * mm, "end": v(52.79, -17.44) * mm});
            skLineSegment(sketch, "E2804", {"start": v(52.79, -17.44) * mm, "end": v(52.7, -17.27) * mm});
            skLineSegment(sketch, "E2805", {"start": v(52.7, -17.27) * mm, "end": v(52.63, -17.17) * mm});
            skLineSegment(sketch, "E2806", {"start": v(52.63, -17.17) * mm, "end": v(52.6, -17.11) * mm});
            skLineSegment(sketch, "E2807", {"start": v(52.6, -17.11) * mm, "end": v(52.55, -17.05) * mm});
            skLineSegment(sketch, "E2808", {"start": v(52.55, -17.05) * mm, "end": v(52.46, -16.95) * mm});
            skLineSegment(sketch, "E2809", {"start": v(52.46, -16.95) * mm, "end": v(52.2, -16.7) * mm});
            skLineSegment(sketch, "E2810", {"start": v(52.2, -16.7) * mm, "end": v(52.06, -16.62) * mm});
            skLineSegment(sketch, "E2811", {"start": v(52.06, -16.62) * mm, "end": v(51.89, -16.53) * mm});
            skLineSegment(sketch, "E2812", {"start": v(51.89, -16.53) * mm, "end": v(51.7, -16.45) * mm});
            skLineSegment(sketch, "E2813", {"start": v(51.7, -16.45) * mm, "end": v(51.53, -16.38) * mm});
            skLineSegment(sketch, "E2814", {"start": v(51.53, -16.38) * mm, "end": v(51.42, -16.36) * mm});
            skLineSegment(sketch, "E2815", {"start": v(51.42, -16.36) * mm, "end": v(51.3, -16.35) * mm});
            skLineSegment(sketch, "E2816", {"start": v(51.3, -16.35) * mm, "end": v(51.02, -16.34) * mm});
            skLineSegment(sketch, "E2817", {"start": v(51.02, -16.34) * mm, "end": v(50.73, -16.35) * mm});
            skLineSegment(sketch, "E2818", {"start": v(41.5, -17.24) * mm, "end": v(43.5, -17.24) * mm});
            skLineSegment(sketch, "E2819", {"start": v(43.5, -17.24) * mm, "end": v(43.5, -14.24) * mm});
            skLineSegment(sketch, "E2820", {"start": v(43.5, -14.24) * mm, "end": v(41.5, -14.24) * mm});
            skLineSegment(sketch, "E2821", {"start": v(41.5, -14.24) * mm, "end": v(41.5, -17.24) * mm});
            skLineSegment(sketch, "E2822", {"start": v(43.5, -41.33) * mm, "end": v(58.5, -41.33) * mm});
            skLineSegment(sketch, "E2823", {"start": v(58.5, -41.33) * mm, "end": v(58.5, -32.48) * mm});
            skLineSegment(sketch, "E2824", {"start": v(58.5, -32.48) * mm, "end": v(43.5, -32.48) * mm});
            skLineSegment(sketch, "E2825", {"start": v(43.5, -32.48) * mm, "end": v(43.5, -41.33) * mm});
            skArc(sketch, "E2826", {"start": v(51.76, -37.5) * mm, "mid": v(52.5, -39.27) * mm, "end": v(54.26, -40) * mm});
            skArc(sketch, "E2827", {"start": v(54.26, -40) * mm, "mid": v(56.03, -39.27) * mm, "end": v(56.76, -37.5) * mm});
            skArc(sketch, "E2828", {"start": v(56.76, -37.5) * mm, "mid": v(56.03, -35.73) * mm, "end": v(54.26, -35) * mm});
            skArc(sketch, "E2829", {"start": v(54.26, -35) * mm, "mid": v(52.5, -35.73) * mm, "end": v(51.76, -37.5) * mm});
            skLineSegment(sketch, "E2830", {"start": v(43.5, -32.48) * mm, "end": v(43.5, -55.97) * mm});
            skArc(sketch, "E2831", {"start": v(43.5, -55.97) * mm, "mid": v(45.26, -60.21) * mm, "end": v(49.5, -61.97) * mm});
            skLineSegment(sketch, "E2832", {"start": v(49.5, -61.97) * mm, "end": v(52.5, -61.97) * mm});
            skArc(sketch, "E2833", {"start": v(52.5, -61.97) * mm, "mid": v(56.74, -60.21) * mm, "end": v(58.5, -55.97) * mm});
            skLineSegment(sketch, "E2834", {"start": v(58.5, -55.97) * mm, "end": v(58.5, -32.48) * mm});
            skArc(sketch, "E2835", {"start": v(45.26, -37.5) * mm, "mid": v(46, -39.27) * mm, "end": v(47.76, -40) * mm});
            skArc(sketch, "E2836", {"start": v(47.76, -40) * mm, "mid": v(49.53, -39.27) * mm, "end": v(50.26, -37.5) * mm});
            skArc(sketch, "E2837", {"start": v(50.26, -37.5) * mm, "mid": v(49.53, -35.73) * mm, "end": v(47.76, -35) * mm});
            skArc(sketch, "E2838", {"start": v(47.76, -35) * mm, "mid": v(46, -35.73) * mm, "end": v(45.26, -37.5) * mm});
            skArc(sketch, "E2839", {"start": v(47.76, -36) * mm, "mid": v(46.7, -36.44) * mm, "end": v(46.26, -37.5) * mm});
            skArc(sketch, "E2840", {"start": v(46.26, -37.5) * mm, "mid": v(46.7, -38.56) * mm, "end": v(47.76, -39) * mm});
            skArc(sketch, "E2841", {"start": v(47.76, -39) * mm, "mid": v(48.82, -38.56) * mm, "end": v(49.26, -37.5) * mm});
            skArc(sketch, "E2842", {"start": v(49.26, -37.5) * mm, "mid": v(48.82, -36.44) * mm, "end": v(47.76, -36) * mm});
            skArc(sketch, "E2843", {"start": v(54.27, -36) * mm, "mid": v(53.2, -36.44) * mm, "end": v(52.77, -37.5) * mm});
            skArc(sketch, "E2844", {"start": v(52.77, -37.5) * mm, "mid": v(53.2, -38.56) * mm, "end": v(54.27, -39) * mm});
            skArc(sketch, "E2845", {"start": v(54.27, -39) * mm, "mid": v(55.33, -38.56) * mm, "end": v(55.77, -37.5) * mm});
            skArc(sketch, "E2846", {"start": v(55.77, -37.5) * mm, "mid": v(55.33, -36.44) * mm, "end": v(54.27, -36) * mm});
            skLineSegment(sketch, "E2847", {"start": v(50.73, -47.84) * mm, "end": v(50.6, -47.85) * mm});
            skLineSegment(sketch, "E2848", {"start": v(50.6, -47.85) * mm, "end": v(50.5, -47.87) * mm});
            skLineSegment(sketch, "E2849", {"start": v(50.5, -47.87) * mm, "end": v(50.28, -47.95) * mm});
            skLineSegment(sketch, "E2850", {"start": v(50.28, -47.95) * mm, "end": v(50.06, -48.05) * mm});
            skLineSegment(sketch, "E2851", {"start": v(50.06, -48.05) * mm, "end": v(49.85, -48.19) * mm});
            skLineSegment(sketch, "E2852", {"start": v(49.85, -48.19) * mm, "end": v(49.67, -48.34) * mm});
            skLineSegment(sketch, "E2853", {"start": v(49.67, -48.34) * mm, "end": v(49.47, -48.53) * mm});
            skLineSegment(sketch, "E2854", {"start": v(49.47, -48.53) * mm, "end": v(49.4, -48.65) * mm});
            skLineSegment(sketch, "E2855", {"start": v(49.4, -48.65) * mm, "end": v(49.4, -48.66) * mm});
            skLineSegment(sketch, "E2856", {"start": v(49.4, -48.66) * mm, "end": v(49.34, -48.76) * mm});
            skLineSegment(sketch, "E2857", {"start": v(49.34, -48.76) * mm, "end": v(49.24, -48.92) * mm});
            skLineSegment(sketch, "E2858", {"start": v(49.24, -48.92) * mm, "end": v(49.17, -49.1) * mm});
            skLineSegment(sketch, "E2859", {"start": v(49.17, -49.1) * mm, "end": v(49.09, -49.36) * mm});
            skLineSegment(sketch, "E2860", {"start": v(49.09, -49.36) * mm, "end": v(49.05, -49.45) * mm});
            skLineSegment(sketch, "E2861", {"start": v(49.05, -49.45) * mm, "end": v(49.05, -56.55) * mm});
            skLineSegment(sketch, "E2862", {"start": v(49.05, -56.55) * mm, "end": v(49.09, -56.64) * mm});
            skLineSegment(sketch, "E2863", {"start": v(49.09, -56.64) * mm, "end": v(49.16, -56.87) * mm});
            skLineSegment(sketch, "E2864", {"start": v(49.16, -56.87) * mm, "end": v(49.21, -57.02) * mm});
            skLineSegment(sketch, "E2865", {"start": v(49.21, -57.02) * mm, "end": v(49.26, -57.14) * mm});
            skLineSegment(sketch, "E2866", {"start": v(49.26, -57.14) * mm, "end": v(49.33, -57.24) * mm});
            skLineSegment(sketch, "E2867", {"start": v(49.33, -57.24) * mm, "end": v(49.4, -57.34) * mm});
            skLineSegment(sketch, "E2868", {"start": v(49.4, -57.34) * mm, "end": v(49.41, -57.35) * mm});
            skLineSegment(sketch, "E2869", {"start": v(49.41, -57.35) * mm, "end": v(49.42, -57.39) * mm});
            skLineSegment(sketch, "E2870", {"start": v(49.42, -57.39) * mm, "end": v(49.48, -57.47) * mm});
            skLineSegment(sketch, "E2871", {"start": v(49.48, -57.47) * mm, "end": v(49.58, -57.58) * mm});
            skLineSegment(sketch, "E2872", {"start": v(49.58, -57.58) * mm, "end": v(49.78, -57.77) * mm});
            skLineSegment(sketch, "E2873", {"start": v(49.78, -57.77) * mm, "end": v(49.87, -57.84) * mm});
            skLineSegment(sketch, "E2874", {"start": v(49.87, -57.84) * mm, "end": v(49.93, -57.87) * mm});
            skLineSegment(sketch, "E2875", {"start": v(49.93, -57.87) * mm, "end": v(49.96, -57.9) * mm});
            skLineSegment(sketch, "E2876", {"start": v(49.96, -57.9) * mm, "end": v(50.05, -57.94) * mm});
            skLineSegment(sketch, "E2877", {"start": v(50.05, -57.94) * mm, "end": v(50.34, -58.08) * mm});
            skLineSegment(sketch, "E2878", {"start": v(50.34, -58.08) * mm, "end": v(50.49, -58.13) * mm});
            skLineSegment(sketch, "E2879", {"start": v(50.49, -58.13) * mm, "end": v(50.65, -58.17) * mm});
            skLineSegment(sketch, "E2880", {"start": v(50.65, -58.17) * mm, "end": v(50.83, -58.19) * mm});
            skLineSegment(sketch, "E2881", {"start": v(50.83, -58.19) * mm, "end": v(51, -58.2) * mm});
            skLineSegment(sketch, "E2882", {"start": v(51, -58.2) * mm, "end": v(51.19, -58.19) * mm});
            skLineSegment(sketch, "E2883", {"start": v(51.19, -58.19) * mm, "end": v(51.36, -58.17) * mm});
            skLineSegment(sketch, "E2884", {"start": v(51.36, -58.17) * mm, "end": v(51.53, -58.13) * mm});
            skLineSegment(sketch, "E2885", {"start": v(51.53, -58.13) * mm, "end": v(51.68, -58.08) * mm});
            skLineSegment(sketch, "E2886", {"start": v(51.68, -58.08) * mm, "end": v(51.98, -57.95) * mm});
            skLineSegment(sketch, "E2887", {"start": v(51.98, -57.95) * mm, "end": v(52.08, -57.9) * mm});
            skLineSegment(sketch, "E2888", {"start": v(52.08, -57.9) * mm, "end": v(52.11, -57.86) * mm});
            skLineSegment(sketch, "E2889", {"start": v(52.11, -57.86) * mm, "end": v(52.14, -57.85) * mm});
            skLineSegment(sketch, "E2890", {"start": v(52.14, -57.85) * mm, "end": v(52.22, -57.79) * mm});
            skLineSegment(sketch, "E2891", {"start": v(52.22, -57.79) * mm, "end": v(52.37, -57.65) * mm});
            skLineSegment(sketch, "E2892", {"start": v(52.37, -57.65) * mm, "end": v(52.52, -57.51) * mm});
            skLineSegment(sketch, "E2893", {"start": v(52.52, -57.51) * mm, "end": v(52.58, -57.44) * mm});
            skLineSegment(sketch, "E2894", {"start": v(52.58, -57.44) * mm, "end": v(52.6, -57.37) * mm});
            skLineSegment(sketch, "E2895", {"start": v(52.6, -57.37) * mm, "end": v(52.62, -57.35) * mm});
            skLineSegment(sketch, "E2896", {"start": v(52.62, -57.35) * mm, "end": v(52.62, -57.34) * mm});
            skLineSegment(sketch, "E2897", {"start": v(52.62, -57.34) * mm, "end": v(52.69, -57.26) * mm});
            skLineSegment(sketch, "E2898", {"start": v(52.69, -57.26) * mm, "end": v(52.75, -57.18) * mm});
            skLineSegment(sketch, "E2899", {"start": v(52.75, -57.18) * mm, "end": v(52.8, -57.06) * mm});
            skLineSegment(sketch, "E2900", {"start": v(52.8, -57.06) * mm, "end": v(52.94, -56.65) * mm});
            skLineSegment(sketch, "E2901", {"start": v(52.94, -56.65) * mm, "end": v(52.98, -56.51) * mm});
            skLineSegment(sketch, "E2902", {"start": v(52.98, -56.51) * mm, "end": v(52.98, -49.45) * mm});
            skLineSegment(sketch, "E2903", {"start": v(52.98, -49.45) * mm, "end": v(52.94, -49.36) * mm});
            skLineSegment(sketch, "E2904", {"start": v(52.94, -49.36) * mm, "end": v(52.86, -49.1) * mm});
            skLineSegment(sketch, "E2905", {"start": v(52.86, -49.1) * mm, "end": v(52.79, -48.92) * mm});
            skLineSegment(sketch, "E2906", {"start": v(52.79, -48.92) * mm, "end": v(52.7, -48.76) * mm});
            skLineSegment(sketch, "E2907", {"start": v(52.7, -48.76) * mm, "end": v(52.63, -48.66) * mm});
            skLineSegment(sketch, "E2908", {"start": v(52.63, -48.66) * mm, "end": v(52.6, -48.6) * mm});
            skLineSegment(sketch, "E2909", {"start": v(52.6, -48.6) * mm, "end": v(52.55, -48.53) * mm});
            skLineSegment(sketch, "E2910", {"start": v(52.55, -48.53) * mm, "end": v(52.46, -48.44) * mm});
            skLineSegment(sketch, "E2911", {"start": v(52.46, -48.44) * mm, "end": v(52.2, -48.2) * mm});
            skLineSegment(sketch, "E2912", {"start": v(52.2, -48.2) * mm, "end": v(52.06, -48.1) * mm});
            skLineSegment(sketch, "E2913", {"start": v(52.06, -48.1) * mm, "end": v(51.89, -48.01) * mm});
            skLineSegment(sketch, "E2914", {"start": v(51.89, -48.01) * mm, "end": v(51.7, -47.93) * mm});
            skLineSegment(sketch, "E2915", {"start": v(51.7, -47.93) * mm, "end": v(51.53, -47.87) * mm});
            skLineSegment(sketch, "E2916", {"start": v(51.53, -47.87) * mm, "end": v(51.42, -47.85) * mm});
            skLineSegment(sketch, "E2917", {"start": v(51.42, -47.85) * mm, "end": v(51.3, -47.84) * mm});
            skLineSegment(sketch, "E2918", {"start": v(51.3, -47.84) * mm, "end": v(51.02, -47.83) * mm});
            skLineSegment(sketch, "E2919", {"start": v(51.02, -47.83) * mm, "end": v(50.73, -47.84) * mm});
            skLineSegment(sketch, "E2920", {"start": v(41.5, -48.73) * mm, "end": v(43.5, -48.73) * mm});
            skLineSegment(sketch, "E2921", {"start": v(43.5, -48.73) * mm, "end": v(43.5, -45.73) * mm});
            skLineSegment(sketch, "E2922", {"start": v(43.5, -45.73) * mm, "end": v(41.5, -45.73) * mm});
            skLineSegment(sketch, "E2923", {"start": v(41.5, -45.73) * mm, "end": v(41.5, -48.73) * mm});
            skSolve(sketch);
        }
        {
            var Q0;
            {var subQ3=sQuery(id+"F0.wireOp",EDGE,"E4");Q0=makeQuery(id+"F0.imprint","IMPRINT",FACE,{"disambiguationData":[TD([[makeQuery(id+"F0.imprint","IMPRINT",EDGE,{"derivedFrom":subQ3}),-1.0]])]});}
            var Q1;
            {var subQ1=sQuery(id+"F0.wireOp",EDGE,"E106");Q1=makeQuery(id+"F0.imprint","IMPRINT",FACE,{"disambiguationData":[TD([[makeQuery(id+"F0.imprint","IMPRINT",EDGE,{"derivedFrom":subQ1}),-1.0]])]});}
            var Q2;
            {var subQ1=sQuery(id+"F0.wireOp",EDGE,"E212");Q2=makeQuery(id+"F0.imprint","IMPRINT",FACE,{"disambiguationData":[TD([[makeQuery(id+"F0.imprint","IMPRINT",EDGE,{"derivedFrom":subQ1}),-1.0]])]});}
            var Q3;
            {var subQ2=sQuery(id+"F0.wireOp",EDGE,"E530");Q3=makeQuery(id+"F0.imprint","IMPRINT",FACE,{"disambiguationData":[TD([[makeQuery(id+"F0.imprint","IMPRINT",EDGE,{"derivedFrom":subQ2}),-1.0]])]});}
            var Q4;
            {var subQ1=sQuery(id+"F0.wireOp",EDGE,"E318");Q4=makeQuery(id+"F0.imprint","IMPRINT",FACE,{"disambiguationData":[TD([[makeQuery(id+"F0.imprint","IMPRINT",EDGE,{"derivedFrom":subQ1}),-1.0]])]});}
            var Q5;
            {var subQ1=sQuery(id+"F0.wireOp",EDGE,"E424");Q5=makeQuery(id+"F0.imprint","IMPRINT",FACE,{"disambiguationData":[TD([[makeQuery(id+"F0.imprint","IMPRINT",EDGE,{"derivedFrom":subQ1}),-1.0]])]});}
            var Q6;
            {var subQ2=sQuery(id+"F0.wireOp",EDGE,"E2508");Q6=makeQuery(id+"F0.imprint","IMPRINT",FACE,{"disambiguationData":[TD([[makeQuery(id+"F0.imprint","IMPRINT",EDGE,{"derivedFrom":subQ2}),-1.0]])]});}
            var Q7;
            {var subQ2=sQuery(id+"F0.wireOp",EDGE,"E2614");Q7=makeQuery(id+"F0.imprint","IMPRINT",FACE,{"disambiguationData":[TD([[makeQuery(id+"F0.imprint","IMPRINT",EDGE,{"derivedFrom":subQ2}),-1.0]])]});}
            var Q8;
            {var subQ2=sQuery(id+"F0.wireOp",EDGE,"E1056");Q8=makeQuery(id+"F0.imprint","IMPRINT",FACE,{"disambiguationData":[TD([[makeQuery(id+"F0.imprint","IMPRINT",EDGE,{"derivedFrom":subQ2}),-1.0]])]});}
            var Q9;
            {var subQ1=sQuery(id+"F0.wireOp",EDGE,"E950");Q9=makeQuery(id+"F0.imprint","IMPRINT",FACE,{"disambiguationData":[TD([[makeQuery(id+"F0.imprint","IMPRINT",EDGE,{"derivedFrom":subQ1}),-1.0]])]});}
            var Q10;
            {var subQ2=sQuery(id+"F0.wireOp",EDGE,"E1162");Q10=makeQuery(id+"F0.imprint","IMPRINT",FACE,{"disambiguationData":[TD([[makeQuery(id+"F0.imprint","IMPRINT",EDGE,{"derivedFrom":subQ2}),-1.0]])]});}
            var Q11;
            {var subQ1=sQuery(id+"F0.wireOp",EDGE,"E844");Q11=makeQuery(id+"F0.imprint","IMPRINT",FACE,{"disambiguationData":[TD([[makeQuery(id+"F0.imprint","IMPRINT",EDGE,{"derivedFrom":subQ1}),-1.0]])]});}
            var Q12;
            {var subQ1=sQuery(id+"F0.wireOp",EDGE,"E738");Q12=makeQuery(id+"F0.imprint","IMPRINT",FACE,{"disambiguationData":[TD([[makeQuery(id+"F0.imprint","IMPRINT",EDGE,{"derivedFrom":subQ1}),-1.0]])]});}
            var Q13;
            {var subQ3=sQuery(id+"F0.wireOp",EDGE,"E636");Q13=makeQuery(id+"F0.imprint","IMPRINT",FACE,{"disambiguationData":[TD([[makeQuery(id+"F0.imprint","IMPRINT",EDGE,{"derivedFrom":subQ3}),-1.0]])]});}
            var Q14;
            {var subQ1=sQuery(id+"F0.wireOp",EDGE,"E1476");Q14=makeQuery(id+"F0.imprint","IMPRINT",FACE,{"disambiguationData":[TD([[makeQuery(id+"F0.imprint","IMPRINT",EDGE,{"derivedFrom":subQ1}),-1.0]])]});}
            var Q15;
            {var subQ2=sQuery(id+"F0.wireOp",EDGE,"E1794");Q15=makeQuery(id+"F0.imprint","IMPRINT",FACE,{"disambiguationData":[TD([[makeQuery(id+"F0.imprint","IMPRINT",EDGE,{"derivedFrom":subQ2}),-1.0]])]});}
            var Q16;
            {var subQ1=sQuery(id+"F0.wireOp",EDGE,"E1582");Q16=makeQuery(id+"F0.imprint","IMPRINT",FACE,{"disambiguationData":[TD([[makeQuery(id+"F0.imprint","IMPRINT",EDGE,{"derivedFrom":subQ1}),-1.0]])]});}
            var Q17;
            {var subQ1=sQuery(id+"F0.wireOp",EDGE,"E1688");Q17=makeQuery(id+"F0.imprint","IMPRINT",FACE,{"disambiguationData":[TD([[makeQuery(id+"F0.imprint","IMPRINT",EDGE,{"derivedFrom":subQ1}),-1.0]])]});}
            var Q18;
            {var subQ2=sQuery(id+"F0.wireOp",EDGE,"E2720");Q18=makeQuery(id+"F0.imprint","IMPRINT",FACE,{"disambiguationData":[TD([[makeQuery(id+"F0.imprint","IMPRINT",EDGE,{"derivedFrom":subQ2}),-1.0]])]});}
            var Q19;
            {var subQ2=sQuery(id+"F0.wireOp",EDGE,"E2822");Q19=makeQuery(id+"F0.imprint","IMPRINT",FACE,{"disambiguationData":[TD([[makeQuery(id+"F0.imprint","IMPRINT",EDGE,{"derivedFrom":subQ2}),-1.0]])]});}
            var Q20;
            {var subQ1=sQuery(id+"F0.wireOp",EDGE,"E2300");Q20=makeQuery(id+"F0.imprint","IMPRINT",FACE,{"disambiguationData":[TD([[makeQuery(id+"F0.imprint","IMPRINT",EDGE,{"derivedFrom":subQ1}),-1.0]])]});}
            var Q21;
            {var subQ1=sQuery(id+"F0.wireOp",EDGE,"E2198");Q21=makeQuery(id+"F0.imprint","IMPRINT",FACE,{"disambiguationData":[TD([[makeQuery(id+"F0.imprint","IMPRINT",EDGE,{"derivedFrom":subQ1}),-1.0]])]});}
            var Q22;
            {var subQ2=sQuery(id+"F0.wireOp",EDGE,"E2402");Q22=makeQuery(id+"F0.imprint","IMPRINT",FACE,{"disambiguationData":[TD([[makeQuery(id+"F0.imprint","IMPRINT",EDGE,{"derivedFrom":subQ2}),-1.0]])]});}
            var Q23;
            {var subQ1=sQuery(id+"F0.wireOp",EDGE,"E2096");Q23=makeQuery(id+"F0.imprint","IMPRINT",FACE,{"disambiguationData":[TD([[makeQuery(id+"F0.imprint","IMPRINT",EDGE,{"derivedFrom":subQ1}),-1.0]])]});}
            var Q24;
            {var subQ1=sQuery(id+"F0.wireOp",EDGE,"E1994");Q24=makeQuery(id+"F0.imprint","IMPRINT",FACE,{"disambiguationData":[TD([[makeQuery(id+"F0.imprint","IMPRINT",EDGE,{"derivedFrom":subQ1}),-1.0]])]});}
            var Q25;
            {var subQ3=sQuery(id+"F0.wireOp",EDGE,"E1896");Q25=makeQuery(id+"F0.imprint","IMPRINT",FACE,{"disambiguationData":[TD([[makeQuery(id+"F0.imprint","IMPRINT",EDGE,{"derivedFrom":subQ3}),-1.0]])]});}
            var Q26;
            {var subQ1=sQuery(id+"F0.wireOp",EDGE,"E1370");Q26=makeQuery(id+"F0.imprint","IMPRINT",FACE,{"disambiguationData":[TD([[makeQuery(id+"F0.imprint","IMPRINT",EDGE,{"derivedFrom":subQ1}),-1.0]])]});}
            var Q27;
            {var subQ3=sQuery(id+"F0.wireOp",EDGE,"E1268");Q27=makeQuery(id+"F0.imprint","IMPRINT",FACE,{"disambiguationData":[TD([[makeQuery(id+"F0.imprint","IMPRINT",EDGE,{"derivedFrom":subQ3}),-1.0]])]});}
            extrude(context, id + "F1", {"entities" : qUnion([Q0, Q1, Q2, Q3, Q4, Q5, Q6, Q7, Q8, Q9, Q10, Q11, Q12, Q13, Q14, Q15, Q16, Q17, Q18, Q19, Q20, Q21, Q22, Q23, Q24, Q25, Q26, Q27]), "depth" : 6 * mm, "offsetDistance" : 25 * mm});
        }
        {
            var Q0;
            {var subQ1=sQuery(id+"F0.wireOp",EDGE,"E4");Q0=makeQuery(id+"F0.imprint","IMPRINT",FACE,{"disambiguationData":[TD([[makeQuery(id+"F0.imprint","IMPRINT",EDGE,{"derivedFrom":subQ1}),1.0]])]});}
            var Q1;
            {var subQ1=sQuery(id+"F0.wireOp",EDGE,"E106");Q1=makeQuery(id+"F0.imprint","IMPRINT",FACE,{"disambiguationData":[TD([[makeQuery(id+"F0.imprint","IMPRINT",EDGE,{"derivedFrom":subQ1}),1.0]])]});}
            var Q2;
            {var subQ1=sQuery(id+"F0.wireOp",EDGE,"E212");Q2=makeQuery(id+"F0.imprint","IMPRINT",FACE,{"disambiguationData":[TD([[makeQuery(id+"F0.imprint","IMPRINT",EDGE,{"derivedFrom":subQ1}),1.0]])]});}
            var Q3;
            {var subQ1=sQuery(id+"F0.wireOp",EDGE,"E530");Q3=makeQuery(id+"F0.imprint","IMPRINT",FACE,{"disambiguationData":[TD([[makeQuery(id+"F0.imprint","IMPRINT",EDGE,{"derivedFrom":subQ1}),1.0]])]});}
            var Q4;
            {var subQ1=sQuery(id+"F0.wireOp",EDGE,"E318");Q4=makeQuery(id+"F0.imprint","IMPRINT",FACE,{"disambiguationData":[TD([[makeQuery(id+"F0.imprint","IMPRINT",EDGE,{"derivedFrom":subQ1}),1.0]])]});}
            var Q5;
            {var subQ1=sQuery(id+"F0.wireOp",EDGE,"E424");Q5=makeQuery(id+"F0.imprint","IMPRINT",FACE,{"disambiguationData":[TD([[makeQuery(id+"F0.imprint","IMPRINT",EDGE,{"derivedFrom":subQ1}),1.0]])]});}
            var Q6;
            {var subQ1=sQuery(id+"F0.wireOp",EDGE,"E2508");Q6=makeQuery(id+"F0.imprint","IMPRINT",FACE,{"disambiguationData":[TD([[makeQuery(id+"F0.imprint","IMPRINT",EDGE,{"derivedFrom":subQ1}),1.0]])]});}
            var Q7;
            {var subQ1=sQuery(id+"F0.wireOp",EDGE,"E636");Q7=makeQuery(id+"F0.imprint","IMPRINT",FACE,{"disambiguationData":[TD([[makeQuery(id+"F0.imprint","IMPRINT",EDGE,{"derivedFrom":subQ1}),1.0]])]});}
            var Q8;
            {var subQ4=sQuery(id+"F0.wireOp",EDGE,"E738");Q8=makeQuery(id+"F0.imprint","IMPRINT",FACE,{"disambiguationData":[TD([[makeQuery(id+"F0.imprint","IMPRINT",EDGE,{"derivedFrom":subQ4}),1.0]])]});}
            var Q9;
            {var subQ4=sQuery(id+"F0.wireOp",EDGE,"E844");Q9=makeQuery(id+"F0.imprint","IMPRINT",FACE,{"disambiguationData":[TD([[makeQuery(id+"F0.imprint","IMPRINT",EDGE,{"derivedFrom":subQ4}),1.0]])]});}
            var Q10;
            {var subQ5=sQuery(id+"F0.wireOp",EDGE,"E1162");Q10=makeQuery(id+"F0.imprint","IMPRINT",FACE,{"disambiguationData":[TD([[makeQuery(id+"F0.imprint","IMPRINT",EDGE,{"derivedFrom":subQ5}),1.0]])]});}
            var Q11;
            {var subQ4=sQuery(id+"F0.wireOp",EDGE,"E950");Q11=makeQuery(id+"F0.imprint","IMPRINT",FACE,{"disambiguationData":[TD([[makeQuery(id+"F0.imprint","IMPRINT",EDGE,{"derivedFrom":subQ4}),1.0]])]});}
            var Q12;
            {var subQ4=sQuery(id+"F0.wireOp",EDGE,"E1056");Q12=makeQuery(id+"F0.imprint","IMPRINT",FACE,{"disambiguationData":[TD([[makeQuery(id+"F0.imprint","IMPRINT",EDGE,{"derivedFrom":subQ4}),1.0]])]});}
            var Q13;
            {var subQ1=sQuery(id+"F0.wireOp",EDGE,"E1268");Q13=makeQuery(id+"F0.imprint","IMPRINT",FACE,{"disambiguationData":[TD([[makeQuery(id+"F0.imprint","IMPRINT",EDGE,{"derivedFrom":subQ1}),1.0]])]});}
            var Q14;
            {var subQ4=sQuery(id+"F0.wireOp",EDGE,"E1370");Q14=makeQuery(id+"F0.imprint","IMPRINT",FACE,{"disambiguationData":[TD([[makeQuery(id+"F0.imprint","IMPRINT",EDGE,{"derivedFrom":subQ4}),1.0]])]});}
            var Q15;
            {var subQ4=sQuery(id+"F0.wireOp",EDGE,"E1476");Q15=makeQuery(id+"F0.imprint","IMPRINT",FACE,{"disambiguationData":[TD([[makeQuery(id+"F0.imprint","IMPRINT",EDGE,{"derivedFrom":subQ4}),1.0]])]});}
            var Q16;
            {var subQ5=sQuery(id+"F0.wireOp",EDGE,"E1794");Q16=makeQuery(id+"F0.imprint","IMPRINT",FACE,{"disambiguationData":[TD([[makeQuery(id+"F0.imprint","IMPRINT",EDGE,{"derivedFrom":subQ5}),1.0]])]});}
            var Q17;
            {var subQ4=sQuery(id+"F0.wireOp",EDGE,"E1582");Q17=makeQuery(id+"F0.imprint","IMPRINT",FACE,{"disambiguationData":[TD([[makeQuery(id+"F0.imprint","IMPRINT",EDGE,{"derivedFrom":subQ4}),1.0]])]});}
            var Q18;
            {var subQ1=sQuery(id+"F0.wireOp",EDGE,"E2720");Q18=makeQuery(id+"F0.imprint","IMPRINT",FACE,{"disambiguationData":[TD([[makeQuery(id+"F0.imprint","IMPRINT",EDGE,{"derivedFrom":subQ1}),1.0]])]});}
            var Q19;
            {var subQ1=sQuery(id+"F0.wireOp",EDGE,"E1896");Q19=makeQuery(id+"F0.imprint","IMPRINT",FACE,{"disambiguationData":[TD([[makeQuery(id+"F0.imprint","IMPRINT",EDGE,{"derivedFrom":subQ1}),1.0]])]});}
            var Q20;
            {var subQ4=sQuery(id+"F0.wireOp",EDGE,"E1994");Q20=makeQuery(id+"F0.imprint","IMPRINT",FACE,{"disambiguationData":[TD([[makeQuery(id+"F0.imprint","IMPRINT",EDGE,{"derivedFrom":subQ4}),1.0]])]});}
            var Q21;
            {var subQ4=sQuery(id+"F0.wireOp",EDGE,"E2096");Q21=makeQuery(id+"F0.imprint","IMPRINT",FACE,{"disambiguationData":[TD([[makeQuery(id+"F0.imprint","IMPRINT",EDGE,{"derivedFrom":subQ4}),1.0]])]});}
            var Q22;
            {var subQ5=sQuery(id+"F0.wireOp",EDGE,"E2402");Q22=makeQuery(id+"F0.imprint","IMPRINT",FACE,{"disambiguationData":[TD([[makeQuery(id+"F0.imprint","IMPRINT",EDGE,{"derivedFrom":subQ5}),1.0]])]});}
            var Q23;
            {var subQ4=sQuery(id+"F0.wireOp",EDGE,"E2198");Q23=makeQuery(id+"F0.imprint","IMPRINT",FACE,{"disambiguationData":[TD([[makeQuery(id+"F0.imprint","IMPRINT",EDGE,{"derivedFrom":subQ4}),1.0]])]});}
            var Q24;
            {var subQ4=sQuery(id+"F0.wireOp",EDGE,"E2300");Q24=makeQuery(id+"F0.imprint","IMPRINT",FACE,{"disambiguationData":[TD([[makeQuery(id+"F0.imprint","IMPRINT",EDGE,{"derivedFrom":subQ4}),1.0]])]});}
            var Q25;
            {var subQ1=sQuery(id+"F0.wireOp",EDGE,"E2822");Q25=makeQuery(id+"F0.imprint","IMPRINT",FACE,{"disambiguationData":[TD([[makeQuery(id+"F0.imprint","IMPRINT",EDGE,{"derivedFrom":subQ1}),1.0]])]});}
            var Q26;
            {var subQ4=sQuery(id+"F0.wireOp",EDGE,"E1688");Q26=makeQuery(id+"F0.imprint","IMPRINT",FACE,{"disambiguationData":[TD([[makeQuery(id+"F0.imprint","IMPRINT",EDGE,{"derivedFrom":subQ4}),1.0]])]});}
            var Q27;
            {var subQ1=sQuery(id+"F0.wireOp",EDGE,"E2614");Q27=makeQuery(id+"F0.imprint","IMPRINT",FACE,{"disambiguationData":[TD([[makeQuery(id+"F0.imprint","IMPRINT",EDGE,{"derivedFrom":subQ1}),1.0]])]});}
            extrude(context, id + "F2", {"entities" : qUnion([Q0, Q1, Q2, Q3, Q4, Q5, Q6, Q7, Q8, Q9, Q10, Q11, Q12, Q13, Q14, Q15, Q16, Q17, Q18, Q19, Q20, Q21, Q22, Q23, Q24, Q25, Q26, Q27]), "depth" : 6 * mm, "offsetDistance" : 25 * mm});
        }
        {
            var Q0;
            Q0=makeQuery(id+"F0.imprint","IMPRINT",FACE,{"disambiguationData":[TD([[makeQuery(id+"F0.imprint","IMPRINT",EDGE,{"derivedFrom":sQuery(id+"F0.wireOp",EDGE,"E17")}),1.0]])]});
            var Q1;
            Q1=makeQuery(id+"F0.imprint","IMPRINT",FACE,{"disambiguationData":[TD([[makeQuery(id+"F0.imprint","IMPRINT",EDGE,{"derivedFrom":sQuery(id+"F0.wireOp",EDGE,"E8")}),1.0]])]});
            var Q2;
            Q2=makeQuery(id+"F0.imprint","IMPRINT",FACE,{"disambiguationData":[TD([[makeQuery(id+"F0.imprint","IMPRINT",EDGE,{"derivedFrom":sQuery(id+"F0.wireOp",EDGE,"E119")}),1.0]])]});
            var Q3;
            Q3=makeQuery(id+"F0.imprint","IMPRINT",FACE,{"disambiguationData":[TD([[makeQuery(id+"F0.imprint","IMPRINT",EDGE,{"derivedFrom":sQuery(id+"F0.wireOp",EDGE,"E110")}),1.0]])]});
            var Q4;
            Q4=makeQuery(id+"F0.imprint","IMPRINT",FACE,{"disambiguationData":[TD([[makeQuery(id+"F0.imprint","IMPRINT",EDGE,{"derivedFrom":sQuery(id+"F0.wireOp",EDGE,"E225")}),1.0]])]});
            var Q5;
            Q5=makeQuery(id+"F0.imprint","IMPRINT",FACE,{"disambiguationData":[TD([[makeQuery(id+"F0.imprint","IMPRINT",EDGE,{"derivedFrom":sQuery(id+"F0.wireOp",EDGE,"E216")}),1.0]])]});
            var Q6;
            Q6=makeQuery(id+"F0.imprint","IMPRINT",FACE,{"disambiguationData":[TD([[makeQuery(id+"F0.imprint","IMPRINT",EDGE,{"derivedFrom":sQuery(id+"F0.wireOp",EDGE,"E543")}),1.0]])]});
            var Q7;
            Q7=makeQuery(id+"F0.imprint","IMPRINT",FACE,{"disambiguationData":[TD([[makeQuery(id+"F0.imprint","IMPRINT",EDGE,{"derivedFrom":sQuery(id+"F0.wireOp",EDGE,"E649")}),1.0]])]});
            var Q8;
            Q8=makeQuery(id+"F0.imprint","IMPRINT",FACE,{"disambiguationData":[TD([[makeQuery(id+"F0.imprint","IMPRINT",EDGE,{"derivedFrom":sQuery(id+"F0.wireOp",EDGE,"E640")}),1.0]])]});
            var Q9;
            Q9=makeQuery(id+"F0.imprint","IMPRINT",FACE,{"disambiguationData":[TD([[makeQuery(id+"F0.imprint","IMPRINT",EDGE,{"derivedFrom":sQuery(id+"F0.wireOp",EDGE,"E751")}),1.0]])]});
            var Q10;
            Q10=makeQuery(id+"F0.imprint","IMPRINT",FACE,{"disambiguationData":[TD([[makeQuery(id+"F0.imprint","IMPRINT",EDGE,{"derivedFrom":sQuery(id+"F0.wireOp",EDGE,"E742")}),1.0]])]});
            var Q11;
            Q11=makeQuery(id+"F0.imprint","IMPRINT",FACE,{"disambiguationData":[TD([[makeQuery(id+"F0.imprint","IMPRINT",EDGE,{"derivedFrom":sQuery(id+"F0.wireOp",EDGE,"E848")}),1.0]])]});
            var Q12;
            Q12=makeQuery(id+"F0.imprint","IMPRINT",FACE,{"disambiguationData":[TD([[makeQuery(id+"F0.imprint","IMPRINT",EDGE,{"derivedFrom":sQuery(id+"F0.wireOp",EDGE,"E857")}),1.0]])]});
            var Q13;
            Q13=makeQuery(id+"F0.imprint","IMPRINT",FACE,{"disambiguationData":[TD([[makeQuery(id+"F0.imprint","IMPRINT",EDGE,{"derivedFrom":sQuery(id+"F0.wireOp",EDGE,"E534")}),1.0]])]});
            var Q14;
            Q14=makeQuery(id+"F0.imprint","IMPRINT",FACE,{"disambiguationData":[TD([[makeQuery(id+"F0.imprint","IMPRINT",EDGE,{"derivedFrom":sQuery(id+"F0.wireOp",EDGE,"E1175")}),1.0]])]});
            var Q15;
            Q15=makeQuery(id+"F0.imprint","IMPRINT",FACE,{"disambiguationData":[TD([[makeQuery(id+"F0.imprint","IMPRINT",EDGE,{"derivedFrom":sQuery(id+"F0.wireOp",EDGE,"E1166")}),1.0]])]});
            var Q16;
            Q16=makeQuery(id+"F0.imprint","IMPRINT",FACE,{"disambiguationData":[TD([[makeQuery(id+"F0.imprint","IMPRINT",EDGE,{"derivedFrom":sQuery(id+"F0.wireOp",EDGE,"E963")}),1.0]])]});
            var Q17;
            Q17=makeQuery(id+"F0.imprint","IMPRINT",FACE,{"disambiguationData":[TD([[makeQuery(id+"F0.imprint","IMPRINT",EDGE,{"derivedFrom":sQuery(id+"F0.wireOp",EDGE,"E331")}),1.0]])]});
            var Q18;
            Q18=makeQuery(id+"F0.imprint","IMPRINT",FACE,{"disambiguationData":[TD([[makeQuery(id+"F0.imprint","IMPRINT",EDGE,{"derivedFrom":sQuery(id+"F0.wireOp",EDGE,"E322")}),1.0]])]});
            var Q19;
            Q19=makeQuery(id+"F0.imprint","IMPRINT",FACE,{"disambiguationData":[TD([[makeQuery(id+"F0.imprint","IMPRINT",EDGE,{"derivedFrom":sQuery(id+"F0.wireOp",EDGE,"E954")}),1.0]])]});
            var Q20;
            Q20=makeQuery(id+"F0.imprint","IMPRINT",FACE,{"disambiguationData":[TD([[makeQuery(id+"F0.imprint","IMPRINT",EDGE,{"derivedFrom":sQuery(id+"F0.wireOp",EDGE,"E437")}),1.0]])]});
            var Q21;
            Q21=makeQuery(id+"F0.imprint","IMPRINT",FACE,{"disambiguationData":[TD([[makeQuery(id+"F0.imprint","IMPRINT",EDGE,{"derivedFrom":sQuery(id+"F0.wireOp",EDGE,"E428")}),1.0]])]});
            var Q22;
            Q22=makeQuery(id+"F0.imprint","IMPRINT",FACE,{"disambiguationData":[TD([[makeQuery(id+"F0.imprint","IMPRINT",EDGE,{"derivedFrom":sQuery(id+"F0.wireOp",EDGE,"E1069")}),1.0]])]});
            var Q23;
            Q23=makeQuery(id+"F0.imprint","IMPRINT",FACE,{"disambiguationData":[TD([[makeQuery(id+"F0.imprint","IMPRINT",EDGE,{"derivedFrom":sQuery(id+"F0.wireOp",EDGE,"E1060")}),1.0]])]});
            var Q24;
            Q24=makeQuery(id+"F0.imprint","IMPRINT",FACE,{"disambiguationData":[TD([[makeQuery(id+"F0.imprint","IMPRINT",EDGE,{"derivedFrom":sQuery(id+"F0.wireOp",EDGE,"E2521")}),1.0]])]});
            var Q25;
            Q25=makeQuery(id+"F0.imprint","IMPRINT",FACE,{"disambiguationData":[TD([[makeQuery(id+"F0.imprint","IMPRINT",EDGE,{"derivedFrom":sQuery(id+"F0.wireOp",EDGE,"E2512")}),1.0]])]});
            var Q26;
            Q26=makeQuery(id+"F0.imprint","IMPRINT",FACE,{"disambiguationData":[TD([[makeQuery(id+"F0.imprint","IMPRINT",EDGE,{"derivedFrom":sQuery(id+"F0.wireOp",EDGE,"E2627")}),1.0]])]});
            var Q27;
            Q27=makeQuery(id+"F0.imprint","IMPRINT",FACE,{"disambiguationData":[TD([[makeQuery(id+"F0.imprint","IMPRINT",EDGE,{"derivedFrom":sQuery(id+"F0.wireOp",EDGE,"E2618")}),1.0]])]});
            var Q28;
            Q28=makeQuery(id+"F0.imprint","IMPRINT",FACE,{"disambiguationData":[TD([[makeQuery(id+"F0.imprint","IMPRINT",EDGE,{"derivedFrom":sQuery(id+"F0.wireOp",EDGE,"E1272")}),1.0]])]});
            var Q29;
            Q29=makeQuery(id+"F0.imprint","IMPRINT",FACE,{"disambiguationData":[TD([[makeQuery(id+"F0.imprint","IMPRINT",EDGE,{"derivedFrom":sQuery(id+"F0.wireOp",EDGE,"E1383")}),1.0]])]});
            var Q30;
            Q30=makeQuery(id+"F0.imprint","IMPRINT",FACE,{"disambiguationData":[TD([[makeQuery(id+"F0.imprint","IMPRINT",EDGE,{"derivedFrom":sQuery(id+"F0.wireOp",EDGE,"E1374")}),1.0]])]});
            var Q31;
            Q31=makeQuery(id+"F0.imprint","IMPRINT",FACE,{"disambiguationData":[TD([[makeQuery(id+"F0.imprint","IMPRINT",EDGE,{"derivedFrom":sQuery(id+"F0.wireOp",EDGE,"E1489")}),1.0]])]});
            var Q32;
            Q32=makeQuery(id+"F0.imprint","IMPRINT",FACE,{"disambiguationData":[TD([[makeQuery(id+"F0.imprint","IMPRINT",EDGE,{"derivedFrom":sQuery(id+"F0.wireOp",EDGE,"E1480")}),1.0]])]});
            var Q33;
            Q33=makeQuery(id+"F0.imprint","IMPRINT",FACE,{"disambiguationData":[TD([[makeQuery(id+"F0.imprint","IMPRINT",EDGE,{"derivedFrom":sQuery(id+"F0.wireOp",EDGE,"E1807")}),1.0]])]});
            var Q34;
            Q34=makeQuery(id+"F0.imprint","IMPRINT",FACE,{"disambiguationData":[TD([[makeQuery(id+"F0.imprint","IMPRINT",EDGE,{"derivedFrom":sQuery(id+"F0.wireOp",EDGE,"E1798")}),1.0]])]});
            var Q35;
            Q35=makeQuery(id+"F0.imprint","IMPRINT",FACE,{"disambiguationData":[TD([[makeQuery(id+"F0.imprint","IMPRINT",EDGE,{"derivedFrom":sQuery(id+"F0.wireOp",EDGE,"E1595")}),1.0]])]});
            var Q36;
            Q36=makeQuery(id+"F0.imprint","IMPRINT",FACE,{"disambiguationData":[TD([[makeQuery(id+"F0.imprint","IMPRINT",EDGE,{"derivedFrom":sQuery(id+"F0.wireOp",EDGE,"E1586")}),1.0]])]});
            var Q37;
            Q37=makeQuery(id+"F0.imprint","IMPRINT",FACE,{"disambiguationData":[TD([[makeQuery(id+"F0.imprint","IMPRINT",EDGE,{"derivedFrom":sQuery(id+"F0.wireOp",EDGE,"E1909")}),1.0]])]});
            var Q38;
            Q38=makeQuery(id+"F0.imprint","IMPRINT",FACE,{"disambiguationData":[TD([[makeQuery(id+"F0.imprint","IMPRINT",EDGE,{"derivedFrom":sQuery(id+"F0.wireOp",EDGE,"E1900")}),1.0]])]});
            var Q39;
            Q39=makeQuery(id+"F0.imprint","IMPRINT",FACE,{"disambiguationData":[TD([[makeQuery(id+"F0.imprint","IMPRINT",EDGE,{"derivedFrom":sQuery(id+"F0.wireOp",EDGE,"E1998")}),1.0]])]});
            var Q40;
            Q40=makeQuery(id+"F0.imprint","IMPRINT",FACE,{"disambiguationData":[TD([[makeQuery(id+"F0.imprint","IMPRINT",EDGE,{"derivedFrom":sQuery(id+"F0.wireOp",EDGE,"E1281")}),1.0]])]});
            var Q41;
            Q41=makeQuery(id+"F0.imprint","IMPRINT",FACE,{"disambiguationData":[TD([[makeQuery(id+"F0.imprint","IMPRINT",EDGE,{"derivedFrom":sQuery(id+"F0.wireOp",EDGE,"E2007")}),1.0]])]});
            var Q42;
            Q42=makeQuery(id+"F0.imprint","IMPRINT",FACE,{"disambiguationData":[TD([[makeQuery(id+"F0.imprint","IMPRINT",EDGE,{"derivedFrom":sQuery(id+"F0.wireOp",EDGE,"E2109")}),1.0]])]});
            var Q43;
            Q43=makeQuery(id+"F0.imprint","IMPRINT",FACE,{"disambiguationData":[TD([[makeQuery(id+"F0.imprint","IMPRINT",EDGE,{"derivedFrom":sQuery(id+"F0.wireOp",EDGE,"E2100")}),1.0]])]});
            var Q44;
            Q44=makeQuery(id+"F0.imprint","IMPRINT",FACE,{"disambiguationData":[TD([[makeQuery(id+"F0.imprint","IMPRINT",EDGE,{"derivedFrom":sQuery(id+"F0.wireOp",EDGE,"E2415")}),1.0]])]});
            var Q45;
            Q45=makeQuery(id+"F0.imprint","IMPRINT",FACE,{"disambiguationData":[TD([[makeQuery(id+"F0.imprint","IMPRINT",EDGE,{"derivedFrom":sQuery(id+"F0.wireOp",EDGE,"E2406")}),1.0]])]});
            var Q46;
            Q46=makeQuery(id+"F0.imprint","IMPRINT",FACE,{"disambiguationData":[TD([[makeQuery(id+"F0.imprint","IMPRINT",EDGE,{"derivedFrom":sQuery(id+"F0.wireOp",EDGE,"E2211")}),1.0]])]});
            var Q47;
            Q47=makeQuery(id+"F0.imprint","IMPRINT",FACE,{"disambiguationData":[TD([[makeQuery(id+"F0.imprint","IMPRINT",EDGE,{"derivedFrom":sQuery(id+"F0.wireOp",EDGE,"E2202")}),1.0]])]});
            var Q48;
            Q48=makeQuery(id+"F0.imprint","IMPRINT",FACE,{"disambiguationData":[TD([[makeQuery(id+"F0.imprint","IMPRINT",EDGE,{"derivedFrom":sQuery(id+"F0.wireOp",EDGE,"E2313")}),1.0]])]});
            var Q49;
            Q49=makeQuery(id+"F0.imprint","IMPRINT",FACE,{"disambiguationData":[TD([[makeQuery(id+"F0.imprint","IMPRINT",EDGE,{"derivedFrom":sQuery(id+"F0.wireOp",EDGE,"E2304")}),1.0]])]});
            var Q50;
            Q50=makeQuery(id+"F0.imprint","IMPRINT",FACE,{"disambiguationData":[TD([[makeQuery(id+"F0.imprint","IMPRINT",EDGE,{"derivedFrom":sQuery(id+"F0.wireOp",EDGE,"E2835")}),1.0]])]});
            var Q51;
            Q51=makeQuery(id+"F0.imprint","IMPRINT",FACE,{"disambiguationData":[TD([[makeQuery(id+"F0.imprint","IMPRINT",EDGE,{"derivedFrom":sQuery(id+"F0.wireOp",EDGE,"E2826")}),1.0]])]});
            var Q52;
            Q52=makeQuery(id+"F0.imprint","IMPRINT",FACE,{"disambiguationData":[TD([[makeQuery(id+"F0.imprint","IMPRINT",EDGE,{"derivedFrom":sQuery(id+"F0.wireOp",EDGE,"E2724")}),1.0]])]});
            var Q53;
            Q53=makeQuery(id+"F0.imprint","IMPRINT",FACE,{"disambiguationData":[TD([[makeQuery(id+"F0.imprint","IMPRINT",EDGE,{"derivedFrom":sQuery(id+"F0.wireOp",EDGE,"E2733")}),1.0]])]});
            var Q54;
            Q54=makeQuery(id+"F0.imprint","IMPRINT",FACE,{"disambiguationData":[TD([[makeQuery(id+"F0.imprint","IMPRINT",EDGE,{"derivedFrom":sQuery(id+"F0.wireOp",EDGE,"E1692")}),1.0]])]});
            var Q55;
            Q55=makeQuery(id+"F0.imprint","IMPRINT",FACE,{"disambiguationData":[TD([[makeQuery(id+"F0.imprint","IMPRINT",EDGE,{"derivedFrom":sQuery(id+"F0.wireOp",EDGE,"E1701")}),1.0]])]});
            extrude(context, id + "F3", {"entities" : qUnion([Q0, Q1, Q2, Q3, Q4, Q5, Q6, Q7, Q8, Q9, Q10, Q11, Q12, Q13, Q14, Q15, Q16, Q17, Q18, Q19, Q20, Q21, Q22, Q23, Q24, Q25, Q26, Q27, Q28, Q29, Q30, Q31, Q32, Q33, Q34, Q35, Q36, Q37, Q38, Q39, Q40, Q41, Q42, Q43, Q44, Q45, Q46, Q47, Q48, Q49, Q50, Q51, Q52, Q53, Q54, Q55]), "depth" : 4 * mm, "offsetDistance" : 25 * mm});
        }
        {
            var Q0;
            Q0=makeQuery(id+"F0.imprint","IMPRINT",FACE,{"disambiguationData":[TD([[makeQuery(id+"F0.imprint","IMPRINT",EDGE,{"derivedFrom":sQuery(id+"F0.wireOp",EDGE,"E204")}),1.0]])]});
            var Q1;
            {var subQ0=sQuery(id+"F0.wireOp",EDGE,"E1");Q1=makeQuery(id+"F0.imprint","IMPRINT",FACE,{"disambiguationData":[TD([[makeQuery(id+"F0.imprint","IMPRINT",EDGE,{"derivedFrom":subQ0}),1.0]])]});}
            var Q2;
            Q2=makeQuery(id+"F0.imprint","IMPRINT",FACE,{"disambiguationData":[TD([[makeQuery(id+"F0.imprint","IMPRINT",EDGE,{"derivedFrom":sQuery(id+"F0.wireOp",EDGE,"E310")}),1.0]])]});
            var Q3;
            {var subQ0=sQuery(id+"F0.wireOp",EDGE,"E103");Q3=makeQuery(id+"F0.imprint","IMPRINT",FACE,{"disambiguationData":[TD([[makeQuery(id+"F0.imprint","IMPRINT",EDGE,{"derivedFrom":subQ0}),1.0]])]});}
            var Q4;
            {var subQ0=sQuery(id+"F0.wireOp",EDGE,"E209");Q4=makeQuery(id+"F0.imprint","IMPRINT",FACE,{"disambiguationData":[TD([[makeQuery(id+"F0.imprint","IMPRINT",EDGE,{"derivedFrom":subQ0}),1.0]])]});}
            var Q5;
            Q5=makeQuery(id+"F0.imprint","IMPRINT",FACE,{"disambiguationData":[TD([[makeQuery(id+"F0.imprint","IMPRINT",EDGE,{"derivedFrom":sQuery(id+"F0.wireOp",EDGE,"E628")}),1.0]])]});
            var Q6;
            {var subQ0=sQuery(id+"F0.wireOp",EDGE,"E416");Q6=makeQuery(id+"F0.imprint","IMPRINT",FACE,{"disambiguationData":[TD([[makeQuery(id+"F0.imprint","IMPRINT",EDGE,{"derivedFrom":subQ0}),1.0]])]});}
            var Q7;
            {var subQ0=sQuery(id+"F0.wireOp",EDGE,"E527");Q7=makeQuery(id+"F0.imprint","IMPRINT",FACE,{"disambiguationData":[TD([[makeQuery(id+"F0.imprint","IMPRINT",EDGE,{"derivedFrom":subQ0}),1.0]])]});}
            var Q8;
            Q8=makeQuery(id+"F0.imprint","IMPRINT",FACE,{"disambiguationData":[TD([[makeQuery(id+"F0.imprint","IMPRINT",EDGE,{"derivedFrom":sQuery(id+"F0.wireOp",EDGE,"E522")}),1.0]])]});
            var Q9;
            {var subQ0=sQuery(id+"F0.wireOp",EDGE,"E421");Q9=makeQuery(id+"F0.imprint","IMPRINT",FACE,{"disambiguationData":[TD([[makeQuery(id+"F0.imprint","IMPRINT",EDGE,{"derivedFrom":subQ0}),1.0]])]});}
            var Q10;
            {var subQ0=sQuery(id+"F0.wireOp",EDGE,"E2505");Q10=makeQuery(id+"F0.imprint","IMPRINT",FACE,{"disambiguationData":[TD([[makeQuery(id+"F0.imprint","IMPRINT",EDGE,{"derivedFrom":subQ0}),1.0]])]});}
            var Q11;
            Q11=makeQuery(id+"F0.imprint","IMPRINT",FACE,{"disambiguationData":[TD([[makeQuery(id+"F0.imprint","IMPRINT",EDGE,{"derivedFrom":sQuery(id+"F0.wireOp",EDGE,"E2606")}),1.0]])]});
            var Q12;
            {var subQ0=sQuery(id+"F0.wireOp",EDGE,"E315");Q12=makeQuery(id+"F0.imprint","IMPRINT",FACE,{"disambiguationData":[TD([[makeQuery(id+"F0.imprint","IMPRINT",EDGE,{"derivedFrom":subQ0}),1.0]])]});}
            var Q13;
            Q13=makeQuery(id+"F0.imprint","IMPRINT",FACE,{"disambiguationData":[TD([[makeQuery(id+"F0.imprint","IMPRINT",EDGE,{"derivedFrom":sQuery(id+"F0.wireOp",EDGE,"E836")}),1.0]])]});
            var Q14;
            {var subQ0=sQuery(id+"F0.wireOp",EDGE,"E633");Q14=makeQuery(id+"F0.imprint","IMPRINT",FACE,{"disambiguationData":[TD([[makeQuery(id+"F0.imprint","IMPRINT",EDGE,{"derivedFrom":subQ0}),1.0]])]});}
            var Q15;
            {var subQ0=sQuery(id+"F0.wireOp",EDGE,"E735");Q15=makeQuery(id+"F0.imprint","IMPRINT",FACE,{"disambiguationData":[TD([[makeQuery(id+"F0.imprint","IMPRINT",EDGE,{"derivedFrom":subQ0}),1.0]])]});}
            var Q16;
            Q16=makeQuery(id+"F0.imprint","IMPRINT",FACE,{"disambiguationData":[TD([[makeQuery(id+"F0.imprint","IMPRINT",EDGE,{"derivedFrom":sQuery(id+"F0.wireOp",EDGE,"E1260")}),1.0]])]});
            var Q17;
            {var subQ0=sQuery(id+"F0.wireOp",EDGE,"E1048");Q17=makeQuery(id+"F0.imprint","IMPRINT",FACE,{"disambiguationData":[TD([[makeQuery(id+"F0.imprint","IMPRINT",EDGE,{"derivedFrom":subQ0}),1.0]])]});}
            var Q18;
            Q18=makeQuery(id+"F0.imprint","IMPRINT",FACE,{"disambiguationData":[TD([[makeQuery(id+"F0.imprint","IMPRINT",EDGE,{"derivedFrom":sQuery(id+"F0.wireOp",EDGE,"E1154")}),1.0]])]});
            var Q19;
            Q19=makeQuery(id+"F0.imprint","IMPRINT",FACE,{"disambiguationData":[TD([[makeQuery(id+"F0.imprint","IMPRINT",EDGE,{"derivedFrom":sQuery(id+"F0.wireOp",EDGE,"E2712")}),1.0]])]});
            var Q20;
            {var subQ0=sQuery(id+"F0.wireOp",EDGE,"E841");Q20=makeQuery(id+"F0.imprint","IMPRINT",FACE,{"disambiguationData":[TD([[makeQuery(id+"F0.imprint","IMPRINT",EDGE,{"derivedFrom":subQ0}),1.0]])]});}
            var Q21;
            Q21=makeQuery(id+"F0.imprint","IMPRINT",FACE,{"disambiguationData":[TD([[makeQuery(id+"F0.imprint","IMPRINT",EDGE,{"derivedFrom":sQuery(id+"F0.wireOp",EDGE,"E942")}),1.0]])]});
            var Q22;
            {var subQ0=sQuery(id+"F0.wireOp",EDGE,"E947");Q22=makeQuery(id+"F0.imprint","IMPRINT",FACE,{"disambiguationData":[TD([[makeQuery(id+"F0.imprint","IMPRINT",EDGE,{"derivedFrom":subQ0}),1.0]])]});}
            var Q23;
            {var subQ0=sQuery(id+"F0.wireOp",EDGE,"E1053");Q23=makeQuery(id+"F0.imprint","IMPRINT",FACE,{"disambiguationData":[TD([[makeQuery(id+"F0.imprint","IMPRINT",EDGE,{"derivedFrom":subQ0}),1.0]])]});}
            var Q24;
            {var subQ0=sQuery(id+"F0.wireOp",EDGE,"E2611");Q24=makeQuery(id+"F0.imprint","IMPRINT",FACE,{"disambiguationData":[TD([[makeQuery(id+"F0.imprint","IMPRINT",EDGE,{"derivedFrom":subQ0}),1.0]])]});}
            var Q25;
            {var subQ0=sQuery(id+"F0.wireOp",EDGE,"E1159");Q25=makeQuery(id+"F0.imprint","IMPRINT",FACE,{"disambiguationData":[TD([[makeQuery(id+"F0.imprint","IMPRINT",EDGE,{"derivedFrom":subQ0}),1.0]])]});}
            var Q26;
            Q26=makeQuery(id+"F0.imprint","IMPRINT",FACE,{"disambiguationData":[TD([[makeQuery(id+"F0.imprint","IMPRINT",EDGE,{"derivedFrom":sQuery(id+"F0.wireOp",EDGE,"E1468")}),1.0]])]});
            var Q27;
            {var subQ0=sQuery(id+"F0.wireOp",EDGE,"E1265");Q27=makeQuery(id+"F0.imprint","IMPRINT",FACE,{"disambiguationData":[TD([[makeQuery(id+"F0.imprint","IMPRINT",EDGE,{"derivedFrom":subQ0}),1.0]])]});}
            var Q28;
            Q28=makeQuery(id+"F0.imprint","IMPRINT",FACE,{"disambiguationData":[TD([[makeQuery(id+"F0.imprint","IMPRINT",EDGE,{"derivedFrom":sQuery(id+"F0.wireOp",EDGE,"E2092")}),1.0]])]});
            var Q29;
            Q29=makeQuery(id+"F0.imprint","IMPRINT",FACE,{"disambiguationData":[TD([[makeQuery(id+"F0.imprint","IMPRINT",EDGE,{"derivedFrom":sQuery(id+"F0.wireOp",EDGE,"E2194")}),1.0]])]});
            var Q30;
            Q30=makeQuery(id+"F0.imprint","IMPRINT",FACE,{"disambiguationData":[TD([[makeQuery(id+"F0.imprint","IMPRINT",EDGE,{"derivedFrom":sQuery(id+"F0.wireOp",EDGE,"E2500")}),1.0]])]});
            var Q31;
            {var subQ0=sQuery(id+"F0.wireOp",EDGE,"E2296");Q31=makeQuery(id+"F0.imprint","IMPRINT",FACE,{"disambiguationData":[TD([[makeQuery(id+"F0.imprint","IMPRINT",EDGE,{"derivedFrom":subQ0}),1.0]])]});}
            var Q32;
            Q32=makeQuery(id+"F0.imprint","IMPRINT",FACE,{"disambiguationData":[TD([[makeQuery(id+"F0.imprint","IMPRINT",EDGE,{"derivedFrom":sQuery(id+"F0.wireOp",EDGE,"E2398")}),1.0]])]});
            var Q33;
            Q33=makeQuery(id+"F0.imprint","IMPRINT",FACE,{"disambiguationData":[TD([[makeQuery(id+"F0.imprint","IMPRINT",EDGE,{"derivedFrom":sQuery(id+"F0.wireOp",EDGE,"E2920")}),1.0]])]});
            var Q34;
            {var subQ0=sQuery(id+"F0.wireOp",EDGE,"E2717");Q34=makeQuery(id+"F0.imprint","IMPRINT",FACE,{"disambiguationData":[TD([[makeQuery(id+"F0.imprint","IMPRINT",EDGE,{"derivedFrom":subQ0}),1.0]])]});}
            var Q35;
            {var subQ0=sQuery(id+"F0.wireOp",EDGE,"E1685");Q35=makeQuery(id+"F0.imprint","IMPRINT",FACE,{"disambiguationData":[TD([[makeQuery(id+"F0.imprint","IMPRINT",EDGE,{"derivedFrom":subQ0}),1.0]])]});}
            var Q36;
            {var subQ0=sQuery(id+"F0.wireOp",EDGE,"E1579");Q36=makeQuery(id+"F0.imprint","IMPRINT",FACE,{"disambiguationData":[TD([[makeQuery(id+"F0.imprint","IMPRINT",EDGE,{"derivedFrom":subQ0}),1.0]])]});}
            var Q37;
            {var subQ0=sQuery(id+"F0.wireOp",EDGE,"E1791");Q37=makeQuery(id+"F0.imprint","IMPRINT",FACE,{"disambiguationData":[TD([[makeQuery(id+"F0.imprint","IMPRINT",EDGE,{"derivedFrom":subQ0}),1.0]])]});}
            var Q38;
            {var subQ0=sQuery(id+"F0.wireOp",EDGE,"E1473");Q38=makeQuery(id+"F0.imprint","IMPRINT",FACE,{"disambiguationData":[TD([[makeQuery(id+"F0.imprint","IMPRINT",EDGE,{"derivedFrom":subQ0}),1.0]])]});}
            var Q39;
            {var subQ0=sQuery(id+"F0.wireOp",EDGE,"E1367");Q39=makeQuery(id+"F0.imprint","IMPRINT",FACE,{"disambiguationData":[TD([[makeQuery(id+"F0.imprint","IMPRINT",EDGE,{"derivedFrom":subQ0}),1.0]])]});}
            var Q40;
            Q40=makeQuery(id+"F0.imprint","IMPRINT",FACE,{"disambiguationData":[TD([[makeQuery(id+"F0.imprint","IMPRINT",EDGE,{"derivedFrom":sQuery(id+"F0.wireOp",EDGE,"E1574")}),1.0]])]});
            var Q41;
            Q41=makeQuery(id+"F0.imprint","IMPRINT",FACE,{"disambiguationData":[TD([[makeQuery(id+"F0.imprint","IMPRINT",EDGE,{"derivedFrom":sQuery(id+"F0.wireOp",EDGE,"E1892")}),1.0]])]});
            var Q42;
            {var subQ0=sQuery(id+"F0.wireOp",EDGE,"E1680");Q42=makeQuery(id+"F0.imprint","IMPRINT",FACE,{"disambiguationData":[TD([[makeQuery(id+"F0.imprint","IMPRINT",EDGE,{"derivedFrom":subQ0}),1.0]])]});}
            var Q43;
            Q43=makeQuery(id+"F0.imprint","IMPRINT",FACE,{"disambiguationData":[TD([[makeQuery(id+"F0.imprint","IMPRINT",EDGE,{"derivedFrom":sQuery(id+"F0.wireOp",EDGE,"E1786")}),1.0]])]});
            var Q44;
            Q44=makeQuery(id+"F0.imprint","IMPRINT",FACE,{"disambiguationData":[TD([[makeQuery(id+"F0.imprint","IMPRINT",EDGE,{"derivedFrom":sQuery(id+"F0.wireOp",EDGE,"E2818")}),1.0]])]});
            extrude(context, id + "F4", {"entities" : qUnion([Q0, Q1, Q2, Q3, Q4, Q5, Q6, Q7, Q8, Q9, Q10, Q11, Q12, Q13, Q14, Q15, Q16, Q17, Q18, Q19, Q20, Q21, Q22, Q23, Q24, Q25, Q26, Q27, Q28, Q29, Q30, Q31, Q32, Q33, Q34, Q35, Q36, Q37, Q38, Q39, Q40, Q41, Q42, Q43, Q44]), "depth" : 0.6 * mm, "offsetDistance" : 25 * mm});
        }
    });
